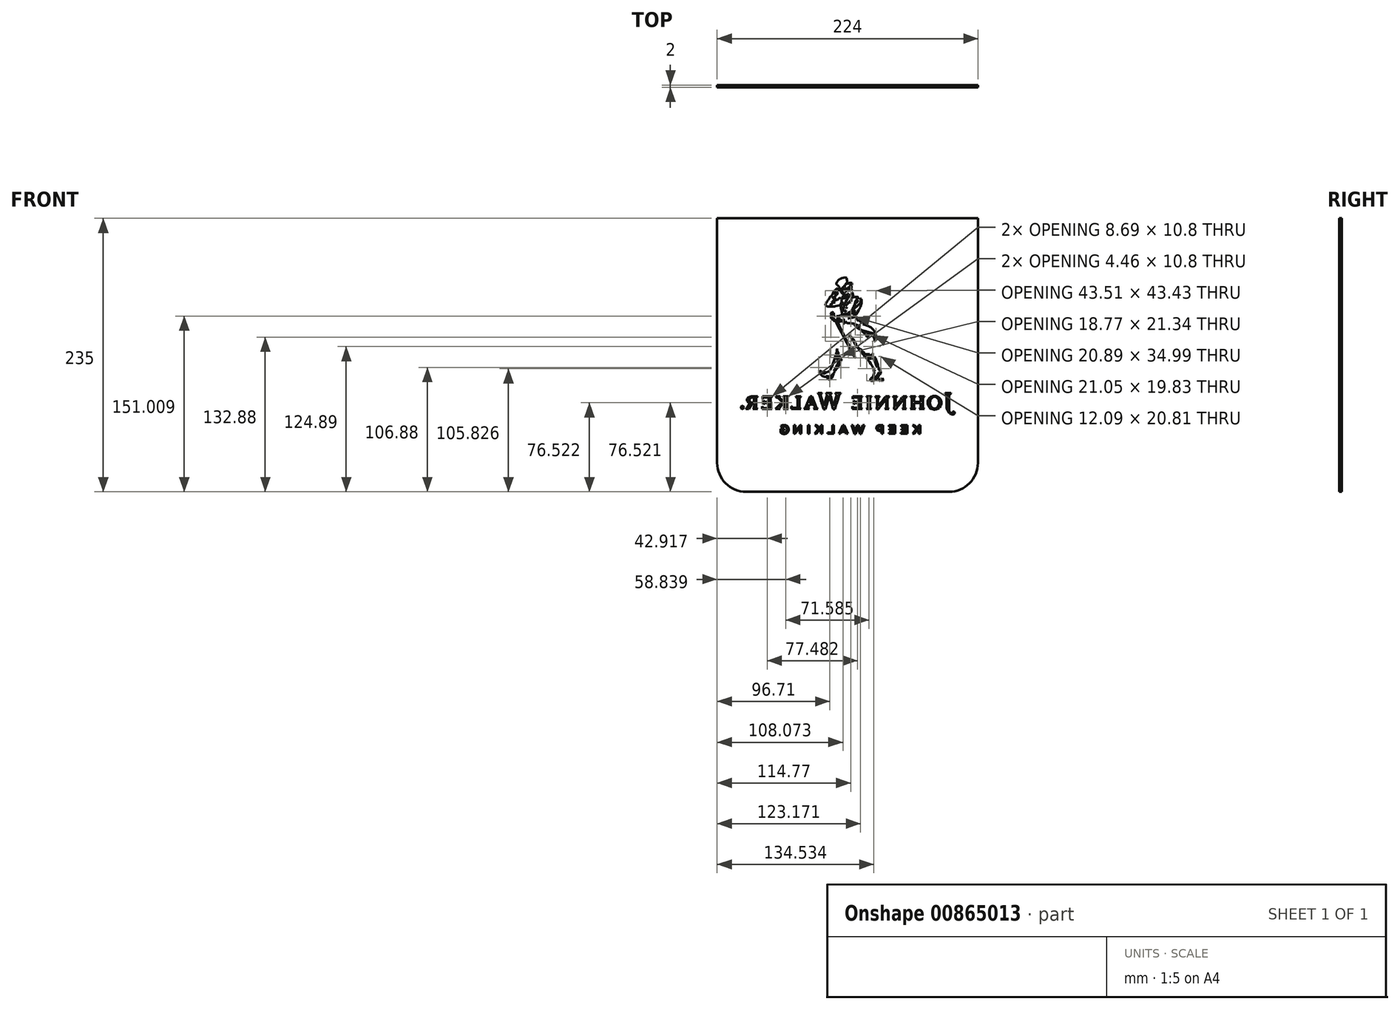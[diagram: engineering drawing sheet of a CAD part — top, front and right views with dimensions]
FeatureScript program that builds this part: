
annotation { "Feature Type Name" : "Feature", "Feature Type Description" : "" }
export const myFeature = defineFeature(function(context is Context, id is Id, definition is map)
    precondition{}
    {
        {
            var Q0;
            Q0=qCreatedBy(makeId("Front.planeOp"),FACE);
            var sketch = newSketch(context, id + "F0", { "sketchPlane" : qUnion([Q0])});
            skLineSegment(sketch, "E0", {"start": v(0.13, 0) * mm, "end": v(-86.87, 0) * mm});
            skLineSegment(sketch, "E1", {"start": v(0.13, 0) * mm, "end": v(87.13, 0) * mm});
            skLineSegment(sketch, "E2", {"start": v(0.13, 235) * mm, "end": v(-111.87, 235) * mm});
            skLineSegment(sketch, "E3", {"start": v(-111.87, 235) * mm, "end": v(-111.87, 25) * mm});
            skLineSegment(sketch, "E4", {"start": v(0.13, 235) * mm, "end": v(112.13, 235) * mm});
            skLineSegment(sketch, "E5", {"start": v(112.13, 235) * mm, "end": v(112.13, 25) * mm});
            skArc(sketch, "E6", {"start": v(-111.87, 25) * mm, "mid": v(-104.54, 7.32) * mm, "end": v(-86.87, 0) * mm});
            skArc(sketch, "E7", {"start": v(87.13, 0) * mm, "mid": v(104.81, 7.32) * mm, "end": v(112.13, 25) * mm});
            skSolve(sketch);
        }
        {
            var Q0;
            Q0=qCreatedBy(makeId("Front.planeOp"),FACE);
            var sketch = newSketch(context, id + "F1", { "sketchPlane" : qUnion([Q0])});
            skLineSegment(sketch, "E8", {"start": v(-58.86, 54.13) * mm, "end": v(-55.76, 57.34) * mm});
            skLineSegment(sketch, "E9", {"start": v(-55.76, 57.34) * mm, "end": v(-57.37, 57.34) * mm});
            skLineSegment(sketch, "E10", {"start": v(-57.37, 57.34) * mm, "end": v(-60.91, 53.59) * mm});
            skLineSegment(sketch, "E11", {"start": v(-60.91, 53.59) * mm, "end": v(-60.91, 57.34) * mm});
            skLineSegment(sketch, "E12", {"start": v(-60.91, 57.34) * mm, "end": v(-62.22, 57.34) * mm});
            skLineSegment(sketch, "E13", {"start": v(-62.22, 57.34) * mm, "end": v(-62.22, 49.88) * mm});
            skLineSegment(sketch, "E14", {"start": v(-62.22, 49.88) * mm, "end": v(-60.91, 49.88) * mm});
            skLineSegment(sketch, "E15", {"start": v(-60.91, 49.88) * mm, "end": v(-60.91, 52.04) * mm});
            skLineSegment(sketch, "E16", {"start": v(-60.91, 52.04) * mm, "end": v(-59.75, 53.24) * mm});
            skLineSegment(sketch, "E17", {"start": v(-59.75, 53.24) * mm, "end": v(-57.2, 49.88) * mm});
            skLineSegment(sketch, "E18", {"start": v(-57.2, 49.88) * mm, "end": v(-55.62, 49.88) * mm});
            skLineSegment(sketch, "E19", {"start": v(-55.62, 49.88) * mm, "end": v(-58.86, 54.13) * mm});
            skLineSegment(sketch, "E20", {"start": v(-45.72, 57.34) * mm, "end": v(-51.25, 57.34) * mm});
            skLineSegment(sketch, "E21", {"start": v(-51.25, 57.34) * mm, "end": v(-51.25, 49.88) * mm});
            skLineSegment(sketch, "E22", {"start": v(-51.25, 49.88) * mm, "end": v(-45.67, 49.88) * mm});
            skLineSegment(sketch, "E23", {"start": v(-45.67, 49.88) * mm, "end": v(-45.67, 51.05) * mm});
            skLineSegment(sketch, "E24", {"start": v(-45.67, 51.05) * mm, "end": v(-49.94, 51.05) * mm});
            skLineSegment(sketch, "E25", {"start": v(-49.94, 51.05) * mm, "end": v(-49.94, 53.06) * mm});
            skLineSegment(sketch, "E26", {"start": v(-49.94, 53.06) * mm, "end": v(-46.2, 53.06) * mm});
            skLineSegment(sketch, "E27", {"start": v(-46.2, 53.06) * mm, "end": v(-46.2, 54.23) * mm});
            skLineSegment(sketch, "E28", {"start": v(-46.2, 54.23) * mm, "end": v(-49.94, 54.23) * mm});
            skLineSegment(sketch, "E29", {"start": v(-49.94, 54.23) * mm, "end": v(-49.94, 56.17) * mm});
            skLineSegment(sketch, "E30", {"start": v(-49.94, 56.17) * mm, "end": v(-45.72, 56.17) * mm});
            skLineSegment(sketch, "E31", {"start": v(-45.72, 56.17) * mm, "end": v(-45.72, 57.34) * mm});
            skLineSegment(sketch, "E32", {"start": v(-35.3, 57.34) * mm, "end": v(-40.82, 57.34) * mm});
            skLineSegment(sketch, "E33", {"start": v(-40.82, 57.34) * mm, "end": v(-40.82, 49.88) * mm});
            skLineSegment(sketch, "E34", {"start": v(-40.82, 49.88) * mm, "end": v(-35.24, 49.88) * mm});
            skLineSegment(sketch, "E35", {"start": v(-35.24, 49.88) * mm, "end": v(-35.24, 51.05) * mm});
            skLineSegment(sketch, "E36", {"start": v(-35.24, 51.05) * mm, "end": v(-39.52, 51.05) * mm});
            skLineSegment(sketch, "E37", {"start": v(-39.52, 51.05) * mm, "end": v(-39.52, 53.06) * mm});
            skLineSegment(sketch, "E38", {"start": v(-39.52, 53.06) * mm, "end": v(-35.77, 53.06) * mm});
            skLineSegment(sketch, "E39", {"start": v(-35.77, 53.06) * mm, "end": v(-35.77, 54.23) * mm});
            skLineSegment(sketch, "E40", {"start": v(-35.77, 54.23) * mm, "end": v(-39.52, 54.23) * mm});
            skLineSegment(sketch, "E41", {"start": v(-39.52, 54.23) * mm, "end": v(-39.52, 56.17) * mm});
            skLineSegment(sketch, "E42", {"start": v(-39.52, 56.17) * mm, "end": v(-35.3, 56.17) * mm});
            skLineSegment(sketch, "E43", {"start": v(-35.3, 56.17) * mm, "end": v(-35.3, 57.34) * mm});
            skLineSegment(sketch, "E44", {"start": v(-24.63, 54.83) * mm, "end": v(-24.63, 55.1) * mm});
            skLineSegment(sketch, "E45", {"start": v(-24.63, 55.1) * mm, "end": v(-24.83, 55.87) * mm});
            skLineSegment(sketch, "E46", {"start": v(-24.83, 55.87) * mm, "end": v(-25.4, 56.66) * mm});
            skLineSegment(sketch, "E47", {"start": v(-25.4, 56.66) * mm, "end": v(-26.28, 57.16) * mm});
            skLineSegment(sketch, "E48", {"start": v(-26.28, 57.16) * mm, "end": v(-27.17, 57.34) * mm});
            skLineSegment(sketch, "E49", {"start": v(-27.17, 57.34) * mm, "end": v(-27.46, 57.34) * mm});
            skLineSegment(sketch, "E50", {"start": v(-27.46, 57.34) * mm, "end": v(-30.4, 57.34) * mm});
            skLineSegment(sketch, "E51", {"start": v(-30.4, 57.34) * mm, "end": v(-30.4, 49.88) * mm});
            skLineSegment(sketch, "E52", {"start": v(-30.4, 49.88) * mm, "end": v(-29.09, 49.88) * mm});
            skLineSegment(sketch, "E53", {"start": v(-29.09, 49.88) * mm, "end": v(-29.09, 52.28) * mm});
            skLineSegment(sketch, "E54", {"start": v(-29.09, 52.28) * mm, "end": v(-27.6, 52.28) * mm});
            skLineSegment(sketch, "E55", {"start": v(-27.6, 52.28) * mm, "end": v(-27.32, 52.28) * mm});
            skLineSegment(sketch, "E56", {"start": v(-27.32, 52.28) * mm, "end": v(-26.45, 52.44) * mm});
            skLineSegment(sketch, "E57", {"start": v(-26.45, 52.44) * mm, "end": v(-25.5, 52.93) * mm});
            skLineSegment(sketch, "E58", {"start": v(-25.5, 52.93) * mm, "end": v(-24.86, 53.73) * mm});
            skLineSegment(sketch, "E59", {"start": v(-24.86, 53.73) * mm, "end": v(-24.63, 54.56) * mm});
            skLineSegment(sketch, "E60", {"start": v(-24.63, 54.56) * mm, "end": v(-24.63, 54.83) * mm});
            skLineSegment(sketch, "E61", {"start": v(-25.96, 54.8) * mm, "end": v(-25.96, 54.67) * mm});
            skLineSegment(sketch, "E62", {"start": v(-25.96, 54.67) * mm, "end": v(-26.07, 54.26) * mm});
            skLineSegment(sketch, "E63", {"start": v(-26.07, 54.26) * mm, "end": v(-26.39, 53.83) * mm});
            skLineSegment(sketch, "E64", {"start": v(-26.39, 53.83) * mm, "end": v(-26.9, 53.56) * mm});
            skLineSegment(sketch, "E65", {"start": v(-26.9, 53.56) * mm, "end": v(-27.4, 53.46) * mm});
            skLineSegment(sketch, "E66", {"start": v(-27.4, 53.46) * mm, "end": v(-27.57, 53.46) * mm});
            skLineSegment(sketch, "E67", {"start": v(-27.57, 53.46) * mm, "end": v(-29.09, 53.46) * mm});
            skLineSegment(sketch, "E68", {"start": v(-29.09, 53.46) * mm, "end": v(-29.09, 56.14) * mm});
            skLineSegment(sketch, "E69", {"start": v(-29.09, 56.14) * mm, "end": v(-27.57, 56.14) * mm});
            skLineSegment(sketch, "E70", {"start": v(-27.57, 56.14) * mm, "end": v(-27.4, 56.14) * mm});
            skLineSegment(sketch, "E71", {"start": v(-27.4, 56.14) * mm, "end": v(-26.9, 56.06) * mm});
            skLineSegment(sketch, "E72", {"start": v(-26.9, 56.06) * mm, "end": v(-26.4, 55.8) * mm});
            skLineSegment(sketch, "E73", {"start": v(-26.4, 55.8) * mm, "end": v(-26.07, 55.39) * mm});
            skLineSegment(sketch, "E74", {"start": v(-26.07, 55.39) * mm, "end": v(-25.96, 54.95) * mm});
            skLineSegment(sketch, "E75", {"start": v(-25.96, 54.95) * mm, "end": v(-25.96, 54.8) * mm});
            skLineSegment(sketch, "E76", {"start": v(-11.08, 51.8) * mm, "end": v(-12.86, 57.34) * mm});
            skLineSegment(sketch, "E77", {"start": v(-12.86, 57.34) * mm, "end": v(-14.27, 57.34) * mm});
            skLineSegment(sketch, "E78", {"start": v(-14.27, 57.34) * mm, "end": v(-11.68, 49.83) * mm});
            skLineSegment(sketch, "E79", {"start": v(-11.68, 49.83) * mm, "end": v(-10.55, 49.83) * mm});
            skLineSegment(sketch, "E80", {"start": v(-10.55, 49.83) * mm, "end": v(-8.71, 55.18) * mm});
            skLineSegment(sketch, "E81", {"start": v(-8.71, 55.18) * mm, "end": v(-6.88, 49.83) * mm});
            skLineSegment(sketch, "E82", {"start": v(-6.88, 49.83) * mm, "end": v(-5.75, 49.83) * mm});
            skLineSegment(sketch, "E83", {"start": v(-5.75, 49.83) * mm, "end": v(-3.15, 57.34) * mm});
            skLineSegment(sketch, "E84", {"start": v(-3.15, 57.34) * mm, "end": v(-4.53, 57.34) * mm});
            skLineSegment(sketch, "E85", {"start": v(-4.53, 57.34) * mm, "end": v(-6.3, 51.8) * mm});
            skLineSegment(sketch, "E86", {"start": v(-6.3, 51.8) * mm, "end": v(-8.14, 57.36) * mm});
            skLineSegment(sketch, "E87", {"start": v(-8.14, 57.36) * mm, "end": v(-9.25, 57.36) * mm});
            skLineSegment(sketch, "E88", {"start": v(-9.25, 57.36) * mm, "end": v(-11.08, 51.8) * mm});
            skLineSegment(sketch, "E89", {"start": v(4.31, 57.39) * mm, "end": v(3.1, 57.39) * mm});
            skLineSegment(sketch, "E90", {"start": v(3.1, 57.39) * mm, "end": v(-0.18, 49.88) * mm});
            skLineSegment(sketch, "E91", {"start": v(-0.18, 49.88) * mm, "end": v(1.16, 49.88) * mm});
            skLineSegment(sketch, "E92", {"start": v(1.16, 49.88) * mm, "end": v(1.93, 51.68) * mm});
            skLineSegment(sketch, "E93", {"start": v(1.93, 51.68) * mm, "end": v(5.46, 51.68) * mm});
            skLineSegment(sketch, "E94", {"start": v(5.46, 51.68) * mm, "end": v(6.2, 49.88) * mm});
            skLineSegment(sketch, "E95", {"start": v(6.2, 49.88) * mm, "end": v(7.6, 49.88) * mm});
            skLineSegment(sketch, "E96", {"start": v(7.6, 49.88) * mm, "end": v(4.31, 57.39) * mm});
            skLineSegment(sketch, "E97", {"start": v(4.97, 52.84) * mm, "end": v(2.4, 52.84) * mm});
            skLineSegment(sketch, "E98", {"start": v(2.4, 52.84) * mm, "end": v(3.69, 55.82) * mm});
            skLineSegment(sketch, "E99", {"start": v(3.69, 55.82) * mm, "end": v(4.97, 52.84) * mm});
            skLineSegment(sketch, "E100", {"start": v(12.05, 49.88) * mm, "end": v(17.28, 49.88) * mm});
            skLineSegment(sketch, "E101", {"start": v(17.28, 49.88) * mm, "end": v(17.28, 51.07) * mm});
            skLineSegment(sketch, "E102", {"start": v(17.28, 51.07) * mm, "end": v(13.36, 51.07) * mm});
            skLineSegment(sketch, "E103", {"start": v(13.36, 51.07) * mm, "end": v(13.36, 57.34) * mm});
            skLineSegment(sketch, "E104", {"start": v(13.36, 57.34) * mm, "end": v(12.05, 57.34) * mm});
            skLineSegment(sketch, "E105", {"start": v(12.05, 57.34) * mm, "end": v(12.05, 49.88) * mm});
            skLineSegment(sketch, "E106", {"start": v(25.13, 54.13) * mm, "end": v(28.23, 57.34) * mm});
            skLineSegment(sketch, "E107", {"start": v(28.23, 57.34) * mm, "end": v(26.63, 57.34) * mm});
            skLineSegment(sketch, "E108", {"start": v(26.63, 57.34) * mm, "end": v(23.08, 53.59) * mm});
            skLineSegment(sketch, "E109", {"start": v(23.08, 53.59) * mm, "end": v(23.08, 57.34) * mm});
            skLineSegment(sketch, "E110", {"start": v(23.08, 57.34) * mm, "end": v(21.77, 57.34) * mm});
            skLineSegment(sketch, "E111", {"start": v(21.77, 57.34) * mm, "end": v(21.77, 49.88) * mm});
            skLineSegment(sketch, "E112", {"start": v(21.77, 49.88) * mm, "end": v(23.08, 49.88) * mm});
            skLineSegment(sketch, "E113", {"start": v(23.08, 49.88) * mm, "end": v(23.08, 52.04) * mm});
            skLineSegment(sketch, "E114", {"start": v(23.08, 52.04) * mm, "end": v(24.24, 53.24) * mm});
            skLineSegment(sketch, "E115", {"start": v(24.24, 53.24) * mm, "end": v(26.79, 49.88) * mm});
            skLineSegment(sketch, "E116", {"start": v(26.79, 49.88) * mm, "end": v(28.37, 49.88) * mm});
            skLineSegment(sketch, "E117", {"start": v(28.37, 49.88) * mm, "end": v(25.13, 54.13) * mm});
            skLineSegment(sketch, "E118", {"start": v(33, 49.88) * mm, "end": v(34.31, 49.88) * mm});
            skLineSegment(sketch, "E119", {"start": v(34.31, 49.88) * mm, "end": v(34.31, 57.34) * mm});
            skLineSegment(sketch, "E120", {"start": v(34.31, 57.34) * mm, "end": v(33, 57.34) * mm});
            skLineSegment(sketch, "E121", {"start": v(33, 57.34) * mm, "end": v(33, 49.88) * mm});
            skLineSegment(sketch, "E122", {"start": v(44.97, 52.18) * mm, "end": v(40.98, 57.34) * mm});
            skLineSegment(sketch, "E123", {"start": v(40.98, 57.34) * mm, "end": v(39.76, 57.34) * mm});
            skLineSegment(sketch, "E124", {"start": v(39.76, 57.34) * mm, "end": v(39.76, 49.88) * mm});
            skLineSegment(sketch, "E125", {"start": v(39.76, 49.88) * mm, "end": v(41.05, 49.88) * mm});
            skLineSegment(sketch, "E126", {"start": v(41.05, 49.88) * mm, "end": v(41.05, 55.18) * mm});
            skLineSegment(sketch, "E127", {"start": v(41.05, 55.18) * mm, "end": v(45.16, 49.88) * mm});
            skLineSegment(sketch, "E128", {"start": v(45.16, 49.88) * mm, "end": v(46.26, 49.88) * mm});
            skLineSegment(sketch, "E129", {"start": v(46.26, 49.88) * mm, "end": v(46.26, 57.34) * mm});
            skLineSegment(sketch, "E130", {"start": v(46.26, 57.34) * mm, "end": v(44.97, 57.34) * mm});
            skLineSegment(sketch, "E131", {"start": v(44.97, 57.34) * mm, "end": v(44.97, 52.18) * mm});
            skLineSegment(sketch, "E132", {"start": v(57.65, 50.91) * mm, "end": v(57.65, 54.05) * mm});
            skLineSegment(sketch, "E133", {"start": v(57.65, 54.05) * mm, "end": v(54.48, 54.05) * mm});
            skLineSegment(sketch, "E134", {"start": v(54.48, 54.05) * mm, "end": v(54.48, 52.9) * mm});
            skLineSegment(sketch, "E135", {"start": v(54.48, 52.9) * mm, "end": v(56.39, 52.9) * mm});
            skLineSegment(sketch, "E136", {"start": v(56.39, 52.9) * mm, "end": v(56.39, 51.51) * mm});
            skLineSegment(sketch, "E137", {"start": v(56.39, 51.51) * mm, "end": v(56.27, 51.43) * mm});
            skLineSegment(sketch, "E138", {"start": v(56.27, 51.43) * mm, "end": v(55.58, 51.1) * mm});
            skLineSegment(sketch, "E139", {"start": v(55.58, 51.1) * mm, "end": v(54.83, 50.95) * mm});
            skLineSegment(sketch, "E140", {"start": v(54.83, 50.95) * mm, "end": v(54.59, 50.95) * mm});
            skLineSegment(sketch, "E141", {"start": v(54.59, 50.95) * mm, "end": v(54.33, 50.95) * mm});
            skLineSegment(sketch, "E142", {"start": v(54.33, 50.95) * mm, "end": v(53.55, 51.15) * mm});
            skLineSegment(sketch, "E143", {"start": v(53.55, 51.15) * mm, "end": v(52.75, 51.7) * mm});
            skLineSegment(sketch, "E144", {"start": v(52.75, 51.7) * mm, "end": v(52.23, 52.55) * mm});
            skLineSegment(sketch, "E145", {"start": v(52.23, 52.55) * mm, "end": v(52.05, 53.35) * mm});
            skLineSegment(sketch, "E146", {"start": v(52.05, 53.35) * mm, "end": v(52.05, 53.62) * mm});
            skLineSegment(sketch, "E147", {"start": v(52.05, 53.62) * mm, "end": v(52.05, 53.88) * mm});
            skLineSegment(sketch, "E148", {"start": v(52.05, 53.88) * mm, "end": v(52.23, 54.64) * mm});
            skLineSegment(sketch, "E149", {"start": v(52.23, 54.64) * mm, "end": v(52.74, 55.49) * mm});
            skLineSegment(sketch, "E150", {"start": v(52.74, 55.49) * mm, "end": v(53.5, 56.05) * mm});
            skLineSegment(sketch, "E151", {"start": v(53.5, 56.05) * mm, "end": v(54.23, 56.26) * mm});
            skLineSegment(sketch, "E152", {"start": v(54.23, 56.26) * mm, "end": v(54.47, 56.26) * mm});
            skLineSegment(sketch, "E153", {"start": v(54.47, 56.26) * mm, "end": v(54.76, 56.26) * mm});
            skLineSegment(sketch, "E154", {"start": v(54.76, 56.26) * mm, "end": v(55.65, 56.05) * mm});
            skLineSegment(sketch, "E155", {"start": v(55.65, 56.05) * mm, "end": v(56.41, 55.59) * mm});
            skLineSegment(sketch, "E156", {"start": v(56.41, 55.59) * mm, "end": v(56.56, 55.46) * mm});
            skLineSegment(sketch, "E157", {"start": v(56.56, 55.46) * mm, "end": v(57.38, 56.46) * mm});
            skLineSegment(sketch, "E158", {"start": v(57.38, 56.46) * mm, "end": v(57.2, 56.62) * mm});
            skLineSegment(sketch, "E159", {"start": v(57.2, 56.62) * mm, "end": v(56.15, 57.2) * mm});
            skLineSegment(sketch, "E160", {"start": v(56.15, 57.2) * mm, "end": v(54.93, 57.47) * mm});
            skLineSegment(sketch, "E161", {"start": v(54.93, 57.47) * mm, "end": v(54.52, 57.47) * mm});
            skLineSegment(sketch, "E162", {"start": v(54.52, 57.47) * mm, "end": v(54.13, 57.47) * mm});
            skLineSegment(sketch, "E163", {"start": v(54.13, 57.47) * mm, "end": v(52.97, 57.16) * mm});
            skLineSegment(sketch, "E164", {"start": v(52.97, 57.16) * mm, "end": v(51.76, 56.32) * mm});
            skLineSegment(sketch, "E165", {"start": v(51.76, 56.32) * mm, "end": v(50.96, 55.09) * mm});
            skLineSegment(sketch, "E166", {"start": v(50.96, 55.09) * mm, "end": v(50.68, 53.97) * mm});
            skLineSegment(sketch, "E167", {"start": v(50.68, 53.97) * mm, "end": v(50.68, 53.6) * mm});
            skLineSegment(sketch, "E168", {"start": v(50.68, 53.6) * mm, "end": v(50.68, 53.22) * mm});
            skLineSegment(sketch, "E169", {"start": v(50.68, 53.22) * mm, "end": v(50.95, 52.08) * mm});
            skLineSegment(sketch, "E170", {"start": v(50.95, 52.08) * mm, "end": v(51.73, 50.86) * mm});
            skLineSegment(sketch, "E171", {"start": v(51.73, 50.86) * mm, "end": v(52.95, 50.05) * mm});
            skLineSegment(sketch, "E172", {"start": v(52.95, 50.05) * mm, "end": v(54.14, 49.76) * mm});
            skLineSegment(sketch, "E173", {"start": v(54.14, 49.76) * mm, "end": v(54.54, 49.76) * mm});
            skLineSegment(sketch, "E174", {"start": v(54.54, 49.76) * mm, "end": v(54.99, 49.76) * mm});
            skLineSegment(sketch, "E175", {"start": v(54.99, 49.76) * mm, "end": v(56.32, 50.1) * mm});
            skLineSegment(sketch, "E176", {"start": v(56.32, 50.1) * mm, "end": v(57.47, 50.76) * mm});
            skLineSegment(sketch, "E177", {"start": v(57.47, 50.76) * mm, "end": v(57.65, 50.91) * mm});
            skLineSegment(sketch, "E178", {"start": v(-27.51, 81.88) * mm, "end": v(-26.05, 80.76) * mm});
            skLineSegment(sketch, "E179", {"start": v(-26.05, 80.76) * mm, "end": v(-26.05, 80.5) * mm});
            skLineSegment(sketch, "E180", {"start": v(-26.05, 80.5) * mm, "end": v(-26, 77.76) * mm});
            skLineSegment(sketch, "E181", {"start": v(-26, 77.76) * mm, "end": v(-26, 77.46) * mm});
            skLineSegment(sketch, "E182", {"start": v(-26, 77.46) * mm, "end": v(-26, 77.16) * mm});
            skLineSegment(sketch, "E183", {"start": v(-26, 77.16) * mm, "end": v(-25.98, 74.54) * mm});
            skLineSegment(sketch, "E184", {"start": v(-25.98, 74.54) * mm, "end": v(-25.98, 73.67) * mm});
            skLineSegment(sketch, "E185", {"start": v(-25.98, 73.67) * mm, "end": v(-26.2, 73.96) * mm});
            skLineSegment(sketch, "E186", {"start": v(-26.2, 73.96) * mm, "end": v(-27.25, 75.3) * mm});
            skLineSegment(sketch, "E187", {"start": v(-27.25, 75.3) * mm, "end": v(-28.21, 76.5) * mm});
            skLineSegment(sketch, "E188", {"start": v(-28.21, 76.5) * mm, "end": v(-28.4, 76.74) * mm});
            skLineSegment(sketch, "E189", {"start": v(-28.4, 76.74) * mm, "end": v(-28.57, 76.96) * mm});
            skLineSegment(sketch, "E190", {"start": v(-28.57, 76.96) * mm, "end": v(-30.17, 78.96) * mm});
            skLineSegment(sketch, "E191", {"start": v(-30.17, 78.96) * mm, "end": v(-30.3, 79.12) * mm});
            skLineSegment(sketch, "E192", {"start": v(-30.3, 79.12) * mm, "end": v(-30.45, 79.3) * mm});
            skLineSegment(sketch, "E193", {"start": v(-30.45, 79.3) * mm, "end": v(-31.63, 80.77) * mm});
            skLineSegment(sketch, "E194", {"start": v(-31.63, 80.77) * mm, "end": v(-31.72, 80.9) * mm});
            skLineSegment(sketch, "E195", {"start": v(-31.72, 80.9) * mm, "end": v(-31.82, 81) * mm});
            skLineSegment(sketch, "E196", {"start": v(-31.82, 81) * mm, "end": v(-32.2, 81.51) * mm});
            skLineSegment(sketch, "E197", {"start": v(-32.2, 81.51) * mm, "end": v(-32.48, 81.93) * mm});
            skLineSegment(sketch, "E198", {"start": v(-32.48, 81.93) * mm, "end": v(-32.52, 82) * mm});
            skLineSegment(sketch, "E199", {"start": v(-32.52, 82) * mm, "end": v(-35.74, 82) * mm});
            skLineSegment(sketch, "E200", {"start": v(-35.74, 82) * mm, "end": v(-35.74, 81.88) * mm});
            skLineSegment(sketch, "E201", {"start": v(-35.74, 81.88) * mm, "end": v(-34.22, 80.8) * mm});
            skLineSegment(sketch, "E202", {"start": v(-34.22, 80.8) * mm, "end": v(-34.2, 79.93) * mm});
            skLineSegment(sketch, "E203", {"start": v(-34.2, 79.93) * mm, "end": v(-34.14, 76.09) * mm});
            skLineSegment(sketch, "E204", {"start": v(-34.14, 76.09) * mm, "end": v(-34.2, 72.88) * mm});
            skLineSegment(sketch, "E205", {"start": v(-34.2, 72.88) * mm, "end": v(-34.22, 72.34) * mm});
            skLineSegment(sketch, "E206", {"start": v(-34.22, 72.34) * mm, "end": v(-35.49, 71.3) * mm});
            skLineSegment(sketch, "E207", {"start": v(-35.49, 71.3) * mm, "end": v(-35.49, 71.15) * mm});
            skLineSegment(sketch, "E208", {"start": v(-35.49, 71.15) * mm, "end": v(-31.79, 71.15) * mm});
            skLineSegment(sketch, "E209", {"start": v(-31.79, 71.15) * mm, "end": v(-31.79, 71.3) * mm});
            skLineSegment(sketch, "E210", {"start": v(-31.79, 71.3) * mm, "end": v(-33.18, 72.34) * mm});
            skLineSegment(sketch, "E211", {"start": v(-33.18, 72.34) * mm, "end": v(-33.18, 72.34) * mm});
            skLineSegment(sketch, "E212", {"start": v(-33.18, 72.34) * mm, "end": v(-33.2, 72.97) * mm});
            skLineSegment(sketch, "E213", {"start": v(-33.2, 72.97) * mm, "end": v(-33.3, 78.1) * mm});
            skLineSegment(sketch, "E214", {"start": v(-33.3, 78.1) * mm, "end": v(-33.3, 79.8) * mm});
            skLineSegment(sketch, "E215", {"start": v(-33.3, 79.8) * mm, "end": v(-26.91, 71.77) * mm});
            skLineSegment(sketch, "E216", {"start": v(-26.91, 71.77) * mm, "end": v(-26.9, 71.74) * mm});
            skLineSegment(sketch, "E217", {"start": v(-26.9, 71.74) * mm, "end": v(-26.65, 71.44) * mm});
            skLineSegment(sketch, "E218", {"start": v(-26.65, 71.44) * mm, "end": v(-26.62, 71.4) * mm});
            skLineSegment(sketch, "E219", {"start": v(-26.62, 71.4) * mm, "end": v(-26.6, 71.38) * mm});
            skLineSegment(sketch, "E220", {"start": v(-26.6, 71.38) * mm, "end": v(-26.47, 71.16) * mm});
            skLineSegment(sketch, "E221", {"start": v(-26.47, 71.16) * mm, "end": v(-26.47, 71.1) * mm});
            skLineSegment(sketch, "E222", {"start": v(-26.47, 71.1) * mm, "end": v(-25, 71.1) * mm});
            skLineSegment(sketch, "E223", {"start": v(-25, 71.1) * mm, "end": v(-25.01, 71.44) * mm});
            skLineSegment(sketch, "E224", {"start": v(-25.01, 71.44) * mm, "end": v(-25.13, 74.54) * mm});
            skLineSegment(sketch, "E225", {"start": v(-25.13, 74.54) * mm, "end": v(-25.13, 75.58) * mm});
            skLineSegment(sketch, "E226", {"start": v(-25.13, 75.58) * mm, "end": v(-25.14, 75.97) * mm});
            skLineSegment(sketch, "E227", {"start": v(-25.14, 75.97) * mm, "end": v(-25.09, 80.3) * mm});
            skLineSegment(sketch, "E228", {"start": v(-25.09, 80.3) * mm, "end": v(-25.07, 80.76) * mm});
            skLineSegment(sketch, "E229", {"start": v(-25.07, 80.76) * mm, "end": v(-23.8, 81.88) * mm});
            skLineSegment(sketch, "E230", {"start": v(-23.8, 81.88) * mm, "end": v(-23.8, 82) * mm});
            skLineSegment(sketch, "E231", {"start": v(-23.8, 82) * mm, "end": v(-27.51, 82) * mm});
            skLineSegment(sketch, "E232", {"start": v(-27.51, 82) * mm, "end": v(-27.51, 81.88) * mm});
            skLineSegment(sketch, "E233", {"start": v(-17.36, 81) * mm, "end": v(-16.11, 81.88) * mm});
            skLineSegment(sketch, "E234", {"start": v(-16.11, 81.88) * mm, "end": v(-16.11, 81.99) * mm});
            skLineSegment(sketch, "E235", {"start": v(-16.11, 81.99) * mm, "end": v(-20.47, 81.99) * mm});
            skLineSegment(sketch, "E236", {"start": v(-20.47, 81.99) * mm, "end": v(-20.47, 81.88) * mm});
            skLineSegment(sketch, "E237", {"start": v(-20.47, 81.88) * mm, "end": v(-19.22, 81) * mm});
            skLineSegment(sketch, "E238", {"start": v(-19.22, 81) * mm, "end": v(-19.22, 80.28) * mm});
            skLineSegment(sketch, "E239", {"start": v(-19.22, 80.28) * mm, "end": v(-19.22, 72.97) * mm});
            skLineSegment(sketch, "E240", {"start": v(-19.22, 72.97) * mm, "end": v(-19.22, 72.23) * mm});
            skLineSegment(sketch, "E241", {"start": v(-19.22, 72.23) * mm, "end": v(-20.51, 71.32) * mm});
            skLineSegment(sketch, "E242", {"start": v(-20.51, 71.32) * mm, "end": v(-20.51, 71.19) * mm});
            skLineSegment(sketch, "E243", {"start": v(-20.51, 71.19) * mm, "end": v(-16.06, 71.19) * mm});
            skLineSegment(sketch, "E244", {"start": v(-16.06, 71.19) * mm, "end": v(-16.06, 71.32) * mm});
            skLineSegment(sketch, "E245", {"start": v(-16.06, 71.32) * mm, "end": v(-17.36, 72.23) * mm});
            skLineSegment(sketch, "E246", {"start": v(-17.36, 72.23) * mm, "end": v(-17.37, 72.93) * mm});
            skLineSegment(sketch, "E247", {"start": v(-17.37, 72.93) * mm, "end": v(-17.37, 80.24) * mm});
            skLineSegment(sketch, "E248", {"start": v(-17.37, 80.24) * mm, "end": v(-17.36, 81) * mm});
            skLineSegment(sketch, "E249", {"start": v(-5.1, 72.11) * mm, "end": v(-5.49, 72.1) * mm});
            skLineSegment(sketch, "E250", {"start": v(-5.49, 72.1) * mm, "end": v(-9.16, 72.1) * mm});
            skLineSegment(sketch, "E251", {"start": v(-9.16, 72.1) * mm, "end": v(-9.51, 72.11) * mm});
            skLineSegment(sketch, "E252", {"start": v(-9.51, 72.11) * mm, "end": v(-9.52, 72.47) * mm});
            skLineSegment(sketch, "E253", {"start": v(-9.52, 72.47) * mm, "end": v(-9.52, 76.02) * mm});
            skLineSegment(sketch, "E254", {"start": v(-9.52, 76.02) * mm, "end": v(-9.51, 76.37) * mm});
            skLineSegment(sketch, "E255", {"start": v(-9.51, 76.37) * mm, "end": v(-9.3, 76.38) * mm});
            skLineSegment(sketch, "E256", {"start": v(-9.3, 76.38) * mm, "end": v(-8.05, 76.4) * mm});
            skLineSegment(sketch, "E257", {"start": v(-8.05, 76.4) * mm, "end": v(-6.6, 76.4) * mm});
            skLineSegment(sketch, "E258", {"start": v(-6.6, 76.4) * mm, "end": v(-6.12, 76.4) * mm});
            skLineSegment(sketch, "E259", {"start": v(-6.12, 76.4) * mm, "end": v(-5.28, 75.17) * mm});
            skLineSegment(sketch, "E260", {"start": v(-5.28, 75.17) * mm, "end": v(-5.16, 75.17) * mm});
            skLineSegment(sketch, "E261", {"start": v(-5.16, 75.17) * mm, "end": v(-5.16, 78.51) * mm});
            skLineSegment(sketch, "E262", {"start": v(-5.16, 78.51) * mm, "end": v(-5.28, 78.51) * mm});
            skLineSegment(sketch, "E263", {"start": v(-5.28, 78.51) * mm, "end": v(-6.12, 77.25) * mm});
            skLineSegment(sketch, "E264", {"start": v(-6.12, 77.25) * mm, "end": v(-6.7, 77.25) * mm});
            skLineSegment(sketch, "E265", {"start": v(-6.7, 77.25) * mm, "end": v(-8.41, 77.27) * mm});
            skLineSegment(sketch, "E266", {"start": v(-8.41, 77.27) * mm, "end": v(-9.45, 77.3) * mm});
            skLineSegment(sketch, "E267", {"start": v(-9.45, 77.3) * mm, "end": v(-9.54, 77.3) * mm});
            skLineSegment(sketch, "E268", {"start": v(-9.54, 77.3) * mm, "end": v(-9.54, 77.45) * mm});
            skLineSegment(sketch, "E269", {"start": v(-9.54, 77.45) * mm, "end": v(-9.58, 78.72) * mm});
            skLineSegment(sketch, "E270", {"start": v(-9.58, 78.72) * mm, "end": v(-9.58, 79.14) * mm});
            skLineSegment(sketch, "E271", {"start": v(-9.58, 79.14) * mm, "end": v(-9.58, 79.62) * mm});
            skLineSegment(sketch, "E272", {"start": v(-9.58, 79.62) * mm, "end": v(-9.56, 80.88) * mm});
            skLineSegment(sketch, "E273", {"start": v(-9.56, 80.88) * mm, "end": v(-9.55, 81.04) * mm});
            skLineSegment(sketch, "E274", {"start": v(-9.55, 81.04) * mm, "end": v(-9.39, 81.06) * mm});
            skLineSegment(sketch, "E275", {"start": v(-9.39, 81.06) * mm, "end": v(-7.92, 81.1) * mm});
            skLineSegment(sketch, "E276", {"start": v(-7.92, 81.1) * mm, "end": v(-7.43, 81.1) * mm});
            skLineSegment(sketch, "E277", {"start": v(-7.43, 81.1) * mm, "end": v(-6.87, 81.1) * mm});
            skLineSegment(sketch, "E278", {"start": v(-6.87, 81.1) * mm, "end": v(-5.6, 81.1) * mm});
            skLineSegment(sketch, "E279", {"start": v(-5.6, 81.1) * mm, "end": v(-5.16, 81.1) * mm});
            skLineSegment(sketch, "E280", {"start": v(-5.16, 81.1) * mm, "end": v(-4.26, 79.85) * mm});
            skLineSegment(sketch, "E281", {"start": v(-4.26, 79.85) * mm, "end": v(-4.14, 79.85) * mm});
            skLineSegment(sketch, "E282", {"start": v(-4.14, 79.85) * mm, "end": v(-4.14, 82) * mm});
            skLineSegment(sketch, "E283", {"start": v(-4.14, 82) * mm, "end": v(-12.6, 82) * mm});
            skLineSegment(sketch, "E284", {"start": v(-12.6, 82) * mm, "end": v(-12.6, 81.88) * mm});
            skLineSegment(sketch, "E285", {"start": v(-12.6, 81.88) * mm, "end": v(-11.37, 81) * mm});
            skLineSegment(sketch, "E286", {"start": v(-11.37, 81) * mm, "end": v(-11.37, 80.37) * mm});
            skLineSegment(sketch, "E287", {"start": v(-11.37, 80.37) * mm, "end": v(-11.35, 76.92) * mm});
            skLineSegment(sketch, "E288", {"start": v(-11.35, 76.92) * mm, "end": v(-11.37, 73.06) * mm});
            skLineSegment(sketch, "E289", {"start": v(-11.37, 73.06) * mm, "end": v(-11.37, 72.23) * mm});
            skLineSegment(sketch, "E290", {"start": v(-11.37, 72.23) * mm, "end": v(-12.6, 71.33) * mm});
            skLineSegment(sketch, "E291", {"start": v(-12.6, 71.33) * mm, "end": v(-12.6, 71.19) * mm});
            skLineSegment(sketch, "E292", {"start": v(-12.6, 71.19) * mm, "end": v(-3.92, 71.19) * mm});
            skLineSegment(sketch, "E293", {"start": v(-3.92, 71.19) * mm, "end": v(-3.92, 73.58) * mm});
            skLineSegment(sketch, "E294", {"start": v(-3.92, 73.58) * mm, "end": v(-4.04, 73.58) * mm});
            skLineSegment(sketch, "E295", {"start": v(-4.04, 73.58) * mm, "end": v(-5.1, 72.11) * mm});
            skLineSegment(sketch, "E296", {"start": v(-42.45, 81.88) * mm, "end": v(-41.02, 80.76) * mm});
            skLineSegment(sketch, "E297", {"start": v(-41.02, 80.76) * mm, "end": v(-41.01, 80.5) * mm});
            skLineSegment(sketch, "E298", {"start": v(-41.01, 80.5) * mm, "end": v(-40.98, 77.76) * mm});
            skLineSegment(sketch, "E299", {"start": v(-40.98, 77.76) * mm, "end": v(-40.97, 77.46) * mm});
            skLineSegment(sketch, "E300", {"start": v(-40.97, 77.46) * mm, "end": v(-40.97, 77.16) * mm});
            skLineSegment(sketch, "E301", {"start": v(-40.97, 77.16) * mm, "end": v(-40.95, 74.54) * mm});
            skLineSegment(sketch, "E302", {"start": v(-40.95, 74.54) * mm, "end": v(-40.95, 73.67) * mm});
            skLineSegment(sketch, "E303", {"start": v(-40.95, 73.67) * mm, "end": v(-41.17, 73.96) * mm});
            skLineSegment(sketch, "E304", {"start": v(-41.17, 73.96) * mm, "end": v(-43.15, 76.5) * mm});
            skLineSegment(sketch, "E305", {"start": v(-43.15, 76.5) * mm, "end": v(-43.33, 76.74) * mm});
            skLineSegment(sketch, "E306", {"start": v(-43.33, 76.74) * mm, "end": v(-43.52, 76.96) * mm});
            skLineSegment(sketch, "E307", {"start": v(-43.52, 76.96) * mm, "end": v(-45.14, 78.96) * mm});
            skLineSegment(sketch, "E308", {"start": v(-45.14, 78.96) * mm, "end": v(-45.28, 79.12) * mm});
            skLineSegment(sketch, "E309", {"start": v(-45.28, 79.12) * mm, "end": v(-45.42, 79.3) * mm});
            skLineSegment(sketch, "E310", {"start": v(-45.42, 79.3) * mm, "end": v(-46.58, 80.77) * mm});
            skLineSegment(sketch, "E311", {"start": v(-46.58, 80.77) * mm, "end": v(-46.67, 80.9) * mm});
            skLineSegment(sketch, "E312", {"start": v(-46.67, 80.9) * mm, "end": v(-46.77, 81) * mm});
            skLineSegment(sketch, "E313", {"start": v(-46.77, 81) * mm, "end": v(-47.15, 81.51) * mm});
            skLineSegment(sketch, "E314", {"start": v(-47.15, 81.51) * mm, "end": v(-47.43, 81.93) * mm});
            skLineSegment(sketch, "E315", {"start": v(-47.43, 81.93) * mm, "end": v(-47.47, 82) * mm});
            skLineSegment(sketch, "E316", {"start": v(-47.47, 82) * mm, "end": v(-50.68, 82) * mm});
            skLineSegment(sketch, "E317", {"start": v(-50.68, 82) * mm, "end": v(-50.68, 81.88) * mm});
            skLineSegment(sketch, "E318", {"start": v(-50.68, 81.88) * mm, "end": v(-49.18, 80.8) * mm});
            skLineSegment(sketch, "E319", {"start": v(-49.18, 80.8) * mm, "end": v(-49.15, 79.93) * mm});
            skLineSegment(sketch, "E320", {"start": v(-49.15, 79.93) * mm, "end": v(-49.1, 76.09) * mm});
            skLineSegment(sketch, "E321", {"start": v(-49.1, 76.09) * mm, "end": v(-49.15, 72.88) * mm});
            skLineSegment(sketch, "E322", {"start": v(-49.15, 72.88) * mm, "end": v(-49.18, 72.34) * mm});
            skLineSegment(sketch, "E323", {"start": v(-49.18, 72.34) * mm, "end": v(-50.43, 71.3) * mm});
            skLineSegment(sketch, "E324", {"start": v(-50.43, 71.3) * mm, "end": v(-50.43, 71.15) * mm});
            skLineSegment(sketch, "E325", {"start": v(-50.43, 71.15) * mm, "end": v(-46.74, 71.15) * mm});
            skLineSegment(sketch, "E326", {"start": v(-46.74, 71.15) * mm, "end": v(-46.74, 71.3) * mm});
            skLineSegment(sketch, "E327", {"start": v(-46.74, 71.3) * mm, "end": v(-48.13, 72.34) * mm});
            skLineSegment(sketch, "E328", {"start": v(-48.13, 72.34) * mm, "end": v(-48.12, 72.34) * mm});
            skLineSegment(sketch, "E329", {"start": v(-48.12, 72.34) * mm, "end": v(-48.15, 72.97) * mm});
            skLineSegment(sketch, "E330", {"start": v(-48.15, 72.97) * mm, "end": v(-48.26, 78.1) * mm});
            skLineSegment(sketch, "E331", {"start": v(-48.26, 78.1) * mm, "end": v(-48.26, 79.8) * mm});
            skLineSegment(sketch, "E332", {"start": v(-48.26, 79.8) * mm, "end": v(-41.86, 71.77) * mm});
            skLineSegment(sketch, "E333", {"start": v(-41.86, 71.77) * mm, "end": v(-41.83, 71.74) * mm});
            skLineSegment(sketch, "E334", {"start": v(-41.83, 71.74) * mm, "end": v(-41.6, 71.44) * mm});
            skLineSegment(sketch, "E335", {"start": v(-41.6, 71.44) * mm, "end": v(-41.57, 71.4) * mm});
            skLineSegment(sketch, "E336", {"start": v(-41.57, 71.4) * mm, "end": v(-41.55, 71.38) * mm});
            skLineSegment(sketch, "E337", {"start": v(-41.55, 71.38) * mm, "end": v(-41.42, 71.16) * mm});
            skLineSegment(sketch, "E338", {"start": v(-41.42, 71.16) * mm, "end": v(-41.42, 71.1) * mm});
            skLineSegment(sketch, "E339", {"start": v(-41.42, 71.1) * mm, "end": v(-39.95, 71.1) * mm});
            skLineSegment(sketch, "E340", {"start": v(-39.95, 71.1) * mm, "end": v(-39.97, 71.44) * mm});
            skLineSegment(sketch, "E341", {"start": v(-39.97, 71.44) * mm, "end": v(-40.1, 74.54) * mm});
            skLineSegment(sketch, "E342", {"start": v(-40.1, 74.54) * mm, "end": v(-40.1, 75.58) * mm});
            skLineSegment(sketch, "E343", {"start": v(-40.1, 75.58) * mm, "end": v(-40.1, 75.97) * mm});
            skLineSegment(sketch, "E344", {"start": v(-40.1, 75.97) * mm, "end": v(-40.04, 80.3) * mm});
            skLineSegment(sketch, "E345", {"start": v(-40.04, 80.3) * mm, "end": v(-40.02, 80.76) * mm});
            skLineSegment(sketch, "E346", {"start": v(-40.02, 80.76) * mm, "end": v(-38.76, 81.88) * mm});
            skLineSegment(sketch, "E347", {"start": v(-38.76, 81.88) * mm, "end": v(-38.76, 82) * mm});
            skLineSegment(sketch, "E348", {"start": v(-38.76, 82) * mm, "end": v(-42.45, 82) * mm});
            skLineSegment(sketch, "E349", {"start": v(-42.45, 82) * mm, "end": v(-42.45, 81.88) * mm});
            skLineSegment(sketch, "E350", {"start": v(22.12, 84.65) * mm, "end": v(22.17, 84.62) * mm});
            skLineSegment(sketch, "E351", {"start": v(22.17, 84.62) * mm, "end": v(22.7, 84.26) * mm});
            skLineSegment(sketch, "E352", {"start": v(22.7, 84.26) * mm, "end": v(22.75, 84.23) * mm});
            skLineSegment(sketch, "E353", {"start": v(22.75, 84.23) * mm, "end": v(22.8, 84.2) * mm});
            skLineSegment(sketch, "E354", {"start": v(22.8, 84.2) * mm, "end": v(23.3, 83.82) * mm});
            skLineSegment(sketch, "E355", {"start": v(23.3, 83.82) * mm, "end": v(23.35, 83.78) * mm});
            skLineSegment(sketch, "E356", {"start": v(23.35, 83.78) * mm, "end": v(23.25, 83.42) * mm});
            skLineSegment(sketch, "E357", {"start": v(23.25, 83.42) * mm, "end": v(22.34, 80.21) * mm});
            skLineSegment(sketch, "E358", {"start": v(22.34, 80.21) * mm, "end": v(22.26, 79.92) * mm});
            skLineSegment(sketch, "E359", {"start": v(22.26, 79.92) * mm, "end": v(22.18, 79.63) * mm});
            skLineSegment(sketch, "E360", {"start": v(22.18, 79.63) * mm, "end": v(21.46, 77.16) * mm});
            skLineSegment(sketch, "E361", {"start": v(21.46, 77.16) * mm, "end": v(21.4, 76.94) * mm});
            skLineSegment(sketch, "E362", {"start": v(21.4, 76.94) * mm, "end": v(21.33, 76.74) * mm});
            skLineSegment(sketch, "E363", {"start": v(21.33, 76.74) * mm, "end": v(20.84, 75.02) * mm});
            skLineSegment(sketch, "E364", {"start": v(20.84, 75.02) * mm, "end": v(20.8, 74.88) * mm});
            skLineSegment(sketch, "E365", {"start": v(20.8, 74.88) * mm, "end": v(20.77, 74.75) * mm});
            skLineSegment(sketch, "E366", {"start": v(20.77, 74.75) * mm, "end": v(20.63, 74.2) * mm});
            skLineSegment(sketch, "E367", {"start": v(20.63, 74.2) * mm, "end": v(20.54, 73.83) * mm});
            skLineSegment(sketch, "E368", {"start": v(20.54, 73.83) * mm, "end": v(20.53, 73.78) * mm});
            skLineSegment(sketch, "E369", {"start": v(20.53, 73.78) * mm, "end": v(17.53, 83.66) * mm});
            skLineSegment(sketch, "E370", {"start": v(17.53, 83.66) * mm, "end": v(17.58, 83.71) * mm});
            skLineSegment(sketch, "E371", {"start": v(17.58, 83.71) * mm, "end": v(18.07, 84.19) * mm});
            skLineSegment(sketch, "E372", {"start": v(18.07, 84.19) * mm, "end": v(18.12, 84.23) * mm});
            skLineSegment(sketch, "E373", {"start": v(18.12, 84.23) * mm, "end": v(18.17, 84.27) * mm});
            skLineSegment(sketch, "E374", {"start": v(18.17, 84.27) * mm, "end": v(18.64, 84.62) * mm});
            skLineSegment(sketch, "E375", {"start": v(18.64, 84.62) * mm, "end": v(18.68, 84.65) * mm});
            skLineSegment(sketch, "E376", {"start": v(18.68, 84.65) * mm, "end": v(18.68, 84.77) * mm});
            skLineSegment(sketch, "E377", {"start": v(18.68, 84.77) * mm, "end": v(13.9, 84.77) * mm});
            skLineSegment(sketch, "E378", {"start": v(13.9, 84.77) * mm, "end": v(13.9, 84.63) * mm});
            skLineSegment(sketch, "E379", {"start": v(13.9, 84.63) * mm, "end": v(15.1, 83.7) * mm});
            skLineSegment(sketch, "E380", {"start": v(15.1, 83.7) * mm, "end": v(15.02, 83.45) * mm});
            skLineSegment(sketch, "E381", {"start": v(15.02, 83.45) * mm, "end": v(14.26, 80.97) * mm});
            skLineSegment(sketch, "E382", {"start": v(14.26, 80.97) * mm, "end": v(14.2, 80.73) * mm});
            skLineSegment(sketch, "E383", {"start": v(14.2, 80.73) * mm, "end": v(14.12, 80.5) * mm});
            skLineSegment(sketch, "E384", {"start": v(14.12, 80.5) * mm, "end": v(13.48, 78.33) * mm});
            skLineSegment(sketch, "E385", {"start": v(13.48, 78.33) * mm, "end": v(13.42, 78.13) * mm});
            skLineSegment(sketch, "E386", {"start": v(13.42, 78.13) * mm, "end": v(13.36, 77.93) * mm});
            skLineSegment(sketch, "E387", {"start": v(13.36, 77.93) * mm, "end": v(12.8, 76.03) * mm});
            skLineSegment(sketch, "E388", {"start": v(12.8, 76.03) * mm, "end": v(12.76, 75.85) * mm});
            skLineSegment(sketch, "E389", {"start": v(12.76, 75.85) * mm, "end": v(12.7, 75.68) * mm});
            skLineSegment(sketch, "E390", {"start": v(12.7, 75.68) * mm, "end": v(12.23, 74) * mm});
            skLineSegment(sketch, "E391", {"start": v(12.23, 74) * mm, "end": v(12.19, 73.83) * mm});
            skLineSegment(sketch, "E392", {"start": v(12.19, 73.83) * mm, "end": v(9.36, 83.69) * mm});
            skLineSegment(sketch, "E393", {"start": v(9.36, 83.69) * mm, "end": v(10.52, 84.65) * mm});
            skLineSegment(sketch, "E394", {"start": v(10.52, 84.65) * mm, "end": v(10.52, 84.77) * mm});
            skLineSegment(sketch, "E395", {"start": v(10.52, 84.77) * mm, "end": v(5.92, 84.77) * mm});
            skLineSegment(sketch, "E396", {"start": v(5.92, 84.77) * mm, "end": v(5.92, 84.65) * mm});
            skLineSegment(sketch, "E397", {"start": v(5.92, 84.65) * mm, "end": v(5.97, 84.61) * mm});
            skLineSegment(sketch, "E398", {"start": v(5.97, 84.61) * mm, "end": v(6.39, 84.27) * mm});
            skLineSegment(sketch, "E399", {"start": v(6.39, 84.27) * mm, "end": v(6.42, 84.24) * mm});
            skLineSegment(sketch, "E400", {"start": v(6.42, 84.24) * mm, "end": v(6.45, 84.22) * mm});
            skLineSegment(sketch, "E401", {"start": v(6.45, 84.22) * mm, "end": v(6.73, 84) * mm});
            skLineSegment(sketch, "E402", {"start": v(6.73, 84) * mm, "end": v(6.75, 83.97) * mm});
            skLineSegment(sketch, "E403", {"start": v(6.75, 83.97) * mm, "end": v(6.77, 83.95) * mm});
            skLineSegment(sketch, "E404", {"start": v(6.77, 83.95) * mm, "end": v(6.94, 83.77) * mm});
            skLineSegment(sketch, "E405", {"start": v(6.94, 83.77) * mm, "end": v(6.95, 83.76) * mm});
            skLineSegment(sketch, "E406", {"start": v(6.95, 83.76) * mm, "end": v(6.96, 83.74) * mm});
            skLineSegment(sketch, "E407", {"start": v(6.96, 83.74) * mm, "end": v(7.06, 83.55) * mm});
            skLineSegment(sketch, "E408", {"start": v(7.06, 83.55) * mm, "end": v(7.06, 83.53) * mm});
            skLineSegment(sketch, "E409", {"start": v(7.06, 83.53) * mm, "end": v(7.1, 83.41) * mm});
            skLineSegment(sketch, "E410", {"start": v(7.1, 83.41) * mm, "end": v(7.33, 82.68) * mm});
            skLineSegment(sketch, "E411", {"start": v(7.33, 82.68) * mm, "end": v(7.63, 81.76) * mm});
            skLineSegment(sketch, "E412", {"start": v(7.63, 81.76) * mm, "end": v(7.7, 81.55) * mm});
            skLineSegment(sketch, "E413", {"start": v(7.7, 81.55) * mm, "end": v(7.77, 81.33) * mm});
            skLineSegment(sketch, "E414", {"start": v(7.77, 81.33) * mm, "end": v(8.57, 78.85) * mm});
            skLineSegment(sketch, "E415", {"start": v(8.57, 78.85) * mm, "end": v(8.66, 78.57) * mm});
            skLineSegment(sketch, "E416", {"start": v(8.66, 78.57) * mm, "end": v(8.75, 78.3) * mm});
            skLineSegment(sketch, "E417", {"start": v(8.75, 78.3) * mm, "end": v(9.73, 75.3) * mm});
            skLineSegment(sketch, "E418", {"start": v(9.73, 75.3) * mm, "end": v(9.84, 74.97) * mm});
            skLineSegment(sketch, "E419", {"start": v(9.84, 74.97) * mm, "end": v(9.94, 74.65) * mm});
            skLineSegment(sketch, "E420", {"start": v(9.94, 74.65) * mm, "end": v(10.97, 71.27) * mm});
            skLineSegment(sketch, "E421", {"start": v(10.97, 71.27) * mm, "end": v(11.08, 70.91) * mm});
            skLineSegment(sketch, "E422", {"start": v(11.08, 70.91) * mm, "end": v(12.6, 70.91) * mm});
            skLineSegment(sketch, "E423", {"start": v(12.6, 70.91) * mm, "end": v(12.59, 70.93) * mm});
            skLineSegment(sketch, "E424", {"start": v(12.59, 70.93) * mm, "end": v(12.57, 71.03) * mm});
            skLineSegment(sketch, "E425", {"start": v(12.57, 71.03) * mm, "end": v(12.57, 71.06) * mm});
            skLineSegment(sketch, "E426", {"start": v(12.57, 71.06) * mm, "end": v(12.57, 71.13) * mm});
            skLineSegment(sketch, "E427", {"start": v(12.57, 71.13) * mm, "end": v(12.6, 71.31) * mm});
            skLineSegment(sketch, "E428", {"start": v(12.6, 71.31) * mm, "end": v(12.6, 71.33) * mm});
            skLineSegment(sketch, "E429", {"start": v(12.6, 71.33) * mm, "end": v(12.6, 71.35) * mm});
            skLineSegment(sketch, "E430", {"start": v(12.6, 71.35) * mm, "end": v(12.66, 71.59) * mm});
            skLineSegment(sketch, "E431", {"start": v(12.66, 71.59) * mm, "end": v(12.67, 71.6) * mm});
            skLineSegment(sketch, "E432", {"start": v(12.67, 71.6) * mm, "end": v(12.68, 71.63) * mm});
            skLineSegment(sketch, "E433", {"start": v(12.68, 71.63) * mm, "end": v(12.75, 71.84) * mm});
            skLineSegment(sketch, "E434", {"start": v(12.75, 71.84) * mm, "end": v(12.76, 71.86) * mm});
            skLineSegment(sketch, "E435", {"start": v(12.76, 71.86) * mm, "end": v(12.79, 71.98) * mm});
            skLineSegment(sketch, "E436", {"start": v(12.79, 71.98) * mm, "end": v(13.13, 73.27) * mm});
            skLineSegment(sketch, "E437", {"start": v(13.13, 73.27) * mm, "end": v(13.17, 73.4) * mm});
            skLineSegment(sketch, "E438", {"start": v(13.17, 73.4) * mm, "end": v(13.2, 73.55) * mm});
            skLineSegment(sketch, "E439", {"start": v(13.2, 73.55) * mm, "end": v(13.6, 75.01) * mm});
            skLineSegment(sketch, "E440", {"start": v(13.6, 75.01) * mm, "end": v(13.65, 75.16) * mm});
            skLineSegment(sketch, "E441", {"start": v(13.65, 75.16) * mm, "end": v(13.69, 75.31) * mm});
            skLineSegment(sketch, "E442", {"start": v(13.69, 75.31) * mm, "end": v(14.13, 76.88) * mm});
            skLineSegment(sketch, "E443", {"start": v(14.13, 76.88) * mm, "end": v(14.17, 77.04) * mm});
            skLineSegment(sketch, "E444", {"start": v(14.17, 77.04) * mm, "end": v(14.22, 77.2) * mm});
            skLineSegment(sketch, "E445", {"start": v(14.22, 77.2) * mm, "end": v(14.67, 78.78) * mm});
            skLineSegment(sketch, "E446", {"start": v(14.67, 78.78) * mm, "end": v(14.72, 78.94) * mm});
            skLineSegment(sketch, "E447", {"start": v(14.72, 78.94) * mm, "end": v(14.76, 79.1) * mm});
            skLineSegment(sketch, "E448", {"start": v(14.76, 79.1) * mm, "end": v(15.2, 80.59) * mm});
            skLineSegment(sketch, "E449", {"start": v(15.2, 80.59) * mm, "end": v(15.24, 80.73) * mm});
            skLineSegment(sketch, "E450", {"start": v(15.24, 80.73) * mm, "end": v(15.28, 80.89) * mm});
            skLineSegment(sketch, "E451", {"start": v(15.28, 80.89) * mm, "end": v(15.69, 82.25) * mm});
            skLineSegment(sketch, "E452", {"start": v(15.69, 82.25) * mm, "end": v(15.72, 82.37) * mm});
            skLineSegment(sketch, "E453", {"start": v(15.72, 82.37) * mm, "end": v(19.31, 70.91) * mm});
            skLineSegment(sketch, "E454", {"start": v(19.31, 70.91) * mm, "end": v(20.76, 70.91) * mm});
            skLineSegment(sketch, "E455", {"start": v(20.76, 70.91) * mm, "end": v(20.78, 70.97) * mm});
            skLineSegment(sketch, "E456", {"start": v(20.78, 70.97) * mm, "end": v(20.9, 71.44) * mm});
            skLineSegment(sketch, "E457", {"start": v(20.9, 71.44) * mm, "end": v(21.08, 72.13) * mm});
            skLineSegment(sketch, "E458", {"start": v(21.08, 72.13) * mm, "end": v(21.13, 72.3) * mm});
            skLineSegment(sketch, "E459", {"start": v(21.13, 72.3) * mm, "end": v(21.17, 72.47) * mm});
            skLineSegment(sketch, "E460", {"start": v(21.17, 72.47) * mm, "end": v(21.46, 73.45) * mm});
            skLineSegment(sketch, "E461", {"start": v(21.46, 73.45) * mm, "end": v(21.81, 74.64) * mm});
            skLineSegment(sketch, "E462", {"start": v(21.81, 74.64) * mm, "end": v(21.9, 74.9) * mm});
            skLineSegment(sketch, "E463", {"start": v(21.9, 74.9) * mm, "end": v(21.98, 75.17) * mm});
            skLineSegment(sketch, "E464", {"start": v(21.98, 75.17) * mm, "end": v(22.42, 76.65) * mm});
            skLineSegment(sketch, "E465", {"start": v(22.42, 76.65) * mm, "end": v(22.93, 78.32) * mm});
            skLineSegment(sketch, "E466", {"start": v(22.93, 78.32) * mm, "end": v(23.04, 78.68) * mm});
            skLineSegment(sketch, "E467", {"start": v(23.04, 78.68) * mm, "end": v(23.15, 79.04) * mm});
            skLineSegment(sketch, "E468", {"start": v(23.15, 79.04) * mm, "end": v(23.73, 81.02) * mm});
            skLineSegment(sketch, "E469", {"start": v(23.73, 81.02) * mm, "end": v(24.36, 83.17) * mm});
            skLineSegment(sketch, "E470", {"start": v(24.36, 83.17) * mm, "end": v(24.5, 83.62) * mm});
            skLineSegment(sketch, "E471", {"start": v(24.5, 83.62) * mm, "end": v(24.57, 83.7) * mm});
            skLineSegment(sketch, "E472", {"start": v(24.57, 83.7) * mm, "end": v(25.2, 84.28) * mm});
            skLineSegment(sketch, "E473", {"start": v(25.2, 84.28) * mm, "end": v(25.25, 84.32) * mm});
            skLineSegment(sketch, "E474", {"start": v(25.25, 84.32) * mm, "end": v(25.3, 84.36) * mm});
            skLineSegment(sketch, "E475", {"start": v(25.3, 84.36) * mm, "end": v(25.62, 84.66) * mm});
            skLineSegment(sketch, "E476", {"start": v(25.62, 84.66) * mm, "end": v(25.64, 84.67) * mm});
            skLineSegment(sketch, "E477", {"start": v(25.64, 84.67) * mm, "end": v(25.64, 84.77) * mm});
            skLineSegment(sketch, "E478", {"start": v(25.64, 84.77) * mm, "end": v(22.12, 84.77) * mm});
            skLineSegment(sketch, "E479", {"start": v(22.12, 84.77) * mm, "end": v(22.12, 84.65) * mm});
            skLineSegment(sketch, "E480", {"start": v(-88.79, 84.72) * mm, "end": v(-87.13, 83.69) * mm});
            skLineSegment(sketch, "E481", {"start": v(-87.13, 83.69) * mm, "end": v(-87.02, 72.08) * mm});
            skLineSegment(sketch, "E482", {"start": v(-87.02, 72.08) * mm, "end": v(-87.02, 71.77) * mm});
            skLineSegment(sketch, "E483", {"start": v(-87.02, 71.77) * mm, "end": v(-87.04, 70.93) * mm});
            skLineSegment(sketch, "E484", {"start": v(-87.04, 70.93) * mm, "end": v(-87.04, 70.84) * mm});
            skLineSegment(sketch, "E485", {"start": v(-87.04, 70.84) * mm, "end": v(-87.05, 70.76) * mm});
            skLineSegment(sketch, "E486", {"start": v(-87.05, 70.76) * mm, "end": v(-87.13, 69.94) * mm});
            skLineSegment(sketch, "E487", {"start": v(-87.13, 69.94) * mm, "end": v(-87.14, 69.87) * mm});
            skLineSegment(sketch, "E488", {"start": v(-87.14, 69.87) * mm, "end": v(-87.16, 69.8) * mm});
            skLineSegment(sketch, "E489", {"start": v(-87.16, 69.8) * mm, "end": v(-87.38, 69.1) * mm});
            skLineSegment(sketch, "E490", {"start": v(-87.38, 69.1) * mm, "end": v(-87.4, 69.04) * mm});
            skLineSegment(sketch, "E491", {"start": v(-87.4, 69.04) * mm, "end": v(-87.44, 68.98) * mm});
            skLineSegment(sketch, "E492", {"start": v(-87.44, 68.98) * mm, "end": v(-87.85, 68.36) * mm});
            skLineSegment(sketch, "E493", {"start": v(-87.85, 68.36) * mm, "end": v(-87.9, 68.3) * mm});
            skLineSegment(sketch, "E494", {"start": v(-87.9, 68.3) * mm, "end": v(-87.96, 68.23) * mm});
            skLineSegment(sketch, "E495", {"start": v(-87.96, 68.23) * mm, "end": v(-88.74, 67.61) * mm});
            skLineSegment(sketch, "E496", {"start": v(-88.74, 67.61) * mm, "end": v(-88.83, 67.57) * mm});
            skLineSegment(sketch, "E497", {"start": v(-88.83, 67.57) * mm, "end": v(-88.92, 67.52) * mm});
            skLineSegment(sketch, "E498", {"start": v(-88.92, 67.52) * mm, "end": v(-89.9, 67.32) * mm});
            skLineSegment(sketch, "E499", {"start": v(-89.9, 67.32) * mm, "end": v(-90, 67.32) * mm});
            skLineSegment(sketch, "E500", {"start": v(-90, 67.32) * mm, "end": v(-90, 67.33) * mm});
            skLineSegment(sketch, "E501", {"start": v(-90, 67.33) * mm, "end": v(-89.9, 67.48) * mm});
            skLineSegment(sketch, "E502", {"start": v(-89.9, 67.48) * mm, "end": v(-89.89, 67.5) * mm});
            skLineSegment(sketch, "E503", {"start": v(-89.89, 67.5) * mm, "end": v(-89.88, 67.5) * mm});
            skLineSegment(sketch, "E504", {"start": v(-89.88, 67.5) * mm, "end": v(-89.8, 67.68) * mm});
            skLineSegment(sketch, "E505", {"start": v(-89.8, 67.68) * mm, "end": v(-89.8, 67.7) * mm});
            skLineSegment(sketch, "E506", {"start": v(-89.8, 67.7) * mm, "end": v(-89.8, 67.72) * mm});
            skLineSegment(sketch, "E507", {"start": v(-89.8, 67.72) * mm, "end": v(-89.77, 67.93) * mm});
            skLineSegment(sketch, "E508", {"start": v(-89.77, 67.93) * mm, "end": v(-89.77, 68) * mm});
            skLineSegment(sketch, "E509", {"start": v(-89.77, 68) * mm, "end": v(-89.77, 68.08) * mm});
            skLineSegment(sketch, "E510", {"start": v(-89.77, 68.08) * mm, "end": v(-89.83, 68.3) * mm});
            skLineSegment(sketch, "E511", {"start": v(-89.83, 68.3) * mm, "end": v(-89.85, 68.32) * mm});
            skLineSegment(sketch, "E512", {"start": v(-89.85, 68.32) * mm, "end": v(-89.86, 68.35) * mm});
            skLineSegment(sketch, "E513", {"start": v(-89.86, 68.35) * mm, "end": v(-90.04, 68.63) * mm});
            skLineSegment(sketch, "E514", {"start": v(-90.04, 68.63) * mm, "end": v(-90.06, 68.66) * mm});
            skLineSegment(sketch, "E515", {"start": v(-90.06, 68.66) * mm, "end": v(-90.1, 68.68) * mm});
            skLineSegment(sketch, "E516", {"start": v(-90.1, 68.68) * mm, "end": v(-90.37, 68.86) * mm});
            skLineSegment(sketch, "E517", {"start": v(-90.37, 68.86) * mm, "end": v(-90.4, 68.87) * mm});
            skLineSegment(sketch, "E518", {"start": v(-90.4, 68.87) * mm, "end": v(-90.43, 68.89) * mm});
            skLineSegment(sketch, "E519", {"start": v(-90.43, 68.89) * mm, "end": v(-90.7, 68.97) * mm});
            skLineSegment(sketch, "E520", {"start": v(-90.7, 68.97) * mm, "end": v(-90.8, 68.97) * mm});
            skLineSegment(sketch, "E521", {"start": v(-90.8, 68.97) * mm, "end": v(-90.9, 68.97) * mm});
            skLineSegment(sketch, "E522", {"start": v(-90.9, 68.97) * mm, "end": v(-91.17, 68.9) * mm});
            skLineSegment(sketch, "E523", {"start": v(-91.17, 68.9) * mm, "end": v(-91.2, 68.88) * mm});
            skLineSegment(sketch, "E524", {"start": v(-91.2, 68.88) * mm, "end": v(-91.24, 68.87) * mm});
            skLineSegment(sketch, "E525", {"start": v(-91.24, 68.87) * mm, "end": v(-91.52, 68.68) * mm});
            skLineSegment(sketch, "E526", {"start": v(-91.52, 68.68) * mm, "end": v(-91.55, 68.66) * mm});
            skLineSegment(sketch, "E527", {"start": v(-91.55, 68.66) * mm, "end": v(-91.57, 68.64) * mm});
            skLineSegment(sketch, "E528", {"start": v(-91.57, 68.64) * mm, "end": v(-91.77, 68.34) * mm});
            skLineSegment(sketch, "E529", {"start": v(-91.77, 68.34) * mm, "end": v(-91.79, 68.3) * mm});
            skLineSegment(sketch, "E530", {"start": v(-91.79, 68.3) * mm, "end": v(-91.8, 68.28) * mm});
            skLineSegment(sketch, "E531", {"start": v(-91.8, 68.28) * mm, "end": v(-91.9, 67.98) * mm});
            skLineSegment(sketch, "E532", {"start": v(-91.9, 67.98) * mm, "end": v(-91.9, 67.87) * mm});
            skLineSegment(sketch, "E533", {"start": v(-91.9, 67.87) * mm, "end": v(-91.9, 67.72) * mm});
            skLineSegment(sketch, "E534", {"start": v(-91.9, 67.72) * mm, "end": v(-91.74, 67.3) * mm});
            skLineSegment(sketch, "E535", {"start": v(-91.74, 67.3) * mm, "end": v(-91.71, 67.26) * mm});
            skLineSegment(sketch, "E536", {"start": v(-91.71, 67.26) * mm, "end": v(-91.69, 67.2) * mm});
            skLineSegment(sketch, "E537", {"start": v(-91.69, 67.2) * mm, "end": v(-91.32, 66.86) * mm});
            skLineSegment(sketch, "E538", {"start": v(-91.32, 66.86) * mm, "end": v(-91.28, 66.83) * mm});
            skLineSegment(sketch, "E539", {"start": v(-91.28, 66.83) * mm, "end": v(-91.23, 66.8) * mm});
            skLineSegment(sketch, "E540", {"start": v(-91.23, 66.8) * mm, "end": v(-90.75, 66.6) * mm});
            skLineSegment(sketch, "E541", {"start": v(-90.75, 66.6) * mm, "end": v(-90.7, 66.59) * mm});
            skLineSegment(sketch, "E542", {"start": v(-90.7, 66.59) * mm, "end": v(-90.64, 66.57) * mm});
            skLineSegment(sketch, "E543", {"start": v(-90.64, 66.57) * mm, "end": v(-90.22, 66.5) * mm});
            skLineSegment(sketch, "E544", {"start": v(-90.22, 66.5) * mm, "end": v(-90.08, 66.5) * mm});
            skLineSegment(sketch, "E545", {"start": v(-90.08, 66.5) * mm, "end": v(-89.78, 66.5) * mm});
            skLineSegment(sketch, "E546", {"start": v(-89.78, 66.5) * mm, "end": v(-88.96, 66.67) * mm});
            skLineSegment(sketch, "E547", {"start": v(-88.96, 66.67) * mm, "end": v(-88.87, 66.7) * mm});
            skLineSegment(sketch, "E548", {"start": v(-88.87, 66.7) * mm, "end": v(-88.77, 66.74) * mm});
            skLineSegment(sketch, "E549", {"start": v(-88.77, 66.74) * mm, "end": v(-87.88, 67.2) * mm});
            skLineSegment(sketch, "E550", {"start": v(-87.88, 67.2) * mm, "end": v(-87.8, 67.26) * mm});
            skLineSegment(sketch, "E551", {"start": v(-87.8, 67.26) * mm, "end": v(-87.7, 67.32) * mm});
            skLineSegment(sketch, "E552", {"start": v(-87.7, 67.32) * mm, "end": v(-86.93, 68.03) * mm});
            skLineSegment(sketch, "E553", {"start": v(-86.93, 68.03) * mm, "end": v(-86.86, 68.11) * mm});
            skLineSegment(sketch, "E554", {"start": v(-86.86, 68.11) * mm, "end": v(-86.79, 68.2) * mm});
            skLineSegment(sketch, "E555", {"start": v(-86.79, 68.2) * mm, "end": v(-86.18, 69.13) * mm});
            skLineSegment(sketch, "E556", {"start": v(-86.18, 69.13) * mm, "end": v(-86.13, 69.23) * mm});
            skLineSegment(sketch, "E557", {"start": v(-86.13, 69.23) * mm, "end": v(-86.08, 69.32) * mm});
            skLineSegment(sketch, "E558", {"start": v(-86.08, 69.32) * mm, "end": v(-85.66, 70.15) * mm});
            skLineSegment(sketch, "E559", {"start": v(-85.66, 70.15) * mm, "end": v(-85.62, 70.23) * mm});
            skLineSegment(sketch, "E560", {"start": v(-85.62, 70.23) * mm, "end": v(-85.58, 70.31) * mm});
            skLineSegment(sketch, "E561", {"start": v(-85.58, 70.31) * mm, "end": v(-85.25, 71.18) * mm});
            skLineSegment(sketch, "E562", {"start": v(-85.25, 71.18) * mm, "end": v(-85.23, 71.28) * mm});
            skLineSegment(sketch, "E563", {"start": v(-85.23, 71.28) * mm, "end": v(-85.2, 71.38) * mm});
            skLineSegment(sketch, "E564", {"start": v(-85.2, 71.38) * mm, "end": v(-85, 72.38) * mm});
            skLineSegment(sketch, "E565", {"start": v(-85, 72.38) * mm, "end": v(-84.98, 72.48) * mm});
            skLineSegment(sketch, "E566", {"start": v(-84.98, 72.48) * mm, "end": v(-84.96, 72.6) * mm});
            skLineSegment(sketch, "E567", {"start": v(-84.96, 72.6) * mm, "end": v(-84.9, 73.85) * mm});
            skLineSegment(sketch, "E568", {"start": v(-84.9, 73.85) * mm, "end": v(-84.91, 73.99) * mm});
            skLineSegment(sketch, "E569", {"start": v(-84.91, 73.99) * mm, "end": v(-84.91, 74.14) * mm});
            skLineSegment(sketch, "E570", {"start": v(-84.91, 74.14) * mm, "end": v(-84.94, 75.64) * mm});
            skLineSegment(sketch, "E571", {"start": v(-84.94, 75.64) * mm, "end": v(-84.95, 75.8) * mm});
            skLineSegment(sketch, "E572", {"start": v(-84.95, 75.8) * mm, "end": v(-84.95, 75.96) * mm});
            skLineSegment(sketch, "E573", {"start": v(-84.95, 75.96) * mm, "end": v(-84.97, 77.71) * mm});
            skLineSegment(sketch, "E574", {"start": v(-84.97, 77.71) * mm, "end": v(-84.98, 77.9) * mm});
            skLineSegment(sketch, "E575", {"start": v(-84.98, 77.9) * mm, "end": v(-84.98, 78.1) * mm});
            skLineSegment(sketch, "E576", {"start": v(-84.98, 78.1) * mm, "end": v(-85.01, 80.26) * mm});
            skLineSegment(sketch, "E577", {"start": v(-85.01, 80.26) * mm, "end": v(-85.01, 80.5) * mm});
            skLineSegment(sketch, "E578", {"start": v(-85.01, 80.5) * mm, "end": v(-85.02, 80.74) * mm});
            skLineSegment(sketch, "E579", {"start": v(-85.02, 80.74) * mm, "end": v(-85.03, 83.05) * mm});
            skLineSegment(sketch, "E580", {"start": v(-85.03, 83.05) * mm, "end": v(-85.03, 83.82) * mm});
            skLineSegment(sketch, "E581", {"start": v(-85.03, 83.82) * mm, "end": v(-83.65, 84.72) * mm});
            skLineSegment(sketch, "E582", {"start": v(-83.65, 84.72) * mm, "end": v(-83.65, 84.84) * mm});
            skLineSegment(sketch, "E583", {"start": v(-83.65, 84.84) * mm, "end": v(-88.79, 84.84) * mm});
            skLineSegment(sketch, "E584", {"start": v(-88.79, 84.84) * mm, "end": v(-88.79, 84.72) * mm});
            skLineSegment(sketch, "E585", {"start": v(-69.46, 79.59) * mm, "end": v(-69.53, 79.7) * mm});
            skLineSegment(sketch, "E586", {"start": v(-69.53, 79.7) * mm, "end": v(-70.34, 80.67) * mm});
            skLineSegment(sketch, "E587", {"start": v(-70.34, 80.67) * mm, "end": v(-70.43, 80.75) * mm});
            skLineSegment(sketch, "E588", {"start": v(-70.43, 80.75) * mm, "end": v(-70.52, 80.85) * mm});
            skLineSegment(sketch, "E589", {"start": v(-70.52, 80.85) * mm, "end": v(-71.51, 81.62) * mm});
            skLineSegment(sketch, "E590", {"start": v(-71.51, 81.62) * mm, "end": v(-71.62, 81.68) * mm});
            skLineSegment(sketch, "E591", {"start": v(-71.62, 81.68) * mm, "end": v(-71.73, 81.75) * mm});
            skLineSegment(sketch, "E592", {"start": v(-71.73, 81.75) * mm, "end": v(-72.85, 82.22) * mm});
            skLineSegment(sketch, "E593", {"start": v(-72.85, 82.22) * mm, "end": v(-72.97, 82.25) * mm});
            skLineSegment(sketch, "E594", {"start": v(-72.97, 82.25) * mm, "end": v(-73.09, 82.29) * mm});
            skLineSegment(sketch, "E595", {"start": v(-73.09, 82.29) * mm, "end": v(-74.08, 82.45) * mm});
            skLineSegment(sketch, "E596", {"start": v(-74.08, 82.45) * mm, "end": v(-74.4, 82.45) * mm});
            skLineSegment(sketch, "E597", {"start": v(-74.4, 82.45) * mm, "end": v(-74.72, 82.45) * mm});
            skLineSegment(sketch, "E598", {"start": v(-74.72, 82.45) * mm, "end": v(-75.66, 82.34) * mm});
            skLineSegment(sketch, "E599", {"start": v(-75.66, 82.34) * mm, "end": v(-76.63, 82.07) * mm});
            skLineSegment(sketch, "E600", {"start": v(-76.63, 82.07) * mm, "end": v(-76.8, 82) * mm});
            skLineSegment(sketch, "E601", {"start": v(-76.8, 82) * mm, "end": v(-77, 81.92) * mm});
            skLineSegment(sketch, "E602", {"start": v(-77, 81.92) * mm, "end": v(-78.58, 80.87) * mm});
            skLineSegment(sketch, "E603", {"start": v(-78.58, 80.87) * mm, "end": v(-78.71, 80.73) * mm});
            skLineSegment(sketch, "E604", {"start": v(-78.71, 80.73) * mm, "end": v(-78.85, 80.6) * mm});
            skLineSegment(sketch, "E605", {"start": v(-78.85, 80.6) * mm, "end": v(-79.45, 79.87) * mm});
            skLineSegment(sketch, "E606", {"start": v(-79.45, 79.87) * mm, "end": v(-79.92, 79.05) * mm});
            skLineSegment(sketch, "E607", {"start": v(-79.92, 79.05) * mm, "end": v(-80, 78.87) * mm});
            skLineSegment(sketch, "E608", {"start": v(-80, 78.87) * mm, "end": v(-80.07, 78.7) * mm});
            skLineSegment(sketch, "E609", {"start": v(-80.07, 78.7) * mm, "end": v(-80.45, 77.1) * mm});
            skLineSegment(sketch, "E610", {"start": v(-80.45, 77.1) * mm, "end": v(-80.45, 76.58) * mm});
            skLineSegment(sketch, "E611", {"start": v(-80.45, 76.58) * mm, "end": v(-80.45, 76.02) * mm});
            skLineSegment(sketch, "E612", {"start": v(-80.45, 76.02) * mm, "end": v(-80.06, 74.5) * mm});
            skLineSegment(sketch, "E613", {"start": v(-80.06, 74.5) * mm, "end": v(-79.98, 74.33) * mm});
            skLineSegment(sketch, "E614", {"start": v(-79.98, 74.33) * mm, "end": v(-79.9, 74.15) * mm});
            skLineSegment(sketch, "E615", {"start": v(-79.9, 74.15) * mm, "end": v(-78.83, 72.62) * mm});
            skLineSegment(sketch, "E616", {"start": v(-78.83, 72.62) * mm, "end": v(-78.7, 72.48) * mm});
            skLineSegment(sketch, "E617", {"start": v(-78.7, 72.48) * mm, "end": v(-78.56, 72.35) * mm});
            skLineSegment(sketch, "E618", {"start": v(-78.56, 72.35) * mm, "end": v(-76.98, 71.28) * mm});
            skLineSegment(sketch, "E619", {"start": v(-76.98, 71.28) * mm, "end": v(-76.8, 71.2) * mm});
            skLineSegment(sketch, "E620", {"start": v(-76.8, 71.2) * mm, "end": v(-76.62, 71.11) * mm});
            skLineSegment(sketch, "E621", {"start": v(-76.62, 71.11) * mm, "end": v(-75.68, 70.85) * mm});
            skLineSegment(sketch, "E622", {"start": v(-75.68, 70.85) * mm, "end": v(-74.77, 70.76) * mm});
            skLineSegment(sketch, "E623", {"start": v(-74.77, 70.76) * mm, "end": v(-74.47, 70.76) * mm});
            skLineSegment(sketch, "E624", {"start": v(-74.47, 70.76) * mm, "end": v(-74.17, 70.76) * mm});
            skLineSegment(sketch, "E625", {"start": v(-74.17, 70.76) * mm, "end": v(-73.27, 70.85) * mm});
            skLineSegment(sketch, "E626", {"start": v(-73.27, 70.85) * mm, "end": v(-72.33, 71.12) * mm});
            skLineSegment(sketch, "E627", {"start": v(-72.33, 71.12) * mm, "end": v(-72.15, 71.22) * mm});
            skLineSegment(sketch, "E628", {"start": v(-72.15, 71.22) * mm, "end": v(-71.97, 71.3) * mm});
            skLineSegment(sketch, "E629", {"start": v(-71.97, 71.3) * mm, "end": v(-70.43, 72.36) * mm});
            skLineSegment(sketch, "E630", {"start": v(-70.43, 72.36) * mm, "end": v(-70.3, 72.5) * mm});
            skLineSegment(sketch, "E631", {"start": v(-70.3, 72.5) * mm, "end": v(-70.17, 72.64) * mm});
            skLineSegment(sketch, "E632", {"start": v(-70.17, 72.64) * mm, "end": v(-69.13, 74.18) * mm});
            skLineSegment(sketch, "E633", {"start": v(-69.13, 74.18) * mm, "end": v(-69.05, 74.35) * mm});
            skLineSegment(sketch, "E634", {"start": v(-69.05, 74.35) * mm, "end": v(-68.98, 74.53) * mm});
            skLineSegment(sketch, "E635", {"start": v(-68.98, 74.53) * mm, "end": v(-68.61, 76.07) * mm});
            skLineSegment(sketch, "E636", {"start": v(-68.61, 76.07) * mm, "end": v(-68.61, 76.58) * mm});
            skLineSegment(sketch, "E637", {"start": v(-68.61, 76.58) * mm, "end": v(-68.61, 76.98) * mm});
            skLineSegment(sketch, "E638", {"start": v(-68.61, 76.98) * mm, "end": v(-68.8, 78.06) * mm});
            skLineSegment(sketch, "E639", {"start": v(-68.8, 78.06) * mm, "end": v(-68.83, 78.19) * mm});
            skLineSegment(sketch, "E640", {"start": v(-68.83, 78.19) * mm, "end": v(-68.87, 78.31) * mm});
            skLineSegment(sketch, "E641", {"start": v(-68.87, 78.31) * mm, "end": v(-69.4, 79.49) * mm});
            skLineSegment(sketch, "E642", {"start": v(-69.4, 79.49) * mm, "end": v(-69.46, 79.59) * mm});
            skLineSegment(sketch, "E643", {"start": v(-71.06, 74.4) * mm, "end": v(-71.12, 74.24) * mm});
            skLineSegment(sketch, "E644", {"start": v(-71.12, 74.24) * mm, "end": v(-71.82, 72.94) * mm});
            skLineSegment(sketch, "E645", {"start": v(-71.82, 72.94) * mm, "end": v(-71.9, 72.83) * mm});
            skLineSegment(sketch, "E646", {"start": v(-71.9, 72.83) * mm, "end": v(-72, 72.73) * mm});
            skLineSegment(sketch, "E647", {"start": v(-72, 72.73) * mm, "end": v(-73, 71.9) * mm});
            skLineSegment(sketch, "E648", {"start": v(-73, 71.9) * mm, "end": v(-73.11, 71.83) * mm});
            skLineSegment(sketch, "E649", {"start": v(-73.11, 71.83) * mm, "end": v(-73.22, 71.78) * mm});
            skLineSegment(sketch, "E650", {"start": v(-73.22, 71.78) * mm, "end": v(-74.2, 71.52) * mm});
            skLineSegment(sketch, "E651", {"start": v(-74.2, 71.52) * mm, "end": v(-74.51, 71.52) * mm});
            skLineSegment(sketch, "E652", {"start": v(-74.51, 71.52) * mm, "end": v(-74.89, 71.52) * mm});
            skLineSegment(sketch, "E653", {"start": v(-74.89, 71.52) * mm, "end": v(-75.9, 71.8) * mm});
            skLineSegment(sketch, "E654", {"start": v(-75.9, 71.8) * mm, "end": v(-76.01, 71.86) * mm});
            skLineSegment(sketch, "E655", {"start": v(-76.01, 71.86) * mm, "end": v(-76.13, 71.92) * mm});
            skLineSegment(sketch, "E656", {"start": v(-76.13, 71.92) * mm, "end": v(-77.17, 72.76) * mm});
            skLineSegment(sketch, "E657", {"start": v(-77.17, 72.76) * mm, "end": v(-77.26, 72.87) * mm});
            skLineSegment(sketch, "E658", {"start": v(-77.26, 72.87) * mm, "end": v(-77.35, 72.97) * mm});
            skLineSegment(sketch, "E659", {"start": v(-77.35, 72.97) * mm, "end": v(-78.07, 74.3) * mm});
            skLineSegment(sketch, "E660", {"start": v(-78.07, 74.3) * mm, "end": v(-78.12, 74.46) * mm});
            skLineSegment(sketch, "E661", {"start": v(-78.12, 74.46) * mm, "end": v(-78.17, 74.62) * mm});
            skLineSegment(sketch, "E662", {"start": v(-78.17, 74.62) * mm, "end": v(-78.43, 76.09) * mm});
            skLineSegment(sketch, "E663", {"start": v(-78.43, 76.09) * mm, "end": v(-78.43, 76.58) * mm});
            skLineSegment(sketch, "E664", {"start": v(-78.43, 76.58) * mm, "end": v(-78.43, 77.08) * mm});
            skLineSegment(sketch, "E665", {"start": v(-78.43, 77.08) * mm, "end": v(-78.22, 78.43) * mm});
            skLineSegment(sketch, "E666", {"start": v(-78.22, 78.43) * mm, "end": v(-78.17, 78.59) * mm});
            skLineSegment(sketch, "E667", {"start": v(-78.17, 78.59) * mm, "end": v(-78.13, 78.74) * mm});
            skLineSegment(sketch, "E668", {"start": v(-78.13, 78.74) * mm, "end": v(-77.5, 80.05) * mm});
            skLineSegment(sketch, "E669", {"start": v(-77.5, 80.05) * mm, "end": v(-77.42, 80.16) * mm});
            skLineSegment(sketch, "E670", {"start": v(-77.42, 80.16) * mm, "end": v(-77.34, 80.27) * mm});
            skLineSegment(sketch, "E671", {"start": v(-77.34, 80.27) * mm, "end": v(-76.33, 81.17) * mm});
            skLineSegment(sketch, "E672", {"start": v(-76.33, 81.17) * mm, "end": v(-76.22, 81.23) * mm});
            skLineSegment(sketch, "E673", {"start": v(-76.22, 81.23) * mm, "end": v(-76.1, 81.3) * mm});
            skLineSegment(sketch, "E674", {"start": v(-76.1, 81.3) * mm, "end": v(-74.98, 81.62) * mm});
            skLineSegment(sketch, "E675", {"start": v(-74.98, 81.62) * mm, "end": v(-74.6, 81.62) * mm});
            skLineSegment(sketch, "E676", {"start": v(-74.6, 81.62) * mm, "end": v(-74.2, 81.62) * mm});
            skLineSegment(sketch, "E677", {"start": v(-74.2, 81.62) * mm, "end": v(-73.1, 81.3) * mm});
            skLineSegment(sketch, "E678", {"start": v(-73.1, 81.3) * mm, "end": v(-72.98, 81.23) * mm});
            skLineSegment(sketch, "E679", {"start": v(-72.98, 81.23) * mm, "end": v(-72.86, 81.17) * mm});
            skLineSegment(sketch, "E680", {"start": v(-72.86, 81.17) * mm, "end": v(-71.85, 80.28) * mm});
            skLineSegment(sketch, "E681", {"start": v(-71.85, 80.28) * mm, "end": v(-71.76, 80.17) * mm});
            skLineSegment(sketch, "E682", {"start": v(-71.76, 80.17) * mm, "end": v(-71.68, 80.06) * mm});
            skLineSegment(sketch, "E683", {"start": v(-71.68, 80.06) * mm, "end": v(-71.05, 78.74) * mm});
            skLineSegment(sketch, "E684", {"start": v(-71.05, 78.74) * mm, "end": v(-71, 78.59) * mm});
            skLineSegment(sketch, "E685", {"start": v(-71, 78.59) * mm, "end": v(-70.96, 78.44) * mm});
            skLineSegment(sketch, "E686", {"start": v(-70.96, 78.44) * mm, "end": v(-70.74, 77.04) * mm});
            skLineSegment(sketch, "E687", {"start": v(-70.74, 77.04) * mm, "end": v(-70.74, 76.58) * mm});
            skLineSegment(sketch, "E688", {"start": v(-70.74, 76.58) * mm, "end": v(-70.74, 76.03) * mm});
            skLineSegment(sketch, "E689", {"start": v(-70.74, 76.03) * mm, "end": v(-71, 74.56) * mm});
            skLineSegment(sketch, "E690", {"start": v(-71, 74.56) * mm, "end": v(-71.06, 74.4) * mm});
            skLineSegment(sketch, "E691", {"start": v(-58.23, 81.88) * mm, "end": v(-56.98, 81) * mm});
            skLineSegment(sketch, "E692", {"start": v(-56.98, 81) * mm, "end": v(-56.98, 77.31) * mm});
            skLineSegment(sketch, "E693", {"start": v(-56.98, 77.31) * mm, "end": v(-57.47, 77.3) * mm});
            skLineSegment(sketch, "E694", {"start": v(-57.47, 77.3) * mm, "end": v(-62.24, 77.3) * mm});
            skLineSegment(sketch, "E695", {"start": v(-62.24, 77.3) * mm, "end": v(-62.72, 77.31) * mm});
            skLineSegment(sketch, "E696", {"start": v(-62.72, 77.31) * mm, "end": v(-62.72, 81) * mm});
            skLineSegment(sketch, "E697", {"start": v(-62.72, 81) * mm, "end": v(-61.47, 81.88) * mm});
            skLineSegment(sketch, "E698", {"start": v(-61.47, 81.88) * mm, "end": v(-61.47, 82) * mm});
            skLineSegment(sketch, "E699", {"start": v(-61.47, 82) * mm, "end": v(-65.79, 82) * mm});
            skLineSegment(sketch, "E700", {"start": v(-65.79, 82) * mm, "end": v(-65.79, 81.88) * mm});
            skLineSegment(sketch, "E701", {"start": v(-65.79, 81.88) * mm, "end": v(-64.58, 81) * mm});
            skLineSegment(sketch, "E702", {"start": v(-64.58, 81) * mm, "end": v(-64.58, 72.23) * mm});
            skLineSegment(sketch, "E703", {"start": v(-64.58, 72.23) * mm, "end": v(-65.79, 71.32) * mm});
            skLineSegment(sketch, "E704", {"start": v(-65.79, 71.32) * mm, "end": v(-65.79, 71.19) * mm});
            skLineSegment(sketch, "E705", {"start": v(-65.79, 71.19) * mm, "end": v(-61.47, 71.19) * mm});
            skLineSegment(sketch, "E706", {"start": v(-61.47, 71.19) * mm, "end": v(-61.47, 71.32) * mm});
            skLineSegment(sketch, "E707", {"start": v(-61.47, 71.32) * mm, "end": v(-62.72, 72.23) * mm});
            skLineSegment(sketch, "E708", {"start": v(-62.72, 72.23) * mm, "end": v(-62.72, 76.43) * mm});
            skLineSegment(sketch, "E709", {"start": v(-62.72, 76.43) * mm, "end": v(-62.24, 76.44) * mm});
            skLineSegment(sketch, "E710", {"start": v(-62.24, 76.44) * mm, "end": v(-57.47, 76.44) * mm});
            skLineSegment(sketch, "E711", {"start": v(-57.47, 76.44) * mm, "end": v(-56.98, 76.43) * mm});
            skLineSegment(sketch, "E712", {"start": v(-56.98, 76.43) * mm, "end": v(-56.98, 72.23) * mm});
            skLineSegment(sketch, "E713", {"start": v(-56.98, 72.23) * mm, "end": v(-58.23, 71.32) * mm});
            skLineSegment(sketch, "E714", {"start": v(-58.23, 71.32) * mm, "end": v(-58.23, 71.19) * mm});
            skLineSegment(sketch, "E715", {"start": v(-58.23, 71.19) * mm, "end": v(-53.91, 71.19) * mm});
            skLineSegment(sketch, "E716", {"start": v(-53.91, 71.19) * mm, "end": v(-53.91, 71.32) * mm});
            skLineSegment(sketch, "E717", {"start": v(-53.91, 71.32) * mm, "end": v(-55.13, 72.23) * mm});
            skLineSegment(sketch, "E718", {"start": v(-55.13, 72.23) * mm, "end": v(-55.14, 72.91) * mm});
            skLineSegment(sketch, "E719", {"start": v(-55.14, 72.91) * mm, "end": v(-55.14, 80.22) * mm});
            skLineSegment(sketch, "E720", {"start": v(-55.14, 80.22) * mm, "end": v(-55.13, 81) * mm});
            skLineSegment(sketch, "E721", {"start": v(-55.13, 81) * mm, "end": v(-53.91, 81.88) * mm});
            skLineSegment(sketch, "E722", {"start": v(-53.91, 81.88) * mm, "end": v(-53.91, 82) * mm});
            skLineSegment(sketch, "E723", {"start": v(-53.91, 82) * mm, "end": v(-58.23, 82) * mm});
            skLineSegment(sketch, "E724", {"start": v(-58.23, 82) * mm, "end": v(-58.23, 81.88) * mm});
            skLineSegment(sketch, "E725", {"start": v(32.2, 82.16) * mm, "end": v(30.65, 82.16) * mm});
            skLineSegment(sketch, "E726", {"start": v(30.65, 82.16) * mm, "end": v(26.9, 72.3) * mm});
            skLineSegment(sketch, "E727", {"start": v(26.9, 72.3) * mm, "end": v(25.64, 71.26) * mm});
            skLineSegment(sketch, "E728", {"start": v(25.64, 71.26) * mm, "end": v(25.64, 71.12) * mm});
            skLineSegment(sketch, "E729", {"start": v(25.64, 71.12) * mm, "end": v(29.3, 71.12) * mm});
            skLineSegment(sketch, "E730", {"start": v(29.3, 71.12) * mm, "end": v(29.3, 71.26) * mm});
            skLineSegment(sketch, "E731", {"start": v(29.3, 71.26) * mm, "end": v(27.92, 72.3) * mm});
            skLineSegment(sketch, "E732", {"start": v(27.92, 72.3) * mm, "end": v(28.96, 75.15) * mm});
            skLineSegment(sketch, "E733", {"start": v(28.96, 75.15) * mm, "end": v(29.32, 75.16) * mm});
            skLineSegment(sketch, "E734", {"start": v(29.32, 75.16) * mm, "end": v(32.7, 75.16) * mm});
            skLineSegment(sketch, "E735", {"start": v(32.7, 75.16) * mm, "end": v(33.02, 75.15) * mm});
            skLineSegment(sketch, "E736", {"start": v(33.02, 75.15) * mm, "end": v(34.14, 72.3) * mm});
            skLineSegment(sketch, "E737", {"start": v(34.14, 72.3) * mm, "end": v(32.75, 71.26) * mm});
            skLineSegment(sketch, "E738", {"start": v(32.75, 71.26) * mm, "end": v(32.75, 71.12) * mm});
            skLineSegment(sketch, "E739", {"start": v(32.75, 71.12) * mm, "end": v(37.5, 71.12) * mm});
            skLineSegment(sketch, "E740", {"start": v(37.5, 71.12) * mm, "end": v(37.5, 71.26) * mm});
            skLineSegment(sketch, "E741", {"start": v(37.5, 71.26) * mm, "end": v(36.25, 72.34) * mm});
            skLineSegment(sketch, "E742", {"start": v(36.25, 72.34) * mm, "end": v(32.2, 82.16) * mm});
            skLineSegment(sketch, "E743", {"start": v(29.28, 75.96) * mm, "end": v(30.94, 80.54) * mm});
            skLineSegment(sketch, "E744", {"start": v(30.94, 80.54) * mm, "end": v(32.71, 75.96) * mm});
            skLineSegment(sketch, "E745", {"start": v(32.71, 75.96) * mm, "end": v(29.28, 75.96) * mm});
            skLineSegment(sketch, "E746", {"start": v(72.4, 72.05) * mm, "end": v(72, 72.03) * mm});
            skLineSegment(sketch, "E747", {"start": v(72, 72.03) * mm, "end": v(68.31, 72.03) * mm});
            skLineSegment(sketch, "E748", {"start": v(68.31, 72.03) * mm, "end": v(67.97, 72.05) * mm});
            skLineSegment(sketch, "E749", {"start": v(67.97, 72.05) * mm, "end": v(67.96, 72.4) * mm});
            skLineSegment(sketch, "E750", {"start": v(67.96, 72.4) * mm, "end": v(67.96, 75.95) * mm});
            skLineSegment(sketch, "E751", {"start": v(67.96, 75.95) * mm, "end": v(67.97, 76.3) * mm});
            skLineSegment(sketch, "E752", {"start": v(67.97, 76.3) * mm, "end": v(68.17, 76.3) * mm});
            skLineSegment(sketch, "E753", {"start": v(68.17, 76.3) * mm, "end": v(69.41, 76.33) * mm});
            skLineSegment(sketch, "E754", {"start": v(69.41, 76.33) * mm, "end": v(70.89, 76.34) * mm});
            skLineSegment(sketch, "E755", {"start": v(70.89, 76.34) * mm, "end": v(71.38, 76.34) * mm});
            skLineSegment(sketch, "E756", {"start": v(71.38, 76.34) * mm, "end": v(72.22, 75.1) * mm});
            skLineSegment(sketch, "E757", {"start": v(72.22, 75.1) * mm, "end": v(72.34, 75.1) * mm});
            skLineSegment(sketch, "E758", {"start": v(72.34, 75.1) * mm, "end": v(72.34, 78.44) * mm});
            skLineSegment(sketch, "E759", {"start": v(72.34, 78.44) * mm, "end": v(72.22, 78.44) * mm});
            skLineSegment(sketch, "E760", {"start": v(72.22, 78.44) * mm, "end": v(71.38, 77.19) * mm});
            skLineSegment(sketch, "E761", {"start": v(71.38, 77.19) * mm, "end": v(70.8, 77.19) * mm});
            skLineSegment(sketch, "E762", {"start": v(70.8, 77.19) * mm, "end": v(69.07, 77.2) * mm});
            skLineSegment(sketch, "E763", {"start": v(69.07, 77.2) * mm, "end": v(68.03, 77.22) * mm});
            skLineSegment(sketch, "E764", {"start": v(68.03, 77.22) * mm, "end": v(67.94, 77.23) * mm});
            skLineSegment(sketch, "E765", {"start": v(67.94, 77.23) * mm, "end": v(67.94, 77.38) * mm});
            skLineSegment(sketch, "E766", {"start": v(67.94, 77.38) * mm, "end": v(67.91, 78.65) * mm});
            skLineSegment(sketch, "E767", {"start": v(67.91, 78.65) * mm, "end": v(67.91, 79.07) * mm});
            skLineSegment(sketch, "E768", {"start": v(67.91, 79.07) * mm, "end": v(67.9, 79.23) * mm});
            skLineSegment(sketch, "E769", {"start": v(67.9, 79.23) * mm, "end": v(67.92, 80.81) * mm});
            skLineSegment(sketch, "E770", {"start": v(67.92, 80.81) * mm, "end": v(67.93, 80.98) * mm});
            skLineSegment(sketch, "E771", {"start": v(67.93, 80.98) * mm, "end": v(68.1, 81) * mm});
            skLineSegment(sketch, "E772", {"start": v(68.1, 81) * mm, "end": v(69.54, 81.04) * mm});
            skLineSegment(sketch, "E773", {"start": v(69.54, 81.04) * mm, "end": v(70.03, 81.04) * mm});
            skLineSegment(sketch, "E774", {"start": v(70.03, 81.04) * mm, "end": v(70.6, 81.04) * mm});
            skLineSegment(sketch, "E775", {"start": v(70.6, 81.04) * mm, "end": v(71.9, 81.03) * mm});
            skLineSegment(sketch, "E776", {"start": v(71.9, 81.03) * mm, "end": v(72.34, 81.03) * mm});
            skLineSegment(sketch, "E777", {"start": v(72.34, 81.03) * mm, "end": v(73.23, 79.78) * mm});
            skLineSegment(sketch, "E778", {"start": v(73.23, 79.78) * mm, "end": v(73.34, 79.78) * mm});
            skLineSegment(sketch, "E779", {"start": v(73.34, 79.78) * mm, "end": v(73.34, 81.92) * mm});
            skLineSegment(sketch, "E780", {"start": v(73.34, 81.92) * mm, "end": v(64.87, 81.92) * mm});
            skLineSegment(sketch, "E781", {"start": v(64.87, 81.92) * mm, "end": v(64.87, 81.81) * mm});
            skLineSegment(sketch, "E782", {"start": v(64.87, 81.81) * mm, "end": v(66.1, 80.93) * mm});
            skLineSegment(sketch, "E783", {"start": v(66.1, 80.93) * mm, "end": v(66.1, 80.3) * mm});
            skLineSegment(sketch, "E784", {"start": v(66.1, 80.3) * mm, "end": v(66.13, 76.86) * mm});
            skLineSegment(sketch, "E785", {"start": v(66.13, 76.86) * mm, "end": v(66.1, 73) * mm});
            skLineSegment(sketch, "E786", {"start": v(66.1, 73) * mm, "end": v(66.1, 72.16) * mm});
            skLineSegment(sketch, "E787", {"start": v(66.1, 72.16) * mm, "end": v(64.87, 71.26) * mm});
            skLineSegment(sketch, "E788", {"start": v(64.87, 71.26) * mm, "end": v(64.87, 71.12) * mm});
            skLineSegment(sketch, "E789", {"start": v(64.87, 71.12) * mm, "end": v(73.57, 71.12) * mm});
            skLineSegment(sketch, "E790", {"start": v(73.57, 71.12) * mm, "end": v(73.57, 73.52) * mm});
            skLineSegment(sketch, "E791", {"start": v(73.57, 73.52) * mm, "end": v(73.44, 73.52) * mm});
            skLineSegment(sketch, "E792", {"start": v(73.44, 73.52) * mm, "end": v(72.4, 72.05) * mm});
            skLineSegment(sketch, "E793", {"start": v(87.18, 71.44) * mm, "end": v(87.16, 71.46) * mm});
            skLineSegment(sketch, "E794", {"start": v(87.16, 71.46) * mm, "end": v(86.89, 71.73) * mm});
            skLineSegment(sketch, "E795", {"start": v(86.89, 71.73) * mm, "end": v(86.86, 71.75) * mm});
            skLineSegment(sketch, "E796", {"start": v(86.86, 71.75) * mm, "end": v(86.83, 71.79) * mm});
            skLineSegment(sketch, "E797", {"start": v(86.83, 71.79) * mm, "end": v(86.56, 72.15) * mm});
            skLineSegment(sketch, "E798", {"start": v(86.56, 72.15) * mm, "end": v(86.54, 72.18) * mm});
            skLineSegment(sketch, "E799", {"start": v(86.54, 72.18) * mm, "end": v(86.5, 72.2) * mm});
            skLineSegment(sketch, "E800", {"start": v(86.5, 72.2) * mm, "end": v(86.29, 72.48) * mm});
            skLineSegment(sketch, "E801", {"start": v(86.29, 72.48) * mm, "end": v(86.27, 72.5) * mm});
            skLineSegment(sketch, "E802", {"start": v(86.27, 72.5) * mm, "end": v(84.57, 75.15) * mm});
            skLineSegment(sketch, "E803", {"start": v(84.57, 75.15) * mm, "end": v(84.52, 75.23) * mm});
            skLineSegment(sketch, "E804", {"start": v(84.52, 75.23) * mm, "end": v(84, 75.83) * mm});
            skLineSegment(sketch, "E805", {"start": v(84, 75.83) * mm, "end": v(83.94, 75.88) * mm});
            skLineSegment(sketch, "E806", {"start": v(83.94, 75.88) * mm, "end": v(83.88, 75.92) * mm});
            skLineSegment(sketch, "E807", {"start": v(83.88, 75.92) * mm, "end": v(83.12, 76.17) * mm});
            skLineSegment(sketch, "E808", {"start": v(83.12, 76.17) * mm, "end": v(83.03, 76.18) * mm});
            skLineSegment(sketch, "E809", {"start": v(83.03, 76.18) * mm, "end": v(83.15, 76.18) * mm});
            skLineSegment(sketch, "E810", {"start": v(83.15, 76.18) * mm, "end": v(84.33, 76.4) * mm});
            skLineSegment(sketch, "E811", {"start": v(84.33, 76.4) * mm, "end": v(84.44, 76.43) * mm});
            skLineSegment(sketch, "E812", {"start": v(84.44, 76.43) * mm, "end": v(84.55, 76.47) * mm});
            skLineSegment(sketch, "E813", {"start": v(84.55, 76.47) * mm, "end": v(85.48, 76.96) * mm});
            skLineSegment(sketch, "E814", {"start": v(85.48, 76.96) * mm, "end": v(85.56, 77.02) * mm});
            skLineSegment(sketch, "E815", {"start": v(85.56, 77.02) * mm, "end": v(85.64, 77.08) * mm});
            skLineSegment(sketch, "E816", {"start": v(85.64, 77.08) * mm, "end": v(86.25, 77.8) * mm});
            skLineSegment(sketch, "E817", {"start": v(86.25, 77.8) * mm, "end": v(86.3, 77.88) * mm});
            skLineSegment(sketch, "E818", {"start": v(86.3, 77.88) * mm, "end": v(86.34, 77.97) * mm});
            skLineSegment(sketch, "E819", {"start": v(86.34, 77.97) * mm, "end": v(86.57, 78.74) * mm});
            skLineSegment(sketch, "E820", {"start": v(86.57, 78.74) * mm, "end": v(86.57, 79) * mm});
            skLineSegment(sketch, "E821", {"start": v(86.57, 79) * mm, "end": v(86.57, 79.29) * mm});
            skLineSegment(sketch, "E822", {"start": v(86.57, 79.29) * mm, "end": v(86.3, 80.07) * mm});
            skLineSegment(sketch, "E823", {"start": v(86.3, 80.07) * mm, "end": v(86.26, 80.16) * mm});
            skLineSegment(sketch, "E824", {"start": v(86.26, 80.16) * mm, "end": v(86.2, 80.25) * mm});
            skLineSegment(sketch, "E825", {"start": v(86.2, 80.25) * mm, "end": v(85.48, 81.04) * mm});
            skLineSegment(sketch, "E826", {"start": v(85.48, 81.04) * mm, "end": v(85.4, 81.1) * mm});
            skLineSegment(sketch, "E827", {"start": v(85.4, 81.1) * mm, "end": v(85.3, 81.18) * mm});
            skLineSegment(sketch, "E828", {"start": v(85.3, 81.18) * mm, "end": v(84.17, 81.68) * mm});
            skLineSegment(sketch, "E829", {"start": v(84.17, 81.68) * mm, "end": v(84.04, 81.71) * mm});
            skLineSegment(sketch, "E830", {"start": v(84.04, 81.71) * mm, "end": v(83.9, 81.75) * mm});
            skLineSegment(sketch, "E831", {"start": v(83.9, 81.75) * mm, "end": v(82.7, 81.92) * mm});
            skLineSegment(sketch, "E832", {"start": v(82.7, 81.92) * mm, "end": v(82.29, 81.92) * mm});
            skLineSegment(sketch, "E833", {"start": v(82.29, 81.92) * mm, "end": v(77.26, 81.92) * mm});
            skLineSegment(sketch, "E834", {"start": v(77.26, 81.92) * mm, "end": v(77.26, 81.81) * mm});
            skLineSegment(sketch, "E835", {"start": v(77.26, 81.81) * mm, "end": v(78.48, 80.9) * mm});
            skLineSegment(sketch, "E836", {"start": v(78.48, 80.9) * mm, "end": v(78.48, 72.16) * mm});
            skLineSegment(sketch, "E837", {"start": v(78.48, 72.16) * mm, "end": v(77.19, 71.26) * mm});
            skLineSegment(sketch, "E838", {"start": v(77.19, 71.26) * mm, "end": v(77.19, 71.12) * mm});
            skLineSegment(sketch, "E839", {"start": v(77.19, 71.12) * mm, "end": v(81.6, 71.12) * mm});
            skLineSegment(sketch, "E840", {"start": v(81.6, 71.12) * mm, "end": v(81.6, 71.26) * mm});
            skLineSegment(sketch, "E841", {"start": v(81.6, 71.26) * mm, "end": v(80.4, 72.1) * mm});
            skLineSegment(sketch, "E842", {"start": v(80.4, 72.1) * mm, "end": v(80.35, 75.81) * mm});
            skLineSegment(sketch, "E843", {"start": v(80.35, 75.81) * mm, "end": v(80.41, 75.82) * mm});
            skLineSegment(sketch, "E844", {"start": v(80.41, 75.82) * mm, "end": v(80.9, 75.85) * mm});
            skLineSegment(sketch, "E845", {"start": v(80.9, 75.85) * mm, "end": v(81.06, 75.85) * mm});
            skLineSegment(sketch, "E846", {"start": v(81.06, 75.85) * mm, "end": v(81.52, 75.85) * mm});
            skLineSegment(sketch, "E847", {"start": v(81.52, 75.85) * mm, "end": v(81.66, 75.85) * mm});
            skLineSegment(sketch, "E848", {"start": v(81.66, 75.85) * mm, "end": v(82.03, 75.77) * mm});
            skLineSegment(sketch, "E849", {"start": v(82.03, 75.77) * mm, "end": v(82.06, 75.75) * mm});
            skLineSegment(sketch, "E850", {"start": v(82.06, 75.75) * mm, "end": v(82.09, 75.74) * mm});
            skLineSegment(sketch, "E851", {"start": v(82.09, 75.74) * mm, "end": v(82.4, 75.43) * mm});
            skLineSegment(sketch, "E852", {"start": v(82.4, 75.43) * mm, "end": v(82.43, 75.38) * mm});
            skLineSegment(sketch, "E853", {"start": v(82.43, 75.38) * mm, "end": v(84.96, 71.12) * mm});
            skLineSegment(sketch, "E854", {"start": v(84.96, 71.12) * mm, "end": v(87.42, 71.12) * mm});
            skLineSegment(sketch, "E855", {"start": v(87.42, 71.12) * mm, "end": v(87.42, 71.26) * mm});
            skLineSegment(sketch, "E856", {"start": v(87.42, 71.26) * mm, "end": v(87.4, 71.27) * mm});
            skLineSegment(sketch, "E857", {"start": v(87.4, 71.27) * mm, "end": v(87.2, 71.41) * mm});
            skLineSegment(sketch, "E858", {"start": v(87.2, 71.41) * mm, "end": v(87.18, 71.44) * mm});
            skLineSegment(sketch, "E859", {"start": v(81.58, 76.6) * mm, "end": v(81, 76.6) * mm});
            skLineSegment(sketch, "E860", {"start": v(81, 76.6) * mm, "end": v(80.97, 76.6) * mm});
            skLineSegment(sketch, "E861", {"start": v(80.97, 76.6) * mm, "end": v(80.73, 76.6) * mm});
            skLineSegment(sketch, "E862", {"start": v(80.73, 76.6) * mm, "end": v(80.66, 76.6) * mm});
            skLineSegment(sketch, "E863", {"start": v(80.66, 76.6) * mm, "end": v(80.58, 76.6) * mm});
            skLineSegment(sketch, "E864", {"start": v(80.58, 76.6) * mm, "end": v(80.38, 76.62) * mm});
            skLineSegment(sketch, "E865", {"start": v(80.38, 76.62) * mm, "end": v(80.36, 76.62) * mm});
            skLineSegment(sketch, "E866", {"start": v(80.36, 76.62) * mm, "end": v(80.38, 81.07) * mm});
            skLineSegment(sketch, "E867", {"start": v(80.38, 81.07) * mm, "end": v(80.5, 81.07) * mm});
            skLineSegment(sketch, "E868", {"start": v(80.5, 81.07) * mm, "end": v(80.82, 81.1) * mm});
            skLineSegment(sketch, "E869", {"start": v(80.82, 81.1) * mm, "end": v(80.86, 81.1) * mm});
            skLineSegment(sketch, "E870", {"start": v(80.86, 81.1) * mm, "end": v(80.9, 81.1) * mm});
            skLineSegment(sketch, "E871", {"start": v(80.9, 81.1) * mm, "end": v(81.32, 81.1) * mm});
            skLineSegment(sketch, "E872", {"start": v(81.32, 81.1) * mm, "end": v(81.37, 81.1) * mm});
            skLineSegment(sketch, "E873", {"start": v(81.37, 81.1) * mm, "end": v(81.4, 81.11) * mm});
            skLineSegment(sketch, "E874", {"start": v(81.4, 81.11) * mm, "end": v(81.69, 81.13) * mm});
            skLineSegment(sketch, "E875", {"start": v(81.69, 81.13) * mm, "end": v(81.78, 81.13) * mm});
            skLineSegment(sketch, "E876", {"start": v(81.78, 81.13) * mm, "end": v(82.06, 81.13) * mm});
            skLineSegment(sketch, "E877", {"start": v(82.06, 81.13) * mm, "end": v(82.15, 81.13) * mm});
            skLineSegment(sketch, "E878", {"start": v(82.15, 81.13) * mm, "end": v(82.97, 80.98) * mm});
            skLineSegment(sketch, "E879", {"start": v(82.97, 80.98) * mm, "end": v(83.04, 80.96) * mm});
            skLineSegment(sketch, "E880", {"start": v(83.04, 80.96) * mm, "end": v(83.12, 80.93) * mm});
            skLineSegment(sketch, "E881", {"start": v(83.12, 80.93) * mm, "end": v(83.75, 80.51) * mm});
            skLineSegment(sketch, "E882", {"start": v(83.75, 80.51) * mm, "end": v(83.8, 80.46) * mm});
            skLineSegment(sketch, "E883", {"start": v(83.8, 80.46) * mm, "end": v(83.85, 80.41) * mm});
            skLineSegment(sketch, "E884", {"start": v(83.85, 80.41) * mm, "end": v(84.24, 79.84) * mm});
            skLineSegment(sketch, "E885", {"start": v(84.24, 79.84) * mm, "end": v(84.27, 79.78) * mm});
            skLineSegment(sketch, "E886", {"start": v(84.27, 79.78) * mm, "end": v(84.3, 79.71) * mm});
            skLineSegment(sketch, "E887", {"start": v(84.3, 79.71) * mm, "end": v(84.43, 79.14) * mm});
            skLineSegment(sketch, "E888", {"start": v(84.43, 79.14) * mm, "end": v(84.43, 78.94) * mm});
            skLineSegment(sketch, "E889", {"start": v(84.43, 78.94) * mm, "end": v(84.43, 78.7) * mm});
            skLineSegment(sketch, "E890", {"start": v(84.43, 78.7) * mm, "end": v(84.25, 77.94) * mm});
            skLineSegment(sketch, "E891", {"start": v(84.25, 77.94) * mm, "end": v(83.82, 77.3) * mm});
            skLineSegment(sketch, "E892", {"start": v(83.82, 77.3) * mm, "end": v(83.7, 77.2) * mm});
            skLineSegment(sketch, "E893", {"start": v(83.7, 77.2) * mm, "end": v(83.57, 77.1) * mm});
            skLineSegment(sketch, "E894", {"start": v(83.57, 77.1) * mm, "end": v(82.8, 76.75) * mm});
            skLineSegment(sketch, "E895", {"start": v(82.8, 76.75) * mm, "end": v(81.88, 76.6) * mm});
            skLineSegment(sketch, "E896", {"start": v(81.88, 76.6) * mm, "end": v(81.58, 76.6) * mm});
            skLineSegment(sketch, "E897", {"start": v(56.22, 77.38) * mm, "end": v(56.46, 77.6) * mm});
            skLineSegment(sketch, "E898", {"start": v(56.46, 77.6) * mm, "end": v(57.53, 78.61) * mm});
            skLineSegment(sketch, "E899", {"start": v(57.53, 78.61) * mm, "end": v(58.46, 79.48) * mm});
            skLineSegment(sketch, "E900", {"start": v(58.46, 79.48) * mm, "end": v(58.63, 79.63) * mm});
            skLineSegment(sketch, "E901", {"start": v(58.63, 79.63) * mm, "end": v(58.8, 79.78) * mm});
            skLineSegment(sketch, "E902", {"start": v(58.8, 79.78) * mm, "end": v(59.5, 80.4) * mm});
            skLineSegment(sketch, "E903", {"start": v(59.5, 80.4) * mm, "end": v(60.03, 80.88) * mm});
            skLineSegment(sketch, "E904", {"start": v(60.03, 80.88) * mm, "end": v(60.12, 80.96) * mm});
            skLineSegment(sketch, "E905", {"start": v(60.12, 80.96) * mm, "end": v(61.75, 81.81) * mm});
            skLineSegment(sketch, "E906", {"start": v(61.75, 81.81) * mm, "end": v(61.75, 81.92) * mm});
            skLineSegment(sketch, "E907", {"start": v(61.75, 81.92) * mm, "end": v(58.12, 81.92) * mm});
            skLineSegment(sketch, "E908", {"start": v(58.12, 81.92) * mm, "end": v(58.12, 81.81) * mm});
            skLineSegment(sketch, "E909", {"start": v(58.12, 81.81) * mm, "end": v(58.67, 80.97) * mm});
            skLineSegment(sketch, "E910", {"start": v(58.67, 80.97) * mm, "end": v(58.58, 80.87) * mm});
            skLineSegment(sketch, "E911", {"start": v(58.58, 80.87) * mm, "end": v(57.61, 79.9) * mm});
            skLineSegment(sketch, "E912", {"start": v(57.61, 79.9) * mm, "end": v(57.52, 79.8) * mm});
            skLineSegment(sketch, "E913", {"start": v(57.52, 79.8) * mm, "end": v(57.42, 79.71) * mm});
            skLineSegment(sketch, "E914", {"start": v(57.42, 79.71) * mm, "end": v(56.45, 78.8) * mm});
            skLineSegment(sketch, "E915", {"start": v(56.45, 78.8) * mm, "end": v(56.35, 78.72) * mm});
            skLineSegment(sketch, "E916", {"start": v(56.35, 78.72) * mm, "end": v(56.26, 78.63) * mm});
            skLineSegment(sketch, "E917", {"start": v(56.26, 78.63) * mm, "end": v(55.35, 77.79) * mm});
            skLineSegment(sketch, "E918", {"start": v(55.35, 77.79) * mm, "end": v(55.26, 77.7) * mm});
            skLineSegment(sketch, "E919", {"start": v(55.26, 77.7) * mm, "end": v(55.17, 77.63) * mm});
            skLineSegment(sketch, "E920", {"start": v(55.17, 77.63) * mm, "end": v(54.33, 76.9) * mm});
            skLineSegment(sketch, "E921", {"start": v(54.33, 76.9) * mm, "end": v(54.24, 76.84) * mm});
            skLineSegment(sketch, "E922", {"start": v(54.24, 76.84) * mm, "end": v(54.56, 76.52) * mm});
            skLineSegment(sketch, "E923", {"start": v(54.56, 76.52) * mm, "end": v(56.26, 74.72) * mm});
            skLineSegment(sketch, "E924", {"start": v(56.26, 74.72) * mm, "end": v(58.17, 72.59) * mm});
            skLineSegment(sketch, "E925", {"start": v(58.17, 72.59) * mm, "end": v(58.59, 72.1) * mm});
            skLineSegment(sketch, "E926", {"start": v(58.59, 72.1) * mm, "end": v(58.12, 71.26) * mm});
            skLineSegment(sketch, "E927", {"start": v(58.12, 71.26) * mm, "end": v(58.12, 71.12) * mm});
            skLineSegment(sketch, "E928", {"start": v(58.12, 71.12) * mm, "end": v(62.05, 71.12) * mm});
            skLineSegment(sketch, "E929", {"start": v(62.05, 71.12) * mm, "end": v(62.05, 71.26) * mm});
            skLineSegment(sketch, "E930", {"start": v(62.05, 71.26) * mm, "end": v(61.2, 72.1) * mm});
            skLineSegment(sketch, "E931", {"start": v(61.2, 72.1) * mm, "end": v(60.8, 72.53) * mm});
            skLineSegment(sketch, "E932", {"start": v(60.8, 72.53) * mm, "end": v(59.59, 73.79) * mm});
            skLineSegment(sketch, "E933", {"start": v(59.59, 73.79) * mm, "end": v(58.22, 75.22) * mm});
            skLineSegment(sketch, "E934", {"start": v(58.22, 75.22) * mm, "end": v(57.1, 76.42) * mm});
            skLineSegment(sketch, "E935", {"start": v(57.1, 76.42) * mm, "end": v(56.44, 77.14) * mm});
            skLineSegment(sketch, "E936", {"start": v(56.44, 77.14) * mm, "end": v(56.22, 77.38) * mm});
            skLineSegment(sketch, "E937", {"start": v(54.24, 80.93) * mm, "end": v(55.5, 81.81) * mm});
            skLineSegment(sketch, "E938", {"start": v(55.5, 81.81) * mm, "end": v(55.5, 81.92) * mm});
            skLineSegment(sketch, "E939", {"start": v(55.5, 81.92) * mm, "end": v(51.12, 81.92) * mm});
            skLineSegment(sketch, "E940", {"start": v(51.12, 81.92) * mm, "end": v(51.12, 81.81) * mm});
            skLineSegment(sketch, "E941", {"start": v(51.12, 81.81) * mm, "end": v(52.36, 80.93) * mm});
            skLineSegment(sketch, "E942", {"start": v(52.36, 80.93) * mm, "end": v(52.36, 80.2) * mm});
            skLineSegment(sketch, "E943", {"start": v(52.36, 80.2) * mm, "end": v(52.36, 72.9) * mm});
            skLineSegment(sketch, "E944", {"start": v(52.36, 72.9) * mm, "end": v(52.36, 72.16) * mm});
            skLineSegment(sketch, "E945", {"start": v(52.36, 72.16) * mm, "end": v(51.07, 71.26) * mm});
            skLineSegment(sketch, "E946", {"start": v(51.07, 71.26) * mm, "end": v(51.07, 71.12) * mm});
            skLineSegment(sketch, "E947", {"start": v(51.07, 71.12) * mm, "end": v(55.53, 71.12) * mm});
            skLineSegment(sketch, "E948", {"start": v(55.53, 71.12) * mm, "end": v(55.53, 71.26) * mm});
            skLineSegment(sketch, "E949", {"start": v(55.53, 71.26) * mm, "end": v(54.24, 72.16) * mm});
            skLineSegment(sketch, "E950", {"start": v(54.24, 72.16) * mm, "end": v(54.24, 72.9) * mm});
            skLineSegment(sketch, "E951", {"start": v(54.24, 72.9) * mm, "end": v(54.24, 80.21) * mm});
            skLineSegment(sketch, "E952", {"start": v(54.24, 80.21) * mm, "end": v(54.24, 80.93) * mm});
            skLineSegment(sketch, "E953", {"start": v(47.18, 72.1) * mm, "end": v(45.04, 72.1) * mm});
            skLineSegment(sketch, "E954", {"start": v(45.04, 72.1) * mm, "end": v(44.57, 72.1) * mm});
            skLineSegment(sketch, "E955", {"start": v(44.57, 72.1) * mm, "end": v(43.54, 72.1) * mm});
            skLineSegment(sketch, "E956", {"start": v(43.54, 72.1) * mm, "end": v(43.2, 72.1) * mm});
            skLineSegment(sketch, "E957", {"start": v(43.2, 72.1) * mm, "end": v(43.18, 72.85) * mm});
            skLineSegment(sketch, "E958", {"start": v(43.18, 72.85) * mm, "end": v(43.18, 80.2) * mm});
            skLineSegment(sketch, "E959", {"start": v(43.18, 80.2) * mm, "end": v(43.2, 80.93) * mm});
            skLineSegment(sketch, "E960", {"start": v(43.2, 80.93) * mm, "end": v(44.56, 81.8) * mm});
            skLineSegment(sketch, "E961", {"start": v(44.56, 81.8) * mm, "end": v(44.56, 81.91) * mm});
            skLineSegment(sketch, "E962", {"start": v(44.56, 81.91) * mm, "end": v(40.06, 81.91) * mm});
            skLineSegment(sketch, "E963", {"start": v(40.06, 81.91) * mm, "end": v(40.06, 81.8) * mm});
            skLineSegment(sketch, "E964", {"start": v(40.06, 81.8) * mm, "end": v(41.3, 80.93) * mm});
            skLineSegment(sketch, "E965", {"start": v(41.3, 80.93) * mm, "end": v(41.3, 80.2) * mm});
            skLineSegment(sketch, "E966", {"start": v(41.3, 80.2) * mm, "end": v(41.3, 72.9) * mm});
            skLineSegment(sketch, "E967", {"start": v(41.3, 72.9) * mm, "end": v(41.3, 72.16) * mm});
            skLineSegment(sketch, "E968", {"start": v(41.3, 72.16) * mm, "end": v(40.06, 71.26) * mm});
            skLineSegment(sketch, "E969", {"start": v(40.06, 71.26) * mm, "end": v(40.06, 71.12) * mm});
            skLineSegment(sketch, "E970", {"start": v(40.06, 71.12) * mm, "end": v(48.34, 71.12) * mm});
            skLineSegment(sketch, "E971", {"start": v(48.34, 71.12) * mm, "end": v(48.34, 73.53) * mm});
            skLineSegment(sketch, "E972", {"start": v(48.34, 73.53) * mm, "end": v(48.19, 73.53) * mm});
            skLineSegment(sketch, "E973", {"start": v(48.19, 73.53) * mm, "end": v(47.18, 72.1) * mm});
            skLineSegment(sketch, "E974", {"start": v(91.9, 72.54) * mm, "end": v(91.9, 72.68) * mm});
            skLineSegment(sketch, "E975", {"start": v(91.9, 72.68) * mm, "end": v(91.78, 73.1) * mm});
            skLineSegment(sketch, "E976", {"start": v(91.78, 73.1) * mm, "end": v(91.48, 73.54) * mm});
            skLineSegment(sketch, "E977", {"start": v(91.48, 73.54) * mm, "end": v(91.03, 73.85) * mm});
            skLineSegment(sketch, "E978", {"start": v(91.03, 73.85) * mm, "end": v(90.6, 73.96) * mm});
            skLineSegment(sketch, "E979", {"start": v(90.6, 73.96) * mm, "end": v(90.47, 73.96) * mm});
            skLineSegment(sketch, "E980", {"start": v(90.47, 73.96) * mm, "end": v(90.33, 73.96) * mm});
            skLineSegment(sketch, "E981", {"start": v(90.33, 73.96) * mm, "end": v(89.9, 73.85) * mm});
            skLineSegment(sketch, "E982", {"start": v(89.9, 73.85) * mm, "end": v(89.46, 73.54) * mm});
            skLineSegment(sketch, "E983", {"start": v(89.46, 73.54) * mm, "end": v(89.15, 73.09) * mm});
            skLineSegment(sketch, "E984", {"start": v(89.15, 73.09) * mm, "end": v(89.04, 72.67) * mm});
            skLineSegment(sketch, "E985", {"start": v(89.04, 72.67) * mm, "end": v(89.04, 72.53) * mm});
            skLineSegment(sketch, "E986", {"start": v(89.04, 72.53) * mm, "end": v(89.04, 72.4) * mm});
            skLineSegment(sketch, "E987", {"start": v(89.04, 72.4) * mm, "end": v(89.15, 71.98) * mm});
            skLineSegment(sketch, "E988", {"start": v(89.15, 71.98) * mm, "end": v(89.45, 71.53) * mm});
            skLineSegment(sketch, "E989", {"start": v(89.45, 71.53) * mm, "end": v(89.9, 71.22) * mm});
            skLineSegment(sketch, "E990", {"start": v(89.9, 71.22) * mm, "end": v(90.32, 71.11) * mm});
            skLineSegment(sketch, "E991", {"start": v(90.32, 71.11) * mm, "end": v(90.46, 71.11) * mm});
            skLineSegment(sketch, "E992", {"start": v(90.46, 71.11) * mm, "end": v(90.6, 71.11) * mm});
            skLineSegment(sketch, "E993", {"start": v(90.6, 71.11) * mm, "end": v(91.02, 71.23) * mm});
            skLineSegment(sketch, "E994", {"start": v(91.02, 71.23) * mm, "end": v(91.48, 71.54) * mm});
            skLineSegment(sketch, "E995", {"start": v(91.48, 71.54) * mm, "end": v(91.78, 71.99) * mm});
            skLineSegment(sketch, "E996", {"start": v(91.78, 71.99) * mm, "end": v(91.9, 72.4) * mm});
            skLineSegment(sketch, "E997", {"start": v(91.9, 72.4) * mm, "end": v(91.9, 72.54) * mm});
            skLineSegment(sketch, "E998", {"start": v(91.73, 72.54) * mm, "end": v(91.73, 72.42) * mm});
            skLineSegment(sketch, "E999", {"start": v(91.73, 72.42) * mm, "end": v(91.63, 72.05) * mm});
            skLineSegment(sketch, "E1000", {"start": v(91.63, 72.05) * mm, "end": v(91.36, 71.64) * mm});
            skLineSegment(sketch, "E1001", {"start": v(91.36, 71.64) * mm, "end": v(90.96, 71.37) * mm});
            skLineSegment(sketch, "E1002", {"start": v(90.96, 71.37) * mm, "end": v(90.59, 71.27) * mm});
            skLineSegment(sketch, "E1003", {"start": v(90.59, 71.27) * mm, "end": v(90.46, 71.27) * mm});
            skLineSegment(sketch, "E1004", {"start": v(90.46, 71.27) * mm, "end": v(90.34, 71.27) * mm});
            skLineSegment(sketch, "E1005", {"start": v(90.34, 71.27) * mm, "end": v(89.96, 71.37) * mm});
            skLineSegment(sketch, "E1006", {"start": v(89.96, 71.37) * mm, "end": v(89.57, 71.64) * mm});
            skLineSegment(sketch, "E1007", {"start": v(89.57, 71.64) * mm, "end": v(89.3, 72.04) * mm});
            skLineSegment(sketch, "E1008", {"start": v(89.3, 72.04) * mm, "end": v(89.2, 72.41) * mm});
            skLineSegment(sketch, "E1009", {"start": v(89.2, 72.41) * mm, "end": v(89.2, 72.53) * mm});
            skLineSegment(sketch, "E1010", {"start": v(89.2, 72.53) * mm, "end": v(89.2, 72.66) * mm});
            skLineSegment(sketch, "E1011", {"start": v(89.2, 72.66) * mm, "end": v(89.3, 73.03) * mm});
            skLineSegment(sketch, "E1012", {"start": v(89.3, 73.03) * mm, "end": v(89.57, 73.43) * mm});
            skLineSegment(sketch, "E1013", {"start": v(89.57, 73.43) * mm, "end": v(89.97, 73.7) * mm});
            skLineSegment(sketch, "E1014", {"start": v(89.97, 73.7) * mm, "end": v(90.34, 73.8) * mm});
            skLineSegment(sketch, "E1015", {"start": v(90.34, 73.8) * mm, "end": v(90.47, 73.8) * mm});
            skLineSegment(sketch, "E1016", {"start": v(90.47, 73.8) * mm, "end": v(90.6, 73.8) * mm});
            skLineSegment(sketch, "E1017", {"start": v(90.6, 73.8) * mm, "end": v(90.97, 73.7) * mm});
            skLineSegment(sketch, "E1018", {"start": v(90.97, 73.7) * mm, "end": v(91.37, 73.44) * mm});
            skLineSegment(sketch, "E1019", {"start": v(91.37, 73.44) * mm, "end": v(91.63, 73.04) * mm});
            skLineSegment(sketch, "E1020", {"start": v(91.63, 73.04) * mm, "end": v(91.73, 72.67) * mm});
            skLineSegment(sketch, "E1021", {"start": v(91.73, 72.67) * mm, "end": v(91.73, 72.54) * mm});
            skLineSegment(sketch, "E1022", {"start": v(91.15, 72.84) * mm, "end": v(91.15, 72.93) * mm});
            skLineSegment(sketch, "E1023", {"start": v(91.15, 72.93) * mm, "end": v(90.99, 73.2) * mm});
            skLineSegment(sketch, "E1024", {"start": v(90.99, 73.2) * mm, "end": v(90.66, 73.34) * mm});
            skLineSegment(sketch, "E1025", {"start": v(90.66, 73.34) * mm, "end": v(90.55, 73.34) * mm});
            skLineSegment(sketch, "E1026", {"start": v(90.55, 73.34) * mm, "end": v(89.88, 73.34) * mm});
            skLineSegment(sketch, "E1027", {"start": v(89.88, 73.34) * mm, "end": v(89.88, 71.82) * mm});
            skLineSegment(sketch, "E1028", {"start": v(89.88, 71.82) * mm, "end": v(90.21, 71.82) * mm});
            skLineSegment(sketch, "E1029", {"start": v(90.21, 71.82) * mm, "end": v(90.21, 72.3) * mm});
            skLineSegment(sketch, "E1030", {"start": v(90.21, 72.3) * mm, "end": v(90.48, 72.3) * mm});
            skLineSegment(sketch, "E1031", {"start": v(90.48, 72.3) * mm, "end": v(90.8, 71.82) * mm});
            skLineSegment(sketch, "E1032", {"start": v(90.8, 71.82) * mm, "end": v(91.2, 71.82) * mm});
            skLineSegment(sketch, "E1033", {"start": v(91.2, 71.82) * mm, "end": v(90.82, 72.36) * mm});
            skLineSegment(sketch, "E1034", {"start": v(90.82, 72.36) * mm, "end": v(90.87, 72.38) * mm});
            skLineSegment(sketch, "E1035", {"start": v(90.87, 72.38) * mm, "end": v(91.15, 72.72) * mm});
            skLineSegment(sketch, "E1036", {"start": v(91.15, 72.72) * mm, "end": v(91.15, 72.84) * mm});
            skLineSegment(sketch, "E1037", {"start": v(90.8, 72.82) * mm, "end": v(90.8, 72.76) * mm});
            skLineSegment(sketch, "E1038", {"start": v(90.8, 72.76) * mm, "end": v(90.61, 72.6) * mm});
            skLineSegment(sketch, "E1039", {"start": v(90.61, 72.6) * mm, "end": v(90.55, 72.6) * mm});
            skLineSegment(sketch, "E1040", {"start": v(90.55, 72.6) * mm, "end": v(90.21, 72.6) * mm});
            skLineSegment(sketch, "E1041", {"start": v(90.21, 72.6) * mm, "end": v(90.21, 73.04) * mm});
            skLineSegment(sketch, "E1042", {"start": v(90.21, 73.04) * mm, "end": v(90.54, 73.04) * mm});
            skLineSegment(sketch, "E1043", {"start": v(90.54, 73.04) * mm, "end": v(90.6, 73.04) * mm});
            skLineSegment(sketch, "E1044", {"start": v(90.6, 73.04) * mm, "end": v(90.8, 72.87) * mm});
            skLineSegment(sketch, "E1045", {"start": v(90.8, 72.87) * mm, "end": v(90.8, 72.82) * mm});
            skLineSegment(sketch, "E1046", {"start": v(62.65, 51.28) * mm, "end": v(62.65, 51.41) * mm});
            skLineSegment(sketch, "E1047", {"start": v(62.65, 51.41) * mm, "end": v(62.54, 51.83) * mm});
            skLineSegment(sketch, "E1048", {"start": v(62.54, 51.83) * mm, "end": v(62.24, 52.28) * mm});
            skLineSegment(sketch, "E1049", {"start": v(62.24, 52.28) * mm, "end": v(61.78, 52.58) * mm});
            skLineSegment(sketch, "E1050", {"start": v(61.78, 52.58) * mm, "end": v(61.36, 52.7) * mm});
            skLineSegment(sketch, "E1051", {"start": v(61.36, 52.7) * mm, "end": v(61.23, 52.7) * mm});
            skLineSegment(sketch, "E1052", {"start": v(61.23, 52.7) * mm, "end": v(61.08, 52.7) * mm});
            skLineSegment(sketch, "E1053", {"start": v(61.08, 52.7) * mm, "end": v(60.66, 52.58) * mm});
            skLineSegment(sketch, "E1054", {"start": v(60.66, 52.58) * mm, "end": v(60.21, 52.27) * mm});
            skLineSegment(sketch, "E1055", {"start": v(60.21, 52.27) * mm, "end": v(59.9, 51.82) * mm});
            skLineSegment(sketch, "E1056", {"start": v(59.9, 51.82) * mm, "end": v(59.8, 51.4) * mm});
            skLineSegment(sketch, "E1057", {"start": v(59.8, 51.4) * mm, "end": v(59.8, 51.27) * mm});
            skLineSegment(sketch, "E1058", {"start": v(59.8, 51.27) * mm, "end": v(59.8, 51.13) * mm});
            skLineSegment(sketch, "E1059", {"start": v(59.8, 51.13) * mm, "end": v(59.9, 50.72) * mm});
            skLineSegment(sketch, "E1060", {"start": v(59.9, 50.72) * mm, "end": v(60.2, 50.27) * mm});
            skLineSegment(sketch, "E1061", {"start": v(60.2, 50.27) * mm, "end": v(60.66, 49.96) * mm});
            skLineSegment(sketch, "E1062", {"start": v(60.66, 49.96) * mm, "end": v(61.08, 49.85) * mm});
            skLineSegment(sketch, "E1063", {"start": v(61.08, 49.85) * mm, "end": v(61.22, 49.85) * mm});
            skLineSegment(sketch, "E1064", {"start": v(61.22, 49.85) * mm, "end": v(61.36, 49.85) * mm});
            skLineSegment(sketch, "E1065", {"start": v(61.36, 49.85) * mm, "end": v(61.78, 49.96) * mm});
            skLineSegment(sketch, "E1066", {"start": v(61.78, 49.96) * mm, "end": v(62.23, 50.27) * mm});
            skLineSegment(sketch, "E1067", {"start": v(62.23, 50.27) * mm, "end": v(62.54, 50.72) * mm});
            skLineSegment(sketch, "E1068", {"start": v(62.54, 50.72) * mm, "end": v(62.65, 51.14) * mm});
            skLineSegment(sketch, "E1069", {"start": v(62.65, 51.14) * mm, "end": v(62.65, 51.28) * mm});
            skLineSegment(sketch, "E1070", {"start": v(62.48, 51.28) * mm, "end": v(62.48, 51.15) * mm});
            skLineSegment(sketch, "E1071", {"start": v(62.48, 51.15) * mm, "end": v(62.38, 50.78) * mm});
            skLineSegment(sketch, "E1072", {"start": v(62.38, 50.78) * mm, "end": v(62.12, 50.38) * mm});
            skLineSegment(sketch, "E1073", {"start": v(62.12, 50.38) * mm, "end": v(61.72, 50.1) * mm});
            skLineSegment(sketch, "E1074", {"start": v(61.72, 50.1) * mm, "end": v(61.34, 50) * mm});
            skLineSegment(sketch, "E1075", {"start": v(61.34, 50) * mm, "end": v(61.22, 50) * mm});
            skLineSegment(sketch, "E1076", {"start": v(61.22, 50) * mm, "end": v(61.1, 50) * mm});
            skLineSegment(sketch, "E1077", {"start": v(61.1, 50) * mm, "end": v(60.72, 50.1) * mm});
            skLineSegment(sketch, "E1078", {"start": v(60.72, 50.1) * mm, "end": v(60.32, 50.37) * mm});
            skLineSegment(sketch, "E1079", {"start": v(60.32, 50.37) * mm, "end": v(60.06, 50.78) * mm});
            skLineSegment(sketch, "E1080", {"start": v(60.06, 50.78) * mm, "end": v(59.96, 51.15) * mm});
            skLineSegment(sketch, "E1081", {"start": v(59.96, 51.15) * mm, "end": v(59.96, 51.27) * mm});
            skLineSegment(sketch, "E1082", {"start": v(59.96, 51.27) * mm, "end": v(59.96, 51.4) * mm});
            skLineSegment(sketch, "E1083", {"start": v(59.96, 51.4) * mm, "end": v(60.06, 51.76) * mm});
            skLineSegment(sketch, "E1084", {"start": v(60.06, 51.76) * mm, "end": v(60.32, 52.17) * mm});
            skLineSegment(sketch, "E1085", {"start": v(60.32, 52.17) * mm, "end": v(60.72, 52.44) * mm});
            skLineSegment(sketch, "E1086", {"start": v(60.72, 52.44) * mm, "end": v(61.1, 52.54) * mm});
            skLineSegment(sketch, "E1087", {"start": v(61.1, 52.54) * mm, "end": v(61.23, 52.54) * mm});
            skLineSegment(sketch, "E1088", {"start": v(61.23, 52.54) * mm, "end": v(61.35, 52.54) * mm});
            skLineSegment(sketch, "E1089", {"start": v(61.35, 52.54) * mm, "end": v(61.72, 52.44) * mm});
            skLineSegment(sketch, "E1090", {"start": v(61.72, 52.44) * mm, "end": v(62.12, 52.17) * mm});
            skLineSegment(sketch, "E1091", {"start": v(62.12, 52.17) * mm, "end": v(62.38, 51.77) * mm});
            skLineSegment(sketch, "E1092", {"start": v(62.38, 51.77) * mm, "end": v(62.48, 51.4) * mm});
            skLineSegment(sketch, "E1093", {"start": v(62.48, 51.4) * mm, "end": v(62.48, 51.28) * mm});
            skLineSegment(sketch, "E1094", {"start": v(61.9, 51.57) * mm, "end": v(61.9, 51.66) * mm});
            skLineSegment(sketch, "E1095", {"start": v(61.9, 51.66) * mm, "end": v(61.74, 51.94) * mm});
            skLineSegment(sketch, "E1096", {"start": v(61.74, 51.94) * mm, "end": v(61.42, 52.07) * mm});
            skLineSegment(sketch, "E1097", {"start": v(61.42, 52.07) * mm, "end": v(61.3, 52.07) * mm});
            skLineSegment(sketch, "E1098", {"start": v(61.3, 52.07) * mm, "end": v(60.64, 52.07) * mm});
            skLineSegment(sketch, "E1099", {"start": v(60.64, 52.07) * mm, "end": v(60.64, 50.56) * mm});
            skLineSegment(sketch, "E1100", {"start": v(60.64, 50.56) * mm, "end": v(60.97, 50.56) * mm});
            skLineSegment(sketch, "E1101", {"start": v(60.97, 50.56) * mm, "end": v(60.97, 51.04) * mm});
            skLineSegment(sketch, "E1102", {"start": v(60.97, 51.04) * mm, "end": v(61.23, 51.04) * mm});
            skLineSegment(sketch, "E1103", {"start": v(61.23, 51.04) * mm, "end": v(61.56, 50.56) * mm});
            skLineSegment(sketch, "E1104", {"start": v(61.56, 50.56) * mm, "end": v(61.95, 50.56) * mm});
            skLineSegment(sketch, "E1105", {"start": v(61.95, 50.56) * mm, "end": v(61.58, 51.1) * mm});
            skLineSegment(sketch, "E1106", {"start": v(61.58, 51.1) * mm, "end": v(61.62, 51.12) * mm});
            skLineSegment(sketch, "E1107", {"start": v(61.62, 51.12) * mm, "end": v(61.9, 51.46) * mm});
            skLineSegment(sketch, "E1108", {"start": v(61.9, 51.46) * mm, "end": v(61.9, 51.57) * mm});
            skLineSegment(sketch, "E1109", {"start": v(61.56, 51.55) * mm, "end": v(61.56, 51.5) * mm});
            skLineSegment(sketch, "E1110", {"start": v(61.56, 51.5) * mm, "end": v(61.37, 51.33) * mm});
            skLineSegment(sketch, "E1111", {"start": v(61.37, 51.33) * mm, "end": v(61.3, 51.33) * mm});
            skLineSegment(sketch, "E1112", {"start": v(61.3, 51.33) * mm, "end": v(60.97, 51.33) * mm});
            skLineSegment(sketch, "E1113", {"start": v(60.97, 51.33) * mm, "end": v(60.97, 51.78) * mm});
            skLineSegment(sketch, "E1114", {"start": v(60.97, 51.78) * mm, "end": v(61.3, 51.78) * mm});
            skLineSegment(sketch, "E1115", {"start": v(61.3, 51.78) * mm, "end": v(61.36, 51.78) * mm});
            skLineSegment(sketch, "E1116", {"start": v(61.36, 51.78) * mm, "end": v(61.56, 51.6) * mm});
            skLineSegment(sketch, "E1117", {"start": v(61.56, 51.6) * mm, "end": v(61.56, 51.55) * mm});
            skLineSegment(sketch, "E1118", {"start": v(-29.92, 96.85) * mm, "end": v(-29.92, 95.42) * mm});
            skLineSegment(sketch, "E1119", {"start": v(-29.92, 95.42) * mm, "end": v(-30.18, 95.42) * mm});
            skLineSegment(sketch, "E1120", {"start": v(-30.18, 95.42) * mm, "end": v(-30.18, 96.85) * mm});
            skLineSegment(sketch, "E1121", {"start": v(-30.18, 96.85) * mm, "end": v(-30.8, 96.85) * mm});
            skLineSegment(sketch, "E1122", {"start": v(-30.8, 96.85) * mm, "end": v(-30.8, 97.06) * mm});
            skLineSegment(sketch, "E1123", {"start": v(-30.8, 97.06) * mm, "end": v(-29.31, 97.06) * mm});
            skLineSegment(sketch, "E1124", {"start": v(-29.31, 97.06) * mm, "end": v(-29.31, 96.85) * mm});
            skLineSegment(sketch, "E1125", {"start": v(-29.31, 96.85) * mm, "end": v(-29.92, 96.85) * mm});
            skLineSegment(sketch, "E1126", {"start": v(-27.42, 95.42) * mm, "end": v(-27.42, 96.58) * mm});
            skLineSegment(sketch, "E1127", {"start": v(-27.42, 96.58) * mm, "end": v(-28.07, 95.6) * mm});
            skLineSegment(sketch, "E1128", {"start": v(-28.07, 95.6) * mm, "end": v(-28.72, 96.58) * mm});
            skLineSegment(sketch, "E1129", {"start": v(-28.72, 96.58) * mm, "end": v(-28.72, 95.42) * mm});
            skLineSegment(sketch, "E1130", {"start": v(-28.72, 95.42) * mm, "end": v(-29, 95.42) * mm});
            skLineSegment(sketch, "E1131", {"start": v(-29, 95.42) * mm, "end": v(-29, 97.06) * mm});
            skLineSegment(sketch, "E1132", {"start": v(-29, 97.06) * mm, "end": v(-28.72, 97.06) * mm});
            skLineSegment(sketch, "E1133", {"start": v(-28.72, 97.06) * mm, "end": v(-28.07, 96.05) * mm});
            skLineSegment(sketch, "E1134", {"start": v(-28.07, 96.05) * mm, "end": v(-27.42, 97.06) * mm});
            skLineSegment(sketch, "E1135", {"start": v(-27.42, 97.06) * mm, "end": v(-27.16, 97.06) * mm});
            skLineSegment(sketch, "E1136", {"start": v(-27.16, 97.06) * mm, "end": v(-27.16, 95.42) * mm});
            skLineSegment(sketch, "E1137", {"start": v(-27.16, 95.42) * mm, "end": v(-27.42, 95.42) * mm});
            skLineSegment(sketch, "E1138", {"start": v(8.48, 149.61) * mm, "end": v(8.42, 149.6) * mm});
            skLineSegment(sketch, "E1139", {"start": v(8.42, 149.6) * mm, "end": v(8.17, 149.45) * mm});
            skLineSegment(sketch, "E1140", {"start": v(8.17, 149.45) * mm, "end": v(8.09, 149.28) * mm});
            skLineSegment(sketch, "E1141", {"start": v(8.09, 149.28) * mm, "end": v(8.1, 149.24) * mm});
            skLineSegment(sketch, "E1142", {"start": v(8.1, 149.24) * mm, "end": v(8.13, 149.21) * mm});
            skLineSegment(sketch, "E1143", {"start": v(8.13, 149.21) * mm, "end": v(8.37, 149.16) * mm});
            skLineSegment(sketch, "E1144", {"start": v(8.37, 149.16) * mm, "end": v(8.8, 149.28) * mm});
            skLineSegment(sketch, "E1145", {"start": v(8.8, 149.28) * mm, "end": v(8.91, 149.33) * mm});
            skLineSegment(sketch, "E1146", {"start": v(8.91, 149.33) * mm, "end": v(9.03, 149.39) * mm});
            skLineSegment(sketch, "E1147", {"start": v(9.03, 149.39) * mm, "end": v(9.4, 149.63) * mm});
            skLineSegment(sketch, "E1148", {"start": v(9.4, 149.63) * mm, "end": v(9.38, 149.76) * mm});
            skLineSegment(sketch, "E1149", {"start": v(9.38, 149.76) * mm, "end": v(9.37, 149.76) * mm});
            skLineSegment(sketch, "E1150", {"start": v(9.37, 149.76) * mm, "end": v(9.02, 149.72) * mm});
            skLineSegment(sketch, "E1151", {"start": v(9.02, 149.72) * mm, "end": v(8.54, 149.64) * mm});
            skLineSegment(sketch, "E1152", {"start": v(8.54, 149.64) * mm, "end": v(8.48, 149.61) * mm});
            skLineSegment(sketch, "E1153", {"start": v(-14.67, 137.43) * mm, "end": v(-15, 137.37) * mm});
            skLineSegment(sketch, "E1154", {"start": v(-15, 137.37) * mm, "end": v(-16.1, 137.19) * mm});
            skLineSegment(sketch, "E1155", {"start": v(-16.1, 137.19) * mm, "end": v(-16.62, 137.05) * mm});
            skLineSegment(sketch, "E1156", {"start": v(-16.62, 137.05) * mm, "end": v(-16.65, 137.02) * mm});
            skLineSegment(sketch, "E1157", {"start": v(-16.65, 137.02) * mm, "end": v(-16.84, 136.86) * mm});
            skLineSegment(sketch, "E1158", {"start": v(-16.84, 136.86) * mm, "end": v(-17.31, 136.3) * mm});
            skLineSegment(sketch, "E1159", {"start": v(-17.31, 136.3) * mm, "end": v(-17.71, 135.62) * mm});
            skLineSegment(sketch, "E1160", {"start": v(-17.71, 135.62) * mm, "end": v(-17.88, 134.98) * mm});
            skLineSegment(sketch, "E1161", {"start": v(-17.88, 134.98) * mm, "end": v(-17.88, 134.39) * mm});
            skLineSegment(sketch, "E1162", {"start": v(-17.88, 134.39) * mm, "end": v(-17.74, 133.87) * mm});
            skLineSegment(sketch, "E1163", {"start": v(-17.74, 133.87) * mm, "end": v(-17.52, 133.43) * mm});
            skLineSegment(sketch, "E1164", {"start": v(-17.52, 133.43) * mm, "end": v(-17.24, 133.08) * mm});
            skLineSegment(sketch, "E1165", {"start": v(-17.24, 133.08) * mm, "end": v(-17.04, 132.9) * mm});
            skLineSegment(sketch, "E1166", {"start": v(-17.04, 132.9) * mm, "end": v(-16.97, 132.85) * mm});
            skLineSegment(sketch, "E1167", {"start": v(-16.97, 132.85) * mm, "end": v(-16.94, 132.83) * mm});
            skLineSegment(sketch, "E1168", {"start": v(-16.94, 132.83) * mm, "end": v(-16.83, 132.78) * mm});
            skLineSegment(sketch, "E1169", {"start": v(-16.83, 132.78) * mm, "end": v(-16.74, 132.8) * mm});
            skLineSegment(sketch, "E1170", {"start": v(-16.74, 132.8) * mm, "end": v(-16.66, 132.93) * mm});
            skLineSegment(sketch, "E1171", {"start": v(-16.66, 132.93) * mm, "end": v(-16.55, 133.17) * mm});
            skLineSegment(sketch, "E1172", {"start": v(-16.55, 133.17) * mm, "end": v(-16.36, 133.54) * mm});
            skLineSegment(sketch, "E1173", {"start": v(-16.36, 133.54) * mm, "end": v(-16.05, 134.07) * mm});
            skLineSegment(sketch, "E1174", {"start": v(-16.05, 134.07) * mm, "end": v(-15.58, 134.77) * mm});
            skLineSegment(sketch, "E1175", {"start": v(-15.58, 134.77) * mm, "end": v(-15.08, 135.44) * mm});
            skLineSegment(sketch, "E1176", {"start": v(-15.08, 135.44) * mm, "end": v(-14.9, 135.66) * mm});
            skLineSegment(sketch, "E1177", {"start": v(-14.9, 135.66) * mm, "end": v(-14.76, 135.84) * mm});
            skLineSegment(sketch, "E1178", {"start": v(-14.76, 135.84) * mm, "end": v(-14.24, 136.34) * mm});
            skLineSegment(sketch, "E1179", {"start": v(-14.24, 136.34) * mm, "end": v(-13.47, 136.98) * mm});
            skLineSegment(sketch, "E1180", {"start": v(-13.47, 136.98) * mm, "end": v(-12.77, 137.49) * mm});
            skLineSegment(sketch, "E1181", {"start": v(-12.77, 137.49) * mm, "end": v(-12.43, 137.73) * mm});
            skLineSegment(sketch, "E1182", {"start": v(-12.43, 137.73) * mm, "end": v(-12.36, 137.8) * mm});
            skLineSegment(sketch, "E1183", {"start": v(-12.36, 137.8) * mm, "end": v(-12.49, 137.83) * mm});
            skLineSegment(sketch, "E1184", {"start": v(-12.49, 137.83) * mm, "end": v(-13.03, 137.74) * mm});
            skLineSegment(sketch, "E1185", {"start": v(-13.03, 137.74) * mm, "end": v(-13.82, 137.59) * mm});
            skLineSegment(sketch, "E1186", {"start": v(-13.82, 137.59) * mm, "end": v(-14.46, 137.46) * mm});
            skLineSegment(sketch, "E1187", {"start": v(-14.46, 137.46) * mm, "end": v(-14.67, 137.43) * mm});
            skLineSegment(sketch, "E1188", {"start": v(4.13, 162.5) * mm, "end": v(4.16, 162.42) * mm});
            skLineSegment(sketch, "E1189", {"start": v(4.16, 162.42) * mm, "end": v(4.26, 162.14) * mm});
            skLineSegment(sketch, "E1190", {"start": v(4.26, 162.14) * mm, "end": v(4.3, 162.04) * mm});
            skLineSegment(sketch, "E1191", {"start": v(4.3, 162.04) * mm, "end": v(4.37, 162.02) * mm});
            skLineSegment(sketch, "E1192", {"start": v(4.37, 162.02) * mm, "end": v(4.53, 162.03) * mm});
            skLineSegment(sketch, "E1193", {"start": v(4.53, 162.03) * mm, "end": v(4.7, 162.13) * mm});
            skLineSegment(sketch, "E1194", {"start": v(4.7, 162.13) * mm, "end": v(4.8, 162.33) * mm});
            skLineSegment(sketch, "E1195", {"start": v(4.8, 162.33) * mm, "end": v(4.82, 162.4) * mm});
            skLineSegment(sketch, "E1196", {"start": v(4.82, 162.4) * mm, "end": v(4.83, 162.46) * mm});
            skLineSegment(sketch, "E1197", {"start": v(4.83, 162.46) * mm, "end": v(4.73, 162.68) * mm});
            skLineSegment(sketch, "E1198", {"start": v(4.73, 162.68) * mm, "end": v(4.46, 162.77) * mm});
            skLineSegment(sketch, "E1199", {"start": v(4.46, 162.77) * mm, "end": v(4.2, 162.7) * mm});
            skLineSegment(sketch, "E1200", {"start": v(4.2, 162.7) * mm, "end": v(4.12, 162.54) * mm});
            skLineSegment(sketch, "E1201", {"start": v(4.12, 162.54) * mm, "end": v(4.13, 162.5) * mm});
            skLineSegment(sketch, "E1202", {"start": v(5.21, 160.85) * mm, "end": v(5.22, 160.9) * mm});
            skLineSegment(sketch, "E1203", {"start": v(5.22, 160.9) * mm, "end": v(5.11, 161.1) * mm});
            skLineSegment(sketch, "E1204", {"start": v(5.11, 161.1) * mm, "end": v(4.88, 161.14) * mm});
            skLineSegment(sketch, "E1205", {"start": v(4.88, 161.14) * mm, "end": v(4.66, 161.05) * mm});
            skLineSegment(sketch, "E1206", {"start": v(4.66, 161.05) * mm, "end": v(4.6, 160.89) * mm});
            skLineSegment(sketch, "E1207", {"start": v(4.6, 160.89) * mm, "end": v(4.63, 160.85) * mm});
            skLineSegment(sketch, "E1208", {"start": v(4.63, 160.85) * mm, "end": v(4.66, 160.78) * mm});
            skLineSegment(sketch, "E1209", {"start": v(4.66, 160.78) * mm, "end": v(4.71, 160.46) * mm});
            skLineSegment(sketch, "E1210", {"start": v(4.71, 160.46) * mm, "end": v(4.7, 160.28) * mm});
            skLineSegment(sketch, "E1211", {"start": v(4.7, 160.28) * mm, "end": v(4.95, 160.38) * mm});
            skLineSegment(sketch, "E1212", {"start": v(4.95, 160.38) * mm, "end": v(5.2, 160.73) * mm});
            skLineSegment(sketch, "E1213", {"start": v(5.2, 160.73) * mm, "end": v(5.21, 160.85) * mm});
            skLineSegment(sketch, "E1214", {"start": v(11.64, 146.86) * mm, "end": v(11.73, 146.92) * mm});
            skLineSegment(sketch, "E1215", {"start": v(11.73, 146.92) * mm, "end": v(12.08, 147.1) * mm});
            skLineSegment(sketch, "E1216", {"start": v(12.08, 147.1) * mm, "end": v(12.34, 147.25) * mm});
            skLineSegment(sketch, "E1217", {"start": v(12.34, 147.25) * mm, "end": v(12.4, 147.3) * mm});
            skLineSegment(sketch, "E1218", {"start": v(12.4, 147.3) * mm, "end": v(12.44, 147.31) * mm});
            skLineSegment(sketch, "E1219", {"start": v(12.44, 147.31) * mm, "end": v(12.63, 147.52) * mm});
            skLineSegment(sketch, "E1220", {"start": v(12.63, 147.52) * mm, "end": v(12.72, 147.75) * mm});
            skLineSegment(sketch, "E1221", {"start": v(12.72, 147.75) * mm, "end": v(12.72, 147.8) * mm});
            skLineSegment(sketch, "E1222", {"start": v(12.72, 147.8) * mm, "end": v(12.71, 147.84) * mm});
            skLineSegment(sketch, "E1223", {"start": v(12.71, 147.84) * mm, "end": v(12.78, 147.97) * mm});
            skLineSegment(sketch, "E1224", {"start": v(12.78, 147.97) * mm, "end": v(12.98, 148.07) * mm});
            skLineSegment(sketch, "E1225", {"start": v(12.98, 148.07) * mm, "end": v(13.04, 148.1) * mm});
            skLineSegment(sketch, "E1226", {"start": v(13.04, 148.1) * mm, "end": v(13.1, 148.12) * mm});
            skLineSegment(sketch, "E1227", {"start": v(13.1, 148.12) * mm, "end": v(13.28, 148.26) * mm});
            skLineSegment(sketch, "E1228", {"start": v(13.28, 148.26) * mm, "end": v(13.38, 148.43) * mm});
            skLineSegment(sketch, "E1229", {"start": v(13.38, 148.43) * mm, "end": v(13.4, 148.48) * mm});
            skLineSegment(sketch, "E1230", {"start": v(13.4, 148.48) * mm, "end": v(13.41, 148.52) * mm});
            skLineSegment(sketch, "E1231", {"start": v(13.41, 148.52) * mm, "end": v(13.52, 148.8) * mm});
            skLineSegment(sketch, "E1232", {"start": v(13.52, 148.8) * mm, "end": v(13.59, 148.88) * mm});
            skLineSegment(sketch, "E1233", {"start": v(13.59, 148.88) * mm, "end": v(13.8, 148.98) * mm});
            skLineSegment(sketch, "E1234", {"start": v(13.8, 148.98) * mm, "end": v(13.87, 149) * mm});
            skLineSegment(sketch, "E1235", {"start": v(13.87, 149) * mm, "end": v(13.94, 149) * mm});
            skLineSegment(sketch, "E1236", {"start": v(13.94, 149) * mm, "end": v(14.3, 149.12) * mm});
            skLineSegment(sketch, "E1237", {"start": v(14.3, 149.12) * mm, "end": v(14.5, 149.4) * mm});
            skLineSegment(sketch, "E1238", {"start": v(14.5, 149.4) * mm, "end": v(14.5, 149.5) * mm});
            skLineSegment(sketch, "E1239", {"start": v(14.5, 149.5) * mm, "end": v(14.5, 149.58) * mm});
            skLineSegment(sketch, "E1240", {"start": v(14.5, 149.58) * mm, "end": v(14.44, 149.85) * mm});
            skLineSegment(sketch, "E1241", {"start": v(14.44, 149.85) * mm, "end": v(14.38, 150.06) * mm});
            skLineSegment(sketch, "E1242", {"start": v(14.38, 150.06) * mm, "end": v(14.37, 150.08) * mm});
            skLineSegment(sketch, "E1243", {"start": v(14.37, 150.08) * mm, "end": v(14.35, 150.08) * mm});
            skLineSegment(sketch, "E1244", {"start": v(14.35, 150.08) * mm, "end": v(14.33, 150.06) * mm});
            skLineSegment(sketch, "E1245", {"start": v(14.33, 150.06) * mm, "end": v(14.15, 149.93) * mm});
            skLineSegment(sketch, "E1246", {"start": v(14.15, 149.93) * mm, "end": v(13.84, 149.9) * mm});
            skLineSegment(sketch, "E1247", {"start": v(13.84, 149.9) * mm, "end": v(13.76, 149.93) * mm});
            skLineSegment(sketch, "E1248", {"start": v(13.76, 149.93) * mm, "end": v(13.64, 149.97) * mm});
            skLineSegment(sketch, "E1249", {"start": v(13.64, 149.97) * mm, "end": v(13.2, 150.17) * mm});
            skLineSegment(sketch, "E1250", {"start": v(13.2, 150.17) * mm, "end": v(12.9, 150.31) * mm});
            skLineSegment(sketch, "E1251", {"start": v(12.9, 150.31) * mm, "end": v(12.85, 150.33) * mm});
            skLineSegment(sketch, "E1252", {"start": v(12.85, 150.33) * mm, "end": v(12.78, 150.35) * mm});
            skLineSegment(sketch, "E1253", {"start": v(12.78, 150.35) * mm, "end": v(12.51, 150.38) * mm});
            skLineSegment(sketch, "E1254", {"start": v(12.51, 150.38) * mm, "end": v(12.43, 150.2) * mm});
            skLineSegment(sketch, "E1255", {"start": v(12.43, 150.2) * mm, "end": v(12.45, 150.17) * mm});
            skLineSegment(sketch, "E1256", {"start": v(12.45, 150.17) * mm, "end": v(12.48, 150.1) * mm});
            skLineSegment(sketch, "E1257", {"start": v(12.48, 150.1) * mm, "end": v(12.55, 149.88) * mm});
            skLineSegment(sketch, "E1258", {"start": v(12.55, 149.88) * mm, "end": v(12.5, 149.69) * mm});
            skLineSegment(sketch, "E1259", {"start": v(12.5, 149.69) * mm, "end": v(12.46, 149.65) * mm});
            skLineSegment(sketch, "E1260", {"start": v(12.46, 149.65) * mm, "end": v(12.43, 149.64) * mm});
            skLineSegment(sketch, "E1261", {"start": v(12.43, 149.64) * mm, "end": v(12.22, 149.5) * mm});
            skLineSegment(sketch, "E1262", {"start": v(12.22, 149.5) * mm, "end": v(12.2, 149.5) * mm});
            skLineSegment(sketch, "E1263", {"start": v(12.2, 149.5) * mm, "end": v(12.13, 149.46) * mm});
            skLineSegment(sketch, "E1264", {"start": v(12.13, 149.46) * mm, "end": v(11.9, 149.26) * mm});
            skLineSegment(sketch, "E1265", {"start": v(11.9, 149.26) * mm, "end": v(11.86, 149.07) * mm});
            skLineSegment(sketch, "E1266", {"start": v(11.86, 149.07) * mm, "end": v(11.86, 149.04) * mm});
            skLineSegment(sketch, "E1267", {"start": v(11.86, 149.04) * mm, "end": v(11.87, 149.02) * mm});
            skLineSegment(sketch, "E1268", {"start": v(11.87, 149.02) * mm, "end": v(11.87, 148.83) * mm});
            skLineSegment(sketch, "E1269", {"start": v(11.87, 148.83) * mm, "end": v(11.8, 148.65) * mm});
            skLineSegment(sketch, "E1270", {"start": v(11.8, 148.65) * mm, "end": v(11.75, 148.62) * mm});
            skLineSegment(sketch, "E1271", {"start": v(11.75, 148.62) * mm, "end": v(11.7, 148.58) * mm});
            skLineSegment(sketch, "E1272", {"start": v(11.7, 148.58) * mm, "end": v(11.42, 148.19) * mm});
            skLineSegment(sketch, "E1273", {"start": v(11.42, 148.19) * mm, "end": v(11.42, 148.14) * mm});
            skLineSegment(sketch, "E1274", {"start": v(11.42, 148.14) * mm, "end": v(11.43, 148.1) * mm});
            skLineSegment(sketch, "E1275", {"start": v(11.43, 148.1) * mm, "end": v(11.22, 147.76) * mm});
            skLineSegment(sketch, "E1276", {"start": v(11.22, 147.76) * mm, "end": v(11.18, 147.73) * mm});
            skLineSegment(sketch, "E1277", {"start": v(11.18, 147.73) * mm, "end": v(11.13, 147.7) * mm});
            skLineSegment(sketch, "E1278", {"start": v(11.13, 147.7) * mm, "end": v(10.8, 147.58) * mm});
            skLineSegment(sketch, "E1279", {"start": v(10.8, 147.58) * mm, "end": v(10.2, 147.52) * mm});
            skLineSegment(sketch, "E1280", {"start": v(10.2, 147.52) * mm, "end": v(10.03, 147.5) * mm});
            skLineSegment(sketch, "E1281", {"start": v(10.03, 147.5) * mm, "end": v(9.85, 147.48) * mm});
            skLineSegment(sketch, "E1282", {"start": v(9.85, 147.48) * mm, "end": v(9.27, 147.52) * mm});
            skLineSegment(sketch, "E1283", {"start": v(9.27, 147.52) * mm, "end": v(8.9, 147.64) * mm});
            skLineSegment(sketch, "E1284", {"start": v(8.9, 147.64) * mm, "end": v(8.84, 147.66) * mm});
            skLineSegment(sketch, "E1285", {"start": v(8.84, 147.66) * mm, "end": v(8.77, 147.68) * mm});
            skLineSegment(sketch, "E1286", {"start": v(8.77, 147.68) * mm, "end": v(8.5, 147.64) * mm});
            skLineSegment(sketch, "E1287", {"start": v(8.5, 147.64) * mm, "end": v(8.37, 147.47) * mm});
            skLineSegment(sketch, "E1288", {"start": v(8.37, 147.47) * mm, "end": v(8.37, 147.41) * mm});
            skLineSegment(sketch, "E1289", {"start": v(8.37, 147.41) * mm, "end": v(8.36, 147.37) * mm});
            skLineSegment(sketch, "E1290", {"start": v(8.36, 147.37) * mm, "end": v(8.38, 147.21) * mm});
            skLineSegment(sketch, "E1291", {"start": v(8.38, 147.21) * mm, "end": v(8.52, 147.14) * mm});
            skLineSegment(sketch, "E1292", {"start": v(8.52, 147.14) * mm, "end": v(8.57, 147.13) * mm});
            skLineSegment(sketch, "E1293", {"start": v(8.57, 147.13) * mm, "end": v(8.61, 147.13) * mm});
            skLineSegment(sketch, "E1294", {"start": v(8.61, 147.13) * mm, "end": v(8.73, 147.03) * mm});
            skLineSegment(sketch, "E1295", {"start": v(8.73, 147.03) * mm, "end": v(8.59, 146.91) * mm});
            skLineSegment(sketch, "E1296", {"start": v(8.59, 146.91) * mm, "end": v(8.54, 146.9) * mm});
            skLineSegment(sketch, "E1297", {"start": v(8.54, 146.9) * mm, "end": v(8.52, 146.9) * mm});
            skLineSegment(sketch, "E1298", {"start": v(8.52, 146.9) * mm, "end": v(8.47, 146.82) * mm});
            skLineSegment(sketch, "E1299", {"start": v(8.47, 146.82) * mm, "end": v(8.6, 146.7) * mm});
            skLineSegment(sketch, "E1300", {"start": v(8.6, 146.7) * mm, "end": v(8.82, 146.58) * mm});
            skLineSegment(sketch, "E1301", {"start": v(8.82, 146.58) * mm, "end": v(8.98, 146.51) * mm});
            skLineSegment(sketch, "E1302", {"start": v(8.98, 146.51) * mm, "end": v(9.04, 146.5) * mm});
            skLineSegment(sketch, "E1303", {"start": v(9.04, 146.5) * mm, "end": v(9.05, 146.5) * mm});
            skLineSegment(sketch, "E1304", {"start": v(9.05, 146.5) * mm, "end": v(9.12, 146.47) * mm});
            skLineSegment(sketch, "E1305", {"start": v(9.12, 146.47) * mm, "end": v(9.15, 146.47) * mm});
            skLineSegment(sketch, "E1306", {"start": v(9.15, 146.47) * mm, "end": v(9.06, 146.28) * mm});
            skLineSegment(sketch, "E1307", {"start": v(9.06, 146.28) * mm, "end": v(8.78, 145.72) * mm});
            skLineSegment(sketch, "E1308", {"start": v(8.78, 145.72) * mm, "end": v(8.15, 144.44) * mm});
            skLineSegment(sketch, "E1309", {"start": v(8.15, 144.44) * mm, "end": v(7.29, 142.72) * mm});
            skLineSegment(sketch, "E1310", {"start": v(7.29, 142.72) * mm, "end": v(6.24, 140.64) * mm});
            skLineSegment(sketch, "E1311", {"start": v(6.24, 140.64) * mm, "end": v(5.05, 138.26) * mm});
            skLineSegment(sketch, "E1312", {"start": v(5.05, 138.26) * mm, "end": v(3.75, 135.68) * mm});
            skLineSegment(sketch, "E1313", {"start": v(3.75, 135.68) * mm, "end": v(2.38, 132.97) * mm});
            skLineSegment(sketch, "E1314", {"start": v(2.38, 132.97) * mm, "end": v(0.99, 130.2) * mm});
            skLineSegment(sketch, "E1315", {"start": v(0.99, 130.2) * mm, "end": v(-0.4, 127.46) * mm});
            skLineSegment(sketch, "E1316", {"start": v(-0.4, 127.46) * mm, "end": v(-1.72, 124.83) * mm});
            skLineSegment(sketch, "E1317", {"start": v(-1.72, 124.83) * mm, "end": v(-2.96, 122.37) * mm});
            skLineSegment(sketch, "E1318", {"start": v(-2.96, 122.37) * mm, "end": v(-4.06, 120.18) * mm});
            skLineSegment(sketch, "E1319", {"start": v(-4.06, 120.18) * mm, "end": v(-5, 118.33) * mm});
            skLineSegment(sketch, "E1320", {"start": v(-5, 118.33) * mm, "end": v(-5.72, 116.89) * mm});
            skLineSegment(sketch, "E1321", {"start": v(-5.72, 116.89) * mm, "end": v(-6.2, 115.95) * mm});
            skLineSegment(sketch, "E1322", {"start": v(-6.2, 115.95) * mm, "end": v(-6.34, 115.65) * mm});
            skLineSegment(sketch, "E1323", {"start": v(-6.34, 115.65) * mm, "end": v(-6.37, 115.58) * mm});
            skLineSegment(sketch, "E1324", {"start": v(-6.37, 115.58) * mm, "end": v(-6.38, 115.56) * mm});
            skLineSegment(sketch, "E1325", {"start": v(-6.38, 115.56) * mm, "end": v(-6.31, 115.4) * mm});
            skLineSegment(sketch, "E1326", {"start": v(-6.31, 115.4) * mm, "end": v(-6.3, 115.4) * mm});
            skLineSegment(sketch, "E1327", {"start": v(-6.3, 115.4) * mm, "end": v(-6.28, 115.38) * mm});
            skLineSegment(sketch, "E1328", {"start": v(-6.28, 115.38) * mm, "end": v(-6.08, 115.4) * mm});
            skLineSegment(sketch, "E1329", {"start": v(-6.08, 115.4) * mm, "end": v(-6.07, 115.42) * mm});
            skLineSegment(sketch, "E1330", {"start": v(-6.07, 115.42) * mm, "end": v(-6.04, 115.47) * mm});
            skLineSegment(sketch, "E1331", {"start": v(-6.04, 115.47) * mm, "end": v(-5.86, 115.8) * mm});
            skLineSegment(sketch, "E1332", {"start": v(-5.86, 115.8) * mm, "end": v(-5.32, 116.81) * mm});
            skLineSegment(sketch, "E1333", {"start": v(-5.32, 116.81) * mm, "end": v(-4.49, 118.37) * mm});
            skLineSegment(sketch, "E1334", {"start": v(-4.49, 118.37) * mm, "end": v(-3.42, 120.37) * mm});
            skLineSegment(sketch, "E1335", {"start": v(-3.42, 120.37) * mm, "end": v(-2.16, 122.74) * mm});
            skLineSegment(sketch, "E1336", {"start": v(-2.16, 122.74) * mm, "end": v(-0.75, 125.37) * mm});
            skLineSegment(sketch, "E1337", {"start": v(-0.75, 125.37) * mm, "end": v(0.75, 128.18) * mm});
            skLineSegment(sketch, "E1338", {"start": v(0.75, 128.18) * mm, "end": v(2.3, 131.08) * mm});
            skLineSegment(sketch, "E1339", {"start": v(2.3, 131.08) * mm, "end": v(3.83, 133.98) * mm});
            skLineSegment(sketch, "E1340", {"start": v(3.83, 133.98) * mm, "end": v(5.33, 136.79) * mm});
            skLineSegment(sketch, "E1341", {"start": v(5.33, 136.79) * mm, "end": v(6.72, 139.41) * mm});
            skLineSegment(sketch, "E1342", {"start": v(6.72, 139.41) * mm, "end": v(7.97, 141.76) * mm});
            skLineSegment(sketch, "E1343", {"start": v(7.97, 141.76) * mm, "end": v(9.03, 143.75) * mm});
            skLineSegment(sketch, "E1344", {"start": v(9.03, 143.75) * mm, "end": v(9.84, 145.28) * mm});
            skLineSegment(sketch, "E1345", {"start": v(9.84, 145.28) * mm, "end": v(10.37, 146.26) * mm});
            skLineSegment(sketch, "E1346", {"start": v(10.37, 146.26) * mm, "end": v(10.55, 146.6) * mm});
            skLineSegment(sketch, "E1347", {"start": v(10.55, 146.6) * mm, "end": v(10.65, 146.62) * mm});
            skLineSegment(sketch, "E1348", {"start": v(10.65, 146.62) * mm, "end": v(11.17, 146.7) * mm});
            skLineSegment(sketch, "E1349", {"start": v(11.17, 146.7) * mm, "end": v(11.59, 146.83) * mm});
            skLineSegment(sketch, "E1350", {"start": v(11.59, 146.83) * mm, "end": v(11.64, 146.86) * mm});
            skLineSegment(sketch, "E1351", {"start": v(12.5, 151.39) * mm, "end": v(12.58, 151.39) * mm});
            skLineSegment(sketch, "E1352", {"start": v(12.58, 151.39) * mm, "end": v(12.82, 151.32) * mm});
            skLineSegment(sketch, "E1353", {"start": v(12.82, 151.32) * mm, "end": v(13, 151.25) * mm});
            skLineSegment(sketch, "E1354", {"start": v(13, 151.25) * mm, "end": v(13.24, 151.7) * mm});
            skLineSegment(sketch, "E1355", {"start": v(13.24, 151.7) * mm, "end": v(13.37, 151.71) * mm});
            skLineSegment(sketch, "E1356", {"start": v(13.37, 151.71) * mm, "end": v(13.73, 151.83) * mm});
            skLineSegment(sketch, "E1357", {"start": v(13.73, 151.83) * mm, "end": v(14.12, 152.11) * mm});
            skLineSegment(sketch, "E1358", {"start": v(14.12, 152.11) * mm, "end": v(14.37, 152.52) * mm});
            skLineSegment(sketch, "E1359", {"start": v(14.37, 152.52) * mm, "end": v(14.47, 152.88) * mm});
            skLineSegment(sketch, "E1360", {"start": v(14.47, 152.88) * mm, "end": v(14.47, 153) * mm});
            skLineSegment(sketch, "E1361", {"start": v(14.47, 153) * mm, "end": v(14.47, 153.13) * mm});
            skLineSegment(sketch, "E1362", {"start": v(14.47, 153.13) * mm, "end": v(14.36, 153.52) * mm});
            skLineSegment(sketch, "E1363", {"start": v(14.36, 153.52) * mm, "end": v(14.08, 153.94) * mm});
            skLineSegment(sketch, "E1364", {"start": v(14.08, 153.94) * mm, "end": v(13.66, 154.22) * mm});
            skLineSegment(sketch, "E1365", {"start": v(13.66, 154.22) * mm, "end": v(13.28, 154.32) * mm});
            skLineSegment(sketch, "E1366", {"start": v(13.28, 154.32) * mm, "end": v(13.15, 154.32) * mm});
            skLineSegment(sketch, "E1367", {"start": v(13.15, 154.32) * mm, "end": v(12.95, 154.32) * mm});
            skLineSegment(sketch, "E1368", {"start": v(12.95, 154.32) * mm, "end": v(12.42, 154.1) * mm});
            skLineSegment(sketch, "E1369", {"start": v(12.42, 154.1) * mm, "end": v(12.36, 154.05) * mm});
            skLineSegment(sketch, "E1370", {"start": v(12.36, 154.05) * mm, "end": v(12.4, 154.05) * mm});
            skLineSegment(sketch, "E1371", {"start": v(12.4, 154.05) * mm, "end": v(12.42, 154.05) * mm});
            skLineSegment(sketch, "E1372", {"start": v(12.42, 154.05) * mm, "end": v(12.46, 154.06) * mm});
            skLineSegment(sketch, "E1373", {"start": v(12.46, 154.06) * mm, "end": v(12.77, 154.1) * mm});
            skLineSegment(sketch, "E1374", {"start": v(12.77, 154.1) * mm, "end": v(12.8, 154.08) * mm});
            skLineSegment(sketch, "E1375", {"start": v(12.8, 154.08) * mm, "end": v(12.81, 154.05) * mm});
            skLineSegment(sketch, "E1376", {"start": v(12.81, 154.05) * mm, "end": v(12.83, 154.03) * mm});
            skLineSegment(sketch, "E1377", {"start": v(12.83, 154.03) * mm, "end": v(12.78, 153.89) * mm});
            skLineSegment(sketch, "E1378", {"start": v(12.78, 153.89) * mm, "end": v(12.66, 153.66) * mm});
            skLineSegment(sketch, "E1379", {"start": v(12.66, 153.66) * mm, "end": v(12.66, 153.6) * mm});
            skLineSegment(sketch, "E1380", {"start": v(12.66, 153.6) * mm, "end": v(12.65, 153.57) * mm});
            skLineSegment(sketch, "E1381", {"start": v(12.65, 153.57) * mm, "end": v(12.54, 153.37) * mm});
            skLineSegment(sketch, "E1382", {"start": v(12.54, 153.37) * mm, "end": v(12.52, 153.36) * mm});
            skLineSegment(sketch, "E1383", {"start": v(12.52, 153.36) * mm, "end": v(12.49, 153.35) * mm});
            skLineSegment(sketch, "E1384", {"start": v(12.49, 153.35) * mm, "end": v(12.22, 153.4) * mm});
            skLineSegment(sketch, "E1385", {"start": v(12.22, 153.4) * mm, "end": v(12.2, 153.42) * mm});
            skLineSegment(sketch, "E1386", {"start": v(12.2, 153.42) * mm, "end": v(12.19, 153.44) * mm});
            skLineSegment(sketch, "E1387", {"start": v(12.19, 153.44) * mm, "end": v(12.09, 153.62) * mm});
            skLineSegment(sketch, "E1388", {"start": v(12.09, 153.62) * mm, "end": v(12.09, 153.68) * mm});
            skLineSegment(sketch, "E1389", {"start": v(12.09, 153.68) * mm, "end": v(12.09, 153.69) * mm});
            skLineSegment(sketch, "E1390", {"start": v(12.09, 153.69) * mm, "end": v(12.03, 153.69) * mm});
            skLineSegment(sketch, "E1391", {"start": v(12.03, 153.69) * mm, "end": v(12.03, 153.68) * mm});
            skLineSegment(sketch, "E1392", {"start": v(12.03, 153.68) * mm, "end": v(12, 153.64) * mm});
            skLineSegment(sketch, "E1393", {"start": v(12, 153.64) * mm, "end": v(11.84, 153.16) * mm});
            skLineSegment(sketch, "E1394", {"start": v(11.84, 153.16) * mm, "end": v(11.84, 153) * mm});
            skLineSegment(sketch, "E1395", {"start": v(11.84, 153) * mm, "end": v(11.84, 152.84) * mm});
            skLineSegment(sketch, "E1396", {"start": v(11.84, 152.84) * mm, "end": v(12.01, 152.38) * mm});
            skLineSegment(sketch, "E1397", {"start": v(12.01, 152.38) * mm, "end": v(12.05, 152.33) * mm});
            skLineSegment(sketch, "E1398", {"start": v(12.05, 152.33) * mm, "end": v(12, 152.22) * mm});
            skLineSegment(sketch, "E1399", {"start": v(12, 152.22) * mm, "end": v(11.74, 151.63) * mm});
            skLineSegment(sketch, "E1400", {"start": v(11.74, 151.63) * mm, "end": v(11.55, 151.18) * mm});
            skLineSegment(sketch, "E1401", {"start": v(11.55, 151.18) * mm, "end": v(11.55, 151.15) * mm});
            skLineSegment(sketch, "E1402", {"start": v(11.55, 151.15) * mm, "end": v(11.54, 151.14) * mm});
            skLineSegment(sketch, "E1403", {"start": v(11.54, 151.14) * mm, "end": v(11.6, 151.1) * mm});
            skLineSegment(sketch, "E1404", {"start": v(11.6, 151.1) * mm, "end": v(11.82, 151.2) * mm});
            skLineSegment(sketch, "E1405", {"start": v(11.82, 151.2) * mm, "end": v(12.14, 151.32) * mm});
            skLineSegment(sketch, "E1406", {"start": v(12.14, 151.32) * mm, "end": v(12.4, 151.39) * mm});
            skLineSegment(sketch, "E1407", {"start": v(12.4, 151.39) * mm, "end": v(12.5, 151.39) * mm});
            skLineSegment(sketch, "E1408", {"start": v(24.4, 103.83) * mm, "end": v(24.33, 103.83) * mm});
            skLineSegment(sketch, "E1409", {"start": v(24.33, 103.83) * mm, "end": v(24.11, 103.7) * mm});
            skLineSegment(sketch, "E1410", {"start": v(24.11, 103.7) * mm, "end": v(24.02, 103.77) * mm});
            skLineSegment(sketch, "E1411", {"start": v(24.02, 103.77) * mm, "end": v(23.75, 103.88) * mm});
            skLineSegment(sketch, "E1412", {"start": v(23.75, 103.88) * mm, "end": v(23.36, 103.92) * mm});
            skLineSegment(sketch, "E1413", {"start": v(23.36, 103.92) * mm, "end": v(22.98, 103.83) * mm});
            skLineSegment(sketch, "E1414", {"start": v(22.98, 103.83) * mm, "end": v(22.87, 103.77) * mm});
            skLineSegment(sketch, "E1415", {"start": v(22.87, 103.77) * mm, "end": v(22.84, 103.74) * mm});
            skLineSegment(sketch, "E1416", {"start": v(22.84, 103.74) * mm, "end": v(22.67, 103.51) * mm});
            skLineSegment(sketch, "E1417", {"start": v(22.67, 103.51) * mm, "end": v(22.53, 103.17) * mm});
            skLineSegment(sketch, "E1418", {"start": v(22.53, 103.17) * mm, "end": v(22.51, 103.08) * mm});
            skLineSegment(sketch, "E1419", {"start": v(22.51, 103.08) * mm, "end": v(22.5, 102.98) * mm});
            skLineSegment(sketch, "E1420", {"start": v(22.5, 102.98) * mm, "end": v(22.42, 102.5) * mm});
            skLineSegment(sketch, "E1421", {"start": v(22.42, 102.5) * mm, "end": v(22.33, 102.17) * mm});
            skLineSegment(sketch, "E1422", {"start": v(22.33, 102.17) * mm, "end": v(22.3, 102.15) * mm});
            skLineSegment(sketch, "E1423", {"start": v(22.3, 102.15) * mm, "end": v(22.29, 102.14) * mm});
            skLineSegment(sketch, "E1424", {"start": v(22.29, 102.14) * mm, "end": v(22.09, 102.13) * mm});
            skLineSegment(sketch, "E1425", {"start": v(22.09, 102.13) * mm, "end": v(22.06, 102.14) * mm});
            skLineSegment(sketch, "E1426", {"start": v(22.06, 102.14) * mm, "end": v(21.97, 102.17) * mm});
            skLineSegment(sketch, "E1427", {"start": v(21.97, 102.17) * mm, "end": v(21.7, 102.27) * mm});
            skLineSegment(sketch, "E1428", {"start": v(21.7, 102.27) * mm, "end": v(21.46, 102.12) * mm});
            skLineSegment(sketch, "E1429", {"start": v(21.46, 102.12) * mm, "end": v(21.39, 102.06) * mm});
            skLineSegment(sketch, "E1430", {"start": v(21.39, 102.06) * mm, "end": v(21.3, 102) * mm});
            skLineSegment(sketch, "E1431", {"start": v(21.3, 102) * mm, "end": v(21, 101.87) * mm});
            skLineSegment(sketch, "E1432", {"start": v(21, 101.87) * mm, "end": v(20.42, 101.72) * mm});
            skLineSegment(sketch, "E1433", {"start": v(20.42, 101.72) * mm, "end": v(19.82, 101.72) * mm});
            skLineSegment(sketch, "E1434", {"start": v(19.82, 101.72) * mm, "end": v(19.43, 101.84) * mm});
            skLineSegment(sketch, "E1435", {"start": v(19.43, 101.84) * mm, "end": v(19.34, 101.93) * mm});
            skLineSegment(sketch, "E1436", {"start": v(19.34, 101.93) * mm, "end": v(19.34, 101.96) * mm});
            skLineSegment(sketch, "E1437", {"start": v(19.34, 101.96) * mm, "end": v(19.38, 101.96) * mm});
            skLineSegment(sketch, "E1438", {"start": v(19.38, 101.96) * mm, "end": v(19.59, 101.94) * mm});
            skLineSegment(sketch, "E1439", {"start": v(19.59, 101.94) * mm, "end": v(20.03, 101.96) * mm});
            skLineSegment(sketch, "E1440", {"start": v(20.03, 101.96) * mm, "end": v(20.59, 102.14) * mm});
            skLineSegment(sketch, "E1441", {"start": v(20.59, 102.14) * mm, "end": v(21.04, 102.42) * mm});
            skLineSegment(sketch, "E1442", {"start": v(21.04, 102.42) * mm, "end": v(21.17, 102.54) * mm});
            skLineSegment(sketch, "E1443", {"start": v(21.17, 102.54) * mm, "end": v(21.2, 102.56) * mm});
            skLineSegment(sketch, "E1444", {"start": v(21.2, 102.56) * mm, "end": v(21.43, 102.76) * mm});
            skLineSegment(sketch, "E1445", {"start": v(21.43, 102.76) * mm, "end": v(21.45, 102.78) * mm});
            skLineSegment(sketch, "E1446", {"start": v(21.45, 102.78) * mm, "end": v(21.46, 102.78) * mm});
            skLineSegment(sketch, "E1447", {"start": v(21.46, 102.78) * mm, "end": v(21.44, 102.81) * mm});
            skLineSegment(sketch, "E1448", {"start": v(21.44, 102.81) * mm, "end": v(21.43, 102.81) * mm});
            skLineSegment(sketch, "E1449", {"start": v(21.43, 102.81) * mm, "end": v(21.4, 102.8) * mm});
            skLineSegment(sketch, "E1450", {"start": v(21.4, 102.8) * mm, "end": v(21.1, 102.7) * mm});
            skLineSegment(sketch, "E1451", {"start": v(21.1, 102.7) * mm, "end": v(21.07, 102.68) * mm});
            skLineSegment(sketch, "E1452", {"start": v(21.07, 102.68) * mm, "end": v(20.81, 102.6) * mm});
            skLineSegment(sketch, "E1453", {"start": v(20.81, 102.6) * mm, "end": v(19.36, 102.56) * mm});
            skLineSegment(sketch, "E1454", {"start": v(19.36, 102.56) * mm, "end": v(17.66, 102.86) * mm});
            skLineSegment(sketch, "E1455", {"start": v(17.66, 102.86) * mm, "end": v(17.28, 102.95) * mm});
            skLineSegment(sketch, "E1456", {"start": v(17.28, 102.95) * mm, "end": v(17.2, 102.97) * mm});
            skLineSegment(sketch, "E1457", {"start": v(17.2, 102.97) * mm, "end": v(16.47, 103.28) * mm});
            skLineSegment(sketch, "E1458", {"start": v(16.47, 103.28) * mm, "end": v(16.4, 103.32) * mm});
            skLineSegment(sketch, "E1459", {"start": v(16.4, 103.32) * mm, "end": v(16.4, 103.36) * mm});
            skLineSegment(sketch, "E1460", {"start": v(16.4, 103.36) * mm, "end": v(16.28, 103.7) * mm});
            skLineSegment(sketch, "E1461", {"start": v(16.28, 103.7) * mm, "end": v(16.23, 103.74) * mm});
            skLineSegment(sketch, "E1462", {"start": v(16.23, 103.74) * mm, "end": v(16.2, 103.76) * mm});
            skLineSegment(sketch, "E1463", {"start": v(16.2, 103.76) * mm, "end": v(15.73, 103.89) * mm});
            skLineSegment(sketch, "E1464", {"start": v(15.73, 103.89) * mm, "end": v(15.68, 103.9) * mm});
            skLineSegment(sketch, "E1465", {"start": v(15.68, 103.9) * mm, "end": v(15.64, 103.92) * mm});
            skLineSegment(sketch, "E1466", {"start": v(15.64, 103.92) * mm, "end": v(15.3, 104.36) * mm});
            skLineSegment(sketch, "E1467", {"start": v(15.3, 104.36) * mm, "end": v(15.26, 104.4) * mm});
            skLineSegment(sketch, "E1468", {"start": v(15.26, 104.4) * mm, "end": v(15.14, 104.64) * mm});
            skLineSegment(sketch, "E1469", {"start": v(15.14, 104.64) * mm, "end": v(14.2, 106.6) * mm});
            skLineSegment(sketch, "E1470", {"start": v(14.2, 106.6) * mm, "end": v(13, 109.45) * mm});
            skLineSegment(sketch, "E1471", {"start": v(13, 109.45) * mm, "end": v(12.74, 110.12) * mm});
            skLineSegment(sketch, "E1472", {"start": v(12.74, 110.12) * mm, "end": v(12.55, 110.63) * mm});
            skLineSegment(sketch, "E1473", {"start": v(12.55, 110.63) * mm, "end": v(12.02, 112.18) * mm});
            skLineSegment(sketch, "E1474", {"start": v(12.02, 112.18) * mm, "end": v(11.44, 114.01) * mm});
            skLineSegment(sketch, "E1475", {"start": v(11.44, 114.01) * mm, "end": v(11, 115.5) * mm});
            skLineSegment(sketch, "E1476", {"start": v(11, 115.5) * mm, "end": v(10.8, 116.27) * mm});
            skLineSegment(sketch, "E1477", {"start": v(10.8, 116.27) * mm, "end": v(10.74, 116.52) * mm});
            skLineSegment(sketch, "E1478", {"start": v(10.74, 116.52) * mm, "end": v(10.67, 116.8) * mm});
            skLineSegment(sketch, "E1479", {"start": v(10.67, 116.8) * mm, "end": v(10.65, 116.84) * mm});
            skLineSegment(sketch, "E1480", {"start": v(10.65, 116.84) * mm, "end": v(10.65, 116.86) * mm});
            skLineSegment(sketch, "E1481", {"start": v(10.65, 116.86) * mm, "end": v(10.62, 116.95) * mm});
            skLineSegment(sketch, "E1482", {"start": v(10.62, 116.95) * mm, "end": v(10.62, 116.94) * mm});
            skLineSegment(sketch, "E1483", {"start": v(10.62, 116.94) * mm, "end": v(10.61, 117) * mm});
            skLineSegment(sketch, "E1484", {"start": v(10.61, 117) * mm, "end": v(10.49, 117.44) * mm});
            skLineSegment(sketch, "E1485", {"start": v(10.49, 117.44) * mm, "end": v(10.47, 117.48) * mm});
            skLineSegment(sketch, "E1486", {"start": v(10.47, 117.48) * mm, "end": v(10.47, 117.49) * mm});
            skLineSegment(sketch, "E1487", {"start": v(10.47, 117.49) * mm, "end": v(10.46, 117.54) * mm});
            skLineSegment(sketch, "E1488", {"start": v(10.46, 117.54) * mm, "end": v(10.45, 117.55) * mm});
            skLineSegment(sketch, "E1489", {"start": v(10.45, 117.55) * mm, "end": v(10.37, 117.52) * mm});
            skLineSegment(sketch, "E1490", {"start": v(10.37, 117.52) * mm, "end": v(10.3, 117.24) * mm});
            skLineSegment(sketch, "E1491", {"start": v(10.3, 117.24) * mm, "end": v(10.27, 116.82) * mm});
            skLineSegment(sketch, "E1492", {"start": v(10.27, 116.82) * mm, "end": v(10.27, 116.47) * mm});
            skLineSegment(sketch, "E1493", {"start": v(10.27, 116.47) * mm, "end": v(10.29, 116.36) * mm});
            skLineSegment(sketch, "E1494", {"start": v(10.29, 116.36) * mm, "end": v(10.24, 116.3) * mm});
            skLineSegment(sketch, "E1495", {"start": v(10.24, 116.3) * mm, "end": v(9.84, 115.5) * mm});
            skLineSegment(sketch, "E1496", {"start": v(9.84, 115.5) * mm, "end": v(9.8, 115.4) * mm});
            skLineSegment(sketch, "E1497", {"start": v(9.8, 115.4) * mm, "end": v(9.7, 115.16) * mm});
            skLineSegment(sketch, "E1498", {"start": v(9.7, 115.16) * mm, "end": v(9.26, 114.05) * mm});
            skLineSegment(sketch, "E1499", {"start": v(9.26, 114.05) * mm, "end": v(8.68, 113.13) * mm});
            skLineSegment(sketch, "E1500", {"start": v(8.68, 113.13) * mm, "end": v(8.5, 113) * mm});
            skLineSegment(sketch, "E1501", {"start": v(8.5, 113) * mm, "end": v(8.36, 112.9) * mm});
            skLineSegment(sketch, "E1502", {"start": v(8.36, 112.9) * mm, "end": v(7.83, 112.55) * mm});
            skLineSegment(sketch, "E1503", {"start": v(7.83, 112.55) * mm, "end": v(7.53, 112.37) * mm});
            skLineSegment(sketch, "E1504", {"start": v(7.53, 112.37) * mm, "end": v(7.51, 112.35) * mm});
            skLineSegment(sketch, "E1505", {"start": v(7.51, 112.35) * mm, "end": v(7.5, 112.34) * mm});
            skLineSegment(sketch, "E1506", {"start": v(7.5, 112.34) * mm, "end": v(7.51, 112.25) * mm});
            skLineSegment(sketch, "E1507", {"start": v(7.51, 112.25) * mm, "end": v(7.63, 112.2) * mm});
            skLineSegment(sketch, "E1508", {"start": v(7.63, 112.2) * mm, "end": v(7.66, 112.18) * mm});
            skLineSegment(sketch, "E1509", {"start": v(7.66, 112.18) * mm, "end": v(7.68, 112.18) * mm});
            skLineSegment(sketch, "E1510", {"start": v(7.68, 112.18) * mm, "end": v(7.84, 112.06) * mm});
            skLineSegment(sketch, "E1511", {"start": v(7.84, 112.06) * mm, "end": v(7.85, 112.04) * mm});
            skLineSegment(sketch, "E1512", {"start": v(7.85, 112.04) * mm, "end": v(7.87, 112) * mm});
            skLineSegment(sketch, "E1513", {"start": v(7.87, 112) * mm, "end": v(8.06, 111.61) * mm});
            skLineSegment(sketch, "E1514", {"start": v(8.06, 111.61) * mm, "end": v(8.07, 111.58) * mm});
            skLineSegment(sketch, "E1515", {"start": v(8.07, 111.58) * mm, "end": v(8.08, 111.56) * mm});
            skLineSegment(sketch, "E1516", {"start": v(8.08, 111.56) * mm, "end": v(8.12, 111.44) * mm});
            skLineSegment(sketch, "E1517", {"start": v(8.12, 111.44) * mm, "end": v(8.12, 111.42) * mm});
            skLineSegment(sketch, "E1518", {"start": v(8.12, 111.42) * mm, "end": v(8.21, 111.18) * mm});
            skLineSegment(sketch, "E1519", {"start": v(8.21, 111.18) * mm, "end": v(8.48, 110.46) * mm});
            skLineSegment(sketch, "E1520", {"start": v(8.48, 110.46) * mm, "end": v(8.97, 109.22) * mm});
            skLineSegment(sketch, "E1521", {"start": v(8.97, 109.22) * mm, "end": v(9.65, 107.8) * mm});
            skLineSegment(sketch, "E1522", {"start": v(9.65, 107.8) * mm, "end": v(10.3, 106.62) * mm});
            skLineSegment(sketch, "E1523", {"start": v(10.3, 106.62) * mm, "end": v(10.55, 106.25) * mm});
            skLineSegment(sketch, "E1524", {"start": v(10.55, 106.25) * mm, "end": v(10.7, 106) * mm});
            skLineSegment(sketch, "E1525", {"start": v(10.7, 106) * mm, "end": v(11.18, 105.3) * mm});
            skLineSegment(sketch, "E1526", {"start": v(11.18, 105.3) * mm, "end": v(11.72, 104.46) * mm});
            skLineSegment(sketch, "E1527", {"start": v(11.72, 104.46) * mm, "end": v(12.03, 103.95) * mm});
            skLineSegment(sketch, "E1528", {"start": v(12.03, 103.95) * mm, "end": v(11.95, 103.95) * mm});
            skLineSegment(sketch, "E1529", {"start": v(11.95, 103.95) * mm, "end": v(11.94, 103.97) * mm});
            skLineSegment(sketch, "E1530", {"start": v(11.94, 103.97) * mm, "end": v(11.74, 104.15) * mm});
            skLineSegment(sketch, "E1531", {"start": v(11.74, 104.15) * mm, "end": v(11.17, 104.74) * mm});
            skLineSegment(sketch, "E1532", {"start": v(11.17, 104.74) * mm, "end": v(10.37, 105.64) * mm});
            skLineSegment(sketch, "E1533", {"start": v(10.37, 105.64) * mm, "end": v(9.62, 106.56) * mm});
            skLineSegment(sketch, "E1534", {"start": v(9.62, 106.56) * mm, "end": v(9.16, 107.18) * mm});
            skLineSegment(sketch, "E1535", {"start": v(9.16, 107.18) * mm, "end": v(9.02, 107.39) * mm});
            skLineSegment(sketch, "E1536", {"start": v(9.02, 107.39) * mm, "end": v(8.93, 107.53) * mm});
            skLineSegment(sketch, "E1537", {"start": v(8.93, 107.53) * mm, "end": v(8.46, 108.4) * mm});
            skLineSegment(sketch, "E1538", {"start": v(8.46, 108.4) * mm, "end": v(8, 109.42) * mm});
            skLineSegment(sketch, "E1539", {"start": v(8, 109.42) * mm, "end": v(7.93, 109.62) * mm});
            skLineSegment(sketch, "E1540", {"start": v(7.93, 109.62) * mm, "end": v(7.85, 109.78) * mm});
            skLineSegment(sketch, "E1541", {"start": v(7.85, 109.78) * mm, "end": v(7.55, 110.59) * mm});
            skLineSegment(sketch, "E1542", {"start": v(7.55, 110.59) * mm, "end": v(7.36, 111.24) * mm});
            skLineSegment(sketch, "E1543", {"start": v(7.36, 111.24) * mm, "end": v(7.34, 111.32) * mm});
            skLineSegment(sketch, "E1544", {"start": v(7.34, 111.32) * mm, "end": v(7.34, 111.34) * mm});
            skLineSegment(sketch, "E1545", {"start": v(7.34, 111.34) * mm, "end": v(7.33, 111.4) * mm});
            skLineSegment(sketch, "E1546", {"start": v(7.33, 111.4) * mm, "end": v(7.32, 111.43) * mm});
            skLineSegment(sketch, "E1547", {"start": v(7.32, 111.43) * mm, "end": v(7.2, 111.68) * mm});
            skLineSegment(sketch, "E1548", {"start": v(7.2, 111.68) * mm, "end": v(7.2, 111.7) * mm});
            skLineSegment(sketch, "E1549", {"start": v(7.2, 111.7) * mm, "end": v(7.15, 111.77) * mm});
            skLineSegment(sketch, "E1550", {"start": v(7.15, 111.77) * mm, "end": v(6.92, 111.97) * mm});
            skLineSegment(sketch, "E1551", {"start": v(6.92, 111.97) * mm, "end": v(6.68, 112) * mm});
            skLineSegment(sketch, "E1552", {"start": v(6.68, 112) * mm, "end": v(6.64, 111.98) * mm});
            skLineSegment(sketch, "E1553", {"start": v(6.64, 111.98) * mm, "end": v(6.6, 111.96) * mm});
            skLineSegment(sketch, "E1554", {"start": v(6.6, 111.96) * mm, "end": v(6.29, 111.78) * mm});
            skLineSegment(sketch, "E1555", {"start": v(6.29, 111.78) * mm, "end": v(6.04, 111.66) * mm});
            skLineSegment(sketch, "E1556", {"start": v(6.04, 111.66) * mm, "end": v(6.13, 111.38) * mm});
            skLineSegment(sketch, "E1557", {"start": v(6.13, 111.38) * mm, "end": v(6.43, 110.6) * mm});
            skLineSegment(sketch, "E1558", {"start": v(6.43, 110.6) * mm, "end": v(7, 109.4) * mm});
            skLineSegment(sketch, "E1559", {"start": v(7, 109.4) * mm, "end": v(7.64, 108.26) * mm});
            skLineSegment(sketch, "E1560", {"start": v(7.64, 108.26) * mm, "end": v(7.88, 107.89) * mm});
            skLineSegment(sketch, "E1561", {"start": v(7.88, 107.89) * mm, "end": v(8.11, 107.53) * mm});
            skLineSegment(sketch, "E1562", {"start": v(8.11, 107.53) * mm, "end": v(8.83, 106.48) * mm});
            skLineSegment(sketch, "E1563", {"start": v(8.83, 106.48) * mm, "end": v(9.6, 105.46) * mm});
            skLineSegment(sketch, "E1564", {"start": v(9.6, 105.46) * mm, "end": v(10.27, 104.65) * mm});
            skLineSegment(sketch, "E1565", {"start": v(10.27, 104.65) * mm, "end": v(10.76, 104.08) * mm});
            skLineSegment(sketch, "E1566", {"start": v(10.76, 104.08) * mm, "end": v(10.92, 103.88) * mm});
            skLineSegment(sketch, "E1567", {"start": v(10.92, 103.88) * mm, "end": v(10.94, 103.85) * mm});
            skLineSegment(sketch, "E1568", {"start": v(10.94, 103.85) * mm, "end": v(11.17, 103.56) * mm});
            skLineSegment(sketch, "E1569", {"start": v(11.17, 103.56) * mm, "end": v(11.19, 103.53) * mm});
            skLineSegment(sketch, "E1570", {"start": v(11.19, 103.53) * mm, "end": v(11.23, 103.48) * mm});
            skLineSegment(sketch, "E1571", {"start": v(11.23, 103.48) * mm, "end": v(11.54, 103) * mm});
            skLineSegment(sketch, "E1572", {"start": v(11.54, 103) * mm, "end": v(11.58, 102.95) * mm});
            skLineSegment(sketch, "E1573", {"start": v(11.58, 102.95) * mm, "end": v(11.57, 102.9) * mm});
            skLineSegment(sketch, "E1574", {"start": v(11.57, 102.9) * mm, "end": v(11.59, 102.6) * mm});
            skLineSegment(sketch, "E1575", {"start": v(11.59, 102.6) * mm, "end": v(11.7, 102.28) * mm});
            skLineSegment(sketch, "E1576", {"start": v(11.7, 102.28) * mm, "end": v(11.73, 102.23) * mm});
            skLineSegment(sketch, "E1577", {"start": v(11.73, 102.23) * mm, "end": v(11.75, 102.21) * mm});
            skLineSegment(sketch, "E1578", {"start": v(11.75, 102.21) * mm, "end": v(11.91, 102.11) * mm});
            skLineSegment(sketch, "E1579", {"start": v(11.91, 102.11) * mm, "end": v(11.94, 102.1) * mm});
            skLineSegment(sketch, "E1580", {"start": v(11.94, 102.1) * mm, "end": v(11.96, 102.1) * mm});
            skLineSegment(sketch, "E1581", {"start": v(11.96, 102.1) * mm, "end": v(12.05, 102.08) * mm});
            skLineSegment(sketch, "E1582", {"start": v(12.05, 102.08) * mm, "end": v(12.18, 102.01) * mm});
            skLineSegment(sketch, "E1583", {"start": v(12.18, 102.01) * mm, "end": v(12.27, 101.86) * mm});
            skLineSegment(sketch, "E1584", {"start": v(12.27, 101.86) * mm, "end": v(12.25, 101.64) * mm});
            skLineSegment(sketch, "E1585", {"start": v(12.25, 101.64) * mm, "end": v(12.23, 101.58) * mm});
            skLineSegment(sketch, "E1586", {"start": v(12.23, 101.58) * mm, "end": v(12.21, 101.56) * mm});
            skLineSegment(sketch, "E1587", {"start": v(12.21, 101.56) * mm, "end": v(12.11, 101.38) * mm});
            skLineSegment(sketch, "E1588", {"start": v(12.11, 101.38) * mm, "end": v(12.1, 101.36) * mm});
            skLineSegment(sketch, "E1589", {"start": v(12.1, 101.36) * mm, "end": v(12.09, 101.32) * mm});
            skLineSegment(sketch, "E1590", {"start": v(12.09, 101.32) * mm, "end": v(12.1, 100.98) * mm});
            skLineSegment(sketch, "E1591", {"start": v(12.1, 100.98) * mm, "end": v(12.12, 100.95) * mm});
            skLineSegment(sketch, "E1592", {"start": v(12.12, 100.95) * mm, "end": v(12.15, 100.88) * mm});
            skLineSegment(sketch, "E1593", {"start": v(12.15, 100.88) * mm, "end": v(12.35, 100.63) * mm});
            skLineSegment(sketch, "E1594", {"start": v(12.35, 100.63) * mm, "end": v(12.53, 100.43) * mm});
            skLineSegment(sketch, "E1595", {"start": v(12.53, 100.43) * mm, "end": v(12.54, 100.4) * mm});
            skLineSegment(sketch, "E1596", {"start": v(12.54, 100.4) * mm, "end": v(12.56, 100.35) * mm});
            skLineSegment(sketch, "E1597", {"start": v(12.56, 100.35) * mm, "end": v(12.63, 100.05) * mm});
            skLineSegment(sketch, "E1598", {"start": v(12.63, 100.05) * mm, "end": v(12.75, 99.58) * mm});
            skLineSegment(sketch, "E1599", {"start": v(12.75, 99.58) * mm, "end": v(12.8, 99.45) * mm});
            skLineSegment(sketch, "E1600", {"start": v(12.8, 99.45) * mm, "end": v(12.8, 99.41) * mm});
            skLineSegment(sketch, "E1601", {"start": v(12.8, 99.41) * mm, "end": v(12.91, 99.14) * mm});
            skLineSegment(sketch, "E1602", {"start": v(12.91, 99.14) * mm, "end": v(12.92, 99.11) * mm});
            skLineSegment(sketch, "E1603", {"start": v(12.92, 99.11) * mm, "end": v(12.94, 99.07) * mm});
            skLineSegment(sketch, "E1604", {"start": v(12.94, 99.07) * mm, "end": v(13.12, 98.64) * mm});
            skLineSegment(sketch, "E1605", {"start": v(13.12, 98.64) * mm, "end": v(13.14, 98.6) * mm});
            skLineSegment(sketch, "E1606", {"start": v(13.14, 98.6) * mm, "end": v(13.23, 98.44) * mm});
            skLineSegment(sketch, "E1607", {"start": v(13.23, 98.44) * mm, "end": v(13.54, 98) * mm});
            skLineSegment(sketch, "E1608", {"start": v(13.54, 98) * mm, "end": v(13.97, 97.5) * mm});
            skLineSegment(sketch, "E1609", {"start": v(13.97, 97.5) * mm, "end": v(14.31, 97.14) * mm});
            skLineSegment(sketch, "E1610", {"start": v(14.31, 97.14) * mm, "end": v(14.46, 97.02) * mm});
            skLineSegment(sketch, "E1611", {"start": v(14.46, 97.02) * mm, "end": v(15.23, 96.21) * mm});
            skLineSegment(sketch, "E1612", {"start": v(15.23, 96.21) * mm, "end": v(15.58, 96.31) * mm});
            skLineSegment(sketch, "E1613", {"start": v(15.58, 96.31) * mm, "end": v(16.34, 96.63) * mm});
            skLineSegment(sketch, "E1614", {"start": v(16.34, 96.63) * mm, "end": v(16.55, 96.73) * mm});
            skLineSegment(sketch, "E1615", {"start": v(16.55, 96.73) * mm, "end": v(16.76, 96.83) * mm});
            skLineSegment(sketch, "E1616", {"start": v(16.76, 96.83) * mm, "end": v(17.46, 97.26) * mm});
            skLineSegment(sketch, "E1617", {"start": v(17.46, 97.26) * mm, "end": v(17.74, 97.47) * mm});
            skLineSegment(sketch, "E1618", {"start": v(17.74, 97.47) * mm, "end": v(17.57, 98.36) * mm});
            skLineSegment(sketch, "E1619", {"start": v(17.57, 98.36) * mm, "end": v(18.1, 98.57) * mm});
            skLineSegment(sketch, "E1620", {"start": v(18.1, 98.57) * mm, "end": v(18.23, 98.62) * mm});
            skLineSegment(sketch, "E1621", {"start": v(18.23, 98.62) * mm, "end": v(18.76, 98.76) * mm});
            skLineSegment(sketch, "E1622", {"start": v(18.76, 98.76) * mm, "end": v(19.77, 99) * mm});
            skLineSegment(sketch, "E1623", {"start": v(19.77, 99) * mm, "end": v(20.91, 99.34) * mm});
            skLineSegment(sketch, "E1624", {"start": v(20.91, 99.34) * mm, "end": v(21.7, 99.64) * mm});
            skLineSegment(sketch, "E1625", {"start": v(21.7, 99.64) * mm, "end": v(21.94, 99.78) * mm});
            skLineSegment(sketch, "E1626", {"start": v(21.94, 99.78) * mm, "end": v(22.2, 99.91) * mm});
            skLineSegment(sketch, "E1627", {"start": v(22.2, 99.91) * mm, "end": v(22.87, 100.48) * mm});
            skLineSegment(sketch, "E1628", {"start": v(22.87, 100.48) * mm, "end": v(23.74, 101.47) * mm});
            skLineSegment(sketch, "E1629", {"start": v(23.74, 101.47) * mm, "end": v(24.44, 102.52) * mm});
            skLineSegment(sketch, "E1630", {"start": v(24.44, 102.52) * mm, "end": v(24.75, 103.18) * mm});
            skLineSegment(sketch, "E1631", {"start": v(24.75, 103.18) * mm, "end": v(24.8, 103.4) * mm});
            skLineSegment(sketch, "E1632", {"start": v(24.8, 103.4) * mm, "end": v(24.81, 103.46) * mm});
            skLineSegment(sketch, "E1633", {"start": v(24.81, 103.46) * mm, "end": v(24.65, 103.7) * mm});
            skLineSegment(sketch, "E1634", {"start": v(24.65, 103.7) * mm, "end": v(24.42, 103.82) * mm});
            skLineSegment(sketch, "E1635", {"start": v(24.42, 103.82) * mm, "end": v(24.4, 103.83) * mm});
            skLineSegment(sketch, "E1636", {"start": v(13.89, 99.19) * mm, "end": v(13.85, 99.16) * mm});
            skLineSegment(sketch, "E1637", {"start": v(13.85, 99.16) * mm, "end": v(13.55, 99.19) * mm});
            skLineSegment(sketch, "E1638", {"start": v(13.55, 99.19) * mm, "end": v(13.2, 99.5) * mm});
            skLineSegment(sketch, "E1639", {"start": v(13.2, 99.5) * mm, "end": v(13.14, 99.61) * mm});
            skLineSegment(sketch, "E1640", {"start": v(13.14, 99.61) * mm, "end": v(13.12, 99.67) * mm});
            skLineSegment(sketch, "E1641", {"start": v(13.12, 99.67) * mm, "end": v(12.97, 100.35) * mm});
            skLineSegment(sketch, "E1642", {"start": v(12.97, 100.35) * mm, "end": v(12.96, 100.41) * mm});
            skLineSegment(sketch, "E1643", {"start": v(12.96, 100.41) * mm, "end": v(12.95, 100.47) * mm});
            skLineSegment(sketch, "E1644", {"start": v(12.95, 100.47) * mm, "end": v(13.17, 100.7) * mm});
            skLineSegment(sketch, "E1645", {"start": v(13.17, 100.7) * mm, "end": v(13.54, 100.74) * mm});
            skLineSegment(sketch, "E1646", {"start": v(13.54, 100.74) * mm, "end": v(13.6, 100.7) * mm});
            skLineSegment(sketch, "E1647", {"start": v(13.6, 100.7) * mm, "end": v(13.67, 100.67) * mm});
            skLineSegment(sketch, "E1648", {"start": v(13.67, 100.67) * mm, "end": v(13.8, 100.35) * mm});
            skLineSegment(sketch, "E1649", {"start": v(13.8, 100.35) * mm, "end": v(13.78, 100.1) * mm});
            skLineSegment(sketch, "E1650", {"start": v(13.78, 100.1) * mm, "end": v(13.78, 100) * mm});
            skLineSegment(sketch, "E1651", {"start": v(13.78, 100) * mm, "end": v(13.8, 99.65) * mm});
            skLineSegment(sketch, "E1652", {"start": v(13.8, 99.65) * mm, "end": v(13.87, 99.4) * mm});
            skLineSegment(sketch, "E1653", {"start": v(13.87, 99.4) * mm, "end": v(13.92, 99.26) * mm});
            skLineSegment(sketch, "E1654", {"start": v(13.92, 99.26) * mm, "end": v(13.9, 99.2) * mm});
            skLineSegment(sketch, "E1655", {"start": v(13.9, 99.2) * mm, "end": v(13.89, 99.19) * mm});
            skLineSegment(sketch, "E1656", {"start": v(18, 99.3) * mm, "end": v(17.92, 99.28) * mm});
            skLineSegment(sketch, "E1657", {"start": v(17.92, 99.28) * mm, "end": v(17.41, 99.12) * mm});
            skLineSegment(sketch, "E1658", {"start": v(17.41, 99.12) * mm, "end": v(16.88, 98.98) * mm});
            skLineSegment(sketch, "E1659", {"start": v(16.88, 98.98) * mm, "end": v(16.8, 98.96) * mm});
            skLineSegment(sketch, "E1660", {"start": v(16.8, 98.96) * mm, "end": v(16.7, 98.94) * mm});
            skLineSegment(sketch, "E1661", {"start": v(16.7, 98.94) * mm, "end": v(16.4, 98.86) * mm});
            skLineSegment(sketch, "E1662", {"start": v(16.4, 98.86) * mm, "end": v(16.16, 98.76) * mm});
            skLineSegment(sketch, "E1663", {"start": v(16.16, 98.76) * mm, "end": v(15.92, 98.6) * mm});
            skLineSegment(sketch, "E1664", {"start": v(15.92, 98.6) * mm, "end": v(15.66, 98.43) * mm});
            skLineSegment(sketch, "E1665", {"start": v(15.66, 98.43) * mm, "end": v(15.57, 98.37) * mm});
            skLineSegment(sketch, "E1666", {"start": v(15.57, 98.37) * mm, "end": v(15.5, 98.33) * mm});
            skLineSegment(sketch, "E1667", {"start": v(15.5, 98.33) * mm, "end": v(15.26, 98.3) * mm});
            skLineSegment(sketch, "E1668", {"start": v(15.26, 98.3) * mm, "end": v(15.2, 98.48) * mm});
            skLineSegment(sketch, "E1669", {"start": v(15.2, 98.48) * mm, "end": v(15.29, 98.78) * mm});
            skLineSegment(sketch, "E1670", {"start": v(15.29, 98.78) * mm, "end": v(15.42, 98.98) * mm});
            skLineSegment(sketch, "E1671", {"start": v(15.42, 98.98) * mm, "end": v(15.47, 99.03) * mm});
            skLineSegment(sketch, "E1672", {"start": v(15.47, 99.03) * mm, "end": v(15.54, 99.1) * mm});
            skLineSegment(sketch, "E1673", {"start": v(15.54, 99.1) * mm, "end": v(16.2, 99.28) * mm});
            skLineSegment(sketch, "E1674", {"start": v(16.2, 99.28) * mm, "end": v(16.91, 99.33) * mm});
            skLineSegment(sketch, "E1675", {"start": v(16.91, 99.33) * mm, "end": v(17.15, 99.33) * mm});
            skLineSegment(sketch, "E1676", {"start": v(17.15, 99.33) * mm, "end": v(17.32, 99.33) * mm});
            skLineSegment(sketch, "E1677", {"start": v(17.32, 99.33) * mm, "end": v(17.82, 99.46) * mm});
            skLineSegment(sketch, "E1678", {"start": v(17.82, 99.46) * mm, "end": v(18.18, 99.6) * mm});
            skLineSegment(sketch, "E1679", {"start": v(18.18, 99.6) * mm, "end": v(18.22, 99.6) * mm});
            skLineSegment(sketch, "E1680", {"start": v(18.22, 99.6) * mm, "end": v(18.22, 99.6) * mm});
            skLineSegment(sketch, "E1681", {"start": v(18.22, 99.6) * mm, "end": v(18.24, 99.51) * mm});
            skLineSegment(sketch, "E1682", {"start": v(18.24, 99.51) * mm, "end": v(18.07, 99.34) * mm});
            skLineSegment(sketch, "E1683", {"start": v(18.07, 99.34) * mm, "end": v(18, 99.3) * mm});
            skLineSegment(sketch, "E1684", {"start": v(14.18, 150.58) * mm, "end": v(14.2, 150.56) * mm});
            skLineSegment(sketch, "E1685", {"start": v(14.2, 150.56) * mm, "end": v(14.38, 150.38) * mm});
            skLineSegment(sketch, "E1686", {"start": v(14.38, 150.38) * mm, "end": v(14.39, 150.36) * mm});
            skLineSegment(sketch, "E1687", {"start": v(14.39, 150.36) * mm, "end": v(14.44, 150.38) * mm});
            skLineSegment(sketch, "E1688", {"start": v(14.44, 150.38) * mm, "end": v(14.77, 150.7) * mm});
            skLineSegment(sketch, "E1689", {"start": v(14.77, 150.7) * mm, "end": v(14.78, 150.76) * mm});
            skLineSegment(sketch, "E1690", {"start": v(14.78, 150.76) * mm, "end": v(14.8, 150.81) * mm});
            skLineSegment(sketch, "E1691", {"start": v(14.8, 150.81) * mm, "end": v(14.67, 151.02) * mm});
            skLineSegment(sketch, "E1692", {"start": v(14.67, 151.02) * mm, "end": v(14.33, 151.15) * mm});
            skLineSegment(sketch, "E1693", {"start": v(14.33, 151.15) * mm, "end": v(14.24, 151.16) * mm});
            skLineSegment(sketch, "E1694", {"start": v(14.24, 151.16) * mm, "end": v(14.13, 151.17) * mm});
            skLineSegment(sketch, "E1695", {"start": v(14.13, 151.17) * mm, "end": v(13.68, 151.26) * mm});
            skLineSegment(sketch, "E1696", {"start": v(13.68, 151.26) * mm, "end": v(13.43, 151.32) * mm});
            skLineSegment(sketch, "E1697", {"start": v(13.43, 151.32) * mm, "end": v(13.33, 151.32) * mm});
            skLineSegment(sketch, "E1698", {"start": v(13.33, 151.32) * mm, "end": v(13.06, 151.24) * mm});
            skLineSegment(sketch, "E1699", {"start": v(13.06, 151.24) * mm, "end": v(13.04, 151.22) * mm});
            skLineSegment(sketch, "E1700", {"start": v(13.04, 151.22) * mm, "end": v(13.11, 151.18) * mm});
            skLineSegment(sketch, "E1701", {"start": v(13.11, 151.18) * mm, "end": v(13.14, 151.18) * mm});
            skLineSegment(sketch, "E1702", {"start": v(13.14, 151.18) * mm, "end": v(13.17, 151.17) * mm});
            skLineSegment(sketch, "E1703", {"start": v(13.17, 151.17) * mm, "end": v(13.64, 150.92) * mm});
            skLineSegment(sketch, "E1704", {"start": v(13.64, 150.92) * mm, "end": v(14.14, 150.62) * mm});
            skLineSegment(sketch, "E1705", {"start": v(14.14, 150.62) * mm, "end": v(14.18, 150.58) * mm});
            skLineSegment(sketch, "E1706", {"start": v(3.02, 167.78) * mm, "end": v(3, 167.8) * mm});
            skLineSegment(sketch, "E1707", {"start": v(3, 167.8) * mm, "end": v(2.8, 167.91) * mm});
            skLineSegment(sketch, "E1708", {"start": v(2.8, 167.91) * mm, "end": v(2.78, 167.92) * mm});
            skLineSegment(sketch, "E1709", {"start": v(2.78, 167.92) * mm, "end": v(2.77, 167.93) * mm});
            skLineSegment(sketch, "E1710", {"start": v(2.77, 167.93) * mm, "end": v(2.74, 167.94) * mm});
            skLineSegment(sketch, "E1711", {"start": v(2.74, 167.94) * mm, "end": v(2.68, 167.96) * mm});
            skLineSegment(sketch, "E1712", {"start": v(2.68, 167.96) * mm, "end": v(2.39, 167.9) * mm});
            skLineSegment(sketch, "E1713", {"start": v(2.39, 167.9) * mm, "end": v(2.06, 167.95) * mm});
            skLineSegment(sketch, "E1714", {"start": v(2.06, 167.95) * mm, "end": v(2, 168.02) * mm});
            skLineSegment(sketch, "E1715", {"start": v(2, 168.02) * mm, "end": v(1.89, 168.13) * mm});
            skLineSegment(sketch, "E1716", {"start": v(1.89, 168.13) * mm, "end": v(1.54, 168.45) * mm});
            skLineSegment(sketch, "E1717", {"start": v(1.54, 168.45) * mm, "end": v(1.1, 168.75) * mm});
            skLineSegment(sketch, "E1718", {"start": v(1.1, 168.75) * mm, "end": v(0.77, 168.86) * mm});
            skLineSegment(sketch, "E1719", {"start": v(0.77, 168.86) * mm, "end": v(0.62, 168.77) * mm});
            skLineSegment(sketch, "E1720", {"start": v(0.62, 168.77) * mm, "end": v(0.62, 168.73) * mm});
            skLineSegment(sketch, "E1721", {"start": v(0.62, 168.73) * mm, "end": v(0.6, 168.64) * mm});
            skLineSegment(sketch, "E1722", {"start": v(0.6, 168.64) * mm, "end": v(0.57, 167.67) * mm});
            skLineSegment(sketch, "E1723", {"start": v(0.57, 167.67) * mm, "end": v(0.6, 167.57) * mm});
            skLineSegment(sketch, "E1724", {"start": v(0.6, 167.57) * mm, "end": v(0.63, 167.4) * mm});
            skLineSegment(sketch, "E1725", {"start": v(0.63, 167.4) * mm, "end": v(0.8, 166.8) * mm});
            skLineSegment(sketch, "E1726", {"start": v(0.8, 166.8) * mm, "end": v(0.9, 166.55) * mm});
            skLineSegment(sketch, "E1727", {"start": v(0.9, 166.55) * mm, "end": v(0.98, 166.43) * mm});
            skLineSegment(sketch, "E1728", {"start": v(0.98, 166.43) * mm, "end": v(1.25, 166.4) * mm});
            skLineSegment(sketch, "E1729", {"start": v(1.25, 166.4) * mm, "end": v(1.32, 166.44) * mm});
            skLineSegment(sketch, "E1730", {"start": v(1.32, 166.44) * mm, "end": v(1.4, 166.47) * mm});
            skLineSegment(sketch, "E1731", {"start": v(1.4, 166.47) * mm, "end": v(1.76, 166.6) * mm});
            skLineSegment(sketch, "E1732", {"start": v(1.76, 166.6) * mm, "end": v(2.01, 166.64) * mm});
            skLineSegment(sketch, "E1733", {"start": v(2.01, 166.64) * mm, "end": v(2.03, 166.65) * mm});
            skLineSegment(sketch, "E1734", {"start": v(2.03, 166.65) * mm, "end": v(2.05, 166.65) * mm});
            skLineSegment(sketch, "E1735", {"start": v(2.05, 166.65) * mm, "end": v(2.28, 166.44) * mm});
            skLineSegment(sketch, "E1736", {"start": v(2.28, 166.44) * mm, "end": v(2.32, 166.41) * mm});
            skLineSegment(sketch, "E1737", {"start": v(2.32, 166.41) * mm, "end": v(2.37, 166.37) * mm});
            skLineSegment(sketch, "E1738", {"start": v(2.37, 166.37) * mm, "end": v(2.65, 166.27) * mm});
            skLineSegment(sketch, "E1739", {"start": v(2.65, 166.27) * mm, "end": v(2.88, 166.28) * mm});
            skLineSegment(sketch, "E1740", {"start": v(2.88, 166.28) * mm, "end": v(2.92, 166.3) * mm});
            skLineSegment(sketch, "E1741", {"start": v(2.92, 166.3) * mm, "end": v(2.95, 166.3) * mm});
            skLineSegment(sketch, "E1742", {"start": v(2.95, 166.3) * mm, "end": v(3.1, 166.43) * mm});
            skLineSegment(sketch, "E1743", {"start": v(3.1, 166.43) * mm, "end": v(3.21, 166.5) * mm});
            skLineSegment(sketch, "E1744", {"start": v(3.21, 166.5) * mm, "end": v(3.22, 166.5) * mm});
            skLineSegment(sketch, "E1745", {"start": v(3.22, 166.5) * mm, "end": v(3.3, 166.46) * mm});
            skLineSegment(sketch, "E1746", {"start": v(3.3, 166.46) * mm, "end": v(3.53, 166.32) * mm});
            skLineSegment(sketch, "E1747", {"start": v(3.53, 166.32) * mm, "end": v(3.87, 166.13) * mm});
            skLineSegment(sketch, "E1748", {"start": v(3.87, 166.13) * mm, "end": v(4.1, 166.1) * mm});
            skLineSegment(sketch, "E1749", {"start": v(4.1, 166.1) * mm, "end": v(4.12, 166.3) * mm});
            skLineSegment(sketch, "E1750", {"start": v(4.12, 166.3) * mm, "end": v(4.1, 166.36) * mm});
            skLineSegment(sketch, "E1751", {"start": v(4.1, 166.36) * mm, "end": v(4.09, 166.39) * mm});
            skLineSegment(sketch, "E1752", {"start": v(4.09, 166.39) * mm, "end": v(4.02, 166.57) * mm});
            skLineSegment(sketch, "E1753", {"start": v(4.02, 166.57) * mm, "end": v(3.94, 166.96) * mm});
            skLineSegment(sketch, "E1754", {"start": v(3.94, 166.96) * mm, "end": v(3.95, 167.46) * mm});
            skLineSegment(sketch, "E1755", {"start": v(3.95, 167.46) * mm, "end": v(4.07, 167.87) * mm});
            skLineSegment(sketch, "E1756", {"start": v(4.07, 167.87) * mm, "end": v(4.15, 167.98) * mm});
            skLineSegment(sketch, "E1757", {"start": v(4.15, 167.98) * mm, "end": v(4.18, 168.03) * mm});
            skLineSegment(sketch, "E1758", {"start": v(4.18, 168.03) * mm, "end": v(4.28, 168.25) * mm});
            skLineSegment(sketch, "E1759", {"start": v(4.28, 168.25) * mm, "end": v(4.25, 168.4) * mm});
            skLineSegment(sketch, "E1760", {"start": v(4.25, 168.4) * mm, "end": v(4.23, 168.4) * mm});
            skLineSegment(sketch, "E1761", {"start": v(4.23, 168.4) * mm, "end": v(4.21, 168.41) * mm});
            skLineSegment(sketch, "E1762", {"start": v(4.21, 168.41) * mm, "end": v(3.98, 168.37) * mm});
            skLineSegment(sketch, "E1763", {"start": v(3.98, 168.37) * mm, "end": v(3.67, 168.27) * mm});
            skLineSegment(sketch, "E1764", {"start": v(3.67, 168.27) * mm, "end": v(3.62, 168.25) * mm});
            skLineSegment(sketch, "E1765", {"start": v(3.62, 168.25) * mm, "end": v(3.57, 168.24) * mm});
            skLineSegment(sketch, "E1766", {"start": v(3.57, 168.24) * mm, "end": v(3.35, 168.1) * mm});
            skLineSegment(sketch, "E1767", {"start": v(3.35, 168.1) * mm, "end": v(3.18, 167.98) * mm});
            skLineSegment(sketch, "E1768", {"start": v(3.18, 167.98) * mm, "end": v(3.17, 167.96) * mm});
            skLineSegment(sketch, "E1769", {"start": v(3.17, 167.96) * mm, "end": v(3.17, 167.94) * mm});
            skLineSegment(sketch, "E1770", {"start": v(3.17, 167.94) * mm, "end": v(3.15, 167.94) * mm});
            skLineSegment(sketch, "E1771", {"start": v(3.15, 167.94) * mm, "end": v(3.14, 167.93) * mm});
            skLineSegment(sketch, "E1772", {"start": v(3.14, 167.93) * mm, "end": v(3.15, 167.77) * mm});
            skLineSegment(sketch, "E1773", {"start": v(3.15, 167.77) * mm, "end": v(3.17, 167.75) * mm});
            skLineSegment(sketch, "E1774", {"start": v(3.17, 167.75) * mm, "end": v(3.17, 167.74) * mm});
            skLineSegment(sketch, "E1775", {"start": v(3.17, 167.74) * mm, "end": v(3.12, 167.7) * mm});
            skLineSegment(sketch, "E1776", {"start": v(3.12, 167.7) * mm, "end": v(3.03, 167.76) * mm});
            skLineSegment(sketch, "E1777", {"start": v(3.03, 167.76) * mm, "end": v(3.02, 167.78) * mm});
            skLineSegment(sketch, "E1778", {"start": v(1.73, 171.75) * mm, "end": v(1.78, 171.78) * mm});
            skLineSegment(sketch, "E1779", {"start": v(1.78, 171.78) * mm, "end": v(2, 171.87) * mm});
            skLineSegment(sketch, "E1780", {"start": v(2, 171.87) * mm, "end": v(2.05, 171.94) * mm});
            skLineSegment(sketch, "E1781", {"start": v(2.05, 171.94) * mm, "end": v(1.87, 171.97) * mm});
            skLineSegment(sketch, "E1782", {"start": v(1.87, 171.97) * mm, "end": v(1.6, 171.93) * mm});
            skLineSegment(sketch, "E1783", {"start": v(1.6, 171.93) * mm, "end": v(1.57, 171.9) * mm});
            skLineSegment(sketch, "E1784", {"start": v(1.57, 171.9) * mm, "end": v(1.52, 171.88) * mm});
            skLineSegment(sketch, "E1785", {"start": v(1.52, 171.88) * mm, "end": v(1.43, 171.67) * mm});
            skLineSegment(sketch, "E1786", {"start": v(1.43, 171.67) * mm, "end": v(1.47, 171.51) * mm});
            skLineSegment(sketch, "E1787", {"start": v(1.47, 171.51) * mm, "end": v(1.48, 171.51) * mm});
            skLineSegment(sketch, "E1788", {"start": v(1.48, 171.51) * mm, "end": v(1.5, 171.5) * mm});
            skLineSegment(sketch, "E1789", {"start": v(1.5, 171.5) * mm, "end": v(1.56, 171.57) * mm});
            skLineSegment(sketch, "E1790", {"start": v(1.56, 171.57) * mm, "end": v(1.69, 171.72) * mm});
            skLineSegment(sketch, "E1791", {"start": v(1.69, 171.72) * mm, "end": v(1.73, 171.75) * mm});
            skLineSegment(sketch, "E1792", {"start": v(-0.06, 170.37) * mm, "end": v(-0.08, 170.38) * mm});
            skLineSegment(sketch, "E1793", {"start": v(-0.08, 170.38) * mm, "end": v(-0.26, 170.3) * mm});
            skLineSegment(sketch, "E1794", {"start": v(-0.26, 170.3) * mm, "end": v(-0.56, 170.1) * mm});
            skLineSegment(sketch, "E1795", {"start": v(-0.56, 170.1) * mm, "end": v(-0.75, 169.92) * mm});
            skLineSegment(sketch, "E1796", {"start": v(-0.75, 169.92) * mm, "end": v(-0.62, 169.84) * mm});
            skLineSegment(sketch, "E1797", {"start": v(-0.62, 169.84) * mm, "end": v(-0.58, 169.84) * mm});
            skLineSegment(sketch, "E1798", {"start": v(-0.58, 169.84) * mm, "end": v(-0.55, 169.84) * mm});
            skLineSegment(sketch, "E1799", {"start": v(-0.55, 169.84) * mm, "end": v(-0.5, 169.84) * mm});
            skLineSegment(sketch, "E1800", {"start": v(-0.5, 169.84) * mm, "end": v(0.11, 169.94) * mm});
            skLineSegment(sketch, "E1801", {"start": v(0.11, 169.94) * mm, "end": v(0.17, 169.95) * mm});
            skLineSegment(sketch, "E1802", {"start": v(0.17, 169.95) * mm, "end": v(0.18, 169.95) * mm});
            skLineSegment(sketch, "E1803", {"start": v(0.18, 169.95) * mm, "end": v(0.28, 170.07) * mm});
            skLineSegment(sketch, "E1804", {"start": v(0.28, 170.07) * mm, "end": v(0.28, 170.07) * mm});
            skLineSegment(sketch, "E1805", {"start": v(0.28, 170.07) * mm, "end": v(0.13, 170.22) * mm});
            skLineSegment(sketch, "E1806", {"start": v(0.13, 170.22) * mm, "end": v(-0.01, 170.37) * mm});
            skLineSegment(sketch, "E1807", {"start": v(-0.01, 170.37) * mm, "end": v(-0.06, 170.37) * mm});
            skLineSegment(sketch, "E1808", {"start": v(8.76, 116.52) * mm, "end": v(8.84, 116.73) * mm});
            skLineSegment(sketch, "E1809", {"start": v(8.84, 116.73) * mm, "end": v(9.1, 117.35) * mm});
            skLineSegment(sketch, "E1810", {"start": v(9.1, 117.35) * mm, "end": v(9.45, 117.97) * mm});
            skLineSegment(sketch, "E1811", {"start": v(9.45, 117.97) * mm, "end": v(9.73, 118.38) * mm});
            skLineSegment(sketch, "E1812", {"start": v(9.73, 118.38) * mm, "end": v(9.87, 118.57) * mm});
            skLineSegment(sketch, "E1813", {"start": v(9.87, 118.57) * mm, "end": v(9.9, 118.61) * mm});
            skLineSegment(sketch, "E1814", {"start": v(9.9, 118.61) * mm, "end": v(9.93, 118.64) * mm});
            skLineSegment(sketch, "E1815", {"start": v(9.93, 118.64) * mm, "end": v(9.87, 119.04) * mm});
            skLineSegment(sketch, "E1816", {"start": v(9.87, 119.04) * mm, "end": v(9.7, 119.51) * mm});
            skLineSegment(sketch, "E1817", {"start": v(9.7, 119.51) * mm, "end": v(9.67, 119.58) * mm});
            skLineSegment(sketch, "E1818", {"start": v(9.67, 119.58) * mm, "end": v(9.66, 119.6) * mm});
            skLineSegment(sketch, "E1819", {"start": v(9.66, 119.6) * mm, "end": v(9.62, 119.68) * mm});
            skLineSegment(sketch, "E1820", {"start": v(9.62, 119.68) * mm, "end": v(9.61, 119.68) * mm});
            skLineSegment(sketch, "E1821", {"start": v(9.61, 119.68) * mm, "end": v(9.45, 119.7) * mm});
            skLineSegment(sketch, "E1822", {"start": v(9.45, 119.7) * mm, "end": v(9.43, 119.7) * mm});
            skLineSegment(sketch, "E1823", {"start": v(9.43, 119.7) * mm, "end": v(9.25, 119.75) * mm});
            skLineSegment(sketch, "E1824", {"start": v(9.25, 119.75) * mm, "end": v(9.24, 119.77) * mm});
            skLineSegment(sketch, "E1825", {"start": v(9.24, 119.77) * mm, "end": v(9.27, 119.86) * mm});
            skLineSegment(sketch, "E1826", {"start": v(9.27, 119.86) * mm, "end": v(9.42, 120.67) * mm});
            skLineSegment(sketch, "E1827", {"start": v(9.42, 120.67) * mm, "end": v(9.43, 120.74) * mm});
            skLineSegment(sketch, "E1828", {"start": v(9.43, 120.74) * mm, "end": v(9.44, 120.82) * mm});
            skLineSegment(sketch, "E1829", {"start": v(9.44, 120.82) * mm, "end": v(9.43, 121.44) * mm});
            skLineSegment(sketch, "E1830", {"start": v(9.43, 121.44) * mm, "end": v(9.3, 122.2) * mm});
            skLineSegment(sketch, "E1831", {"start": v(9.3, 122.2) * mm, "end": v(9.26, 122.36) * mm});
            skLineSegment(sketch, "E1832", {"start": v(9.26, 122.36) * mm, "end": v(9.23, 122.47) * mm});
            skLineSegment(sketch, "E1833", {"start": v(9.23, 122.47) * mm, "end": v(9.1, 122.81) * mm});
            skLineSegment(sketch, "E1834", {"start": v(9.1, 122.81) * mm, "end": v(8.97, 122.97) * mm});
            skLineSegment(sketch, "E1835", {"start": v(8.97, 122.97) * mm, "end": v(8.94, 122.99) * mm});
            skLineSegment(sketch, "E1836", {"start": v(8.94, 122.99) * mm, "end": v(8.91, 122.85) * mm});
            skLineSegment(sketch, "E1837", {"start": v(8.91, 122.85) * mm, "end": v(8.97, 122.46) * mm});
            skLineSegment(sketch, "E1838", {"start": v(8.97, 122.46) * mm, "end": v(8.97, 122.33) * mm});
            skLineSegment(sketch, "E1839", {"start": v(8.97, 122.33) * mm, "end": v(8.98, 122.22) * mm});
            skLineSegment(sketch, "E1840", {"start": v(8.98, 122.22) * mm, "end": v(8.94, 121.56) * mm});
            skLineSegment(sketch, "E1841", {"start": v(8.94, 121.56) * mm, "end": v(8.74, 120.85) * mm});
            skLineSegment(sketch, "E1842", {"start": v(8.74, 120.85) * mm, "end": v(8.68, 120.72) * mm});
            skLineSegment(sketch, "E1843", {"start": v(8.68, 120.72) * mm, "end": v(8.6, 120.58) * mm});
            skLineSegment(sketch, "E1844", {"start": v(8.6, 120.58) * mm, "end": v(8.24, 119.95) * mm});
            skLineSegment(sketch, "E1845", {"start": v(8.24, 119.95) * mm, "end": v(7.97, 119.44) * mm});
            skLineSegment(sketch, "E1846", {"start": v(7.97, 119.44) * mm, "end": v(7.94, 119.36) * mm});
            skLineSegment(sketch, "E1847", {"start": v(7.94, 119.36) * mm, "end": v(7.91, 119.28) * mm});
            skLineSegment(sketch, "E1848", {"start": v(7.91, 119.28) * mm, "end": v(7.9, 118.95) * mm});
            skLineSegment(sketch, "E1849", {"start": v(7.9, 118.95) * mm, "end": v(8.07, 118.74) * mm});
            skLineSegment(sketch, "E1850", {"start": v(8.07, 118.74) * mm, "end": v(8.13, 118.72) * mm});
            skLineSegment(sketch, "E1851", {"start": v(8.13, 118.72) * mm, "end": v(8.14, 118.72) * mm});
            skLineSegment(sketch, "E1852", {"start": v(8.14, 118.72) * mm, "end": v(8.2, 118.72) * mm});
            skLineSegment(sketch, "E1853", {"start": v(8.2, 118.72) * mm, "end": v(8.33, 118.58) * mm});
            skLineSegment(sketch, "E1854", {"start": v(8.33, 118.58) * mm, "end": v(8.34, 118.53) * mm});
            skLineSegment(sketch, "E1855", {"start": v(8.34, 118.53) * mm, "end": v(8.35, 118.47) * mm});
            skLineSegment(sketch, "E1856", {"start": v(8.35, 118.47) * mm, "end": v(8.34, 118.25) * mm});
            skLineSegment(sketch, "E1857", {"start": v(8.34, 118.25) * mm, "end": v(8.22, 117.84) * mm});
            skLineSegment(sketch, "E1858", {"start": v(8.22, 117.84) * mm, "end": v(7.9, 117.24) * mm});
            skLineSegment(sketch, "E1859", {"start": v(7.9, 117.24) * mm, "end": v(7.46, 116.63) * mm});
            skLineSegment(sketch, "E1860", {"start": v(7.46, 116.63) * mm, "end": v(7.3, 116.44) * mm});
            skLineSegment(sketch, "E1861", {"start": v(7.3, 116.44) * mm, "end": v(7.23, 116.36) * mm});
            skLineSegment(sketch, "E1862", {"start": v(7.23, 116.36) * mm, "end": v(6.71, 115.87) * mm});
            skLineSegment(sketch, "E1863", {"start": v(6.71, 115.87) * mm, "end": v(6.05, 115.34) * mm});
            skLineSegment(sketch, "E1864", {"start": v(6.05, 115.34) * mm, "end": v(5.91, 115.24) * mm});
            skLineSegment(sketch, "E1865", {"start": v(5.91, 115.24) * mm, "end": v(5.92, 115.2) * mm});
            skLineSegment(sketch, "E1866", {"start": v(5.92, 115.2) * mm, "end": v(5.94, 114.74) * mm});
            skLineSegment(sketch, "E1867", {"start": v(5.94, 114.74) * mm, "end": v(5.93, 114.68) * mm});
            skLineSegment(sketch, "E1868", {"start": v(5.93, 114.68) * mm, "end": v(5.93, 114.62) * mm});
            skLineSegment(sketch, "E1869", {"start": v(5.93, 114.62) * mm, "end": v(5.83, 114.25) * mm});
            skLineSegment(sketch, "E1870", {"start": v(5.83, 114.25) * mm, "end": v(5.7, 114) * mm});
            skLineSegment(sketch, "E1871", {"start": v(5.7, 114) * mm, "end": v(5.7, 113.98) * mm});
            skLineSegment(sketch, "E1872", {"start": v(5.7, 113.98) * mm, "end": v(5.68, 113.97) * mm});
            skLineSegment(sketch, "E1873", {"start": v(5.68, 113.97) * mm, "end": v(5.54, 113.88) * mm});
            skLineSegment(sketch, "E1874", {"start": v(5.54, 113.88) * mm, "end": v(5.52, 113.88) * mm});
            skLineSegment(sketch, "E1875", {"start": v(5.52, 113.88) * mm, "end": v(5.45, 113.83) * mm});
            skLineSegment(sketch, "E1876", {"start": v(5.45, 113.83) * mm, "end": v(5.31, 113.58) * mm});
            skLineSegment(sketch, "E1877", {"start": v(5.31, 113.58) * mm, "end": v(5.33, 113.24) * mm});
            skLineSegment(sketch, "E1878", {"start": v(5.33, 113.24) * mm, "end": v(5.45, 112.96) * mm});
            skLineSegment(sketch, "E1879", {"start": v(5.45, 112.96) * mm, "end": v(5.52, 112.84) * mm});
            skLineSegment(sketch, "E1880", {"start": v(5.52, 112.84) * mm, "end": v(5.6, 112.9) * mm});
            skLineSegment(sketch, "E1881", {"start": v(5.6, 112.9) * mm, "end": v(5.88, 113.06) * mm});
            skLineSegment(sketch, "E1882", {"start": v(5.88, 113.06) * mm, "end": v(6.41, 113.4) * mm});
            skLineSegment(sketch, "E1883", {"start": v(6.41, 113.4) * mm, "end": v(7.03, 113.79) * mm});
            skLineSegment(sketch, "E1884", {"start": v(7.03, 113.79) * mm, "end": v(7.24, 113.92) * mm});
            skLineSegment(sketch, "E1885", {"start": v(7.24, 113.92) * mm, "end": v(7.4, 114.03) * mm});
            skLineSegment(sketch, "E1886", {"start": v(7.4, 114.03) * mm, "end": v(7.84, 114.47) * mm});
            skLineSegment(sketch, "E1887", {"start": v(7.84, 114.47) * mm, "end": v(8.26, 115.14) * mm});
            skLineSegment(sketch, "E1888", {"start": v(8.26, 115.14) * mm, "end": v(8.54, 115.85) * mm});
            skLineSegment(sketch, "E1889", {"start": v(8.54, 115.85) * mm, "end": v(8.7, 116.35) * mm});
            skLineSegment(sketch, "E1890", {"start": v(8.7, 116.35) * mm, "end": v(8.76, 116.52) * mm});
            skLineSegment(sketch, "E1891", {"start": v(-2.16, 133.25) * mm, "end": v(-2.03, 133.4) * mm});
            skLineSegment(sketch, "E1892", {"start": v(-2.03, 133.4) * mm, "end": v(-1.33, 134.07) * mm});
            skLineSegment(sketch, "E1893", {"start": v(-1.33, 134.07) * mm, "end": v(-0.73, 134.58) * mm});
            skLineSegment(sketch, "E1894", {"start": v(-0.73, 134.58) * mm, "end": v(-0.65, 134.63) * mm});
            skLineSegment(sketch, "E1895", {"start": v(-0.65, 134.63) * mm, "end": v(-0.6, 134.66) * mm});
            skLineSegment(sketch, "E1896", {"start": v(-0.6, 134.66) * mm, "end": v(-0.5, 134.8) * mm});
            skLineSegment(sketch, "E1897", {"start": v(-0.5, 134.8) * mm, "end": v(-0.75, 134.78) * mm});
            skLineSegment(sketch, "E1898", {"start": v(-0.75, 134.78) * mm, "end": v(-1.34, 134.5) * mm});
            skLineSegment(sketch, "E1899", {"start": v(-1.34, 134.5) * mm, "end": v(-2.06, 134.07) * mm});
            skLineSegment(sketch, "E1900", {"start": v(-2.06, 134.07) * mm, "end": v(-2.3, 133.91) * mm});
            skLineSegment(sketch, "E1901", {"start": v(-2.3, 133.91) * mm, "end": v(-2.41, 133.83) * mm});
            skLineSegment(sketch, "E1902", {"start": v(-2.41, 133.83) * mm, "end": v(-3.1, 133.26) * mm});
            skLineSegment(sketch, "E1903", {"start": v(-3.1, 133.26) * mm, "end": v(-3.9, 132.38) * mm});
            skLineSegment(sketch, "E1904", {"start": v(-3.9, 132.38) * mm, "end": v(-4.06, 132.13) * mm});
            skLineSegment(sketch, "E1905", {"start": v(-4.06, 132.13) * mm, "end": v(-4.32, 131.77) * mm});
            skLineSegment(sketch, "E1906", {"start": v(-4.32, 131.77) * mm, "end": v(-5.04, 130.65) * mm});
            skLineSegment(sketch, "E1907", {"start": v(-5.04, 130.65) * mm, "end": v(-5.92, 129.09) * mm});
            skLineSegment(sketch, "E1908", {"start": v(-5.92, 129.09) * mm, "end": v(-6.65, 127.67) * mm});
            skLineSegment(sketch, "E1909", {"start": v(-6.65, 127.67) * mm, "end": v(-7.03, 126.89) * mm});
            skLineSegment(sketch, "E1910", {"start": v(-7.03, 126.89) * mm, "end": v(-7.16, 126.63) * mm});
            skLineSegment(sketch, "E1911", {"start": v(-7.16, 126.63) * mm, "end": v(-7.26, 126.42) * mm});
            skLineSegment(sketch, "E1912", {"start": v(-7.26, 126.42) * mm, "end": v(-7.96, 125.25) * mm});
            skLineSegment(sketch, "E1913", {"start": v(-7.96, 125.25) * mm, "end": v(-8.85, 124.14) * mm});
            skLineSegment(sketch, "E1914", {"start": v(-8.85, 124.14) * mm, "end": v(-9.05, 123.96) * mm});
            skLineSegment(sketch, "E1915", {"start": v(-9.05, 123.96) * mm, "end": v(-9.28, 123.76) * mm});
            skLineSegment(sketch, "E1916", {"start": v(-9.28, 123.76) * mm, "end": v(-10.38, 123.07) * mm});
            skLineSegment(sketch, "E1917", {"start": v(-10.38, 123.07) * mm, "end": v(-11.29, 122.54) * mm});
            skLineSegment(sketch, "E1918", {"start": v(-11.29, 122.54) * mm, "end": v(-11.42, 122.43) * mm});
            skLineSegment(sketch, "E1919", {"start": v(-11.42, 122.43) * mm, "end": v(-11.43, 122.41) * mm});
            skLineSegment(sketch, "E1920", {"start": v(-11.43, 122.41) * mm, "end": v(-11.58, 122.27) * mm});
            skLineSegment(sketch, "E1921", {"start": v(-11.58, 122.27) * mm, "end": v(-11.6, 122.26) * mm});
            skLineSegment(sketch, "E1922", {"start": v(-11.6, 122.26) * mm, "end": v(-11.6, 122.25) * mm});
            skLineSegment(sketch, "E1923", {"start": v(-11.6, 122.25) * mm, "end": v(-11.74, 122.08) * mm});
            skLineSegment(sketch, "E1924", {"start": v(-11.74, 122.08) * mm, "end": v(-11.76, 122.06) * mm});
            skLineSegment(sketch, "E1925", {"start": v(-11.76, 122.06) * mm, "end": v(-11.77, 122.04) * mm});
            skLineSegment(sketch, "E1926", {"start": v(-11.77, 122.04) * mm, "end": v(-11.83, 121.86) * mm});
            skLineSegment(sketch, "E1927", {"start": v(-11.83, 121.86) * mm, "end": v(-11.85, 121.66) * mm});
            skLineSegment(sketch, "E1928", {"start": v(-11.85, 121.66) * mm, "end": v(-11.84, 121.62) * mm});
            skLineSegment(sketch, "E1929", {"start": v(-11.84, 121.62) * mm, "end": v(-11.84, 121.56) * mm});
            skLineSegment(sketch, "E1930", {"start": v(-11.84, 121.56) * mm, "end": v(-11.85, 121.23) * mm});
            skLineSegment(sketch, "E1931", {"start": v(-11.85, 121.23) * mm, "end": v(-11.98, 120.9) * mm});
            skLineSegment(sketch, "E1932", {"start": v(-11.98, 120.9) * mm, "end": v(-12.03, 120.84) * mm});
            skLineSegment(sketch, "E1933", {"start": v(-12.03, 120.84) * mm, "end": v(-12.05, 120.8) * mm});
            skLineSegment(sketch, "E1934", {"start": v(-12.05, 120.8) * mm, "end": v(-12.34, 120.6) * mm});
            skLineSegment(sketch, "E1935", {"start": v(-12.34, 120.6) * mm, "end": v(-12.9, 120.33) * mm});
            skLineSegment(sketch, "E1936", {"start": v(-12.9, 120.33) * mm, "end": v(-13.05, 120.27) * mm});
            skLineSegment(sketch, "E1937", {"start": v(-13.05, 120.27) * mm, "end": v(-13.09, 120.27) * mm});
            skLineSegment(sketch, "E1938", {"start": v(-13.09, 120.27) * mm, "end": v(-13.18, 120.25) * mm});
            skLineSegment(sketch, "E1939", {"start": v(-13.18, 120.25) * mm, "end": v(-13.2, 120.24) * mm});
            skLineSegment(sketch, "E1940", {"start": v(-13.2, 120.24) * mm, "end": v(-13.22, 120.23) * mm});
            skLineSegment(sketch, "E1941", {"start": v(-13.22, 120.23) * mm, "end": v(-13.46, 120.17) * mm});
            skLineSegment(sketch, "E1942", {"start": v(-13.46, 120.17) * mm, "end": v(-13.67, 120.1) * mm});
            skLineSegment(sketch, "E1943", {"start": v(-13.67, 120.1) * mm, "end": v(-13.68, 120.1) * mm});
            skLineSegment(sketch, "E1944", {"start": v(-13.68, 120.1) * mm, "end": v(-13.78, 120.09) * mm});
            skLineSegment(sketch, "E1945", {"start": v(-13.78, 120.09) * mm, "end": v(-14.12, 119.94) * mm});
            skLineSegment(sketch, "E1946", {"start": v(-14.12, 119.94) * mm, "end": v(-14.04, 119.7) * mm});
            skLineSegment(sketch, "E1947", {"start": v(-14.04, 119.7) * mm, "end": v(-14, 119.68) * mm});
            skLineSegment(sketch, "E1948", {"start": v(-14, 119.68) * mm, "end": v(-13.96, 119.66) * mm});
            skLineSegment(sketch, "E1949", {"start": v(-13.96, 119.66) * mm, "end": v(-13.64, 119.53) * mm});
            skLineSegment(sketch, "E1950", {"start": v(-13.64, 119.53) * mm, "end": v(-13.59, 119.52) * mm});
            skLineSegment(sketch, "E1951", {"start": v(-13.59, 119.52) * mm, "end": v(-13.5, 119.5) * mm});
            skLineSegment(sketch, "E1952", {"start": v(-13.5, 119.5) * mm, "end": v(-13.26, 119.39) * mm});
            skLineSegment(sketch, "E1953", {"start": v(-13.26, 119.39) * mm, "end": v(-13.18, 119.27) * mm});
            skLineSegment(sketch, "E1954", {"start": v(-13.18, 119.27) * mm, "end": v(-13.18, 119.23) * mm});
            skLineSegment(sketch, "E1955", {"start": v(-13.18, 119.23) * mm, "end": v(-13.18, 119.14) * mm});
            skLineSegment(sketch, "E1956", {"start": v(-13.18, 119.14) * mm, "end": v(-13.4, 118.88) * mm});
            skLineSegment(sketch, "E1957", {"start": v(-13.4, 118.88) * mm, "end": v(-14, 118.53) * mm});
            skLineSegment(sketch, "E1958", {"start": v(-14, 118.53) * mm, "end": v(-14.2, 118.46) * mm});
            skLineSegment(sketch, "E1959", {"start": v(-14.2, 118.46) * mm, "end": v(-14.46, 118.38) * mm});
            skLineSegment(sketch, "E1960", {"start": v(-14.46, 118.38) * mm, "end": v(-15.25, 118.24) * mm});
            skLineSegment(sketch, "E1961", {"start": v(-15.25, 118.24) * mm, "end": v(-16.27, 118.14) * mm});
            skLineSegment(sketch, "E1962", {"start": v(-16.27, 118.14) * mm, "end": v(-17.05, 118.12) * mm});
            skLineSegment(sketch, "E1963", {"start": v(-17.05, 118.12) * mm, "end": v(-17.36, 118.12) * mm});
            skLineSegment(sketch, "E1964", {"start": v(-17.36, 118.12) * mm, "end": v(-17.59, 118.13) * mm});
            skLineSegment(sketch, "E1965", {"start": v(-17.59, 118.13) * mm, "end": v(-18.4, 118.17) * mm});
            skLineSegment(sketch, "E1966", {"start": v(-18.4, 118.17) * mm, "end": v(-18.83, 118.15) * mm});
            skLineSegment(sketch, "E1967", {"start": v(-18.83, 118.15) * mm, "end": v(-18.87, 118.13) * mm});
            skLineSegment(sketch, "E1968", {"start": v(-18.87, 118.13) * mm, "end": v(-18.89, 118.12) * mm});
            skLineSegment(sketch, "E1969", {"start": v(-18.89, 118.12) * mm, "end": v(-18.88, 117.97) * mm});
            skLineSegment(sketch, "E1970", {"start": v(-18.88, 117.97) * mm, "end": v(-18.52, 117.77) * mm});
            skLineSegment(sketch, "E1971", {"start": v(-18.52, 117.77) * mm, "end": v(-18.39, 117.73) * mm});
            skLineSegment(sketch, "E1972", {"start": v(-18.39, 117.73) * mm, "end": v(-18.3, 117.7) * mm});
            skLineSegment(sketch, "E1973", {"start": v(-18.3, 117.7) * mm, "end": v(-17.68, 117.56) * mm});
            skLineSegment(sketch, "E1974", {"start": v(-17.68, 117.56) * mm, "end": v(-17.03, 117.4) * mm});
            skLineSegment(sketch, "E1975", {"start": v(-17.03, 117.4) * mm, "end": v(-16.93, 117.37) * mm});
            skLineSegment(sketch, "E1976", {"start": v(-16.93, 117.37) * mm, "end": v(-16.9, 117.35) * mm});
            skLineSegment(sketch, "E1977", {"start": v(-16.9, 117.35) * mm, "end": v(-16.82, 117.2) * mm});
            skLineSegment(sketch, "E1978", {"start": v(-16.82, 117.2) * mm, "end": v(-17, 117.09) * mm});
            skLineSegment(sketch, "E1979", {"start": v(-17, 117.09) * mm, "end": v(-17.06, 117.08) * mm});
            skLineSegment(sketch, "E1980", {"start": v(-17.06, 117.08) * mm, "end": v(-17.17, 117.06) * mm});
            skLineSegment(sketch, "E1981", {"start": v(-17.17, 117.06) * mm, "end": v(-17.52, 117.04) * mm});
            skLineSegment(sketch, "E1982", {"start": v(-17.52, 117.04) * mm, "end": v(-18.17, 117.05) * mm});
            skLineSegment(sketch, "E1983", {"start": v(-18.17, 117.05) * mm, "end": v(-18.87, 117.12) * mm});
            skLineSegment(sketch, "E1984", {"start": v(-18.87, 117.12) * mm, "end": v(-19.35, 117.21) * mm});
            skLineSegment(sketch, "E1985", {"start": v(-19.35, 117.21) * mm, "end": v(-19.5, 117.26) * mm});
            skLineSegment(sketch, "E1986", {"start": v(-19.5, 117.26) * mm, "end": v(-19.66, 117.31) * mm});
            skLineSegment(sketch, "E1987", {"start": v(-19.66, 117.31) * mm, "end": v(-19.88, 117.4) * mm});
            skLineSegment(sketch, "E1988", {"start": v(-19.88, 117.4) * mm, "end": v(-19.91, 117.41) * mm});
            skLineSegment(sketch, "E1989", {"start": v(-19.91, 117.41) * mm, "end": v(-20.01, 117.47) * mm});
            skLineSegment(sketch, "E1990", {"start": v(-20.01, 117.47) * mm, "end": v(-20.43, 117.78) * mm});
            skLineSegment(sketch, "E1991", {"start": v(-20.43, 117.78) * mm, "end": v(-20.71, 118.1) * mm});
            skLineSegment(sketch, "E1992", {"start": v(-20.71, 118.1) * mm, "end": v(-20.75, 118.15) * mm});
            skLineSegment(sketch, "E1993", {"start": v(-20.75, 118.15) * mm, "end": v(-20.77, 118.18) * mm});
            skLineSegment(sketch, "E1994", {"start": v(-20.77, 118.18) * mm, "end": v(-20.84, 118.41) * mm});
            skLineSegment(sketch, "E1995", {"start": v(-20.84, 118.41) * mm, "end": v(-20.93, 118.6) * mm});
            skLineSegment(sketch, "E1996", {"start": v(-20.93, 118.6) * mm, "end": v(-20.95, 118.61) * mm});
            skLineSegment(sketch, "E1997", {"start": v(-20.95, 118.61) * mm, "end": v(-21.56, 117.78) * mm});
            skLineSegment(sketch, "E1998", {"start": v(-21.56, 117.78) * mm, "end": v(-21.55, 117.59) * mm});
            skLineSegment(sketch, "E1999", {"start": v(-21.55, 117.59) * mm, "end": v(-21.32, 117.11) * mm});
            skLineSegment(sketch, "E2000", {"start": v(-21.32, 117.11) * mm, "end": v(-21.21, 116.97) * mm});
            skLineSegment(sketch, "E2001", {"start": v(-21.21, 116.97) * mm, "end": v(-21.2, 116.99) * mm});
            skLineSegment(sketch, "E2002", {"start": v(-21.2, 116.99) * mm, "end": v(-21.1, 117.25) * mm});
            skLineSegment(sketch, "E2003", {"start": v(-21.1, 117.25) * mm, "end": v(-21.07, 117.27) * mm});
            skLineSegment(sketch, "E2004", {"start": v(-21.07, 117.27) * mm, "end": v(-21.06, 117.31) * mm});
            skLineSegment(sketch, "E2005", {"start": v(-21.06, 117.31) * mm, "end": v(-20.91, 117.44) * mm});
            skLineSegment(sketch, "E2006", {"start": v(-20.91, 117.44) * mm, "end": v(-20.74, 117.39) * mm});
            skLineSegment(sketch, "E2007", {"start": v(-20.74, 117.39) * mm, "end": v(-20.71, 117.35) * mm});
            skLineSegment(sketch, "E2008", {"start": v(-20.71, 117.35) * mm, "end": v(-20.69, 117.31) * mm});
            skLineSegment(sketch, "E2009", {"start": v(-20.69, 117.31) * mm, "end": v(-20.66, 116.86) * mm});
            skLineSegment(sketch, "E2010", {"start": v(-20.66, 116.86) * mm, "end": v(-20.68, 116.82) * mm});
            skLineSegment(sketch, "E2011", {"start": v(-20.68, 116.82) * mm, "end": v(-20.7, 116.8) * mm});
            skLineSegment(sketch, "E2012", {"start": v(-20.7, 116.8) * mm, "end": v(-20.76, 116.62) * mm});
            skLineSegment(sketch, "E2013", {"start": v(-20.76, 116.62) * mm, "end": v(-20.76, 116.57) * mm});
            skLineSegment(sketch, "E2014", {"start": v(-20.76, 116.57) * mm, "end": v(-20.75, 116.52) * mm});
            skLineSegment(sketch, "E2015", {"start": v(-20.75, 116.52) * mm, "end": v(-20.67, 116.46) * mm});
            skLineSegment(sketch, "E2016", {"start": v(-20.67, 116.46) * mm, "end": v(-20.17, 116.17) * mm});
            skLineSegment(sketch, "E2017", {"start": v(-20.17, 116.17) * mm, "end": v(-19.48, 115.93) * mm});
            skLineSegment(sketch, "E2018", {"start": v(-19.48, 115.93) * mm, "end": v(-19.31, 115.9) * mm});
            skLineSegment(sketch, "E2019", {"start": v(-19.31, 115.9) * mm, "end": v(-19.01, 115.84) * mm});
            skLineSegment(sketch, "E2020", {"start": v(-19.01, 115.84) * mm, "end": v(-18.1, 115.76) * mm});
            skLineSegment(sketch, "E2021", {"start": v(-18.1, 115.76) * mm, "end": v(-17.17, 115.78) * mm});
            skLineSegment(sketch, "E2022", {"start": v(-17.17, 115.78) * mm, "end": v(-16.5, 115.88) * mm});
            skLineSegment(sketch, "E2023", {"start": v(-16.5, 115.88) * mm, "end": v(-16.2, 115.94) * mm});
            skLineSegment(sketch, "E2024", {"start": v(-16.2, 115.94) * mm, "end": v(-16.12, 115.95) * mm});
            skLineSegment(sketch, "E2025", {"start": v(-16.12, 115.95) * mm, "end": v(-16.1, 115.97) * mm});
            skLineSegment(sketch, "E2026", {"start": v(-16.1, 115.97) * mm, "end": v(-15.82, 116.01) * mm});
            skLineSegment(sketch, "E2027", {"start": v(-15.82, 116.01) * mm, "end": v(-15.58, 116.01) * mm});
            skLineSegment(sketch, "E2028", {"start": v(-15.58, 116.01) * mm, "end": v(-15.57, 116) * mm});
            skLineSegment(sketch, "E2029", {"start": v(-15.57, 116) * mm, "end": v(-15.57, 115.97) * mm});
            skLineSegment(sketch, "E2030", {"start": v(-15.57, 115.97) * mm, "end": v(-15.68, 115.57) * mm});
            skLineSegment(sketch, "E2031", {"start": v(-15.68, 115.57) * mm, "end": v(-15.7, 115.53) * mm});
            skLineSegment(sketch, "E2032", {"start": v(-15.7, 115.53) * mm, "end": v(-15.71, 115.48) * mm});
            skLineSegment(sketch, "E2033", {"start": v(-15.71, 115.48) * mm, "end": v(-15.87, 115.15) * mm});
            skLineSegment(sketch, "E2034", {"start": v(-15.87, 115.15) * mm, "end": v(-15.88, 115.12) * mm});
            skLineSegment(sketch, "E2035", {"start": v(-15.88, 115.12) * mm, "end": v(-15.89, 115.09) * mm});
            skLineSegment(sketch, "E2036", {"start": v(-15.89, 115.09) * mm, "end": v(-15.88, 115) * mm});
            skLineSegment(sketch, "E2037", {"start": v(-15.88, 115) * mm, "end": v(-15.84, 114.98) * mm});
            skLineSegment(sketch, "E2038", {"start": v(-15.84, 114.98) * mm, "end": v(-15.8, 115) * mm});
            skLineSegment(sketch, "E2039", {"start": v(-15.8, 115) * mm, "end": v(-15.42, 115.31) * mm});
            skLineSegment(sketch, "E2040", {"start": v(-15.42, 115.31) * mm, "end": v(-15.38, 115.35) * mm});
            skLineSegment(sketch, "E2041", {"start": v(-15.38, 115.35) * mm, "end": v(-15.34, 115.4) * mm});
            skLineSegment(sketch, "E2042", {"start": v(-15.34, 115.4) * mm, "end": v(-14.98, 115.72) * mm});
            skLineSegment(sketch, "E2043", {"start": v(-14.98, 115.72) * mm, "end": v(-14.63, 116.04) * mm});
            skLineSegment(sketch, "E2044", {"start": v(-14.63, 116.04) * mm, "end": v(-14.6, 116.07) * mm});
            skLineSegment(sketch, "E2045", {"start": v(-14.6, 116.07) * mm, "end": v(-14.5, 116.17) * mm});
            skLineSegment(sketch, "E2046", {"start": v(-14.5, 116.17) * mm, "end": v(-14.12, 116.55) * mm});
            skLineSegment(sketch, "E2047", {"start": v(-14.12, 116.55) * mm, "end": v(-13.98, 116.82) * mm});
            skLineSegment(sketch, "E2048", {"start": v(-13.98, 116.82) * mm, "end": v(-14, 116.86) * mm});
            skLineSegment(sketch, "E2049", {"start": v(-14, 116.86) * mm, "end": v(-14, 116.87) * mm});
            skLineSegment(sketch, "E2050", {"start": v(-14, 116.87) * mm, "end": v(-14.05, 117.11) * mm});
            skLineSegment(sketch, "E2051", {"start": v(-14.05, 117.11) * mm, "end": v(-14.05, 117.2) * mm});
            skLineSegment(sketch, "E2052", {"start": v(-14.05, 117.2) * mm, "end": v(-14.06, 117.26) * mm});
            skLineSegment(sketch, "E2053", {"start": v(-14.06, 117.26) * mm, "end": v(-13.94, 117.61) * mm});
            skLineSegment(sketch, "E2054", {"start": v(-13.94, 117.61) * mm, "end": v(-13.59, 117.98) * mm});
            skLineSegment(sketch, "E2055", {"start": v(-13.59, 117.98) * mm, "end": v(-13.48, 118.07) * mm});
            skLineSegment(sketch, "E2056", {"start": v(-13.48, 118.07) * mm, "end": v(-13.37, 118.15) * mm});
            skLineSegment(sketch, "E2057", {"start": v(-13.37, 118.15) * mm, "end": v(-12.8, 118.46) * mm});
            skLineSegment(sketch, "E2058", {"start": v(-12.8, 118.46) * mm, "end": v(-12.25, 118.83) * mm});
            skLineSegment(sketch, "E2059", {"start": v(-12.25, 118.83) * mm, "end": v(-12.15, 118.94) * mm});
            skLineSegment(sketch, "E2060", {"start": v(-12.15, 118.94) * mm, "end": v(-12.04, 119.04) * mm});
            skLineSegment(sketch, "E2061", {"start": v(-12.04, 119.04) * mm, "end": v(-11.88, 119.61) * mm});
            skLineSegment(sketch, "E2062", {"start": v(-11.88, 119.61) * mm, "end": v(-11.75, 120.17) * mm});
            skLineSegment(sketch, "E2063", {"start": v(-11.75, 120.17) * mm, "end": v(-11.66, 120.27) * mm});
            skLineSegment(sketch, "E2064", {"start": v(-11.66, 120.27) * mm, "end": v(-11.56, 120.38) * mm});
            skLineSegment(sketch, "E2065", {"start": v(-11.56, 120.38) * mm, "end": v(-11, 120.78) * mm});
            skLineSegment(sketch, "E2066", {"start": v(-11, 120.78) * mm, "end": v(-10.5, 121.11) * mm});
            skLineSegment(sketch, "E2067", {"start": v(-10.5, 121.11) * mm, "end": v(-10.45, 121.19) * mm});
            skLineSegment(sketch, "E2068", {"start": v(-10.45, 121.19) * mm, "end": v(-10.37, 121.3) * mm});
            skLineSegment(sketch, "E2069", {"start": v(-10.37, 121.3) * mm, "end": v(-10.12, 121.72) * mm});
            skLineSegment(sketch, "E2070", {"start": v(-10.12, 121.72) * mm, "end": v(-9.87, 122.18) * mm});
            skLineSegment(sketch, "E2071", {"start": v(-9.87, 122.18) * mm, "end": v(-9.8, 122.3) * mm});
            skLineSegment(sketch, "E2072", {"start": v(-9.8, 122.3) * mm, "end": v(-9.73, 122.4) * mm});
            skLineSegment(sketch, "E2073", {"start": v(-9.73, 122.4) * mm, "end": v(-9.48, 122.72) * mm});
            skLineSegment(sketch, "E2074", {"start": v(-9.48, 122.72) * mm, "end": v(-8.96, 123.3) * mm});
            skLineSegment(sketch, "E2075", {"start": v(-8.96, 123.3) * mm, "end": v(-8.37, 123.92) * mm});
            skLineSegment(sketch, "E2076", {"start": v(-8.37, 123.92) * mm, "end": v(-7.96, 124.34) * mm});
            skLineSegment(sketch, "E2077", {"start": v(-7.96, 124.34) * mm, "end": v(-7.82, 124.48) * mm});
            skLineSegment(sketch, "E2078", {"start": v(-7.82, 124.48) * mm, "end": v(-7.62, 124.71) * mm});
            skLineSegment(sketch, "E2079", {"start": v(-7.62, 124.71) * mm, "end": v(-7.06, 125.46) * mm});
            skLineSegment(sketch, "E2080", {"start": v(-7.06, 125.46) * mm, "end": v(-6.46, 126.46) * mm});
            skLineSegment(sketch, "E2081", {"start": v(-6.46, 126.46) * mm, "end": v(-5.88, 127.55) * mm});
            skLineSegment(sketch, "E2082", {"start": v(-5.88, 127.55) * mm, "end": v(-5.37, 128.5) * mm});
            skLineSegment(sketch, "E2083", {"start": v(-5.37, 128.5) * mm, "end": v(-5.2, 128.8) * mm});
            skLineSegment(sketch, "E2084", {"start": v(-5.2, 128.8) * mm, "end": v(-4.9, 129.3) * mm});
            skLineSegment(sketch, "E2085", {"start": v(-4.9, 129.3) * mm, "end": v(-3.57, 131.42) * mm});
            skLineSegment(sketch, "E2086", {"start": v(-3.57, 131.42) * mm, "end": v(-2.38, 133.02) * mm});
            skLineSegment(sketch, "E2087", {"start": v(-2.38, 133.02) * mm, "end": v(-2.16, 133.25) * mm});
            skLineSegment(sketch, "E2088", {"start": v(-16.65, 114.53) * mm, "end": v(-16.96, 114.5) * mm});
            skLineSegment(sketch, "E2089", {"start": v(-16.96, 114.5) * mm, "end": v(-17.73, 114.46) * mm});
            skLineSegment(sketch, "E2090", {"start": v(-17.73, 114.46) * mm, "end": v(-18.69, 114.45) * mm});
            skLineSegment(sketch, "E2091", {"start": v(-18.69, 114.45) * mm, "end": v(-19.37, 114.48) * mm});
            skLineSegment(sketch, "E2092", {"start": v(-19.37, 114.48) * mm, "end": v(-19.59, 114.51) * mm});
            skLineSegment(sketch, "E2093", {"start": v(-19.59, 114.51) * mm, "end": v(-19.78, 114.55) * mm});
            skLineSegment(sketch, "E2094", {"start": v(-19.78, 114.55) * mm, "end": v(-20.63, 114.75) * mm});
            skLineSegment(sketch, "E2095", {"start": v(-20.63, 114.75) * mm, "end": v(-21.18, 114.94) * mm});
            skLineSegment(sketch, "E2096", {"start": v(-21.18, 114.94) * mm, "end": v(-21.22, 114.96) * mm});
            skLineSegment(sketch, "E2097", {"start": v(-21.22, 114.96) * mm, "end": v(-21.28, 114.98) * mm});
            skLineSegment(sketch, "E2098", {"start": v(-21.28, 114.98) * mm, "end": v(-21.48, 115.03) * mm});
            skLineSegment(sketch, "E2099", {"start": v(-21.48, 115.03) * mm, "end": v(-21.68, 114.86) * mm});
            skLineSegment(sketch, "E2100", {"start": v(-21.68, 114.86) * mm, "end": v(-21.7, 114.79) * mm});
            skLineSegment(sketch, "E2101", {"start": v(-21.7, 114.79) * mm, "end": v(-21.76, 114.7) * mm});
            skLineSegment(sketch, "E2102", {"start": v(-21.76, 114.7) * mm, "end": v(-22.03, 114.21) * mm});
            skLineSegment(sketch, "E2103", {"start": v(-22.03, 114.21) * mm, "end": v(-22.57, 113.24) * mm});
            skLineSegment(sketch, "E2104", {"start": v(-22.57, 113.24) * mm, "end": v(-23.15, 112.16) * mm});
            skLineSegment(sketch, "E2105", {"start": v(-23.15, 112.16) * mm, "end": v(-23.5, 111.48) * mm});
            skLineSegment(sketch, "E2106", {"start": v(-23.5, 111.48) * mm, "end": v(-23.6, 111.24) * mm});
            skLineSegment(sketch, "E2107", {"start": v(-23.6, 111.24) * mm, "end": v(-23.68, 111.02) * mm});
            skLineSegment(sketch, "E2108", {"start": v(-23.68, 111.02) * mm, "end": v(-23.95, 110.36) * mm});
            skLineSegment(sketch, "E2109", {"start": v(-23.95, 110.36) * mm, "end": v(-24.35, 109.34) * mm});
            skLineSegment(sketch, "E2110", {"start": v(-24.35, 109.34) * mm, "end": v(-24.7, 108.4) * mm});
            skLineSegment(sketch, "E2111", {"start": v(-24.7, 108.4) * mm, "end": v(-24.87, 107.88) * mm});
            skLineSegment(sketch, "E2112", {"start": v(-24.87, 107.88) * mm, "end": v(-24.91, 107.72) * mm});
            skLineSegment(sketch, "E2113", {"start": v(-24.91, 107.72) * mm, "end": v(-24.95, 107.6) * mm});
            skLineSegment(sketch, "E2114", {"start": v(-24.95, 107.6) * mm, "end": v(-25.06, 107.21) * mm});
            skLineSegment(sketch, "E2115", {"start": v(-25.06, 107.21) * mm, "end": v(-25.2, 106.87) * mm});
            skLineSegment(sketch, "E2116", {"start": v(-25.2, 106.87) * mm, "end": v(-25.29, 106.98) * mm});
            skLineSegment(sketch, "E2117", {"start": v(-25.29, 106.98) * mm, "end": v(-25.26, 107.63) * mm});
            skLineSegment(sketch, "E2118", {"start": v(-25.26, 107.63) * mm, "end": v(-25.23, 107.84) * mm});
            skLineSegment(sketch, "E2119", {"start": v(-25.23, 107.84) * mm, "end": v(-25.2, 108.22) * mm});
            skLineSegment(sketch, "E2120", {"start": v(-25.2, 108.22) * mm, "end": v(-24.92, 109.33) * mm});
            skLineSegment(sketch, "E2121", {"start": v(-24.92, 109.33) * mm, "end": v(-24.4, 110.94) * mm});
            skLineSegment(sketch, "E2122", {"start": v(-24.4, 110.94) * mm, "end": v(-23.85, 112.34) * mm});
            skLineSegment(sketch, "E2123", {"start": v(-23.85, 112.34) * mm, "end": v(-23.56, 113.05) * mm});
            skLineSegment(sketch, "E2124", {"start": v(-23.56, 113.05) * mm, "end": v(-23.48, 113.2) * mm});
            skLineSegment(sketch, "E2125", {"start": v(-23.48, 113.2) * mm, "end": v(-23.39, 113.41) * mm});
            skLineSegment(sketch, "E2126", {"start": v(-23.39, 113.41) * mm, "end": v(-23.07, 114.01) * mm});
            skLineSegment(sketch, "E2127", {"start": v(-23.07, 114.01) * mm, "end": v(-22.72, 114.57) * mm});
            skLineSegment(sketch, "E2128", {"start": v(-22.72, 114.57) * mm, "end": v(-22.43, 114.98) * mm});
            skLineSegment(sketch, "E2129", {"start": v(-22.43, 114.98) * mm, "end": v(-22.26, 115.24) * mm});
            skLineSegment(sketch, "E2130", {"start": v(-22.26, 115.24) * mm, "end": v(-22.21, 115.32) * mm});
            skLineSegment(sketch, "E2131", {"start": v(-22.21, 115.32) * mm, "end": v(-22.2, 115.35) * mm});
            skLineSegment(sketch, "E2132", {"start": v(-22.2, 115.35) * mm, "end": v(-22.34, 115.56) * mm});
            skLineSegment(sketch, "E2133", {"start": v(-22.34, 115.56) * mm, "end": v(-22.55, 115.72) * mm});
            skLineSegment(sketch, "E2134", {"start": v(-22.55, 115.72) * mm, "end": v(-22.57, 115.74) * mm});
            skLineSegment(sketch, "E2135", {"start": v(-22.57, 115.74) * mm, "end": v(-22.58, 115.75) * mm});
            skLineSegment(sketch, "E2136", {"start": v(-22.58, 115.75) * mm, "end": v(-22.79, 115.96) * mm});
            skLineSegment(sketch, "E2137", {"start": v(-22.79, 115.96) * mm, "end": v(-22.8, 116) * mm});
            skLineSegment(sketch, "E2138", {"start": v(-22.8, 116) * mm, "end": v(-22.83, 116.03) * mm});
            skLineSegment(sketch, "E2139", {"start": v(-22.83, 116.03) * mm, "end": v(-22.89, 116.23) * mm});
            skLineSegment(sketch, "E2140", {"start": v(-22.89, 116.23) * mm, "end": v(-22.99, 116.22) * mm});
            skLineSegment(sketch, "E2141", {"start": v(-22.99, 116.22) * mm, "end": v(-23, 116.2) * mm});
            skLineSegment(sketch, "E2142", {"start": v(-23, 116.2) * mm, "end": v(-23.1, 116.07) * mm});
            skLineSegment(sketch, "E2143", {"start": v(-23.1, 116.07) * mm, "end": v(-23.4, 115.63) * mm});
            skLineSegment(sketch, "E2144", {"start": v(-23.4, 115.63) * mm, "end": v(-23.86, 114.84) * mm});
            skLineSegment(sketch, "E2145", {"start": v(-23.86, 114.84) * mm, "end": v(-24.33, 113.92) * mm});
            skLineSegment(sketch, "E2146", {"start": v(-24.33, 113.92) * mm, "end": v(-24.65, 113.2) * mm});
            skLineSegment(sketch, "E2147", {"start": v(-24.65, 113.2) * mm, "end": v(-24.74, 112.95) * mm});
            skLineSegment(sketch, "E2148", {"start": v(-24.74, 112.95) * mm, "end": v(-24.82, 112.73) * mm});
            skLineSegment(sketch, "E2149", {"start": v(-24.82, 112.73) * mm, "end": v(-25.04, 112.03) * mm});
            skLineSegment(sketch, "E2150", {"start": v(-25.04, 112.03) * mm, "end": v(-25.4, 110.86) * mm});
            skLineSegment(sketch, "E2151", {"start": v(-25.4, 110.86) * mm, "end": v(-25.73, 109.64) * mm});
            skLineSegment(sketch, "E2152", {"start": v(-25.73, 109.64) * mm, "end": v(-25.93, 108.88) * mm});
            skLineSegment(sketch, "E2153", {"start": v(-25.93, 108.88) * mm, "end": v(-25.99, 108.63) * mm});
            skLineSegment(sketch, "E2154", {"start": v(-25.99, 108.63) * mm, "end": v(-26.03, 108.43) * mm});
            skLineSegment(sketch, "E2155", {"start": v(-26.03, 108.43) * mm, "end": v(-26.23, 107.62) * mm});
            skLineSegment(sketch, "E2156", {"start": v(-26.23, 107.62) * mm, "end": v(-26.42, 107.02) * mm});
            skLineSegment(sketch, "E2157", {"start": v(-26.42, 107.02) * mm, "end": v(-26.45, 106.92) * mm});
            skLineSegment(sketch, "E2158", {"start": v(-26.45, 106.92) * mm, "end": v(-26.48, 106.86) * mm});
            skLineSegment(sketch, "E2159", {"start": v(-26.48, 106.86) * mm, "end": v(-26.78, 106.29) * mm});
            skLineSegment(sketch, "E2160", {"start": v(-26.78, 106.29) * mm, "end": v(-26.8, 106.25) * mm});
            skLineSegment(sketch, "E2161", {"start": v(-26.8, 106.25) * mm, "end": v(-26.82, 106.24) * mm});
            skLineSegment(sketch, "E2162", {"start": v(-26.82, 106.24) * mm, "end": v(-27.1, 105.99) * mm});
            skLineSegment(sketch, "E2163", {"start": v(-27.1, 105.99) * mm, "end": v(-27.12, 105.96) * mm});
            skLineSegment(sketch, "E2164", {"start": v(-27.12, 105.96) * mm, "end": v(-27.13, 105.96) * mm});
            skLineSegment(sketch, "E2165", {"start": v(-27.13, 105.96) * mm, "end": v(-27.17, 105.94) * mm});
            skLineSegment(sketch, "E2166", {"start": v(-27.17, 105.94) * mm, "end": v(-27.09, 105.95) * mm});
            skLineSegment(sketch, "E2167", {"start": v(-27.09, 105.95) * mm, "end": v(-26.73, 105.94) * mm});
            skLineSegment(sketch, "E2168", {"start": v(-26.73, 105.94) * mm, "end": v(-26.5, 105.86) * mm});
            skLineSegment(sketch, "E2169", {"start": v(-26.5, 105.86) * mm, "end": v(-26.48, 105.84) * mm});
            skLineSegment(sketch, "E2170", {"start": v(-26.48, 105.84) * mm, "end": v(-26.45, 105.8) * mm});
            skLineSegment(sketch, "E2171", {"start": v(-26.45, 105.8) * mm, "end": v(-26.37, 105.63) * mm});
            skLineSegment(sketch, "E2172", {"start": v(-26.37, 105.63) * mm, "end": v(-26.57, 105.39) * mm});
            skLineSegment(sketch, "E2173", {"start": v(-26.57, 105.39) * mm, "end": v(-26.65, 105.34) * mm});
            skLineSegment(sketch, "E2174", {"start": v(-26.65, 105.34) * mm, "end": v(-26.7, 105.3) * mm});
            skLineSegment(sketch, "E2175", {"start": v(-26.7, 105.3) * mm, "end": v(-27.24, 104.73) * mm});
            skLineSegment(sketch, "E2176", {"start": v(-27.24, 104.73) * mm, "end": v(-27.3, 104.66) * mm});
            skLineSegment(sketch, "E2177", {"start": v(-27.3, 104.66) * mm, "end": v(-27.35, 104.6) * mm});
            skLineSegment(sketch, "E2178", {"start": v(-27.35, 104.6) * mm, "end": v(-27.66, 104.6) * mm});
            skLineSegment(sketch, "E2179", {"start": v(-27.66, 104.6) * mm, "end": v(-27.9, 104.85) * mm});
            skLineSegment(sketch, "E2180", {"start": v(-27.9, 104.85) * mm, "end": v(-27.92, 104.93) * mm});
            skLineSegment(sketch, "E2181", {"start": v(-27.92, 104.93) * mm, "end": v(-27.92, 104.94) * mm});
            skLineSegment(sketch, "E2182", {"start": v(-27.92, 104.94) * mm, "end": v(-27.95, 104.95) * mm});
            skLineSegment(sketch, "E2183", {"start": v(-27.95, 104.95) * mm, "end": v(-28, 104.82) * mm});
            skLineSegment(sketch, "E2184", {"start": v(-28, 104.82) * mm, "end": v(-28.13, 104.4) * mm});
            skLineSegment(sketch, "E2185", {"start": v(-28.13, 104.4) * mm, "end": v(-28.2, 103.98) * mm});
            skLineSegment(sketch, "E2186", {"start": v(-28.2, 103.98) * mm, "end": v(-28.2, 103.72) * mm});
            skLineSegment(sketch, "E2187", {"start": v(-28.2, 103.72) * mm, "end": v(-28.2, 103.63) * mm});
            skLineSegment(sketch, "E2188", {"start": v(-28.2, 103.63) * mm, "end": v(-28.25, 103.46) * mm});
            skLineSegment(sketch, "E2189", {"start": v(-28.25, 103.46) * mm, "end": v(-28.31, 103.32) * mm});
            skLineSegment(sketch, "E2190", {"start": v(-28.31, 103.32) * mm, "end": v(-28.41, 102.92) * mm});
            skLineSegment(sketch, "E2191", {"start": v(-28.41, 102.92) * mm, "end": v(-28.44, 102.35) * mm});
            skLineSegment(sketch, "E2192", {"start": v(-28.44, 102.35) * mm, "end": v(-28.35, 101.82) * mm});
            skLineSegment(sketch, "E2193", {"start": v(-28.35, 101.82) * mm, "end": v(-28.29, 101.66) * mm});
            skLineSegment(sketch, "E2194", {"start": v(-28.29, 101.66) * mm, "end": v(-28.23, 101.5) * mm});
            skLineSegment(sketch, "E2195", {"start": v(-28.23, 101.5) * mm, "end": v(-27.9, 100.83) * mm});
            skLineSegment(sketch, "E2196", {"start": v(-27.9, 100.83) * mm, "end": v(-27.7, 100.47) * mm});
            skLineSegment(sketch, "E2197", {"start": v(-27.7, 100.47) * mm, "end": v(-26.9, 100.48) * mm});
            skLineSegment(sketch, "E2198", {"start": v(-26.9, 100.48) * mm, "end": v(-26.82, 100.28) * mm});
            skLineSegment(sketch, "E2199", {"start": v(-26.82, 100.28) * mm, "end": v(-26.6, 99.73) * mm});
            skLineSegment(sketch, "E2200", {"start": v(-26.6, 99.73) * mm, "end": v(-26.3, 98.96) * mm});
            skLineSegment(sketch, "E2201", {"start": v(-26.3, 98.96) * mm, "end": v(-26, 98.3) * mm});
            skLineSegment(sketch, "E2202", {"start": v(-26, 98.3) * mm, "end": v(-25.91, 98.09) * mm});
            skLineSegment(sketch, "E2203", {"start": v(-25.91, 98.09) * mm, "end": v(-25.83, 97.9) * mm});
            skLineSegment(sketch, "E2204", {"start": v(-25.83, 97.9) * mm, "end": v(-25.52, 97.34) * mm});
            skLineSegment(sketch, "E2205", {"start": v(-25.52, 97.34) * mm, "end": v(-25.08, 96.8) * mm});
            skLineSegment(sketch, "E2206", {"start": v(-25.08, 96.8) * mm, "end": v(-24.5, 96.4) * mm});
            skLineSegment(sketch, "E2207", {"start": v(-24.5, 96.4) * mm, "end": v(-23.89, 96.11) * mm});
            skLineSegment(sketch, "E2208", {"start": v(-23.89, 96.11) * mm, "end": v(-23.68, 96.03) * mm});
            skLineSegment(sketch, "E2209", {"start": v(-23.68, 96.03) * mm, "end": v(-23.44, 95.93) * mm});
            skLineSegment(sketch, "E2210", {"start": v(-23.44, 95.93) * mm, "end": v(-22.7, 95.7) * mm});
            skLineSegment(sketch, "E2211", {"start": v(-22.7, 95.7) * mm, "end": v(-21.8, 95.52) * mm});
            skLineSegment(sketch, "E2212", {"start": v(-21.8, 95.52) * mm, "end": v(-21.01, 95.43) * mm});
            skLineSegment(sketch, "E2213", {"start": v(-21.01, 95.43) * mm, "end": v(-20.56, 95.42) * mm});
            skLineSegment(sketch, "E2214", {"start": v(-20.56, 95.42) * mm, "end": v(-20.41, 95.43) * mm});
            skLineSegment(sketch, "E2215", {"start": v(-20.41, 95.43) * mm, "end": v(-20.24, 95.43) * mm});
            skLineSegment(sketch, "E2216", {"start": v(-20.24, 95.43) * mm, "end": v(-19.67, 95.5) * mm});
            skLineSegment(sketch, "E2217", {"start": v(-19.67, 95.5) * mm, "end": v(-19.42, 95.62) * mm});
            skLineSegment(sketch, "E2218", {"start": v(-19.42, 95.62) * mm, "end": v(-19.4, 95.65) * mm});
            skLineSegment(sketch, "E2219", {"start": v(-19.4, 95.65) * mm, "end": v(-19.35, 95.75) * mm});
            skLineSegment(sketch, "E2220", {"start": v(-19.35, 95.75) * mm, "end": v(-19.36, 96.1) * mm});
            skLineSegment(sketch, "E2221", {"start": v(-19.36, 96.1) * mm, "end": v(-19.48, 96.21) * mm});
            skLineSegment(sketch, "E2222", {"start": v(-19.48, 96.21) * mm, "end": v(-19.43, 96.3) * mm});
            skLineSegment(sketch, "E2223", {"start": v(-19.43, 96.3) * mm, "end": v(-19.37, 96.55) * mm});
            skLineSegment(sketch, "E2224", {"start": v(-19.37, 96.55) * mm, "end": v(-19.4, 96.91) * mm});
            skLineSegment(sketch, "E2225", {"start": v(-19.4, 96.91) * mm, "end": v(-19.54, 97.24) * mm});
            skLineSegment(sketch, "E2226", {"start": v(-19.54, 97.24) * mm, "end": v(-19.61, 97.33) * mm});
            skLineSegment(sketch, "E2227", {"start": v(-19.61, 97.33) * mm, "end": v(-19.7, 97.43) * mm});
            skLineSegment(sketch, "E2228", {"start": v(-19.7, 97.43) * mm, "end": v(-20, 97.68) * mm});
            skLineSegment(sketch, "E2229", {"start": v(-20, 97.68) * mm, "end": v(-20.53, 98.05) * mm});
            skLineSegment(sketch, "E2230", {"start": v(-20.53, 98.05) * mm, "end": v(-21, 98.35) * mm});
            skLineSegment(sketch, "E2231", {"start": v(-21, 98.35) * mm, "end": v(-21.2, 98.47) * mm});
            skLineSegment(sketch, "E2232", {"start": v(-21.2, 98.47) * mm, "end": v(-21.32, 98.64) * mm});
            skLineSegment(sketch, "E2233", {"start": v(-21.32, 98.64) * mm, "end": v(-21.61, 99.1) * mm});
            skLineSegment(sketch, "E2234", {"start": v(-21.61, 99.1) * mm, "end": v(-21.96, 99.75) * mm});
            skLineSegment(sketch, "E2235", {"start": v(-21.96, 99.75) * mm, "end": v(-22.2, 100.33) * mm});
            skLineSegment(sketch, "E2236", {"start": v(-22.2, 100.33) * mm, "end": v(-22.25, 100.53) * mm});
            skLineSegment(sketch, "E2237", {"start": v(-22.25, 100.53) * mm, "end": v(-22.34, 100.85) * mm});
            skLineSegment(sketch, "E2238", {"start": v(-22.34, 100.85) * mm, "end": v(-22.6, 102.08) * mm});
            skLineSegment(sketch, "E2239", {"start": v(-22.6, 102.08) * mm, "end": v(-22.67, 103.1) * mm});
            skLineSegment(sketch, "E2240", {"start": v(-22.67, 103.1) * mm, "end": v(-22.66, 103.3) * mm});
            skLineSegment(sketch, "E2241", {"start": v(-22.66, 103.3) * mm, "end": v(-22.62, 103.33) * mm});
            skLineSegment(sketch, "E2242", {"start": v(-22.62, 103.33) * mm, "end": v(-22.55, 103.36) * mm});
            skLineSegment(sketch, "E2243", {"start": v(-22.55, 103.36) * mm, "end": v(-22.3, 103.58) * mm});
            skLineSegment(sketch, "E2244", {"start": v(-22.3, 103.58) * mm, "end": v(-22.24, 103.9) * mm});
            skLineSegment(sketch, "E2245", {"start": v(-22.24, 103.9) * mm, "end": v(-22.25, 103.95) * mm});
            skLineSegment(sketch, "E2246", {"start": v(-22.25, 103.95) * mm, "end": v(-22.26, 103.97) * mm});
            skLineSegment(sketch, "E2247", {"start": v(-22.26, 103.97) * mm, "end": v(-22.38, 104.2) * mm});
            skLineSegment(sketch, "E2248", {"start": v(-22.38, 104.2) * mm, "end": v(-22.4, 104.23) * mm});
            skLineSegment(sketch, "E2249", {"start": v(-22.4, 104.23) * mm, "end": v(-22.4, 104.23) * mm});
            skLineSegment(sketch, "E2250", {"start": v(-22.4, 104.23) * mm, "end": v(-22.42, 104.23) * mm});
            skLineSegment(sketch, "E2251", {"start": v(-22.42, 104.23) * mm, "end": v(-22.42, 104.17) * mm});
            skLineSegment(sketch, "E2252", {"start": v(-22.42, 104.17) * mm, "end": v(-22.55, 104) * mm});
            skLineSegment(sketch, "E2253", {"start": v(-22.55, 104) * mm, "end": v(-22.58, 103.99) * mm});
            skLineSegment(sketch, "E2254", {"start": v(-22.58, 103.99) * mm, "end": v(-22.63, 103.96) * mm});
            skLineSegment(sketch, "E2255", {"start": v(-22.63, 103.96) * mm, "end": v(-22.85, 104.04) * mm});
            skLineSegment(sketch, "E2256", {"start": v(-22.85, 104.04) * mm, "end": v(-23.03, 104.22) * mm});
            skLineSegment(sketch, "E2257", {"start": v(-23.03, 104.22) * mm, "end": v(-23.1, 104.23) * mm});
            skLineSegment(sketch, "E2258", {"start": v(-23.1, 104.23) * mm, "end": v(-23.18, 104.24) * mm});
            skLineSegment(sketch, "E2259", {"start": v(-23.18, 104.24) * mm, "end": v(-23.42, 104.38) * mm});
            skLineSegment(sketch, "E2260", {"start": v(-23.42, 104.38) * mm, "end": v(-23.35, 104.57) * mm});
            skLineSegment(sketch, "E2261", {"start": v(-23.35, 104.57) * mm, "end": v(-23.3, 104.6) * mm});
            skLineSegment(sketch, "E2262", {"start": v(-23.3, 104.6) * mm, "end": v(-23.29, 104.6) * mm});
            skLineSegment(sketch, "E2263", {"start": v(-23.29, 104.6) * mm, "end": v(-23.12, 104.68) * mm});
            skLineSegment(sketch, "E2264", {"start": v(-23.12, 104.68) * mm, "end": v(-22.83, 104.67) * mm});
            skLineSegment(sketch, "E2265", {"start": v(-22.83, 104.67) * mm, "end": v(-22.76, 104.63) * mm});
            skLineSegment(sketch, "E2266", {"start": v(-22.76, 104.63) * mm, "end": v(-22.74, 104.63) * mm});
            skLineSegment(sketch, "E2267", {"start": v(-22.74, 104.63) * mm, "end": v(-22.57, 104.52) * mm});
            skLineSegment(sketch, "E2268", {"start": v(-22.57, 104.52) * mm, "end": v(-22.55, 104.5) * mm});
            skLineSegment(sketch, "E2269", {"start": v(-22.55, 104.5) * mm, "end": v(-22.53, 104.52) * mm});
            skLineSegment(sketch, "E2270", {"start": v(-22.53, 104.52) * mm, "end": v(-22.53, 104.57) * mm});
            skLineSegment(sketch, "E2271", {"start": v(-22.53, 104.57) * mm, "end": v(-22.52, 104.65) * mm});
            skLineSegment(sketch, "E2272", {"start": v(-22.52, 104.65) * mm, "end": v(-22.48, 104.88) * mm});
            skLineSegment(sketch, "E2273", {"start": v(-22.48, 104.88) * mm, "end": v(-22.39, 105.28) * mm});
            skLineSegment(sketch, "E2274", {"start": v(-22.39, 105.28) * mm, "end": v(-22.22, 105.83) * mm});
            skLineSegment(sketch, "E2275", {"start": v(-22.22, 105.83) * mm, "end": v(-22, 106.4) * mm});
            skLineSegment(sketch, "E2276", {"start": v(-22, 106.4) * mm, "end": v(-21.92, 106.57) * mm});
            skLineSegment(sketch, "E2277", {"start": v(-21.92, 106.57) * mm, "end": v(-21.75, 106.98) * mm});
            skLineSegment(sketch, "E2278", {"start": v(-21.75, 106.98) * mm, "end": v(-21.08, 108.13) * mm});
            skLineSegment(sketch, "E2279", {"start": v(-21.08, 108.13) * mm, "end": v(-19.9, 109.9) * mm});
            skLineSegment(sketch, "E2280", {"start": v(-19.9, 109.9) * mm, "end": v(-18.76, 111.48) * mm});
            skLineSegment(sketch, "E2281", {"start": v(-18.76, 111.48) * mm, "end": v(-18.15, 112.3) * mm});
            skLineSegment(sketch, "E2282", {"start": v(-18.15, 112.3) * mm, "end": v(-18, 112.49) * mm});
            skLineSegment(sketch, "E2283", {"start": v(-18, 112.49) * mm, "end": v(-17.78, 112.75) * mm});
            skLineSegment(sketch, "E2284", {"start": v(-17.78, 112.75) * mm, "end": v(-17, 113.66) * mm});
            skLineSegment(sketch, "E2285", {"start": v(-17, 113.66) * mm, "end": v(-16.54, 114.16) * mm});
            skLineSegment(sketch, "E2286", {"start": v(-16.54, 114.16) * mm, "end": v(-16.5, 114.21) * mm});
            skLineSegment(sketch, "E2287", {"start": v(-16.5, 114.21) * mm, "end": v(-16.46, 114.26) * mm});
            skLineSegment(sketch, "E2288", {"start": v(-16.46, 114.26) * mm, "end": v(-16.35, 114.42) * mm});
            skLineSegment(sketch, "E2289", {"start": v(-16.35, 114.42) * mm, "end": v(-16.58, 114.52) * mm});
            skLineSegment(sketch, "E2290", {"start": v(-16.58, 114.52) * mm, "end": v(-16.65, 114.53) * mm});
            skLineSegment(sketch, "E2291", {"start": v(-25.36, 99.46) * mm, "end": v(-25.39, 99.43) * mm});
            skLineSegment(sketch, "E2292", {"start": v(-25.39, 99.43) * mm, "end": v(-25.57, 99.43) * mm});
            skLineSegment(sketch, "E2293", {"start": v(-25.57, 99.43) * mm, "end": v(-25.77, 99.7) * mm});
            skLineSegment(sketch, "E2294", {"start": v(-25.77, 99.7) * mm, "end": v(-25.95, 100.1) * mm});
            skLineSegment(sketch, "E2295", {"start": v(-25.95, 100.1) * mm, "end": v(-26.06, 100.4) * mm});
            skLineSegment(sketch, "E2296", {"start": v(-26.06, 100.4) * mm, "end": v(-26.1, 100.5) * mm});
            skLineSegment(sketch, "E2297", {"start": v(-26.1, 100.5) * mm, "end": v(-26.14, 100.6) * mm});
            skLineSegment(sketch, "E2298", {"start": v(-26.14, 100.6) * mm, "end": v(-26.54, 101.25) * mm});
            skLineSegment(sketch, "E2299", {"start": v(-26.54, 101.25) * mm, "end": v(-26.87, 101.95) * mm});
            skLineSegment(sketch, "E2300", {"start": v(-26.87, 101.95) * mm, "end": v(-26.87, 102.1) * mm});
            skLineSegment(sketch, "E2301", {"start": v(-26.87, 102.1) * mm, "end": v(-26.87, 102.23) * mm});
            skLineSegment(sketch, "E2302", {"start": v(-26.87, 102.23) * mm, "end": v(-26.8, 102.63) * mm});
            skLineSegment(sketch, "E2303", {"start": v(-26.8, 102.63) * mm, "end": v(-26.75, 102.74) * mm});
            skLineSegment(sketch, "E2304", {"start": v(-26.75, 102.74) * mm, "end": v(-26.72, 102.77) * mm});
            skLineSegment(sketch, "E2305", {"start": v(-26.72, 102.77) * mm, "end": v(-26.59, 102.8) * mm});
            skLineSegment(sketch, "E2306", {"start": v(-26.59, 102.8) * mm, "end": v(-26.5, 102.66) * mm});
            skLineSegment(sketch, "E2307", {"start": v(-26.5, 102.66) * mm, "end": v(-26.47, 102.39) * mm});
            skLineSegment(sketch, "E2308", {"start": v(-26.47, 102.39) * mm, "end": v(-26.45, 102.14) * mm});
            skLineSegment(sketch, "E2309", {"start": v(-26.45, 102.14) * mm, "end": v(-26.44, 102.06) * mm});
            skLineSegment(sketch, "E2310", {"start": v(-26.44, 102.06) * mm, "end": v(-26.44, 101.95) * mm});
            skLineSegment(sketch, "E2311", {"start": v(-26.44, 101.95) * mm, "end": v(-26.16, 101.51) * mm});
            skLineSegment(sketch, "E2312", {"start": v(-26.16, 101.51) * mm, "end": v(-25.7, 101.02) * mm});
            skLineSegment(sketch, "E2313", {"start": v(-25.7, 101.02) * mm, "end": v(-25.6, 100.88) * mm});
            skLineSegment(sketch, "E2314", {"start": v(-25.6, 100.88) * mm, "end": v(-25.5, 100.75) * mm});
            skLineSegment(sketch, "E2315", {"start": v(-25.5, 100.75) * mm, "end": v(-25.2, 100.1) * mm});
            skLineSegment(sketch, "E2316", {"start": v(-25.2, 100.1) * mm, "end": v(-25.28, 99.55) * mm});
            skLineSegment(sketch, "E2317", {"start": v(-25.28, 99.55) * mm, "end": v(-25.36, 99.46) * mm});
            skLineSegment(sketch, "E2318", {"start": v(-22.85, 97.8) * mm, "end": v(-22.83, 97.77) * mm});
            skLineSegment(sketch, "E2319", {"start": v(-22.83, 97.77) * mm, "end": v(-22.45, 97.38) * mm});
            skLineSegment(sketch, "E2320", {"start": v(-22.45, 97.38) * mm, "end": v(-22.4, 97.34) * mm});
            skLineSegment(sketch, "E2321", {"start": v(-22.4, 97.34) * mm, "end": v(-22.36, 97.32) * mm});
            skLineSegment(sketch, "E2322", {"start": v(-22.36, 97.32) * mm, "end": v(-21.98, 97.17) * mm});
            skLineSegment(sketch, "E2323", {"start": v(-21.98, 97.17) * mm, "end": v(-21.95, 97.16) * mm});
            skLineSegment(sketch, "E2324", {"start": v(-21.95, 97.16) * mm, "end": v(-21.94, 97.16) * mm});
            skLineSegment(sketch, "E2325", {"start": v(-21.94, 97.16) * mm, "end": v(-21.91, 97.1) * mm});
            skLineSegment(sketch, "E2326", {"start": v(-21.91, 97.1) * mm, "end": v(-21.92, 97.09) * mm});
            skLineSegment(sketch, "E2327", {"start": v(-21.92, 97.09) * mm, "end": v(-21.93, 97.08) * mm});
            skLineSegment(sketch, "E2328", {"start": v(-21.93, 97.08) * mm, "end": v(-22.06, 97.05) * mm});
            skLineSegment(sketch, "E2329", {"start": v(-22.06, 97.05) * mm, "end": v(-22.2, 97.05) * mm});
            skLineSegment(sketch, "E2330", {"start": v(-22.2, 97.05) * mm, "end": v(-22.57, 97.16) * mm});
            skLineSegment(sketch, "E2331", {"start": v(-22.57, 97.16) * mm, "end": v(-22.62, 97.2) * mm});
            skLineSegment(sketch, "E2332", {"start": v(-22.62, 97.2) * mm, "end": v(-22.7, 97.24) * mm});
            skLineSegment(sketch, "E2333", {"start": v(-22.7, 97.24) * mm, "end": v(-23.17, 97.42) * mm});
            skLineSegment(sketch, "E2334", {"start": v(-23.17, 97.42) * mm, "end": v(-23.65, 97.62) * mm});
            skLineSegment(sketch, "E2335", {"start": v(-23.65, 97.62) * mm, "end": v(-23.73, 97.68) * mm});
            skLineSegment(sketch, "E2336", {"start": v(-23.73, 97.68) * mm, "end": v(-23.77, 97.71) * mm});
            skLineSegment(sketch, "E2337", {"start": v(-23.77, 97.71) * mm, "end": v(-23.85, 97.86) * mm});
            skLineSegment(sketch, "E2338", {"start": v(-23.85, 97.86) * mm, "end": v(-23.77, 98) * mm});
            skLineSegment(sketch, "E2339", {"start": v(-23.77, 98) * mm, "end": v(-23.57, 98.12) * mm});
            skLineSegment(sketch, "E2340", {"start": v(-23.57, 98.12) * mm, "end": v(-23.39, 98.16) * mm});
            skLineSegment(sketch, "E2341", {"start": v(-23.39, 98.16) * mm, "end": v(-23.33, 98.16) * mm});
            skLineSegment(sketch, "E2342", {"start": v(-23.33, 98.16) * mm, "end": v(-23.24, 98.16) * mm});
            skLineSegment(sketch, "E2343", {"start": v(-23.24, 98.16) * mm, "end": v(-22.97, 97.98) * mm});
            skLineSegment(sketch, "E2344", {"start": v(-22.97, 97.98) * mm, "end": v(-22.85, 97.8) * mm});
            skLineSegment(sketch, "E2345", {"start": v(-23.89, 98.43) * mm, "end": v(-23.97, 98.43) * mm});
            skLineSegment(sketch, "E2346", {"start": v(-23.97, 98.43) * mm, "end": v(-24.2, 98.3) * mm});
            skLineSegment(sketch, "E2347", {"start": v(-24.2, 98.3) * mm, "end": v(-24.41, 98.18) * mm});
            skLineSegment(sketch, "E2348", {"start": v(-24.41, 98.18) * mm, "end": v(-24.48, 98.18) * mm});
            skLineSegment(sketch, "E2349", {"start": v(-24.48, 98.18) * mm, "end": v(-24.5, 98.18) * mm});
            skLineSegment(sketch, "E2350", {"start": v(-24.5, 98.18) * mm, "end": v(-24.6, 98.28) * mm});
            skLineSegment(sketch, "E2351", {"start": v(-24.6, 98.28) * mm, "end": v(-24.43, 98.54) * mm});
            skLineSegment(sketch, "E2352", {"start": v(-24.43, 98.54) * mm, "end": v(-24.36, 98.6) * mm});
            skLineSegment(sketch, "E2353", {"start": v(-24.36, 98.6) * mm, "end": v(-24.28, 98.68) * mm});
            skLineSegment(sketch, "E2354", {"start": v(-24.28, 98.68) * mm, "end": v(-23.82, 98.82) * mm});
            skLineSegment(sketch, "E2355", {"start": v(-23.82, 98.82) * mm, "end": v(-23.5, 98.79) * mm});
            skLineSegment(sketch, "E2356", {"start": v(-23.5, 98.79) * mm, "end": v(-23.48, 98.78) * mm});
            skLineSegment(sketch, "E2357", {"start": v(-23.48, 98.78) * mm, "end": v(-23.43, 98.77) * mm});
            skLineSegment(sketch, "E2358", {"start": v(-23.43, 98.77) * mm, "end": v(-23.28, 98.7) * mm});
            skLineSegment(sketch, "E2359", {"start": v(-23.28, 98.7) * mm, "end": v(-23.32, 98.57) * mm});
            skLineSegment(sketch, "E2360", {"start": v(-23.32, 98.57) * mm, "end": v(-23.54, 98.47) * mm});
            skLineSegment(sketch, "E2361", {"start": v(-23.54, 98.47) * mm, "end": v(-23.8, 98.43) * mm});
            skLineSegment(sketch, "E2362", {"start": v(-23.8, 98.43) * mm, "end": v(-23.89, 98.43) * mm});
            skLineSegment(sketch, "E2363", {"start": v(-24.39, 132.21) * mm, "end": v(-24.39, 131.91) * mm});
            skLineSegment(sketch, "E2364", {"start": v(-24.39, 131.91) * mm, "end": v(-24.23, 131.02) * mm});
            skLineSegment(sketch, "E2365", {"start": v(-24.23, 131.02) * mm, "end": v(-23.88, 130.14) * mm});
            skLineSegment(sketch, "E2366", {"start": v(-23.88, 130.14) * mm, "end": v(-23.5, 129.57) * mm});
            skLineSegment(sketch, "E2367", {"start": v(-23.5, 129.57) * mm, "end": v(-23.3, 129.35) * mm});
            skLineSegment(sketch, "E2368", {"start": v(-23.3, 129.35) * mm, "end": v(-23.27, 129.31) * mm});
            skLineSegment(sketch, "E2369", {"start": v(-23.27, 129.31) * mm, "end": v(-23.25, 129.3) * mm});
            skLineSegment(sketch, "E2370", {"start": v(-23.25, 129.3) * mm, "end": v(-23.16, 129.3) * mm});
            skLineSegment(sketch, "E2371", {"start": v(-23.16, 129.3) * mm, "end": v(-23.16, 129.6) * mm});
            skLineSegment(sketch, "E2372", {"start": v(-23.16, 129.6) * mm, "end": v(-23.16, 130.2) * mm});
            skLineSegment(sketch, "E2373", {"start": v(-23.16, 130.2) * mm, "end": v(-23, 131.08) * mm});
            skLineSegment(sketch, "E2374", {"start": v(-23, 131.08) * mm, "end": v(-22.53, 132.2) * mm});
            skLineSegment(sketch, "E2375", {"start": v(-22.53, 132.2) * mm, "end": v(-21.63, 133.53) * mm});
            skLineSegment(sketch, "E2376", {"start": v(-21.63, 133.53) * mm, "end": v(-20.16, 135.06) * mm});
            skLineSegment(sketch, "E2377", {"start": v(-20.16, 135.06) * mm, "end": v(-18.54, 136.35) * mm});
            skLineSegment(sketch, "E2378", {"start": v(-18.54, 136.35) * mm, "end": v(-17.97, 136.74) * mm});
            skLineSegment(sketch, "E2379", {"start": v(-17.97, 136.74) * mm, "end": v(-18.02, 136.75) * mm});
            skLineSegment(sketch, "E2380", {"start": v(-18.02, 136.75) * mm, "end": v(-18.03, 136.75) * mm});
            skLineSegment(sketch, "E2381", {"start": v(-18.03, 136.75) * mm, "end": v(-18.07, 136.75) * mm});
            skLineSegment(sketch, "E2382", {"start": v(-18.07, 136.75) * mm, "end": v(-18.16, 136.74) * mm});
            skLineSegment(sketch, "E2383", {"start": v(-18.16, 136.74) * mm, "end": v(-18.18, 136.74) * mm});
            skLineSegment(sketch, "E2384", {"start": v(-18.18, 136.74) * mm, "end": v(-18.45, 136.68) * mm});
            skLineSegment(sketch, "E2385", {"start": v(-18.45, 136.68) * mm, "end": v(-19.9, 136.29) * mm});
            skLineSegment(sketch, "E2386", {"start": v(-19.9, 136.29) * mm, "end": v(-21.27, 135.77) * mm});
            skLineSegment(sketch, "E2387", {"start": v(-21.27, 135.77) * mm, "end": v(-21.5, 135.64) * mm});
            skLineSegment(sketch, "E2388", {"start": v(-21.5, 135.64) * mm, "end": v(-21.57, 135.61) * mm});
            skLineSegment(sketch, "E2389", {"start": v(-21.57, 135.61) * mm, "end": v(-22.1, 135.3) * mm});
            skLineSegment(sketch, "E2390", {"start": v(-22.1, 135.3) * mm, "end": v(-22.14, 135.26) * mm});
            skLineSegment(sketch, "E2391", {"start": v(-22.14, 135.26) * mm, "end": v(-22.35, 135.13) * mm});
            skLineSegment(sketch, "E2392", {"start": v(-22.35, 135.13) * mm, "end": v(-23, 134.55) * mm});
            skLineSegment(sketch, "E2393", {"start": v(-23, 134.55) * mm, "end": v(-23.28, 134.08) * mm});
            skLineSegment(sketch, "E2394", {"start": v(-23.28, 134.08) * mm, "end": v(-23.32, 134) * mm});
            skLineSegment(sketch, "E2395", {"start": v(-23.32, 134) * mm, "end": v(-23.34, 133.98) * mm});
            skLineSegment(sketch, "E2396", {"start": v(-23.34, 133.98) * mm, "end": v(-23.34, 133.97) * mm});
            skLineSegment(sketch, "E2397", {"start": v(-23.34, 133.97) * mm, "end": v(-23.38, 133.89) * mm});
            skLineSegment(sketch, "E2398", {"start": v(-23.38, 133.89) * mm, "end": v(-23.46, 133.62) * mm});
            skLineSegment(sketch, "E2399", {"start": v(-23.46, 133.62) * mm, "end": v(-23.54, 133.3) * mm});
            skLineSegment(sketch, "E2400", {"start": v(-23.54, 133.3) * mm, "end": v(-23.6, 133.15) * mm});
            skLineSegment(sketch, "E2401", {"start": v(-23.6, 133.15) * mm, "end": v(-23.63, 133.32) * mm});
            skLineSegment(sketch, "E2402", {"start": v(-23.63, 133.32) * mm, "end": v(-23.64, 133.37) * mm});
            skLineSegment(sketch, "E2403", {"start": v(-23.64, 133.37) * mm, "end": v(-23.64, 133.47) * mm});
            skLineSegment(sketch, "E2404", {"start": v(-23.64, 133.47) * mm, "end": v(-23.6, 133.73) * mm});
            skLineSegment(sketch, "E2405", {"start": v(-23.6, 133.73) * mm, "end": v(-23.6, 133.76) * mm});
            skLineSegment(sketch, "E2406", {"start": v(-23.6, 133.76) * mm, "end": v(-23.6, 133.87) * mm});
            skLineSegment(sketch, "E2407", {"start": v(-23.6, 133.87) * mm, "end": v(-23.53, 134.15) * mm});
            skLineSegment(sketch, "E2408", {"start": v(-23.53, 134.15) * mm, "end": v(-23.52, 134.18) * mm});
            skLineSegment(sketch, "E2409", {"start": v(-23.52, 134.18) * mm, "end": v(-23.52, 134.2) * mm});
            skLineSegment(sketch, "E2410", {"start": v(-23.52, 134.2) * mm, "end": v(-23.43, 134.38) * mm});
            skLineSegment(sketch, "E2411", {"start": v(-23.43, 134.38) * mm, "end": v(-23.42, 134.4) * mm});
            skLineSegment(sketch, "E2412", {"start": v(-23.42, 134.4) * mm, "end": v(-23.4, 134.45) * mm});
            skLineSegment(sketch, "E2413", {"start": v(-23.4, 134.45) * mm, "end": v(-23.1, 134.95) * mm});
            skLineSegment(sketch, "E2414", {"start": v(-23.1, 134.95) * mm, "end": v(-23.07, 135) * mm});
            skLineSegment(sketch, "E2415", {"start": v(-23.07, 135) * mm, "end": v(-23, 135.1) * mm});
            skLineSegment(sketch, "E2416", {"start": v(-23, 135.1) * mm, "end": v(-21.9, 136) * mm});
            skLineSegment(sketch, "E2417", {"start": v(-21.9, 136) * mm, "end": v(-21.75, 136.09) * mm});
            skLineSegment(sketch, "E2418", {"start": v(-21.75, 136.09) * mm, "end": v(-21.33, 136.32) * mm});
            skLineSegment(sketch, "E2419", {"start": v(-21.33, 136.32) * mm, "end": v(-19.99, 136.83) * mm});
            skLineSegment(sketch, "E2420", {"start": v(-19.99, 136.83) * mm, "end": v(-18, 137.32) * mm});
            skLineSegment(sketch, "E2421", {"start": v(-18, 137.32) * mm, "end": v(-15.56, 137.86) * mm});
            skLineSegment(sketch, "E2422", {"start": v(-15.56, 137.86) * mm, "end": v(-13.22, 138.47) * mm});
            skLineSegment(sketch, "E2423", {"start": v(-13.22, 138.47) * mm, "end": v(-12.45, 138.71) * mm});
            skLineSegment(sketch, "E2424", {"start": v(-12.45, 138.71) * mm, "end": v(-12.2, 138.82) * mm});
            skLineSegment(sketch, "E2425", {"start": v(-12.2, 138.82) * mm, "end": v(-9.45, 140.11) * mm});
            skLineSegment(sketch, "E2426", {"start": v(-9.45, 140.11) * mm, "end": v(-9.17, 140.27) * mm});
            skLineSegment(sketch, "E2427", {"start": v(-9.17, 140.27) * mm, "end": v(-8.8, 140.49) * mm});
            skLineSegment(sketch, "E2428", {"start": v(-8.8, 140.49) * mm, "end": v(-7.77, 141.24) * mm});
            skLineSegment(sketch, "E2429", {"start": v(-7.77, 141.24) * mm, "end": v(-6.83, 142.15) * mm});
            skLineSegment(sketch, "E2430", {"start": v(-6.83, 142.15) * mm, "end": v(-6.13, 143) * mm});
            skLineSegment(sketch, "E2431", {"start": v(-6.13, 143) * mm, "end": v(-5.62, 143.58) * mm});
            skLineSegment(sketch, "E2432", {"start": v(-5.62, 143.58) * mm, "end": v(-5.43, 143.75) * mm});
            skLineSegment(sketch, "E2433", {"start": v(-5.43, 143.75) * mm, "end": v(-5.7, 143.65) * mm});
            skLineSegment(sketch, "E2434", {"start": v(-5.7, 143.65) * mm, "end": v(-6.5, 143.34) * mm});
            skLineSegment(sketch, "E2435", {"start": v(-6.5, 143.34) * mm, "end": v(-7.26, 143.03) * mm});
            skLineSegment(sketch, "E2436", {"start": v(-7.26, 143.03) * mm, "end": v(-7.84, 142.79) * mm});
            skLineSegment(sketch, "E2437", {"start": v(-7.84, 142.79) * mm, "end": v(-8.25, 142.63) * mm});
            skLineSegment(sketch, "E2438", {"start": v(-8.25, 142.63) * mm, "end": v(-8.39, 142.58) * mm});
            skLineSegment(sketch, "E2439", {"start": v(-8.39, 142.58) * mm, "end": v(-8.54, 142.53) * mm});
            skLineSegment(sketch, "E2440", {"start": v(-8.54, 142.53) * mm, "end": v(-9, 142.4) * mm});
            skLineSegment(sketch, "E2441", {"start": v(-9, 142.4) * mm, "end": v(-9.6, 142.23) * mm});
            skLineSegment(sketch, "E2442", {"start": v(-9.6, 142.23) * mm, "end": v(-10.19, 142.09) * mm});
            skLineSegment(sketch, "E2443", {"start": v(-10.19, 142.09) * mm, "end": v(-10.67, 142) * mm});
            skLineSegment(sketch, "E2444", {"start": v(-10.67, 142) * mm, "end": v(-11.02, 141.95) * mm});
            skLineSegment(sketch, "E2445", {"start": v(-11.02, 141.95) * mm, "end": v(-11.16, 141.97) * mm});
            skLineSegment(sketch, "E2446", {"start": v(-11.16, 141.97) * mm, "end": v(-11.06, 142.06) * mm});
            skLineSegment(sketch, "E2447", {"start": v(-11.06, 142.06) * mm, "end": v(-10.76, 142.19) * mm});
            skLineSegment(sketch, "E2448", {"start": v(-10.76, 142.19) * mm, "end": v(-10.65, 142.22) * mm});
            skLineSegment(sketch, "E2449", {"start": v(-10.65, 142.22) * mm, "end": v(-10.36, 142.33) * mm});
            skLineSegment(sketch, "E2450", {"start": v(-10.36, 142.33) * mm, "end": v(-9.49, 142.7) * mm});
            skLineSegment(sketch, "E2451", {"start": v(-9.49, 142.7) * mm, "end": v(-8.15, 143.3) * mm});
            skLineSegment(sketch, "E2452", {"start": v(-8.15, 143.3) * mm, "end": v(-6.48, 143.97) * mm});
            skLineSegment(sketch, "E2453", {"start": v(-6.48, 143.97) * mm, "end": v(-4.84, 144.5) * mm});
            skLineSegment(sketch, "E2454", {"start": v(-4.84, 144.5) * mm, "end": v(-4.3, 144.65) * mm});
            skLineSegment(sketch, "E2455", {"start": v(-4.3, 144.65) * mm, "end": v(-4.25, 144.67) * mm});
            skLineSegment(sketch, "E2456", {"start": v(-4.25, 144.67) * mm, "end": v(-3.83, 144.76) * mm});
            skLineSegment(sketch, "E2457", {"start": v(-3.83, 144.76) * mm, "end": v(-3.79, 144.77) * mm});
            skLineSegment(sketch, "E2458", {"start": v(-3.79, 144.77) * mm, "end": v(-3.76, 144.78) * mm});
            skLineSegment(sketch, "E2459", {"start": v(-3.76, 144.78) * mm, "end": v(-3.45, 144.84) * mm});
            skLineSegment(sketch, "E2460", {"start": v(-3.45, 144.84) * mm, "end": v(-3.42, 144.85) * mm});
            skLineSegment(sketch, "E2461", {"start": v(-3.42, 144.85) * mm, "end": v(-3.24, 144.88) * mm});
            skLineSegment(sketch, "E2462", {"start": v(-3.24, 144.88) * mm, "end": v(-1.9, 145.04) * mm});
            skLineSegment(sketch, "E2463", {"start": v(-1.9, 145.04) * mm, "end": v(-1.46, 145.04) * mm});
            skLineSegment(sketch, "E2464", {"start": v(-1.46, 145.04) * mm, "end": v(-1.16, 145.05) * mm});
            skLineSegment(sketch, "E2465", {"start": v(-1.16, 145.05) * mm, "end": v(-0.08, 144.97) * mm});
            skLineSegment(sketch, "E2466", {"start": v(-0.08, 144.97) * mm, "end": v(0.41, 144.88) * mm});
            skLineSegment(sketch, "E2467", {"start": v(0.41, 144.88) * mm, "end": v(0.52, 145) * mm});
            skLineSegment(sketch, "E2468", {"start": v(0.52, 145) * mm, "end": v(0.8, 145.28) * mm});
            skLineSegment(sketch, "E2469", {"start": v(0.8, 145.28) * mm, "end": v(1.14, 145.69) * mm});
            skLineSegment(sketch, "E2470", {"start": v(1.14, 145.69) * mm, "end": v(1.4, 146.04) * mm});
            skLineSegment(sketch, "E2471", {"start": v(1.4, 146.04) * mm, "end": v(1.48, 146.16) * mm});
            skLineSegment(sketch, "E2472", {"start": v(1.48, 146.16) * mm, "end": v(1.5, 146.19) * mm});
            skLineSegment(sketch, "E2473", {"start": v(1.5, 146.19) * mm, "end": v(1.62, 146.42) * mm});
            skLineSegment(sketch, "E2474", {"start": v(1.62, 146.42) * mm, "end": v(1.63, 146.44) * mm});
            skLineSegment(sketch, "E2475", {"start": v(1.63, 146.44) * mm, "end": v(1.64, 146.45) * mm});
            skLineSegment(sketch, "E2476", {"start": v(1.64, 146.45) * mm, "end": v(1.72, 146.58) * mm});
            skLineSegment(sketch, "E2477", {"start": v(1.72, 146.58) * mm, "end": v(1.73, 146.59) * mm});
            skLineSegment(sketch, "E2478", {"start": v(1.73, 146.59) * mm, "end": v(1.75, 146.54) * mm});
            skLineSegment(sketch, "E2479", {"start": v(1.75, 146.54) * mm, "end": v(1.75, 146.53) * mm});
            skLineSegment(sketch, "E2480", {"start": v(1.75, 146.53) * mm, "end": v(1.81, 146.4) * mm});
            skLineSegment(sketch, "E2481", {"start": v(1.81, 146.4) * mm, "end": v(2.03, 145.95) * mm});
            skLineSegment(sketch, "E2482", {"start": v(2.03, 145.95) * mm, "end": v(2.43, 145.2) * mm});
            skLineSegment(sketch, "E2483", {"start": v(2.43, 145.2) * mm, "end": v(2.86, 144.64) * mm});
            skLineSegment(sketch, "E2484", {"start": v(2.86, 144.64) * mm, "end": v(3.18, 144.51) * mm});
            skLineSegment(sketch, "E2485", {"start": v(3.18, 144.51) * mm, "end": v(3.22, 144.55) * mm});
            skLineSegment(sketch, "E2486", {"start": v(3.22, 144.55) * mm, "end": v(3.28, 144.6) * mm});
            skLineSegment(sketch, "E2487", {"start": v(3.28, 144.6) * mm, "end": v(3.4, 144.93) * mm});
            skLineSegment(sketch, "E2488", {"start": v(3.4, 144.93) * mm, "end": v(3.55, 145.62) * mm});
            skLineSegment(sketch, "E2489", {"start": v(3.55, 145.62) * mm, "end": v(3.7, 146.42) * mm});
            skLineSegment(sketch, "E2490", {"start": v(3.7, 146.42) * mm, "end": v(3.77, 146.94) * mm});
            skLineSegment(sketch, "E2491", {"start": v(3.77, 146.94) * mm, "end": v(3.8, 147.11) * mm});
            skLineSegment(sketch, "E2492", {"start": v(3.8, 147.11) * mm, "end": v(3.65, 147.18) * mm});
            skLineSegment(sketch, "E2493", {"start": v(3.65, 147.18) * mm, "end": v(2.93, 147.52) * mm});
            skLineSegment(sketch, "E2494", {"start": v(2.93, 147.52) * mm, "end": v(2.47, 147.74) * mm});
            skLineSegment(sketch, "E2495", {"start": v(2.47, 147.74) * mm, "end": v(2.45, 147.75) * mm});
            skLineSegment(sketch, "E2496", {"start": v(2.45, 147.75) * mm, "end": v(2.47, 147.77) * mm});
            skLineSegment(sketch, "E2497", {"start": v(2.47, 147.77) * mm, "end": v(2.56, 147.73) * mm});
            skLineSegment(sketch, "E2498", {"start": v(2.56, 147.73) * mm, "end": v(2.58, 147.73) * mm});
            skLineSegment(sketch, "E2499", {"start": v(2.58, 147.73) * mm, "end": v(2.62, 147.72) * mm});
            skLineSegment(sketch, "E2500", {"start": v(2.62, 147.72) * mm, "end": v(2.93, 147.67) * mm});
            skLineSegment(sketch, "E2501", {"start": v(2.93, 147.67) * mm, "end": v(3.25, 147.76) * mm});
            skLineSegment(sketch, "E2502", {"start": v(3.25, 147.76) * mm, "end": v(3.3, 147.81) * mm});
            skLineSegment(sketch, "E2503", {"start": v(3.3, 147.81) * mm, "end": v(3.32, 147.83) * mm});
            skLineSegment(sketch, "E2504", {"start": v(3.32, 147.83) * mm, "end": v(3.5, 147.98) * mm});
            skLineSegment(sketch, "E2505", {"start": v(3.5, 147.98) * mm, "end": v(3.52, 147.99) * mm});
            skLineSegment(sketch, "E2506", {"start": v(3.52, 147.99) * mm, "end": v(3.54, 148) * mm});
            skLineSegment(sketch, "E2507", {"start": v(3.54, 148) * mm, "end": v(3.8, 147.9) * mm});
            skLineSegment(sketch, "E2508", {"start": v(3.8, 147.9) * mm, "end": v(3.82, 147.86) * mm});
            skLineSegment(sketch, "E2509", {"start": v(3.82, 147.86) * mm, "end": v(3.83, 147.84) * mm});
            skLineSegment(sketch, "E2510", {"start": v(3.83, 147.84) * mm, "end": v(3.94, 147.63) * mm});
            skLineSegment(sketch, "E2511", {"start": v(3.94, 147.63) * mm, "end": v(3.95, 147.6) * mm});
            skLineSegment(sketch, "E2512", {"start": v(3.95, 147.6) * mm, "end": v(3.95, 147.57) * mm});
            skLineSegment(sketch, "E2513", {"start": v(3.95, 147.57) * mm, "end": v(4.08, 147.3) * mm});
            skLineSegment(sketch, "E2514", {"start": v(4.08, 147.3) * mm, "end": v(4.1, 147.28) * mm});
            skLineSegment(sketch, "E2515", {"start": v(4.1, 147.28) * mm, "end": v(4.13, 147.23) * mm});
            skLineSegment(sketch, "E2516", {"start": v(4.13, 147.23) * mm, "end": v(4.27, 147.1) * mm});
            skLineSegment(sketch, "E2517", {"start": v(4.27, 147.1) * mm, "end": v(4.45, 147) * mm});
            skLineSegment(sketch, "E2518", {"start": v(4.45, 147) * mm, "end": v(4.76, 146.9) * mm});
            skLineSegment(sketch, "E2519", {"start": v(4.76, 146.9) * mm, "end": v(5.16, 146.74) * mm});
            skLineSegment(sketch, "E2520", {"start": v(5.16, 146.74) * mm, "end": v(5.3, 146.69) * mm});
            skLineSegment(sketch, "E2521", {"start": v(5.3, 146.69) * mm, "end": v(5.32, 146.69) * mm});
            skLineSegment(sketch, "E2522", {"start": v(5.32, 146.69) * mm, "end": v(5.4, 146.65) * mm});
            skLineSegment(sketch, "E2523", {"start": v(5.4, 146.65) * mm, "end": v(5.4, 146.65) * mm});
            skLineSegment(sketch, "E2524", {"start": v(5.4, 146.65) * mm, "end": v(5.42, 146.64) * mm});
            skLineSegment(sketch, "E2525", {"start": v(5.42, 146.64) * mm, "end": v(5.47, 146.6) * mm});
            skLineSegment(sketch, "E2526", {"start": v(5.47, 146.6) * mm, "end": v(5.43, 146.69) * mm});
            skLineSegment(sketch, "E2527", {"start": v(5.43, 146.69) * mm, "end": v(5.41, 146.7) * mm});
            skLineSegment(sketch, "E2528", {"start": v(5.41, 146.7) * mm, "end": v(5.2, 147) * mm});
            skLineSegment(sketch, "E2529", {"start": v(5.2, 147) * mm, "end": v(5.17, 147.03) * mm});
            skLineSegment(sketch, "E2530", {"start": v(5.17, 147.03) * mm, "end": v(5.13, 147.1) * mm});
            skLineSegment(sketch, "E2531", {"start": v(5.13, 147.1) * mm, "end": v(5.08, 147.34) * mm});
            skLineSegment(sketch, "E2532", {"start": v(5.08, 147.34) * mm, "end": v(5.26, 147.46) * mm});
            skLineSegment(sketch, "E2533", {"start": v(5.26, 147.46) * mm, "end": v(5.56, 147.44) * mm});
            skLineSegment(sketch, "E2534", {"start": v(5.56, 147.44) * mm, "end": v(5.8, 147.35) * mm});
            skLineSegment(sketch, "E2535", {"start": v(5.8, 147.35) * mm, "end": v(5.86, 147.3) * mm});
            skLineSegment(sketch, "E2536", {"start": v(5.86, 147.3) * mm, "end": v(5.96, 147.22) * mm});
            skLineSegment(sketch, "E2537", {"start": v(5.96, 147.22) * mm, "end": v(6.15, 146.84) * mm});
            skLineSegment(sketch, "E2538", {"start": v(6.15, 146.84) * mm, "end": v(6.06, 146.53) * mm});
            skLineSegment(sketch, "E2539", {"start": v(6.06, 146.53) * mm, "end": v(6.04, 146.45) * mm});
            skLineSegment(sketch, "E2540", {"start": v(6.04, 146.45) * mm, "end": v(6.04, 146.44) * mm});
            skLineSegment(sketch, "E2541", {"start": v(6.04, 146.44) * mm, "end": v(6.05, 146.41) * mm});
            skLineSegment(sketch, "E2542", {"start": v(6.05, 146.41) * mm, "end": v(6.06, 146.41) * mm});
            skLineSegment(sketch, "E2543", {"start": v(6.06, 146.41) * mm, "end": v(6.17, 146.38) * mm});
            skLineSegment(sketch, "E2544", {"start": v(6.17, 146.38) * mm, "end": v(6.65, 146.28) * mm});
            skLineSegment(sketch, "E2545", {"start": v(6.65, 146.28) * mm, "end": v(7, 146.23) * mm});
            skLineSegment(sketch, "E2546", {"start": v(7, 146.23) * mm, "end": v(7.06, 146.22) * mm});
            skLineSegment(sketch, "E2547", {"start": v(7.06, 146.22) * mm, "end": v(7.17, 146.2) * mm});
            skLineSegment(sketch, "E2548", {"start": v(7.17, 146.2) * mm, "end": v(7.54, 146.33) * mm});
            skLineSegment(sketch, "E2549", {"start": v(7.54, 146.33) * mm, "end": v(7.7, 146.57) * mm});
            skLineSegment(sketch, "E2550", {"start": v(7.7, 146.57) * mm, "end": v(7.72, 146.6) * mm});
            skLineSegment(sketch, "E2551", {"start": v(7.72, 146.6) * mm, "end": v(7.74, 146.65) * mm});
            skLineSegment(sketch, "E2552", {"start": v(7.74, 146.65) * mm, "end": v(7.69, 146.82) * mm});
            skLineSegment(sketch, "E2553", {"start": v(7.69, 146.82) * mm, "end": v(7.47, 146.96) * mm});
            skLineSegment(sketch, "E2554", {"start": v(7.47, 146.96) * mm, "end": v(7.19, 147.18) * mm});
            skLineSegment(sketch, "E2555", {"start": v(7.19, 147.18) * mm, "end": v(7.01, 147.54) * mm});
            skLineSegment(sketch, "E2556", {"start": v(7.01, 147.54) * mm, "end": v(7, 147.66) * mm});
            skLineSegment(sketch, "E2557", {"start": v(7, 147.66) * mm, "end": v(6.97, 147.82) * mm});
            skLineSegment(sketch, "E2558", {"start": v(6.97, 147.82) * mm, "end": v(7, 148.33) * mm});
            skLineSegment(sketch, "E2559", {"start": v(7, 148.33) * mm, "end": v(7.19, 148.93) * mm});
            skLineSegment(sketch, "E2560", {"start": v(7.19, 148.93) * mm, "end": v(7.5, 149.43) * mm});
            skLineSegment(sketch, "E2561", {"start": v(7.5, 149.43) * mm, "end": v(7.74, 149.72) * mm});
            skLineSegment(sketch, "E2562", {"start": v(7.74, 149.72) * mm, "end": v(7.84, 149.8) * mm});
            skLineSegment(sketch, "E2563", {"start": v(7.84, 149.8) * mm, "end": v(7.88, 149.84) * mm});
            skLineSegment(sketch, "E2564", {"start": v(7.88, 149.84) * mm, "end": v(8.52, 150.24) * mm});
            skLineSegment(sketch, "E2565", {"start": v(8.52, 150.24) * mm, "end": v(8.59, 150.27) * mm});
            skLineSegment(sketch, "E2566", {"start": v(8.59, 150.27) * mm, "end": v(8.63, 150.3) * mm});
            skLineSegment(sketch, "E2567", {"start": v(8.63, 150.3) * mm, "end": v(8.97, 150.47) * mm});
            skLineSegment(sketch, "E2568", {"start": v(8.97, 150.47) * mm, "end": v(9, 150.49) * mm});
            skLineSegment(sketch, "E2569", {"start": v(9, 150.49) * mm, "end": v(9.02, 150.5) * mm});
            skLineSegment(sketch, "E2570", {"start": v(9.02, 150.5) * mm, "end": v(9.33, 150.67) * mm});
            skLineSegment(sketch, "E2571", {"start": v(9.33, 150.67) * mm, "end": v(9.35, 150.68) * mm});
            skLineSegment(sketch, "E2572", {"start": v(9.35, 150.68) * mm, "end": v(9.38, 150.7) * mm});
            skLineSegment(sketch, "E2573", {"start": v(9.38, 150.7) * mm, "end": v(9.6, 150.85) * mm});
            skLineSegment(sketch, "E2574", {"start": v(9.6, 150.85) * mm, "end": v(9.62, 150.88) * mm});
            skLineSegment(sketch, "E2575", {"start": v(9.62, 150.88) * mm, "end": v(9.63, 150.9) * mm});
            skLineSegment(sketch, "E2576", {"start": v(9.63, 150.9) * mm, "end": v(9.64, 151.06) * mm});
            skLineSegment(sketch, "E2577", {"start": v(9.64, 151.06) * mm, "end": v(9.63, 151.07) * mm});
            skLineSegment(sketch, "E2578", {"start": v(9.63, 151.07) * mm, "end": v(9.62, 151.07) * mm});
            skLineSegment(sketch, "E2579", {"start": v(9.62, 151.07) * mm, "end": v(9.47, 151.07) * mm});
            skLineSegment(sketch, "E2580", {"start": v(9.47, 151.07) * mm, "end": v(9.45, 151.07) * mm});
            skLineSegment(sketch, "E2581", {"start": v(9.45, 151.07) * mm, "end": v(9.4, 151.06) * mm});
            skLineSegment(sketch, "E2582", {"start": v(9.4, 151.06) * mm, "end": v(8.73, 151.04) * mm});
            skLineSegment(sketch, "E2583", {"start": v(8.73, 151.04) * mm, "end": v(8.65, 151.05) * mm});
            skLineSegment(sketch, "E2584", {"start": v(8.65, 151.05) * mm, "end": v(8.42, 151.05) * mm});
            skLineSegment(sketch, "E2585", {"start": v(8.42, 151.05) * mm, "end": v(7.82, 151.11) * mm});
            skLineSegment(sketch, "E2586", {"start": v(7.82, 151.11) * mm, "end": v(7.74, 151.12) * mm});
            skLineSegment(sketch, "E2587", {"start": v(7.74, 151.12) * mm, "end": v(7.7, 151.12) * mm});
            skLineSegment(sketch, "E2588", {"start": v(7.7, 151.12) * mm, "end": v(7.3, 151.17) * mm});
            skLineSegment(sketch, "E2589", {"start": v(7.3, 151.17) * mm, "end": v(7.27, 151.18) * mm});
            skLineSegment(sketch, "E2590", {"start": v(7.27, 151.18) * mm, "end": v(7.22, 151.19) * mm});
            skLineSegment(sketch, "E2591", {"start": v(7.22, 151.19) * mm, "end": v(6.7, 151.27) * mm});
            skLineSegment(sketch, "E2592", {"start": v(6.7, 151.27) * mm, "end": v(6.64, 151.28) * mm});
            skLineSegment(sketch, "E2593", {"start": v(6.64, 151.28) * mm, "end": v(6.46, 151.32) * mm});
            skLineSegment(sketch, "E2594", {"start": v(6.46, 151.32) * mm, "end": v(5.76, 151.49) * mm});
            skLineSegment(sketch, "E2595", {"start": v(5.76, 151.49) * mm, "end": v(5, 151.7) * mm});
            skLineSegment(sketch, "E2596", {"start": v(5, 151.7) * mm, "end": v(4.8, 151.75) * mm});
            skLineSegment(sketch, "E2597", {"start": v(4.8, 151.75) * mm, "end": v(4.71, 151.75) * mm});
            skLineSegment(sketch, "E2598", {"start": v(4.71, 151.75) * mm, "end": v(4.5, 151.82) * mm});
            skLineSegment(sketch, "E2599", {"start": v(4.5, 151.82) * mm, "end": v(4.48, 151.82) * mm});
            skLineSegment(sketch, "E2600", {"start": v(4.48, 151.82) * mm, "end": v(4.36, 151.86) * mm});
            skLineSegment(sketch, "E2601", {"start": v(4.36, 151.86) * mm, "end": v(4.1, 151.95) * mm});
            skLineSegment(sketch, "E2602", {"start": v(4.1, 151.95) * mm, "end": v(3.79, 152.04) * mm});
            skLineSegment(sketch, "E2603", {"start": v(3.79, 152.04) * mm, "end": v(3.62, 152.08) * mm});
            skLineSegment(sketch, "E2604", {"start": v(3.62, 152.08) * mm, "end": v(3.58, 152.1) * mm});
            skLineSegment(sketch, "E2605", {"start": v(3.58, 152.1) * mm, "end": v(3.47, 152.12) * mm});
            skLineSegment(sketch, "E2606", {"start": v(3.47, 152.12) * mm, "end": v(2.47, 152.27) * mm});
            skLineSegment(sketch, "E2607", {"start": v(2.47, 152.27) * mm, "end": v(2.36, 152.27) * mm});
            skLineSegment(sketch, "E2608", {"start": v(2.36, 152.27) * mm, "end": v(2.28, 152.27) * mm});
            skLineSegment(sketch, "E2609", {"start": v(2.28, 152.27) * mm, "end": v(1.6, 152.24) * mm});
            skLineSegment(sketch, "E2610", {"start": v(1.6, 152.24) * mm, "end": v(1.55, 152.24) * mm});
            skLineSegment(sketch, "E2611", {"start": v(1.55, 152.24) * mm, "end": v(1.36, 152.24) * mm});
            skLineSegment(sketch, "E2612", {"start": v(1.36, 152.24) * mm, "end": v(0.5, 152.16) * mm});
            skLineSegment(sketch, "E2613", {"start": v(0.5, 152.16) * mm, "end": v(-0.46, 152.15) * mm});
            skLineSegment(sketch, "E2614", {"start": v(-0.46, 152.15) * mm, "end": v(-0.69, 152.17) * mm});
            skLineSegment(sketch, "E2615", {"start": v(-0.69, 152.17) * mm, "end": v(-0.88, 152.2) * mm});
            skLineSegment(sketch, "E2616", {"start": v(-0.88, 152.2) * mm, "end": v(-1.44, 152.32) * mm});
            skLineSegment(sketch, "E2617", {"start": v(-1.44, 152.32) * mm, "end": v(-1.83, 152.49) * mm});
            skLineSegment(sketch, "E2618", {"start": v(-1.83, 152.49) * mm, "end": v(-1.86, 152.64) * mm});
            skLineSegment(sketch, "E2619", {"start": v(-1.86, 152.64) * mm, "end": v(-1.6, 152.71) * mm});
            skLineSegment(sketch, "E2620", {"start": v(-1.6, 152.71) * mm, "end": v(-1.5, 152.71) * mm});
            skLineSegment(sketch, "E2621", {"start": v(-1.5, 152.71) * mm, "end": v(-1.42, 152.72) * mm});
            skLineSegment(sketch, "E2622", {"start": v(-1.42, 152.72) * mm, "end": v(-0.9, 152.85) * mm});
            skLineSegment(sketch, "E2623", {"start": v(-0.9, 152.85) * mm, "end": v(-0.34, 152.96) * mm});
            skLineSegment(sketch, "E2624", {"start": v(-0.34, 152.96) * mm, "end": v(-0.15, 152.96) * mm});
            skLineSegment(sketch, "E2625", {"start": v(-0.15, 152.96) * mm, "end": v(0.02, 152.96) * mm});
            skLineSegment(sketch, "E2626", {"start": v(0.02, 152.96) * mm, "end": v(1.82, 152.87) * mm});
            skLineSegment(sketch, "E2627", {"start": v(1.82, 152.87) * mm, "end": v(2, 152.85) * mm});
            skLineSegment(sketch, "E2628", {"start": v(2, 152.85) * mm, "end": v(2.07, 152.84) * mm});
            skLineSegment(sketch, "E2629", {"start": v(2.07, 152.84) * mm, "end": v(2.8, 152.75) * mm});
            skLineSegment(sketch, "E2630", {"start": v(2.8, 152.75) * mm, "end": v(2.86, 152.73) * mm});
            skLineSegment(sketch, "E2631", {"start": v(2.86, 152.73) * mm, "end": v(2.92, 152.72) * mm});
            skLineSegment(sketch, "E2632", {"start": v(2.92, 152.72) * mm, "end": v(3.47, 152.55) * mm});
            skLineSegment(sketch, "E2633", {"start": v(3.47, 152.55) * mm, "end": v(3.52, 152.53) * mm});
            skLineSegment(sketch, "E2634", {"start": v(3.52, 152.53) * mm, "end": v(3.59, 152.5) * mm});
            skLineSegment(sketch, "E2635", {"start": v(3.59, 152.5) * mm, "end": v(4.03, 152.34) * mm});
            skLineSegment(sketch, "E2636", {"start": v(4.03, 152.34) * mm, "end": v(4.08, 152.33) * mm});
            skLineSegment(sketch, "E2637", {"start": v(4.08, 152.33) * mm, "end": v(4.12, 152.31) * mm});
            skLineSegment(sketch, "E2638", {"start": v(4.12, 152.31) * mm, "end": v(4.36, 152.23) * mm});
            skLineSegment(sketch, "E2639", {"start": v(4.36, 152.23) * mm, "end": v(4.4, 152.22) * mm});
            skLineSegment(sketch, "E2640", {"start": v(4.4, 152.22) * mm, "end": v(4.41, 152.22) * mm});
            skLineSegment(sketch, "E2641", {"start": v(4.41, 152.22) * mm, "end": v(4.57, 152.16) * mm});
            skLineSegment(sketch, "E2642", {"start": v(4.57, 152.16) * mm, "end": v(4.59, 152.15) * mm});
            skLineSegment(sketch, "E2643", {"start": v(4.59, 152.15) * mm, "end": v(4.64, 152.36) * mm});
            skLineSegment(sketch, "E2644", {"start": v(4.64, 152.36) * mm, "end": v(4.98, 153.78) * mm});
            skLineSegment(sketch, "E2645", {"start": v(4.98, 153.78) * mm, "end": v(5.38, 155.36) * mm});
            skLineSegment(sketch, "E2646", {"start": v(5.38, 155.36) * mm, "end": v(5.45, 155.65) * mm});
            skLineSegment(sketch, "E2647", {"start": v(5.45, 155.65) * mm, "end": v(5.52, 155.9) * mm});
            skLineSegment(sketch, "E2648", {"start": v(5.52, 155.9) * mm, "end": v(5.66, 156.65) * mm});
            skLineSegment(sketch, "E2649", {"start": v(5.66, 156.65) * mm, "end": v(5.87, 157.93) * mm});
            skLineSegment(sketch, "E2650", {"start": v(5.87, 157.93) * mm, "end": v(6.05, 159.26) * mm});
            skLineSegment(sketch, "E2651", {"start": v(6.05, 159.26) * mm, "end": v(6.15, 160.14) * mm});
            skLineSegment(sketch, "E2652", {"start": v(6.15, 160.14) * mm, "end": v(6.19, 160.43) * mm});
            skLineSegment(sketch, "E2653", {"start": v(6.19, 160.43) * mm, "end": v(6.26, 160.41) * mm});
            skLineSegment(sketch, "E2654", {"start": v(6.26, 160.41) * mm, "end": v(6.65, 160.3) * mm});
            skLineSegment(sketch, "E2655", {"start": v(6.65, 160.3) * mm, "end": v(7.62, 160.05) * mm});
            skLineSegment(sketch, "E2656", {"start": v(7.62, 160.05) * mm, "end": v(9.15, 159.73) * mm});
            skLineSegment(sketch, "E2657", {"start": v(9.15, 159.73) * mm, "end": v(10.76, 159.45) * mm});
            skLineSegment(sketch, "E2658", {"start": v(10.76, 159.45) * mm, "end": v(11.3, 159.37) * mm});
            skLineSegment(sketch, "E2659", {"start": v(11.3, 159.37) * mm, "end": v(11.84, 159.29) * mm});
            skLineSegment(sketch, "E2660", {"start": v(11.84, 159.29) * mm, "end": v(13.48, 159.14) * mm});
            skLineSegment(sketch, "E2661", {"start": v(13.48, 159.14) * mm, "end": v(15.36, 159.08) * mm});
            skLineSegment(sketch, "E2662", {"start": v(15.36, 159.08) * mm, "end": v(16.77, 159.14) * mm});
            skLineSegment(sketch, "E2663", {"start": v(16.77, 159.14) * mm, "end": v(17.4, 159.22) * mm});
            skLineSegment(sketch, "E2664", {"start": v(17.4, 159.22) * mm, "end": v(17.52, 159.27) * mm});
            skLineSegment(sketch, "E2665", {"start": v(17.52, 159.27) * mm, "end": v(17.62, 159.3) * mm});
            skLineSegment(sketch, "E2666", {"start": v(17.62, 159.3) * mm, "end": v(17.94, 159.44) * mm});
            skLineSegment(sketch, "E2667", {"start": v(17.94, 159.44) * mm, "end": v(18.45, 159.73) * mm});
            skLineSegment(sketch, "E2668", {"start": v(18.45, 159.73) * mm, "end": v(18.88, 160.08) * mm});
            skLineSegment(sketch, "E2669", {"start": v(18.88, 160.08) * mm, "end": v(19.08, 160.36) * mm});
            skLineSegment(sketch, "E2670", {"start": v(19.08, 160.36) * mm, "end": v(19.1, 160.46) * mm});
            skLineSegment(sketch, "E2671", {"start": v(19.1, 160.46) * mm, "end": v(19.12, 160.66) * mm});
            skLineSegment(sketch, "E2672", {"start": v(19.12, 160.66) * mm, "end": v(18.94, 161.3) * mm});
            skLineSegment(sketch, "E2673", {"start": v(18.94, 161.3) * mm, "end": v(18.39, 162.42) * mm});
            skLineSegment(sketch, "E2674", {"start": v(18.39, 162.42) * mm, "end": v(17.6, 163.63) * mm});
            skLineSegment(sketch, "E2675", {"start": v(17.6, 163.63) * mm, "end": v(16.95, 164.48) * mm});
            skLineSegment(sketch, "E2676", {"start": v(16.95, 164.48) * mm, "end": v(16.72, 164.75) * mm});
            skLineSegment(sketch, "E2677", {"start": v(16.72, 164.75) * mm, "end": v(16.56, 164.94) * mm});
            skLineSegment(sketch, "E2678", {"start": v(16.56, 164.94) * mm, "end": v(15.92, 165.87) * mm});
            skLineSegment(sketch, "E2679", {"start": v(15.92, 165.87) * mm, "end": v(15.52, 166.65) * mm});
            skLineSegment(sketch, "E2680", {"start": v(15.52, 166.65) * mm, "end": v(15.48, 166.76) * mm});
            skLineSegment(sketch, "E2681", {"start": v(15.48, 166.76) * mm, "end": v(15.47, 166.78) * mm});
            skLineSegment(sketch, "E2682", {"start": v(15.47, 166.78) * mm, "end": v(15.44, 166.95) * mm});
            skLineSegment(sketch, "E2683", {"start": v(15.44, 166.95) * mm, "end": v(15.43, 166.96) * mm});
            skLineSegment(sketch, "E2684", {"start": v(15.43, 166.96) * mm, "end": v(15.43, 167.08) * mm});
            skLineSegment(sketch, "E2685", {"start": v(15.43, 167.08) * mm, "end": v(15.35, 167.53) * mm});
            skLineSegment(sketch, "E2686", {"start": v(15.35, 167.53) * mm, "end": v(15, 167.79) * mm});
            skLineSegment(sketch, "E2687", {"start": v(15, 167.79) * mm, "end": v(14.87, 167.8) * mm});
            skLineSegment(sketch, "E2688", {"start": v(14.87, 167.8) * mm, "end": v(14.84, 167.8) * mm});
            skLineSegment(sketch, "E2689", {"start": v(14.84, 167.8) * mm, "end": v(14.61, 167.76) * mm});
            skLineSegment(sketch, "E2690", {"start": v(14.61, 167.76) * mm, "end": v(14.6, 167.75) * mm});
            skLineSegment(sketch, "E2691", {"start": v(14.6, 167.75) * mm, "end": v(14.54, 167.75) * mm});
            skLineSegment(sketch, "E2692", {"start": v(14.54, 167.75) * mm, "end": v(14.4, 167.87) * mm});
            skLineSegment(sketch, "E2693", {"start": v(14.4, 167.87) * mm, "end": v(14.39, 167.9) * mm});
            skLineSegment(sketch, "E2694", {"start": v(14.39, 167.9) * mm, "end": v(14.38, 167.92) * mm});
            skLineSegment(sketch, "E2695", {"start": v(14.38, 167.92) * mm, "end": v(14.35, 167.98) * mm});
            skLineSegment(sketch, "E2696", {"start": v(14.35, 167.98) * mm, "end": v(14.35, 168) * mm});
            skLineSegment(sketch, "E2697", {"start": v(14.35, 168) * mm, "end": v(14.35, 168.03) * mm});
            skLineSegment(sketch, "E2698", {"start": v(14.35, 168.03) * mm, "end": v(14.35, 168.03) * mm});
            skLineSegment(sketch, "E2699", {"start": v(14.35, 168.03) * mm, "end": v(14.34, 168.05) * mm});
            skLineSegment(sketch, "E2700", {"start": v(14.34, 168.05) * mm, "end": v(14.33, 168.09) * mm});
            skLineSegment(sketch, "E2701", {"start": v(14.33, 168.09) * mm, "end": v(14.16, 168.25) * mm});
            skLineSegment(sketch, "E2702", {"start": v(14.16, 168.25) * mm, "end": v(14.14, 168.25) * mm});
            skLineSegment(sketch, "E2703", {"start": v(14.14, 168.25) * mm, "end": v(14.13, 168.26) * mm});
            skLineSegment(sketch, "E2704", {"start": v(14.13, 168.26) * mm, "end": v(14, 168.3) * mm});
            skLineSegment(sketch, "E2705", {"start": v(14, 168.3) * mm, "end": v(13.99, 168.3) * mm});
            skLineSegment(sketch, "E2706", {"start": v(13.99, 168.3) * mm, "end": v(13.96, 168.31) * mm});
            skLineSegment(sketch, "E2707", {"start": v(13.96, 168.31) * mm, "end": v(13.76, 168.57) * mm});
            skLineSegment(sketch, "E2708", {"start": v(13.76, 168.57) * mm, "end": v(13.74, 168.62) * mm});
            skLineSegment(sketch, "E2709", {"start": v(13.74, 168.62) * mm, "end": v(13.73, 168.67) * mm});
            skLineSegment(sketch, "E2710", {"start": v(13.73, 168.67) * mm, "end": v(13.63, 168.95) * mm});
            skLineSegment(sketch, "E2711", {"start": v(13.63, 168.95) * mm, "end": v(13.62, 168.98) * mm});
            skLineSegment(sketch, "E2712", {"start": v(13.62, 168.98) * mm, "end": v(13.62, 169.01) * mm});
            skLineSegment(sketch, "E2713", {"start": v(13.62, 169.01) * mm, "end": v(13.61, 169.03) * mm});
            skLineSegment(sketch, "E2714", {"start": v(13.61, 169.03) * mm, "end": v(13.61, 169.03) * mm});
            skLineSegment(sketch, "E2715", {"start": v(13.61, 169.03) * mm, "end": v(13.6, 169.08) * mm});
            skLineSegment(sketch, "E2716", {"start": v(13.6, 169.08) * mm, "end": v(13.51, 169.25) * mm});
            skLineSegment(sketch, "E2717", {"start": v(13.51, 169.25) * mm, "end": v(13.36, 169.43) * mm});
            skLineSegment(sketch, "E2718", {"start": v(13.36, 169.43) * mm, "end": v(13.31, 169.48) * mm});
            skLineSegment(sketch, "E2719", {"start": v(13.31, 169.48) * mm, "end": v(13.29, 169.49) * mm});
            skLineSegment(sketch, "E2720", {"start": v(13.29, 169.49) * mm, "end": v(13.29, 169.49) * mm});
            skLineSegment(sketch, "E2721", {"start": v(13.29, 169.49) * mm, "end": v(13.26, 169.53) * mm});
            skLineSegment(sketch, "E2722", {"start": v(13.26, 169.53) * mm, "end": v(12.99, 170.08) * mm});
            skLineSegment(sketch, "E2723", {"start": v(12.99, 170.08) * mm, "end": v(12.96, 170.15) * mm});
            skLineSegment(sketch, "E2724", {"start": v(12.96, 170.15) * mm, "end": v(12.89, 170.32) * mm});
            skLineSegment(sketch, "E2725", {"start": v(12.89, 170.32) * mm, "end": v(12.66, 170.99) * mm});
            skLineSegment(sketch, "E2726", {"start": v(12.66, 170.99) * mm, "end": v(12.54, 171.45) * mm});
            skLineSegment(sketch, "E2727", {"start": v(12.54, 171.45) * mm, "end": v(12.52, 171.51) * mm});
            skLineSegment(sketch, "E2728", {"start": v(12.52, 171.51) * mm, "end": v(12.5, 171.56) * mm});
            skLineSegment(sketch, "E2729", {"start": v(12.5, 171.56) * mm, "end": v(12.19, 171.83) * mm});
            skLineSegment(sketch, "E2730", {"start": v(12.19, 171.83) * mm, "end": v(12.16, 171.84) * mm});
            skLineSegment(sketch, "E2731", {"start": v(12.16, 171.84) * mm, "end": v(12.15, 171.85) * mm});
            skLineSegment(sketch, "E2732", {"start": v(12.15, 171.85) * mm, "end": v(11.99, 171.86) * mm});
            skLineSegment(sketch, "E2733", {"start": v(11.99, 171.86) * mm, "end": v(11.94, 171.86) * mm});
            skLineSegment(sketch, "E2734", {"start": v(11.94, 171.86) * mm, "end": v(11.87, 171.87) * mm});
            skLineSegment(sketch, "E2735", {"start": v(11.87, 171.87) * mm, "end": v(11.6, 171.93) * mm});
            skLineSegment(sketch, "E2736", {"start": v(11.6, 171.93) * mm, "end": v(11.56, 171.99) * mm});
            skLineSegment(sketch, "E2737", {"start": v(11.56, 171.99) * mm, "end": v(11.58, 172) * mm});
            skLineSegment(sketch, "E2738", {"start": v(11.58, 172) * mm, "end": v(11.98, 172) * mm});
            skLineSegment(sketch, "E2739", {"start": v(11.98, 172) * mm, "end": v(12.03, 172) * mm});
            skLineSegment(sketch, "E2740", {"start": v(12.03, 172) * mm, "end": v(12.02, 172.03) * mm});
            skLineSegment(sketch, "E2741", {"start": v(12.02, 172.03) * mm, "end": v(11.9, 172.33) * mm});
            skLineSegment(sketch, "E2742", {"start": v(11.9, 172.33) * mm, "end": v(11.88, 172.36) * mm});
            skLineSegment(sketch, "E2743", {"start": v(11.88, 172.36) * mm, "end": v(11.85, 172.43) * mm});
            skLineSegment(sketch, "E2744", {"start": v(11.85, 172.43) * mm, "end": v(11.66, 172.63) * mm});
            skLineSegment(sketch, "E2745", {"start": v(11.66, 172.63) * mm, "end": v(11.45, 172.7) * mm});
            skLineSegment(sketch, "E2746", {"start": v(11.45, 172.7) * mm, "end": v(11.41, 172.7) * mm});
            skLineSegment(sketch, "E2747", {"start": v(11.41, 172.7) * mm, "end": v(11.36, 172.71) * mm});
            skLineSegment(sketch, "E2748", {"start": v(11.36, 172.71) * mm, "end": v(11.16, 172.73) * mm});
            skLineSegment(sketch, "E2749", {"start": v(11.16, 172.73) * mm, "end": v(10.78, 172.73) * mm});
            skLineSegment(sketch, "E2750", {"start": v(10.78, 172.73) * mm, "end": v(10.4, 172.68) * mm});
            skLineSegment(sketch, "E2751", {"start": v(10.4, 172.68) * mm, "end": v(10.21, 172.62) * mm});
            skLineSegment(sketch, "E2752", {"start": v(10.21, 172.62) * mm, "end": v(10.19, 172.58) * mm});
            skLineSegment(sketch, "E2753", {"start": v(10.19, 172.58) * mm, "end": v(10.17, 172.55) * mm});
            skLineSegment(sketch, "E2754", {"start": v(10.17, 172.55) * mm, "end": v(10.17, 172.53) * mm});
            skLineSegment(sketch, "E2755", {"start": v(10.17, 172.53) * mm, "end": v(10.18, 172.54) * mm});
            skLineSegment(sketch, "E2756", {"start": v(10.18, 172.54) * mm, "end": v(10.31, 172.58) * mm});
            skLineSegment(sketch, "E2757", {"start": v(10.31, 172.58) * mm, "end": v(10.35, 172.58) * mm});
            skLineSegment(sketch, "E2758", {"start": v(10.35, 172.58) * mm, "end": v(10.4, 172.58) * mm});
            skLineSegment(sketch, "E2759", {"start": v(10.4, 172.58) * mm, "end": v(10.56, 172.5) * mm});
            skLineSegment(sketch, "E2760", {"start": v(10.56, 172.5) * mm, "end": v(10.65, 172.3) * mm});
            skLineSegment(sketch, "E2761", {"start": v(10.65, 172.3) * mm, "end": v(10.66, 172.24) * mm});
            skLineSegment(sketch, "E2762", {"start": v(10.66, 172.24) * mm, "end": v(10.67, 172.19) * mm});
            skLineSegment(sketch, "E2763", {"start": v(10.67, 172.19) * mm, "end": v(10.67, 171.97) * mm});
            skLineSegment(sketch, "E2764", {"start": v(10.67, 171.97) * mm, "end": v(10.63, 171.86) * mm});
            skLineSegment(sketch, "E2765", {"start": v(10.63, 171.86) * mm, "end": v(10.78, 171.87) * mm});
            skLineSegment(sketch, "E2766", {"start": v(10.78, 171.87) * mm, "end": v(10.96, 171.76) * mm});
            skLineSegment(sketch, "E2767", {"start": v(10.96, 171.76) * mm, "end": v(10.98, 171.71) * mm});
            skLineSegment(sketch, "E2768", {"start": v(10.98, 171.71) * mm, "end": v(10.99, 171.66) * mm});
            skLineSegment(sketch, "E2769", {"start": v(10.99, 171.66) * mm, "end": v(10.98, 171.4) * mm});
            skLineSegment(sketch, "E2770", {"start": v(10.98, 171.4) * mm, "end": v(10.95, 171.23) * mm});
            skLineSegment(sketch, "E2771", {"start": v(10.95, 171.23) * mm, "end": v(11.03, 171.27) * mm});
            skLineSegment(sketch, "E2772", {"start": v(11.03, 171.27) * mm, "end": v(11.2, 171.22) * mm});
            skLineSegment(sketch, "E2773", {"start": v(11.2, 171.22) * mm, "end": v(11.23, 171.18) * mm});
            skLineSegment(sketch, "E2774", {"start": v(11.23, 171.18) * mm, "end": v(11.24, 171.17) * mm});
            skLineSegment(sketch, "E2775", {"start": v(11.24, 171.17) * mm, "end": v(11.3, 171.08) * mm});
            skLineSegment(sketch, "E2776", {"start": v(11.3, 171.08) * mm, "end": v(11.3, 171.07) * mm});
            skLineSegment(sketch, "E2777", {"start": v(11.3, 171.07) * mm, "end": v(11.3, 171.05) * mm});
            skLineSegment(sketch, "E2778", {"start": v(11.3, 171.05) * mm, "end": v(11.28, 170.8) * mm});
            skLineSegment(sketch, "E2779", {"start": v(11.28, 170.8) * mm, "end": v(11.27, 170.76) * mm});
            skLineSegment(sketch, "E2780", {"start": v(11.27, 170.76) * mm, "end": v(11.26, 170.75) * mm});
            skLineSegment(sketch, "E2781", {"start": v(11.26, 170.75) * mm, "end": v(11.22, 170.6) * mm});
            skLineSegment(sketch, "E2782", {"start": v(11.22, 170.6) * mm, "end": v(11.22, 170.58) * mm});
            skLineSegment(sketch, "E2783", {"start": v(11.22, 170.58) * mm, "end": v(11.21, 170.57) * mm});
            skLineSegment(sketch, "E2784", {"start": v(11.21, 170.57) * mm, "end": v(11.1, 170.47) * mm});
            skLineSegment(sketch, "E2785", {"start": v(11.1, 170.47) * mm, "end": v(11.1, 170.46) * mm});
            skLineSegment(sketch, "E2786", {"start": v(11.1, 170.46) * mm, "end": v(11.1, 170.45) * mm});
            skLineSegment(sketch, "E2787", {"start": v(11.1, 170.45) * mm, "end": v(11.08, 170.3) * mm});
            skLineSegment(sketch, "E2788", {"start": v(11.08, 170.3) * mm, "end": v(11.08, 170.27) * mm});
            skLineSegment(sketch, "E2789", {"start": v(11.08, 170.27) * mm, "end": v(11.07, 170.25) * mm});
            skLineSegment(sketch, "E2790", {"start": v(11.07, 170.25) * mm, "end": v(10.94, 169.94) * mm});
            skLineSegment(sketch, "E2791", {"start": v(10.94, 169.94) * mm, "end": v(10.92, 169.91) * mm});
            skLineSegment(sketch, "E2792", {"start": v(10.92, 169.91) * mm, "end": v(10.9, 169.9) * mm});
            skLineSegment(sketch, "E2793", {"start": v(10.9, 169.9) * mm, "end": v(10.8, 169.84) * mm});
            skLineSegment(sketch, "E2794", {"start": v(10.8, 169.84) * mm, "end": v(10.76, 169.84) * mm});
            skLineSegment(sketch, "E2795", {"start": v(10.76, 169.84) * mm, "end": v(10.72, 169.84) * mm});
            skLineSegment(sketch, "E2796", {"start": v(10.72, 169.84) * mm, "end": v(10.62, 169.91) * mm});
            skLineSegment(sketch, "E2797", {"start": v(10.62, 169.91) * mm, "end": v(10.58, 169.98) * mm});
            skLineSegment(sketch, "E2798", {"start": v(10.58, 169.98) * mm, "end": v(10.45, 169.81) * mm});
            skLineSegment(sketch, "E2799", {"start": v(10.45, 169.81) * mm, "end": v(10.21, 169.62) * mm});
            skLineSegment(sketch, "E2800", {"start": v(10.21, 169.62) * mm, "end": v(10.17, 169.61) * mm});
            skLineSegment(sketch, "E2801", {"start": v(10.17, 169.61) * mm, "end": v(10.13, 169.6) * mm});
            skLineSegment(sketch, "E2802", {"start": v(10.13, 169.6) * mm, "end": v(9.99, 169.68) * mm});
            skLineSegment(sketch, "E2803", {"start": v(9.99, 169.68) * mm, "end": v(9.92, 169.82) * mm});
            skLineSegment(sketch, "E2804", {"start": v(9.92, 169.82) * mm, "end": v(9.9, 169.84) * mm});
            skLineSegment(sketch, "E2805", {"start": v(9.9, 169.84) * mm, "end": v(9.9, 169.87) * mm});
            skLineSegment(sketch, "E2806", {"start": v(9.9, 169.87) * mm, "end": v(9.84, 170.33) * mm});
            skLineSegment(sketch, "E2807", {"start": v(9.84, 170.33) * mm, "end": v(9.74, 170.93) * mm});
            skLineSegment(sketch, "E2808", {"start": v(9.74, 170.93) * mm, "end": v(9.72, 171.02) * mm});
            skLineSegment(sketch, "E2809", {"start": v(9.72, 171.02) * mm, "end": v(9.72, 171.04) * mm});
            skLineSegment(sketch, "E2810", {"start": v(9.72, 171.04) * mm, "end": v(9.72, 171.29) * mm});
            skLineSegment(sketch, "E2811", {"start": v(9.72, 171.29) * mm, "end": v(9.74, 171.36) * mm});
            skLineSegment(sketch, "E2812", {"start": v(9.74, 171.36) * mm, "end": v(9.74, 171.37) * mm});
            skLineSegment(sketch, "E2813", {"start": v(9.74, 171.37) * mm, "end": v(9.75, 171.39) * mm});
            skLineSegment(sketch, "E2814", {"start": v(9.75, 171.39) * mm, "end": v(9.79, 171.57) * mm});
            skLineSegment(sketch, "E2815", {"start": v(9.79, 171.57) * mm, "end": v(9.8, 171.59) * mm});
            skLineSegment(sketch, "E2816", {"start": v(9.8, 171.59) * mm, "end": v(9.8, 171.64) * mm});
            skLineSegment(sketch, "E2817", {"start": v(9.8, 171.64) * mm, "end": v(9.85, 171.88) * mm});
            skLineSegment(sketch, "E2818", {"start": v(9.85, 171.88) * mm, "end": v(9.84, 172.02) * mm});
            skLineSegment(sketch, "E2819", {"start": v(9.84, 172.02) * mm, "end": v(9.84, 172.02) * mm});
            skLineSegment(sketch, "E2820", {"start": v(9.84, 172.02) * mm, "end": v(9.83, 172) * mm});
            skLineSegment(sketch, "E2821", {"start": v(9.83, 172) * mm, "end": v(9.7, 171.73) * mm});
            skLineSegment(sketch, "E2822", {"start": v(9.7, 171.73) * mm, "end": v(9.54, 171.3) * mm});
            skLineSegment(sketch, "E2823", {"start": v(9.54, 171.3) * mm, "end": v(9.54, 171.2) * mm});
            skLineSegment(sketch, "E2824", {"start": v(9.54, 171.2) * mm, "end": v(9.54, 171.12) * mm});
            skLineSegment(sketch, "E2825", {"start": v(9.54, 171.12) * mm, "end": v(9.54, 170.86) * mm});
            skLineSegment(sketch, "E2826", {"start": v(9.54, 170.86) * mm, "end": v(9.52, 170.57) * mm});
            skLineSegment(sketch, "E2827", {"start": v(9.52, 170.57) * mm, "end": v(9.52, 170.56) * mm});
            skLineSegment(sketch, "E2828", {"start": v(9.52, 170.56) * mm, "end": v(9.47, 170.58) * mm});
            skLineSegment(sketch, "E2829", {"start": v(9.47, 170.58) * mm, "end": v(9.47, 170.58) * mm});
            skLineSegment(sketch, "E2830", {"start": v(9.47, 170.58) * mm, "end": v(9.45, 170.61) * mm});
            skLineSegment(sketch, "E2831", {"start": v(9.45, 170.61) * mm, "end": v(9.26, 170.88) * mm});
            skLineSegment(sketch, "E2832", {"start": v(9.26, 170.88) * mm, "end": v(9.24, 170.9) * mm});
            skLineSegment(sketch, "E2833", {"start": v(9.24, 170.9) * mm, "end": v(9.2, 170.95) * mm});
            skLineSegment(sketch, "E2834", {"start": v(9.2, 170.95) * mm, "end": v(8.86, 171.16) * mm});
            skLineSegment(sketch, "E2835", {"start": v(8.86, 171.16) * mm, "end": v(8.5, 171.17) * mm});
            skLineSegment(sketch, "E2836", {"start": v(8.5, 171.17) * mm, "end": v(8.43, 171.12) * mm});
            skLineSegment(sketch, "E2837", {"start": v(8.43, 171.12) * mm, "end": v(8.4, 171.1) * mm});
            skLineSegment(sketch, "E2838", {"start": v(8.4, 171.1) * mm, "end": v(8.43, 170.9) * mm});
            skLineSegment(sketch, "E2839", {"start": v(8.43, 170.9) * mm, "end": v(8.64, 170.63) * mm});
            skLineSegment(sketch, "E2840", {"start": v(8.64, 170.63) * mm, "end": v(8.68, 170.56) * mm});
            skLineSegment(sketch, "E2841", {"start": v(8.68, 170.56) * mm, "end": v(8.71, 170.5) * mm});
            skLineSegment(sketch, "E2842", {"start": v(8.71, 170.5) * mm, "end": v(9.05, 169.75) * mm});
            skLineSegment(sketch, "E2843", {"start": v(9.05, 169.75) * mm, "end": v(9.08, 169.67) * mm});
            skLineSegment(sketch, "E2844", {"start": v(9.08, 169.67) * mm, "end": v(9.12, 169.59) * mm});
            skLineSegment(sketch, "E2845", {"start": v(9.12, 169.59) * mm, "end": v(9.26, 169.3) * mm});
            skLineSegment(sketch, "E2846", {"start": v(9.26, 169.3) * mm, "end": v(9.43, 169.06) * mm});
            skLineSegment(sketch, "E2847", {"start": v(9.43, 169.06) * mm, "end": v(9.5, 169) * mm});
            skLineSegment(sketch, "E2848", {"start": v(9.5, 169) * mm, "end": v(9.55, 168.95) * mm});
            skLineSegment(sketch, "E2849", {"start": v(9.55, 168.95) * mm, "end": v(10.03, 168.61) * mm});
            skLineSegment(sketch, "E2850", {"start": v(10.03, 168.61) * mm, "end": v(10.57, 168.3) * mm});
            skLineSegment(sketch, "E2851", {"start": v(10.57, 168.3) * mm, "end": v(10.66, 168.25) * mm});
            skLineSegment(sketch, "E2852", {"start": v(10.66, 168.25) * mm, "end": v(10.75, 168.21) * mm});
            skLineSegment(sketch, "E2853", {"start": v(10.75, 168.21) * mm, "end": v(11.23, 167.95) * mm});
            skLineSegment(sketch, "E2854", {"start": v(11.23, 167.95) * mm, "end": v(11.65, 167.66) * mm});
            skLineSegment(sketch, "E2855", {"start": v(11.65, 167.66) * mm, "end": v(11.7, 167.61) * mm});
            skLineSegment(sketch, "E2856", {"start": v(11.7, 167.61) * mm, "end": v(11.72, 167.6) * mm});
            skLineSegment(sketch, "E2857", {"start": v(11.72, 167.6) * mm, "end": v(11.86, 167.45) * mm});
            skLineSegment(sketch, "E2858", {"start": v(11.86, 167.45) * mm, "end": v(11.88, 167.42) * mm});
            skLineSegment(sketch, "E2859", {"start": v(11.88, 167.42) * mm, "end": v(11.9, 167.4) * mm});
            skLineSegment(sketch, "E2860", {"start": v(11.9, 167.4) * mm, "end": v(12.02, 167.22) * mm});
            skLineSegment(sketch, "E2861", {"start": v(12.02, 167.22) * mm, "end": v(12.03, 167.2) * mm});
            skLineSegment(sketch, "E2862", {"start": v(12.03, 167.2) * mm, "end": v(12.03, 167.2) * mm});
            skLineSegment(sketch, "E2863", {"start": v(12.03, 167.2) * mm, "end": v(12.17, 167.13) * mm});
            skLineSegment(sketch, "E2864", {"start": v(12.17, 167.13) * mm, "end": v(12.18, 167.12) * mm});
            skLineSegment(sketch, "E2865", {"start": v(12.18, 167.12) * mm, "end": v(12.19, 167.12) * mm});
            skLineSegment(sketch, "E2866", {"start": v(12.19, 167.12) * mm, "end": v(12.25, 167.1) * mm});
            skLineSegment(sketch, "E2867", {"start": v(12.25, 167.1) * mm, "end": v(12.27, 167.1) * mm});
            skLineSegment(sketch, "E2868", {"start": v(12.27, 167.1) * mm, "end": v(12.41, 167.1) * mm});
            skLineSegment(sketch, "E2869", {"start": v(12.41, 167.1) * mm, "end": v(12.65, 167.1) * mm});
            skLineSegment(sketch, "E2870", {"start": v(12.65, 167.1) * mm, "end": v(12.73, 167.1) * mm});
            skLineSegment(sketch, "E2871", {"start": v(12.73, 167.1) * mm, "end": v(12.78, 167.1) * mm});
            skLineSegment(sketch, "E2872", {"start": v(12.78, 167.1) * mm, "end": v(12.93, 167.09) * mm});
            skLineSegment(sketch, "E2873", {"start": v(12.93, 167.09) * mm, "end": v(12.94, 167.08) * mm});
            skLineSegment(sketch, "E2874", {"start": v(12.94, 167.08) * mm, "end": v(12.97, 167.07) * mm});
            skLineSegment(sketch, "E2875", {"start": v(12.97, 167.07) * mm, "end": v(13.03, 166.95) * mm});
            skLineSegment(sketch, "E2876", {"start": v(13.03, 166.95) * mm, "end": v(13, 166.83) * mm});
            skLineSegment(sketch, "E2877", {"start": v(13, 166.83) * mm, "end": v(12.98, 166.82) * mm});
            skLineSegment(sketch, "E2878", {"start": v(12.98, 166.82) * mm, "end": v(12.97, 166.8) * mm});
            skLineSegment(sketch, "E2879", {"start": v(12.97, 166.8) * mm, "end": v(12.79, 166.64) * mm});
            skLineSegment(sketch, "E2880", {"start": v(12.79, 166.64) * mm, "end": v(12.76, 166.63) * mm});
            skLineSegment(sketch, "E2881", {"start": v(12.76, 166.63) * mm, "end": v(12.74, 166.62) * mm});
            skLineSegment(sketch, "E2882", {"start": v(12.74, 166.62) * mm, "end": v(12.6, 166.55) * mm});
            skLineSegment(sketch, "E2883", {"start": v(12.6, 166.55) * mm, "end": v(12.6, 166.55) * mm});
            skLineSegment(sketch, "E2884", {"start": v(12.6, 166.55) * mm, "end": v(12.57, 166.54) * mm});
            skLineSegment(sketch, "E2885", {"start": v(12.57, 166.54) * mm, "end": v(12.38, 166.49) * mm});
            skLineSegment(sketch, "E2886", {"start": v(12.38, 166.49) * mm, "end": v(12.36, 166.48) * mm});
            skLineSegment(sketch, "E2887", {"start": v(12.36, 166.48) * mm, "end": v(12.02, 166.48) * mm});
            skLineSegment(sketch, "E2888", {"start": v(12.02, 166.48) * mm, "end": v(11.94, 166.5) * mm});
            skLineSegment(sketch, "E2889", {"start": v(11.94, 166.5) * mm, "end": v(11.91, 166.5) * mm});
            skLineSegment(sketch, "E2890", {"start": v(11.91, 166.5) * mm, "end": v(11.72, 166.55) * mm});
            skLineSegment(sketch, "E2891", {"start": v(11.72, 166.55) * mm, "end": v(11.7, 166.55) * mm});
            skLineSegment(sketch, "E2892", {"start": v(11.7, 166.55) * mm, "end": v(11.68, 166.56) * mm});
            skLineSegment(sketch, "E2893", {"start": v(11.68, 166.56) * mm, "end": v(11.68, 166.57) * mm});
            skLineSegment(sketch, "E2894", {"start": v(11.68, 166.57) * mm, "end": v(11.67, 166.57) * mm});
            skLineSegment(sketch, "E2895", {"start": v(11.67, 166.57) * mm, "end": v(11.62, 166.59) * mm});
            skLineSegment(sketch, "E2896", {"start": v(11.62, 166.59) * mm, "end": v(11.6, 166.59) * mm});
            skLineSegment(sketch, "E2897", {"start": v(11.6, 166.59) * mm, "end": v(11.58, 166.6) * mm});
            skLineSegment(sketch, "E2898", {"start": v(11.58, 166.6) * mm, "end": v(11.53, 166.64) * mm});
            skLineSegment(sketch, "E2899", {"start": v(11.53, 166.64) * mm, "end": v(11.33, 166.81) * mm});
            skLineSegment(sketch, "E2900", {"start": v(11.33, 166.81) * mm, "end": v(11.21, 166.94) * mm});
            skLineSegment(sketch, "E2901", {"start": v(11.21, 166.94) * mm, "end": v(11.21, 166.95) * mm});
            skLineSegment(sketch, "E2902", {"start": v(11.21, 166.95) * mm, "end": v(11.19, 167) * mm});
            skLineSegment(sketch, "E2903", {"start": v(11.19, 167) * mm, "end": v(11.17, 167.01) * mm});
            skLineSegment(sketch, "E2904", {"start": v(11.17, 167.01) * mm, "end": v(11.01, 167.06) * mm});
            skLineSegment(sketch, "E2905", {"start": v(11.01, 167.06) * mm, "end": v(11, 167.05) * mm});
            skLineSegment(sketch, "E2906", {"start": v(11, 167.05) * mm, "end": v(10.96, 167.04) * mm});
            skLineSegment(sketch, "E2907", {"start": v(10.96, 167.04) * mm, "end": v(10.79, 166.94) * mm});
            skLineSegment(sketch, "E2908", {"start": v(10.79, 166.94) * mm, "end": v(10.7, 166.81) * mm});
            skLineSegment(sketch, "E2909", {"start": v(10.7, 166.81) * mm, "end": v(10.71, 166.79) * mm});
            skLineSegment(sketch, "E2910", {"start": v(10.71, 166.79) * mm, "end": v(10.74, 166.73) * mm});
            skLineSegment(sketch, "E2911", {"start": v(10.74, 166.73) * mm, "end": v(10.74, 166.7) * mm});
            skLineSegment(sketch, "E2912", {"start": v(10.74, 166.7) * mm, "end": v(10.77, 166.66) * mm});
            skLineSegment(sketch, "E2913", {"start": v(10.77, 166.66) * mm, "end": v(10.86, 166.3) * mm});
            skLineSegment(sketch, "E2914", {"start": v(10.86, 166.3) * mm, "end": v(10.85, 165.84) * mm});
            skLineSegment(sketch, "E2915", {"start": v(10.85, 165.84) * mm, "end": v(10.85, 165.76) * mm});
            skLineSegment(sketch, "E2916", {"start": v(10.85, 165.76) * mm, "end": v(10.84, 165.69) * mm});
            skLineSegment(sketch, "E2917", {"start": v(10.84, 165.69) * mm, "end": v(10.86, 165.47) * mm});
            skLineSegment(sketch, "E2918", {"start": v(10.86, 165.47) * mm, "end": v(10.92, 165.23) * mm});
            skLineSegment(sketch, "E2919", {"start": v(10.92, 165.23) * mm, "end": v(11.05, 165.15) * mm});
            skLineSegment(sketch, "E2920", {"start": v(11.05, 165.15) * mm, "end": v(11.21, 165.29) * mm});
            skLineSegment(sketch, "E2921", {"start": v(11.21, 165.29) * mm, "end": v(11.25, 165.35) * mm});
            skLineSegment(sketch, "E2922", {"start": v(11.25, 165.35) * mm, "end": v(11.27, 165.39) * mm});
            skLineSegment(sketch, "E2923", {"start": v(11.27, 165.39) * mm, "end": v(11.47, 165.42) * mm});
            skLineSegment(sketch, "E2924", {"start": v(11.47, 165.42) * mm, "end": v(11.74, 165.22) * mm});
            skLineSegment(sketch, "E2925", {"start": v(11.74, 165.22) * mm, "end": v(11.91, 164.92) * mm});
            skLineSegment(sketch, "E2926", {"start": v(11.91, 164.92) * mm, "end": v(11.88, 164.7) * mm});
            skLineSegment(sketch, "E2927", {"start": v(11.88, 164.7) * mm, "end": v(11.84, 164.68) * mm});
            skLineSegment(sketch, "E2928", {"start": v(11.84, 164.68) * mm, "end": v(11.79, 164.65) * mm});
            skLineSegment(sketch, "E2929", {"start": v(11.79, 164.65) * mm, "end": v(11.6, 164.6) * mm});
            skLineSegment(sketch, "E2930", {"start": v(11.6, 164.6) * mm, "end": v(11.38, 164.56) * mm});
            skLineSegment(sketch, "E2931", {"start": v(11.38, 164.56) * mm, "end": v(11.26, 164.51) * mm});
            skLineSegment(sketch, "E2932", {"start": v(11.26, 164.51) * mm, "end": v(11.28, 164.38) * mm});
            skLineSegment(sketch, "E2933", {"start": v(11.28, 164.38) * mm, "end": v(11.3, 164.34) * mm});
            skLineSegment(sketch, "E2934", {"start": v(11.3, 164.34) * mm, "end": v(11.35, 164.25) * mm});
            skLineSegment(sketch, "E2935", {"start": v(11.35, 164.25) * mm, "end": v(11.72, 164.05) * mm});
            skLineSegment(sketch, "E2936", {"start": v(11.72, 164.05) * mm, "end": v(12.22, 163.83) * mm});
            skLineSegment(sketch, "E2937", {"start": v(12.22, 163.83) * mm, "end": v(12.34, 163.73) * mm});
            skLineSegment(sketch, "E2938", {"start": v(12.34, 163.73) * mm, "end": v(12.35, 163.71) * mm});
            skLineSegment(sketch, "E2939", {"start": v(12.35, 163.71) * mm, "end": v(12.36, 163.7) * mm});
            skLineSegment(sketch, "E2940", {"start": v(12.36, 163.7) * mm, "end": v(12.46, 163.67) * mm});
            skLineSegment(sketch, "E2941", {"start": v(12.46, 163.67) * mm, "end": v(12.47, 163.67) * mm});
            skLineSegment(sketch, "E2942", {"start": v(12.47, 163.67) * mm, "end": v(12.64, 163.65) * mm});
            skLineSegment(sketch, "E2943", {"start": v(12.64, 163.65) * mm, "end": v(12.66, 163.64) * mm});
            skLineSegment(sketch, "E2944", {"start": v(12.66, 163.64) * mm, "end": v(12.72, 163.63) * mm});
            skLineSegment(sketch, "E2945", {"start": v(12.72, 163.63) * mm, "end": v(12.73, 163.63) * mm});
            skLineSegment(sketch, "E2946", {"start": v(12.73, 163.63) * mm, "end": v(12.8, 163.63) * mm});
            skLineSegment(sketch, "E2947", {"start": v(12.8, 163.63) * mm, "end": v(12.98, 163.64) * mm});
            skLineSegment(sketch, "E2948", {"start": v(12.98, 163.64) * mm, "end": v(13, 163.64) * mm});
            skLineSegment(sketch, "E2949", {"start": v(13, 163.64) * mm, "end": v(13.07, 163.65) * mm});
            skLineSegment(sketch, "E2950", {"start": v(13.07, 163.65) * mm, "end": v(13.5, 163.62) * mm});
            skLineSegment(sketch, "E2951", {"start": v(13.5, 163.62) * mm, "end": v(13.52, 163.6) * mm});
            skLineSegment(sketch, "E2952", {"start": v(13.52, 163.6) * mm, "end": v(13.52, 163.6) * mm});
            skLineSegment(sketch, "E2953", {"start": v(13.52, 163.6) * mm, "end": v(13.48, 163.43) * mm});
            skLineSegment(sketch, "E2954", {"start": v(13.48, 163.43) * mm, "end": v(13.45, 163.4) * mm});
            skLineSegment(sketch, "E2955", {"start": v(13.45, 163.4) * mm, "end": v(13.4, 163.38) * mm});
            skLineSegment(sketch, "E2956", {"start": v(13.4, 163.38) * mm, "end": v(13, 163.2) * mm});
            skLineSegment(sketch, "E2957", {"start": v(13, 163.2) * mm, "end": v(12.97, 163.2) * mm});
            skLineSegment(sketch, "E2958", {"start": v(12.97, 163.2) * mm, "end": v(13.01, 163.12) * mm});
            skLineSegment(sketch, "E2959", {"start": v(13.01, 163.12) * mm, "end": v(13.34, 162.5) * mm});
            skLineSegment(sketch, "E2960", {"start": v(13.34, 162.5) * mm, "end": v(13.36, 162.44) * mm});
            skLineSegment(sketch, "E2961", {"start": v(13.36, 162.44) * mm, "end": v(13.38, 162.41) * mm});
            skLineSegment(sketch, "E2962", {"start": v(13.38, 162.41) * mm, "end": v(13.54, 162.15) * mm});
            skLineSegment(sketch, "E2963", {"start": v(13.54, 162.15) * mm, "end": v(13.56, 162.12) * mm});
            skLineSegment(sketch, "E2964", {"start": v(13.56, 162.12) * mm, "end": v(13.6, 162.04) * mm});
            skLineSegment(sketch, "E2965", {"start": v(13.6, 162.04) * mm, "end": v(13.8, 161.83) * mm});
            skLineSegment(sketch, "E2966", {"start": v(13.8, 161.83) * mm, "end": v(14.13, 161.53) * mm});
            skLineSegment(sketch, "E2967", {"start": v(14.13, 161.53) * mm, "end": v(14.62, 161.16) * mm});
            skLineSegment(sketch, "E2968", {"start": v(14.62, 161.16) * mm, "end": v(15.15, 160.78) * mm});
            skLineSegment(sketch, "E2969", {"start": v(15.15, 160.78) * mm, "end": v(15.32, 160.66) * mm});
            skLineSegment(sketch, "E2970", {"start": v(15.32, 160.66) * mm, "end": v(15.24, 160.63) * mm});
            skLineSegment(sketch, "E2971", {"start": v(15.24, 160.63) * mm, "end": v(14.69, 160.85) * mm});
            skLineSegment(sketch, "E2972", {"start": v(14.69, 160.85) * mm, "end": v(13.95, 161.25) * mm});
            skLineSegment(sketch, "E2973", {"start": v(13.95, 161.25) * mm, "end": v(13.45, 161.6) * mm});
            skLineSegment(sketch, "E2974", {"start": v(13.45, 161.6) * mm, "end": v(13.31, 161.74) * mm});
            skLineSegment(sketch, "E2975", {"start": v(13.31, 161.74) * mm, "end": v(13.3, 161.75) * mm});
            skLineSegment(sketch, "E2976", {"start": v(13.3, 161.75) * mm, "end": v(13.21, 161.85) * mm});
            skLineSegment(sketch, "E2977", {"start": v(13.21, 161.85) * mm, "end": v(13.2, 161.86) * mm});
            skLineSegment(sketch, "E2978", {"start": v(13.2, 161.86) * mm, "end": v(13.17, 161.9) * mm});
            skLineSegment(sketch, "E2979", {"start": v(13.17, 161.9) * mm, "end": v(12.9, 162.37) * mm});
            skLineSegment(sketch, "E2980", {"start": v(12.9, 162.37) * mm, "end": v(12.89, 162.42) * mm});
            skLineSegment(sketch, "E2981", {"start": v(12.89, 162.42) * mm, "end": v(12.88, 162.45) * mm});
            skLineSegment(sketch, "E2982", {"start": v(12.88, 162.45) * mm, "end": v(12.82, 162.65) * mm});
            skLineSegment(sketch, "E2983", {"start": v(12.82, 162.65) * mm, "end": v(12.81, 162.66) * mm});
            skLineSegment(sketch, "E2984", {"start": v(12.81, 162.66) * mm, "end": v(12.8, 162.7) * mm});
            skLineSegment(sketch, "E2985", {"start": v(12.8, 162.7) * mm, "end": v(12.63, 162.9) * mm});
            skLineSegment(sketch, "E2986", {"start": v(12.63, 162.9) * mm, "end": v(12.6, 162.92) * mm});
            skLineSegment(sketch, "E2987", {"start": v(12.6, 162.92) * mm, "end": v(12.53, 162.95) * mm});
            skLineSegment(sketch, "E2988", {"start": v(12.53, 162.95) * mm, "end": v(12.27, 162.92) * mm});
            skLineSegment(sketch, "E2989", {"start": v(12.27, 162.92) * mm, "end": v(12.1, 162.56) * mm});
            skLineSegment(sketch, "E2990", {"start": v(12.1, 162.56) * mm, "end": v(12.09, 162.44) * mm});
            skLineSegment(sketch, "E2991", {"start": v(12.09, 162.44) * mm, "end": v(12.08, 162.4) * mm});
            skLineSegment(sketch, "E2992", {"start": v(12.08, 162.4) * mm, "end": v(12.07, 162.08) * mm});
            skLineSegment(sketch, "E2993", {"start": v(12.07, 162.08) * mm, "end": v(12.07, 161.97) * mm});
            skLineSegment(sketch, "E2994", {"start": v(12.07, 161.97) * mm, "end": v(12.07, 161.8) * mm});
            skLineSegment(sketch, "E2995", {"start": v(12.07, 161.8) * mm, "end": v(12.07, 161.77) * mm});
            skLineSegment(sketch, "E2996", {"start": v(12.07, 161.77) * mm, "end": v(12, 161.71) * mm});
            skLineSegment(sketch, "E2997", {"start": v(12, 161.71) * mm, "end": v(11.87, 161.8) * mm});
            skLineSegment(sketch, "E2998", {"start": v(11.87, 161.8) * mm, "end": v(11.84, 161.84) * mm});
            skLineSegment(sketch, "E2999", {"start": v(11.84, 161.84) * mm, "end": v(11.8, 161.9) * mm});
            skLineSegment(sketch, "E3000", {"start": v(11.8, 161.9) * mm, "end": v(11.52, 162.53) * mm});
            skLineSegment(sketch, "E3001", {"start": v(11.52, 162.53) * mm, "end": v(11.51, 162.61) * mm});
            skLineSegment(sketch, "E3002", {"start": v(11.51, 162.61) * mm, "end": v(11.51, 162.73) * mm});
            skLineSegment(sketch, "E3003", {"start": v(11.51, 162.73) * mm, "end": v(11.51, 162.83) * mm});
            skLineSegment(sketch, "E3004", {"start": v(11.51, 162.83) * mm, "end": v(11.62, 163.22) * mm});
            skLineSegment(sketch, "E3005", {"start": v(11.62, 163.22) * mm, "end": v(11.78, 163.48) * mm});
            skLineSegment(sketch, "E3006", {"start": v(11.78, 163.48) * mm, "end": v(11.82, 163.52) * mm});
            skLineSegment(sketch, "E3007", {"start": v(11.82, 163.52) * mm, "end": v(11.73, 163.57) * mm});
            skLineSegment(sketch, "E3008", {"start": v(11.73, 163.57) * mm, "end": v(11.45, 163.76) * mm});
            skLineSegment(sketch, "E3009", {"start": v(11.45, 163.76) * mm, "end": v(11.16, 164.06) * mm});
            skLineSegment(sketch, "E3010", {"start": v(11.16, 164.06) * mm, "end": v(11.08, 164.16) * mm});
            skLineSegment(sketch, "E3011", {"start": v(11.08, 164.16) * mm, "end": v(10.96, 164.3) * mm});
            skLineSegment(sketch, "E3012", {"start": v(10.96, 164.3) * mm, "end": v(10.28, 164.74) * mm});
            skLineSegment(sketch, "E3013", {"start": v(10.28, 164.74) * mm, "end": v(9.56, 164.9) * mm});
            skLineSegment(sketch, "E3014", {"start": v(9.56, 164.9) * mm, "end": v(9.43, 164.9) * mm});
            skLineSegment(sketch, "E3015", {"start": v(9.43, 164.9) * mm, "end": v(9.27, 164.88) * mm});
            skLineSegment(sketch, "E3016", {"start": v(9.27, 164.88) * mm, "end": v(8.78, 164.99) * mm});
            skLineSegment(sketch, "E3017", {"start": v(8.78, 164.99) * mm, "end": v(8.29, 165.28) * mm});
            skLineSegment(sketch, "E3018", {"start": v(8.29, 165.28) * mm, "end": v(7.9, 165.68) * mm});
            skLineSegment(sketch, "E3019", {"start": v(7.9, 165.68) * mm, "end": v(7.69, 165.98) * mm});
            skLineSegment(sketch, "E3020", {"start": v(7.69, 165.98) * mm, "end": v(7.62, 166.08) * mm});
            skLineSegment(sketch, "E3021", {"start": v(7.62, 166.08) * mm, "end": v(7.58, 166.13) * mm});
            skLineSegment(sketch, "E3022", {"start": v(7.58, 166.13) * mm, "end": v(7.38, 166.27) * mm});
            skLineSegment(sketch, "E3023", {"start": v(7.38, 166.27) * mm, "end": v(6.93, 166.48) * mm});
            skLineSegment(sketch, "E3024", {"start": v(6.93, 166.48) * mm, "end": v(6.36, 166.64) * mm});
            skLineSegment(sketch, "E3025", {"start": v(6.36, 166.64) * mm, "end": v(5.89, 166.7) * mm});
            skLineSegment(sketch, "E3026", {"start": v(5.89, 166.7) * mm, "end": v(5.73, 166.68) * mm});
            skLineSegment(sketch, "E3027", {"start": v(5.73, 166.68) * mm, "end": v(5.57, 166.68) * mm});
            skLineSegment(sketch, "E3028", {"start": v(5.57, 166.68) * mm, "end": v(4.97, 166.65) * mm});
            skLineSegment(sketch, "E3029", {"start": v(4.97, 166.65) * mm, "end": v(4.62, 166.6) * mm});
            skLineSegment(sketch, "E3030", {"start": v(4.62, 166.6) * mm, "end": v(4.59, 166.59) * mm});
            skLineSegment(sketch, "E3031", {"start": v(4.59, 166.59) * mm, "end": v(4.5, 166.6) * mm});
            skLineSegment(sketch, "E3032", {"start": v(4.5, 166.6) * mm, "end": v(4.48, 166.6) * mm});
            skLineSegment(sketch, "E3033", {"start": v(4.48, 166.6) * mm, "end": v(4.47, 166.58) * mm});
            skLineSegment(sketch, "E3034", {"start": v(4.47, 166.58) * mm, "end": v(4.47, 166.46) * mm});
            skLineSegment(sketch, "E3035", {"start": v(4.47, 166.46) * mm, "end": v(4.53, 166.22) * mm});
            skLineSegment(sketch, "E3036", {"start": v(4.53, 166.22) * mm, "end": v(4.67, 165.92) * mm});
            skLineSegment(sketch, "E3037", {"start": v(4.67, 165.92) * mm, "end": v(4.73, 165.82) * mm});
            skLineSegment(sketch, "E3038", {"start": v(4.73, 165.82) * mm, "end": v(4.75, 165.76) * mm});
            skLineSegment(sketch, "E3039", {"start": v(4.75, 165.76) * mm, "end": v(4.9, 165.59) * mm});
            skLineSegment(sketch, "E3040", {"start": v(4.9, 165.59) * mm, "end": v(5.15, 165.36) * mm});
            skLineSegment(sketch, "E3041", {"start": v(5.15, 165.36) * mm, "end": v(5.35, 165.05) * mm});
            skLineSegment(sketch, "E3042", {"start": v(5.35, 165.05) * mm, "end": v(5.42, 164.7) * mm});
            skLineSegment(sketch, "E3043", {"start": v(5.42, 164.7) * mm, "end": v(5.4, 164.58) * mm});
            skLineSegment(sketch, "E3044", {"start": v(5.4, 164.58) * mm, "end": v(5.4, 164.4) * mm});
            skLineSegment(sketch, "E3045", {"start": v(5.4, 164.4) * mm, "end": v(5.26, 163.56) * mm});
            skLineSegment(sketch, "E3046", {"start": v(5.26, 163.56) * mm, "end": v(5.36, 162.8) * mm});
            skLineSegment(sketch, "E3047", {"start": v(5.36, 162.8) * mm, "end": v(5.47, 162.65) * mm});
            skLineSegment(sketch, "E3048", {"start": v(5.47, 162.65) * mm, "end": v(5.48, 162.64) * mm});
            skLineSegment(sketch, "E3049", {"start": v(5.48, 162.64) * mm, "end": v(5.54, 162.55) * mm});
            skLineSegment(sketch, "E3050", {"start": v(5.54, 162.55) * mm, "end": v(5.54, 162.54) * mm});
            skLineSegment(sketch, "E3051", {"start": v(5.54, 162.54) * mm, "end": v(5.59, 162.46) * mm});
            skLineSegment(sketch, "E3052", {"start": v(5.59, 162.46) * mm, "end": v(5.85, 161.8) * mm});
            skLineSegment(sketch, "E3053", {"start": v(5.85, 161.8) * mm, "end": v(5.98, 161) * mm});
            skLineSegment(sketch, "E3054", {"start": v(5.98, 161) * mm, "end": v(5.95, 160.85) * mm});
            skLineSegment(sketch, "E3055", {"start": v(5.95, 160.85) * mm, "end": v(5.88, 160.47) * mm});
            skLineSegment(sketch, "E3056", {"start": v(5.88, 160.47) * mm, "end": v(5.66, 159.34) * mm});
            skLineSegment(sketch, "E3057", {"start": v(5.66, 159.34) * mm, "end": v(5.28, 157.68) * mm});
            skLineSegment(sketch, "E3058", {"start": v(5.28, 157.68) * mm, "end": v(4.82, 156.12) * mm});
            skLineSegment(sketch, "E3059", {"start": v(4.82, 156.12) * mm, "end": v(4.47, 155.2) * mm});
            skLineSegment(sketch, "E3060", {"start": v(4.47, 155.2) * mm, "end": v(4.3, 154.92) * mm});
            skLineSegment(sketch, "E3061", {"start": v(4.3, 154.92) * mm, "end": v(4.27, 154.86) * mm});
            skLineSegment(sketch, "E3062", {"start": v(4.27, 154.86) * mm, "end": v(4.12, 154.72) * mm});
            skLineSegment(sketch, "E3063", {"start": v(4.12, 154.72) * mm, "end": v(4.08, 154.78) * mm});
            skLineSegment(sketch, "E3064", {"start": v(4.08, 154.78) * mm, "end": v(4, 155.44) * mm});
            skLineSegment(sketch, "E3065", {"start": v(4, 155.44) * mm, "end": v(3.72, 157.2) * mm});
            skLineSegment(sketch, "E3066", {"start": v(3.72, 157.2) * mm, "end": v(3.08, 159.72) * mm});
            skLineSegment(sketch, "E3067", {"start": v(3.08, 159.72) * mm, "end": v(2.3, 161.95) * mm});
            skLineSegment(sketch, "E3068", {"start": v(2.3, 161.95) * mm, "end": v(1.97, 162.66) * mm});
            skLineSegment(sketch, "E3069", {"start": v(1.97, 162.66) * mm, "end": v(1.72, 163.2) * mm});
            skLineSegment(sketch, "E3070", {"start": v(1.72, 163.2) * mm, "end": v(0.28, 165.84) * mm});
            skLineSegment(sketch, "E3071", {"start": v(0.28, 165.84) * mm, "end": v(-1.4, 168.26) * mm});
            skLineSegment(sketch, "E3072", {"start": v(-1.4, 168.26) * mm, "end": v(-1.78, 168.7) * mm});
            skLineSegment(sketch, "E3073", {"start": v(-1.78, 168.7) * mm, "end": v(-2.02, 168.98) * mm});
            skLineSegment(sketch, "E3074", {"start": v(-2.02, 168.98) * mm, "end": v(-2.76, 169.85) * mm});
            skLineSegment(sketch, "E3075", {"start": v(-2.76, 169.85) * mm, "end": v(-3.5, 170.7) * mm});
            skLineSegment(sketch, "E3076", {"start": v(-3.5, 170.7) * mm, "end": v(-3.97, 171.18) * mm});
            skLineSegment(sketch, "E3077", {"start": v(-3.97, 171.18) * mm, "end": v(-4.17, 171.29) * mm});
            skLineSegment(sketch, "E3078", {"start": v(-4.17, 171.29) * mm, "end": v(-4.18, 171.28) * mm});
            skLineSegment(sketch, "E3079", {"start": v(-4.18, 171.28) * mm, "end": v(-4.21, 171.25) * mm});
            skLineSegment(sketch, "E3080", {"start": v(-4.21, 171.25) * mm, "end": v(-4.2, 171) * mm});
            skLineSegment(sketch, "E3081", {"start": v(-4.2, 171) * mm, "end": v(-4.23, 170.45) * mm});
            skLineSegment(sketch, "E3082", {"start": v(-4.23, 170.45) * mm, "end": v(-4.27, 170.27) * mm});
            skLineSegment(sketch, "E3083", {"start": v(-4.27, 170.27) * mm, "end": v(-4.31, 170.1) * mm});
            skLineSegment(sketch, "E3084", {"start": v(-4.31, 170.1) * mm, "end": v(-4.72, 169.54) * mm});
            skLineSegment(sketch, "E3085", {"start": v(-4.72, 169.54) * mm, "end": v(-5.1, 169.27) * mm});
            skLineSegment(sketch, "E3086", {"start": v(-5.1, 169.27) * mm, "end": v(-5.13, 169.24) * mm});
            skLineSegment(sketch, "E3087", {"start": v(-5.13, 169.24) * mm, "end": v(-4.9, 169.12) * mm});
            skLineSegment(sketch, "E3088", {"start": v(-4.9, 169.12) * mm, "end": v(-4.3, 168.98) * mm});
            skLineSegment(sketch, "E3089", {"start": v(-4.3, 168.98) * mm, "end": v(-4.16, 168.93) * mm});
            skLineSegment(sketch, "E3090", {"start": v(-4.16, 168.93) * mm, "end": v(-4.07, 168.9) * mm});
            skLineSegment(sketch, "E3091", {"start": v(-4.07, 168.9) * mm, "end": v(-3.8, 168.75) * mm});
            skLineSegment(sketch, "E3092", {"start": v(-3.8, 168.75) * mm, "end": v(-3.57, 168.6) * mm});
            skLineSegment(sketch, "E3093", {"start": v(-3.57, 168.6) * mm, "end": v(-3.55, 168.49) * mm});
            skLineSegment(sketch, "E3094", {"start": v(-3.55, 168.49) * mm, "end": v(-3.7, 168.48) * mm});
            skLineSegment(sketch, "E3095", {"start": v(-3.7, 168.48) * mm, "end": v(-3.76, 168.49) * mm});
            skLineSegment(sketch, "E3096", {"start": v(-3.76, 168.49) * mm, "end": v(-3.9, 168.5) * mm});
            skLineSegment(sketch, "E3097", {"start": v(-3.9, 168.5) * mm, "end": v(-4.36, 168.55) * mm});
            skLineSegment(sketch, "E3098", {"start": v(-4.36, 168.55) * mm, "end": v(-5, 168.58) * mm});
            skLineSegment(sketch, "E3099", {"start": v(-5, 168.58) * mm, "end": v(-5.5, 168.57) * mm});
            skLineSegment(sketch, "E3100", {"start": v(-5.5, 168.57) * mm, "end": v(-5.66, 168.5) * mm});
            skLineSegment(sketch, "E3101", {"start": v(-5.66, 168.5) * mm, "end": v(-5.64, 168.48) * mm});
            skLineSegment(sketch, "E3102", {"start": v(-5.64, 168.48) * mm, "end": v(-5.45, 168.4) * mm});
            skLineSegment(sketch, "E3103", {"start": v(-5.45, 168.4) * mm, "end": v(-5.02, 168.22) * mm});
            skLineSegment(sketch, "E3104", {"start": v(-5.02, 168.22) * mm, "end": v(-4.48, 167.98) * mm});
            skLineSegment(sketch, "E3105", {"start": v(-4.48, 167.98) * mm, "end": v(-4.06, 167.74) * mm});
            skLineSegment(sketch, "E3106", {"start": v(-4.06, 167.74) * mm, "end": v(-3.92, 167.65) * mm});
            skLineSegment(sketch, "E3107", {"start": v(-3.92, 167.65) * mm, "end": v(-3.84, 167.6) * mm});
            skLineSegment(sketch, "E3108", {"start": v(-3.84, 167.6) * mm, "end": v(-3.59, 167.4) * mm});
            skLineSegment(sketch, "E3109", {"start": v(-3.59, 167.4) * mm, "end": v(-3.34, 167.13) * mm});
            skLineSegment(sketch, "E3110", {"start": v(-3.34, 167.13) * mm, "end": v(-3.29, 166.96) * mm});
            skLineSegment(sketch, "E3111", {"start": v(-3.29, 166.96) * mm, "end": v(-3.47, 166.93) * mm});
            skLineSegment(sketch, "E3112", {"start": v(-3.47, 166.93) * mm, "end": v(-3.52, 166.94) * mm});
            skLineSegment(sketch, "E3113", {"start": v(-3.52, 166.94) * mm, "end": v(-3.78, 167) * mm});
            skLineSegment(sketch, "E3114", {"start": v(-3.78, 167) * mm, "end": v(-6.44, 167.5) * mm});
            skLineSegment(sketch, "E3115", {"start": v(-6.44, 167.5) * mm, "end": v(-6.72, 167.54) * mm});
            skLineSegment(sketch, "E3116", {"start": v(-6.72, 167.54) * mm, "end": v(-6.95, 167.56) * mm});
            skLineSegment(sketch, "E3117", {"start": v(-6.95, 167.56) * mm, "end": v(-7.66, 167.52) * mm});
            skLineSegment(sketch, "E3118", {"start": v(-7.66, 167.52) * mm, "end": v(-8.44, 167.35) * mm});
            skLineSegment(sketch, "E3119", {"start": v(-8.44, 167.35) * mm, "end": v(-8.93, 167.13) * mm});
            skLineSegment(sketch, "E3120", {"start": v(-8.93, 167.13) * mm, "end": v(-8.98, 166.98) * mm});
            skLineSegment(sketch, "E3121", {"start": v(-8.98, 166.98) * mm, "end": v(-8.98, 166.98) * mm});
            skLineSegment(sketch, "E3122", {"start": v(-8.98, 166.98) * mm, "end": v(-8.94, 166.96) * mm});
            skLineSegment(sketch, "E3123", {"start": v(-8.94, 166.96) * mm, "end": v(-8.76, 166.9) * mm});
            skLineSegment(sketch, "E3124", {"start": v(-8.76, 166.9) * mm, "end": v(-8.36, 166.76) * mm});
            skLineSegment(sketch, "E3125", {"start": v(-8.36, 166.76) * mm, "end": v(-7.84, 166.45) * mm});
            skLineSegment(sketch, "E3126", {"start": v(-7.84, 166.45) * mm, "end": v(-7.36, 166.04) * mm});
            skLineSegment(sketch, "E3127", {"start": v(-7.36, 166.04) * mm, "end": v(-7.22, 165.9) * mm});
            skLineSegment(sketch, "E3128", {"start": v(-7.22, 165.9) * mm, "end": v(-7.25, 165.87) * mm});
            skLineSegment(sketch, "E3129", {"start": v(-7.25, 165.87) * mm, "end": v(-7.53, 165.9) * mm});
            skLineSegment(sketch, "E3130", {"start": v(-7.53, 165.9) * mm, "end": v(-8.07, 166.12) * mm});
            skLineSegment(sketch, "E3131", {"start": v(-8.07, 166.12) * mm, "end": v(-8.23, 166.2) * mm});
            skLineSegment(sketch, "E3132", {"start": v(-8.23, 166.2) * mm, "end": v(-8.37, 166.28) * mm});
            skLineSegment(sketch, "E3133", {"start": v(-8.37, 166.28) * mm, "end": v(-8.8, 166.46) * mm});
            skLineSegment(sketch, "E3134", {"start": v(-8.8, 166.46) * mm, "end": v(-9.14, 166.52) * mm});
            skLineSegment(sketch, "E3135", {"start": v(-9.14, 166.52) * mm, "end": v(-9.27, 166.47) * mm});
            skLineSegment(sketch, "E3136", {"start": v(-9.27, 166.47) * mm, "end": v(-9.25, 166.39) * mm});
            skLineSegment(sketch, "E3137", {"start": v(-9.25, 166.39) * mm, "end": v(-9.23, 166.37) * mm});
            skLineSegment(sketch, "E3138", {"start": v(-9.23, 166.37) * mm, "end": v(-9.18, 166.35) * mm});
            skLineSegment(sketch, "E3139", {"start": v(-9.18, 166.35) * mm, "end": v(-8.77, 166.13) * mm});
            skLineSegment(sketch, "E3140", {"start": v(-8.77, 166.13) * mm, "end": v(-8.32, 165.85) * mm});
            skLineSegment(sketch, "E3141", {"start": v(-8.32, 165.85) * mm, "end": v(-8.25, 165.8) * mm});
            skLineSegment(sketch, "E3142", {"start": v(-8.25, 165.8) * mm, "end": v(-8.11, 165.67) * mm});
            skLineSegment(sketch, "E3143", {"start": v(-8.11, 165.67) * mm, "end": v(-7.72, 165.27) * mm});
            skLineSegment(sketch, "E3144", {"start": v(-7.72, 165.27) * mm, "end": v(-7.36, 164.8) * mm});
            skLineSegment(sketch, "E3145", {"start": v(-7.36, 164.8) * mm, "end": v(-7.16, 164.47) * mm});
            skLineSegment(sketch, "E3146", {"start": v(-7.16, 164.47) * mm, "end": v(-7.1, 164.35) * mm});
            skLineSegment(sketch, "E3147", {"start": v(-7.1, 164.35) * mm, "end": v(-7.07, 164.3) * mm});
            skLineSegment(sketch, "E3148", {"start": v(-7.07, 164.3) * mm, "end": v(-6.84, 163.84) * mm});
            skLineSegment(sketch, "E3149", {"start": v(-6.84, 163.84) * mm, "end": v(-6.6, 163.26) * mm});
            skLineSegment(sketch, "E3150", {"start": v(-6.6, 163.26) * mm, "end": v(-6.57, 163.16) * mm});
            skLineSegment(sketch, "E3151", {"start": v(-6.57, 163.16) * mm, "end": v(-6.53, 163.04) * mm});
            skLineSegment(sketch, "E3152", {"start": v(-6.53, 163.04) * mm, "end": v(-6.44, 162.7) * mm});
            skLineSegment(sketch, "E3153", {"start": v(-6.44, 162.7) * mm, "end": v(-6.32, 162.2) * mm});
            skLineSegment(sketch, "E3154", {"start": v(-6.32, 162.2) * mm, "end": v(-6.25, 161.85) * mm});
            skLineSegment(sketch, "E3155", {"start": v(-6.25, 161.85) * mm, "end": v(-6.27, 161.76) * mm});
            skLineSegment(sketch, "E3156", {"start": v(-6.27, 161.76) * mm, "end": v(-6.32, 161.8) * mm});
            skLineSegment(sketch, "E3157", {"start": v(-6.32, 161.8) * mm, "end": v(-6.43, 161.96) * mm});
            skLineSegment(sketch, "E3158", {"start": v(-6.43, 161.96) * mm, "end": v(-6.67, 162.33) * mm});
            skLineSegment(sketch, "E3159", {"start": v(-6.67, 162.33) * mm, "end": v(-6.98, 162.82) * mm});
            skLineSegment(sketch, "E3160", {"start": v(-6.98, 162.82) * mm, "end": v(-7.33, 163.36) * mm});
            skLineSegment(sketch, "E3161", {"start": v(-7.33, 163.36) * mm, "end": v(-7.68, 163.89) * mm});
            skLineSegment(sketch, "E3162", {"start": v(-7.68, 163.89) * mm, "end": v(-8.03, 164.34) * mm});
            skLineSegment(sketch, "E3163", {"start": v(-8.03, 164.34) * mm, "end": v(-8.33, 164.65) * mm});
            skLineSegment(sketch, "E3164", {"start": v(-8.33, 164.65) * mm, "end": v(-8.51, 164.76) * mm});
            skLineSegment(sketch, "E3165", {"start": v(-8.51, 164.76) * mm, "end": v(-8.57, 164.75) * mm});
            skLineSegment(sketch, "E3166", {"start": v(-8.57, 164.75) * mm, "end": v(-8.6, 164.75) * mm});
            skLineSegment(sketch, "E3167", {"start": v(-8.6, 164.75) * mm, "end": v(-8.68, 164.57) * mm});
            skLineSegment(sketch, "E3168", {"start": v(-8.68, 164.57) * mm, "end": v(-8.67, 164.18) * mm});
            skLineSegment(sketch, "E3169", {"start": v(-8.67, 164.18) * mm, "end": v(-8.56, 163.73) * mm});
            skLineSegment(sketch, "E3170", {"start": v(-8.56, 163.73) * mm, "end": v(-8.46, 163.44) * mm});
            skLineSegment(sketch, "E3171", {"start": v(-8.46, 163.44) * mm, "end": v(-8.4, 163.35) * mm});
            skLineSegment(sketch, "E3172", {"start": v(-8.4, 163.35) * mm, "end": v(-8.34, 163.23) * mm});
            skLineSegment(sketch, "E3173", {"start": v(-8.34, 163.23) * mm, "end": v(-8.06, 162.9) * mm});
            skLineSegment(sketch, "E3174", {"start": v(-8.06, 162.9) * mm, "end": v(-7.52, 162.33) * mm});
            skLineSegment(sketch, "E3175", {"start": v(-7.52, 162.33) * mm, "end": v(-6.96, 161.76) * mm});
            skLineSegment(sketch, "E3176", {"start": v(-6.96, 161.76) * mm, "end": v(-6.64, 161.44) * mm});
            skLineSegment(sketch, "E3177", {"start": v(-6.64, 161.44) * mm, "end": v(-6.54, 161.32) * mm});
            skLineSegment(sketch, "E3178", {"start": v(-6.54, 161.32) * mm, "end": v(-6.24, 160.96) * mm});
            skLineSegment(sketch, "E3179", {"start": v(-6.24, 160.96) * mm, "end": v(-5.07, 159.1) * mm});
            skLineSegment(sketch, "E3180", {"start": v(-5.07, 159.1) * mm, "end": v(-4.09, 157.2) * mm});
            skLineSegment(sketch, "E3181", {"start": v(-4.09, 157.2) * mm, "end": v(-3.87, 156.84) * mm});
            skLineSegment(sketch, "E3182", {"start": v(-3.87, 156.84) * mm, "end": v(-3.84, 156.78) * mm});
            skLineSegment(sketch, "E3183", {"start": v(-3.84, 156.78) * mm, "end": v(-3.62, 156.2) * mm});
            skLineSegment(sketch, "E3184", {"start": v(-3.62, 156.2) * mm, "end": v(-3.6, 156.15) * mm});
            skLineSegment(sketch, "E3185", {"start": v(-3.6, 156.15) * mm, "end": v(-3.6, 156.12) * mm});
            skLineSegment(sketch, "E3186", {"start": v(-3.6, 156.12) * mm, "end": v(-3.48, 155.8) * mm});
            skLineSegment(sketch, "E3187", {"start": v(-3.48, 155.8) * mm, "end": v(-3.46, 155.78) * mm});
            skLineSegment(sketch, "E3188", {"start": v(-3.46, 155.78) * mm, "end": v(-3.45, 155.75) * mm});
            skLineSegment(sketch, "E3189", {"start": v(-3.45, 155.75) * mm, "end": v(-3.24, 155.5) * mm});
            skLineSegment(sketch, "E3190", {"start": v(-3.24, 155.5) * mm, "end": v(-3.2, 155.48) * mm});
            skLineSegment(sketch, "E3191", {"start": v(-3.2, 155.48) * mm, "end": v(-3.2, 155.48) * mm});
            skLineSegment(sketch, "E3192", {"start": v(-3.2, 155.48) * mm, "end": v(-3.13, 155.42) * mm});
            skLineSegment(sketch, "E3193", {"start": v(-3.13, 155.42) * mm, "end": v(-3.12, 155.42) * mm});
            skLineSegment(sketch, "E3194", {"start": v(-3.12, 155.42) * mm, "end": v(-3.1, 155.41) * mm});
            skLineSegment(sketch, "E3195", {"start": v(-3.1, 155.41) * mm, "end": v(-3, 155.37) * mm});
            skLineSegment(sketch, "E3196", {"start": v(-3, 155.37) * mm, "end": v(-2.99, 155.37) * mm});
            skLineSegment(sketch, "E3197", {"start": v(-2.99, 155.37) * mm, "end": v(-2.95, 155.35) * mm});
            skLineSegment(sketch, "E3198", {"start": v(-2.95, 155.35) * mm, "end": v(-2.61, 155.17) * mm});
            skLineSegment(sketch, "E3199", {"start": v(-2.61, 155.17) * mm, "end": v(-2.58, 155.13) * mm});
            skLineSegment(sketch, "E3200", {"start": v(-2.58, 155.13) * mm, "end": v(-2.56, 155.12) * mm});
            skLineSegment(sketch, "E3201", {"start": v(-2.56, 155.12) * mm, "end": v(-2.45, 154.99) * mm});
            skLineSegment(sketch, "E3202", {"start": v(-2.45, 154.99) * mm, "end": v(-2.36, 154.88) * mm});
            skLineSegment(sketch, "E3203", {"start": v(-2.36, 154.88) * mm, "end": v(-2.36, 154.87) * mm});
            skLineSegment(sketch, "E3204", {"start": v(-2.36, 154.87) * mm, "end": v(-2.3, 154.82) * mm});
            skLineSegment(sketch, "E3205", {"start": v(-2.3, 154.82) * mm, "end": v(-2.3, 154.8) * mm});
            skLineSegment(sketch, "E3206", {"start": v(-2.3, 154.8) * mm, "end": v(-2.2, 154.72) * mm});
            skLineSegment(sketch, "E3207", {"start": v(-2.2, 154.72) * mm, "end": v(-1.77, 154.44) * mm});
            skLineSegment(sketch, "E3208", {"start": v(-1.77, 154.44) * mm, "end": v(-1.25, 154.28) * mm});
            skLineSegment(sketch, "E3209", {"start": v(-1.25, 154.28) * mm, "end": v(-1.1, 154.24) * mm});
            skLineSegment(sketch, "E3210", {"start": v(-1.1, 154.24) * mm, "end": v(-1.06, 154.23) * mm});
            skLineSegment(sketch, "E3211", {"start": v(-1.06, 154.23) * mm, "end": v(-0.5, 154.05) * mm});
            skLineSegment(sketch, "E3212", {"start": v(-0.5, 154.05) * mm, "end": v(-0.46, 154.03) * mm});
            skLineSegment(sketch, "E3213", {"start": v(-0.46, 154.03) * mm, "end": v(-0.35, 153.99) * mm});
            skLineSegment(sketch, "E3214", {"start": v(-0.35, 153.99) * mm, "end": v(-0.03, 153.7) * mm});
            skLineSegment(sketch, "E3215", {"start": v(-0.03, 153.7) * mm, "end": v(-0.04, 153.46) * mm});
            skLineSegment(sketch, "E3216", {"start": v(-0.04, 153.46) * mm, "end": v(-0.06, 153.46) * mm});
            skLineSegment(sketch, "E3217", {"start": v(-0.06, 153.46) * mm, "end": v(-0.07, 153.45) * mm});
            skLineSegment(sketch, "E3218", {"start": v(-0.07, 153.45) * mm, "end": v(-0.24, 153.45) * mm});
            skLineSegment(sketch, "E3219", {"start": v(-0.24, 153.45) * mm, "end": v(-0.27, 153.46) * mm});
            skLineSegment(sketch, "E3220", {"start": v(-0.27, 153.46) * mm, "end": v(-0.39, 153.48) * mm});
            skLineSegment(sketch, "E3221", {"start": v(-0.39, 153.48) * mm, "end": v(-1.1, 153.57) * mm});
            skLineSegment(sketch, "E3222", {"start": v(-1.1, 153.57) * mm, "end": v(-2.08, 153.58) * mm});
            skLineSegment(sketch, "E3223", {"start": v(-2.08, 153.58) * mm, "end": v(-2.32, 153.56) * mm});
            skLineSegment(sketch, "E3224", {"start": v(-2.32, 153.56) * mm, "end": v(-2.4, 153.56) * mm});
            skLineSegment(sketch, "E3225", {"start": v(-2.4, 153.56) * mm, "end": v(-3.4, 153.43) * mm});
            skLineSegment(sketch, "E3226", {"start": v(-3.4, 153.43) * mm, "end": v(-3.5, 153.42) * mm});
            skLineSegment(sketch, "E3227", {"start": v(-3.5, 153.42) * mm, "end": v(-3.57, 153.4) * mm});
            skLineSegment(sketch, "E3228", {"start": v(-3.57, 153.4) * mm, "end": v(-4.11, 153.29) * mm});
            skLineSegment(sketch, "E3229", {"start": v(-4.11, 153.29) * mm, "end": v(-4.16, 153.28) * mm});
            skLineSegment(sketch, "E3230", {"start": v(-4.16, 153.28) * mm, "end": v(-4.23, 153.27) * mm});
            skLineSegment(sketch, "E3231", {"start": v(-4.23, 153.27) * mm, "end": v(-4.77, 153.23) * mm});
            skLineSegment(sketch, "E3232", {"start": v(-4.77, 153.23) * mm, "end": v(-4.82, 153.23) * mm});
            skLineSegment(sketch, "E3233", {"start": v(-4.82, 153.23) * mm, "end": v(-4.83, 153.24) * mm});
            skLineSegment(sketch, "E3234", {"start": v(-4.83, 153.24) * mm, "end": v(-5, 153.25) * mm});
            skLineSegment(sketch, "E3235", {"start": v(-5, 153.25) * mm, "end": v(-5.68, 153.47) * mm});
            skLineSegment(sketch, "E3236", {"start": v(-5.68, 153.47) * mm, "end": v(-6.28, 153.86) * mm});
            skLineSegment(sketch, "E3237", {"start": v(-6.28, 153.86) * mm, "end": v(-6.4, 153.97) * mm});
            skLineSegment(sketch, "E3238", {"start": v(-6.4, 153.97) * mm, "end": v(-6.42, 153.99) * mm});
            skLineSegment(sketch, "E3239", {"start": v(-6.42, 153.99) * mm, "end": v(-6.6, 154.15) * mm});
            skLineSegment(sketch, "E3240", {"start": v(-6.6, 154.15) * mm, "end": v(-6.62, 154.17) * mm});
            skLineSegment(sketch, "E3241", {"start": v(-6.62, 154.17) * mm, "end": v(-6.68, 154.22) * mm});
            skLineSegment(sketch, "E3242", {"start": v(-6.68, 154.22) * mm, "end": v(-6.83, 154.42) * mm});
            skLineSegment(sketch, "E3243", {"start": v(-6.83, 154.42) * mm, "end": v(-6.6, 154.41) * mm});
            skLineSegment(sketch, "E3244", {"start": v(-6.6, 154.41) * mm, "end": v(-6.09, 154.25) * mm});
            skLineSegment(sketch, "E3245", {"start": v(-6.09, 154.25) * mm, "end": v(-5.6, 154.1) * mm});
            skLineSegment(sketch, "E3246", {"start": v(-5.6, 154.1) * mm, "end": v(-5.43, 154.05) * mm});
            skLineSegment(sketch, "E3247", {"start": v(-5.43, 154.05) * mm, "end": v(-5.38, 154.04) * mm});
            skLineSegment(sketch, "E3248", {"start": v(-5.38, 154.04) * mm, "end": v(-4.87, 153.96) * mm});
            skLineSegment(sketch, "E3249", {"start": v(-4.87, 153.96) * mm, "end": v(-4.7, 153.96) * mm});
            skLineSegment(sketch, "E3250", {"start": v(-4.7, 153.96) * mm, "end": v(-4.06, 153.96) * mm});
            skLineSegment(sketch, "E3251", {"start": v(-4.06, 153.96) * mm, "end": v(-4.02, 153.97) * mm});
            skLineSegment(sketch, "E3252", {"start": v(-4.02, 153.97) * mm, "end": v(-3.78, 153.97) * mm});
            skLineSegment(sketch, "E3253", {"start": v(-3.78, 153.97) * mm, "end": v(-3.14, 154.05) * mm});
            skLineSegment(sketch, "E3254", {"start": v(-3.14, 154.05) * mm, "end": v(-3.06, 154.05) * mm});
            skLineSegment(sketch, "E3255", {"start": v(-3.06, 154.05) * mm, "end": v(-2.85, 154.05) * mm});
            skLineSegment(sketch, "E3256", {"start": v(-2.85, 154.05) * mm, "end": v(-2.8, 154.06) * mm});
            skLineSegment(sketch, "E3257", {"start": v(-2.8, 154.06) * mm, "end": v(-2.55, 154.07) * mm});
            skLineSegment(sketch, "E3258", {"start": v(-2.55, 154.07) * mm, "end": v(-2.47, 154.07) * mm});
            skLineSegment(sketch, "E3259", {"start": v(-2.47, 154.07) * mm, "end": v(-2.42, 154.07) * mm});
            skLineSegment(sketch, "E3260", {"start": v(-2.42, 154.07) * mm, "end": v(-2.25, 154.1) * mm});
            skLineSegment(sketch, "E3261", {"start": v(-2.25, 154.1) * mm, "end": v(-2.25, 154.17) * mm});
            skLineSegment(sketch, "E3262", {"start": v(-2.25, 154.17) * mm, "end": v(-2.26, 154.19) * mm});
            skLineSegment(sketch, "E3263", {"start": v(-2.26, 154.19) * mm, "end": v(-2.27, 154.2) * mm});
            skLineSegment(sketch, "E3264", {"start": v(-2.27, 154.2) * mm, "end": v(-2.55, 154.37) * mm});
            skLineSegment(sketch, "E3265", {"start": v(-2.55, 154.37) * mm, "end": v(-2.58, 154.38) * mm});
            skLineSegment(sketch, "E3266", {"start": v(-2.58, 154.38) * mm, "end": v(-2.6, 154.4) * mm});
            skLineSegment(sketch, "E3267", {"start": v(-2.6, 154.4) * mm, "end": v(-2.84, 154.52) * mm});
            skLineSegment(sketch, "E3268", {"start": v(-2.84, 154.52) * mm, "end": v(-2.86, 154.53) * mm});
            skLineSegment(sketch, "E3269", {"start": v(-2.86, 154.53) * mm, "end": v(-2.9, 154.54) * mm});
            skLineSegment(sketch, "E3270", {"start": v(-2.9, 154.54) * mm, "end": v(-3.2, 154.66) * mm});
            skLineSegment(sketch, "E3271", {"start": v(-3.2, 154.66) * mm, "end": v(-3.24, 154.67) * mm});
            skLineSegment(sketch, "E3272", {"start": v(-3.24, 154.67) * mm, "end": v(-3.3, 154.7) * mm});
            skLineSegment(sketch, "E3273", {"start": v(-3.3, 154.7) * mm, "end": v(-3.95, 154.86) * mm});
            skLineSegment(sketch, "E3274", {"start": v(-3.95, 154.86) * mm, "end": v(-4.03, 154.88) * mm});
            skLineSegment(sketch, "E3275", {"start": v(-4.03, 154.88) * mm, "end": v(-4.09, 154.88) * mm});
            skLineSegment(sketch, "E3276", {"start": v(-4.09, 154.88) * mm, "end": v(-4.23, 154.92) * mm});
            skLineSegment(sketch, "E3277", {"start": v(-4.23, 154.92) * mm, "end": v(-4.27, 154.92) * mm});
            skLineSegment(sketch, "E3278", {"start": v(-4.27, 154.92) * mm, "end": v(-4.46, 154.96) * mm});
            skLineSegment(sketch, "E3279", {"start": v(-4.46, 154.96) * mm, "end": v(-5.3, 155.23) * mm});
            skLineSegment(sketch, "E3280", {"start": v(-5.3, 155.23) * mm, "end": v(-6.03, 155.77) * mm});
            skLineSegment(sketch, "E3281", {"start": v(-6.03, 155.77) * mm, "end": v(-6.16, 155.95) * mm});
            skLineSegment(sketch, "E3282", {"start": v(-6.16, 155.95) * mm, "end": v(-6.18, 155.97) * mm});
            skLineSegment(sketch, "E3283", {"start": v(-6.18, 155.97) * mm, "end": v(-6.19, 156.08) * mm});
            skLineSegment(sketch, "E3284", {"start": v(-6.19, 156.08) * mm, "end": v(-5.95, 156.06) * mm});
            skLineSegment(sketch, "E3285", {"start": v(-5.95, 156.06) * mm, "end": v(-5.56, 155.96) * mm});
            skLineSegment(sketch, "E3286", {"start": v(-5.56, 155.96) * mm, "end": v(-5.24, 155.88) * mm});
            skLineSegment(sketch, "E3287", {"start": v(-5.24, 155.88) * mm, "end": v(-5.13, 155.87) * mm});
            skLineSegment(sketch, "E3288", {"start": v(-5.13, 155.87) * mm, "end": v(-5.12, 155.87) * mm});
            skLineSegment(sketch, "E3289", {"start": v(-5.12, 155.87) * mm, "end": v(-5.04, 155.86) * mm});
            skLineSegment(sketch, "E3290", {"start": v(-5.04, 155.86) * mm, "end": v(-5, 155.86) * mm});
            skLineSegment(sketch, "E3291", {"start": v(-5, 155.86) * mm, "end": v(-4.92, 155.86) * mm});
            skLineSegment(sketch, "E3292", {"start": v(-4.92, 155.86) * mm, "end": v(-4.66, 155.92) * mm});
            skLineSegment(sketch, "E3293", {"start": v(-4.66, 155.92) * mm, "end": v(-4.66, 156.13) * mm});
            skLineSegment(sketch, "E3294", {"start": v(-4.66, 156.13) * mm, "end": v(-4.7, 156.17) * mm});
            skLineSegment(sketch, "E3295", {"start": v(-4.7, 156.17) * mm, "end": v(-4.88, 156.45) * mm});
            skLineSegment(sketch, "E3296", {"start": v(-4.88, 156.45) * mm, "end": v(-5.56, 157.22) * mm});
            skLineSegment(sketch, "E3297", {"start": v(-5.56, 157.22) * mm, "end": v(-6.58, 158.16) * mm});
            skLineSegment(sketch, "E3298", {"start": v(-6.58, 158.16) * mm, "end": v(-7.81, 159.25) * mm});
            skLineSegment(sketch, "E3299", {"start": v(-7.81, 159.25) * mm, "end": v(-8.96, 160.36) * mm});
            skLineSegment(sketch, "E3300", {"start": v(-8.96, 160.36) * mm, "end": v(-9.32, 160.75) * mm});
            skLineSegment(sketch, "E3301", {"start": v(-9.32, 160.75) * mm, "end": v(-9.46, 160.9) * mm});
            skLineSegment(sketch, "E3302", {"start": v(-9.46, 160.9) * mm, "end": v(-10.23, 161.76) * mm});
            skLineSegment(sketch, "E3303", {"start": v(-10.23, 161.76) * mm, "end": v(-10.84, 162.64) * mm});
            skLineSegment(sketch, "E3304", {"start": v(-10.84, 162.64) * mm, "end": v(-10.9, 162.8) * mm});
            skLineSegment(sketch, "E3305", {"start": v(-10.9, 162.8) * mm, "end": v(-10.92, 162.87) * mm});
            skLineSegment(sketch, "E3306", {"start": v(-10.92, 162.87) * mm, "end": v(-11.09, 163.52) * mm});
            skLineSegment(sketch, "E3307", {"start": v(-11.09, 163.52) * mm, "end": v(-11.1, 163.59) * mm});
            skLineSegment(sketch, "E3308", {"start": v(-11.1, 163.59) * mm, "end": v(-11.12, 163.7) * mm});
            skLineSegment(sketch, "E3309", {"start": v(-11.12, 163.7) * mm, "end": v(-11.17, 164.27) * mm});
            skLineSegment(sketch, "E3310", {"start": v(-11.17, 164.27) * mm, "end": v(-11.15, 164.77) * mm});
            skLineSegment(sketch, "E3311", {"start": v(-11.15, 164.77) * mm, "end": v(-11.14, 164.85) * mm});
            skLineSegment(sketch, "E3312", {"start": v(-11.14, 164.85) * mm, "end": v(-11.1, 165.04) * mm});
            skLineSegment(sketch, "E3313", {"start": v(-11.1, 165.04) * mm, "end": v(-10.92, 165.6) * mm});
            skLineSegment(sketch, "E3314", {"start": v(-10.92, 165.6) * mm, "end": v(-10.67, 166.15) * mm});
            skLineSegment(sketch, "E3315", {"start": v(-10.67, 166.15) * mm, "end": v(-10.5, 166.48) * mm});
            skLineSegment(sketch, "E3316", {"start": v(-10.5, 166.48) * mm, "end": v(-10.53, 166.59) * mm});
            skLineSegment(sketch, "E3317", {"start": v(-10.53, 166.59) * mm, "end": v(-10.54, 166.59) * mm});
            skLineSegment(sketch, "E3318", {"start": v(-10.54, 166.59) * mm, "end": v(-10.72, 166.56) * mm});
            skLineSegment(sketch, "E3319", {"start": v(-10.72, 166.56) * mm, "end": v(-10.75, 166.55) * mm});
            skLineSegment(sketch, "E3320", {"start": v(-10.75, 166.55) * mm, "end": v(-10.79, 166.53) * mm});
            skLineSegment(sketch, "E3321", {"start": v(-10.79, 166.53) * mm, "end": v(-11.05, 166.33) * mm});
            skLineSegment(sketch, "E3322", {"start": v(-11.05, 166.33) * mm, "end": v(-11.38, 166.01) * mm});
            skLineSegment(sketch, "E3323", {"start": v(-11.38, 166.01) * mm, "end": v(-11.45, 165.93) * mm});
            skLineSegment(sketch, "E3324", {"start": v(-11.45, 165.93) * mm, "end": v(-11.47, 165.9) * mm});
            skLineSegment(sketch, "E3325", {"start": v(-11.47, 165.9) * mm, "end": v(-11.66, 165.66) * mm});
            skLineSegment(sketch, "E3326", {"start": v(-11.66, 165.66) * mm, "end": v(-11.69, 165.62) * mm});
            skLineSegment(sketch, "E3327", {"start": v(-11.69, 165.62) * mm, "end": v(-11.72, 165.58) * mm});
            skLineSegment(sketch, "E3328", {"start": v(-11.72, 165.58) * mm, "end": v(-11.95, 165) * mm});
            skLineSegment(sketch, "E3329", {"start": v(-11.95, 165) * mm, "end": v(-11.96, 164.9) * mm});
            skLineSegment(sketch, "E3330", {"start": v(-11.96, 164.9) * mm, "end": v(-11.98, 164.8) * mm});
            skLineSegment(sketch, "E3331", {"start": v(-11.98, 164.8) * mm, "end": v(-12.02, 163.73) * mm});
            skLineSegment(sketch, "E3332", {"start": v(-12.02, 163.73) * mm, "end": v(-12, 163.63) * mm});
            skLineSegment(sketch, "E3333", {"start": v(-12, 163.63) * mm, "end": v(-12, 163.35) * mm});
            skLineSegment(sketch, "E3334", {"start": v(-12, 163.35) * mm, "end": v(-11.92, 162.63) * mm});
            skLineSegment(sketch, "E3335", {"start": v(-11.92, 162.63) * mm, "end": v(-11.9, 162.53) * mm});
            skLineSegment(sketch, "E3336", {"start": v(-11.9, 162.53) * mm, "end": v(-11.83, 162.17) * mm});
            skLineSegment(sketch, "E3337", {"start": v(-11.83, 162.17) * mm, "end": v(-11.6, 161.1) * mm});
            skLineSegment(sketch, "E3338", {"start": v(-11.6, 161.1) * mm, "end": v(-11.29, 159.98) * mm});
            skLineSegment(sketch, "E3339", {"start": v(-11.29, 159.98) * mm, "end": v(-10.86, 158.88) * mm});
            skLineSegment(sketch, "E3340", {"start": v(-10.86, 158.88) * mm, "end": v(-10.4, 157.84) * mm});
            skLineSegment(sketch, "E3341", {"start": v(-10.4, 157.84) * mm, "end": v(-10.23, 157.5) * mm});
            skLineSegment(sketch, "E3342", {"start": v(-10.23, 157.5) * mm, "end": v(-10.04, 157.1) * mm});
            skLineSegment(sketch, "E3343", {"start": v(-10.04, 157.1) * mm, "end": v(-9.4, 155.93) * mm});
            skLineSegment(sketch, "E3344", {"start": v(-9.4, 155.93) * mm, "end": v(-8.42, 154.34) * mm});
            skLineSegment(sketch, "E3345", {"start": v(-8.42, 154.34) * mm, "end": v(-7.47, 152.96) * mm});
            skLineSegment(sketch, "E3346", {"start": v(-7.47, 152.96) * mm, "end": v(-6.91, 152.25) * mm});
            skLineSegment(sketch, "E3347", {"start": v(-6.91, 152.25) * mm, "end": v(-6.71, 152.04) * mm});
            skLineSegment(sketch, "E3348", {"start": v(-6.71, 152.04) * mm, "end": v(-6.69, 152.01) * mm});
            skLineSegment(sketch, "E3349", {"start": v(-6.69, 152.01) * mm, "end": v(-6.45, 151.77) * mm});
            skLineSegment(sketch, "E3350", {"start": v(-6.45, 151.77) * mm, "end": v(-6.43, 151.75) * mm});
            skLineSegment(sketch, "E3351", {"start": v(-6.43, 151.75) * mm, "end": v(-6.4, 151.73) * mm});
            skLineSegment(sketch, "E3352", {"start": v(-6.4, 151.73) * mm, "end": v(-6.23, 151.57) * mm});
            skLineSegment(sketch, "E3353", {"start": v(-6.23, 151.57) * mm, "end": v(-6.2, 151.56) * mm});
            skLineSegment(sketch, "E3354", {"start": v(-6.2, 151.56) * mm, "end": v(-6.15, 151.51) * mm});
            skLineSegment(sketch, "E3355", {"start": v(-6.15, 151.51) * mm, "end": v(-5.3, 151.05) * mm});
            skLineSegment(sketch, "E3356", {"start": v(-5.3, 151.05) * mm, "end": v(-5.2, 151) * mm});
            skLineSegment(sketch, "E3357", {"start": v(-5.2, 151) * mm, "end": v(-5.1, 150.96) * mm});
            skLineSegment(sketch, "E3358", {"start": v(-5.1, 150.96) * mm, "end": v(-3.86, 150.47) * mm});
            skLineSegment(sketch, "E3359", {"start": v(-3.86, 150.47) * mm, "end": v(-3.71, 150.41) * mm});
            skLineSegment(sketch, "E3360", {"start": v(-3.71, 150.41) * mm, "end": v(-3.6, 150.37) * mm});
            skLineSegment(sketch, "E3361", {"start": v(-3.6, 150.37) * mm, "end": v(-3.25, 150.25) * mm});
            skLineSegment(sketch, "E3362", {"start": v(-3.25, 150.25) * mm, "end": v(-2.68, 150.04) * mm});
            skLineSegment(sketch, "E3363", {"start": v(-2.68, 150.04) * mm, "end": v(-2.08, 149.82) * mm});
            skLineSegment(sketch, "E3364", {"start": v(-2.08, 149.82) * mm, "end": v(-1.47, 149.59) * mm});
            skLineSegment(sketch, "E3365", {"start": v(-1.47, 149.59) * mm, "end": v(-0.93, 149.38) * mm});
            skLineSegment(sketch, "E3366", {"start": v(-0.93, 149.38) * mm, "end": v(-0.5, 149.2) * mm});
            skLineSegment(sketch, "E3367", {"start": v(-0.5, 149.2) * mm, "end": v(-0.22, 149.09) * mm});
            skLineSegment(sketch, "E3368", {"start": v(-0.22, 149.09) * mm, "end": v(-0.15, 149.04) * mm});
            skLineSegment(sketch, "E3369", {"start": v(-0.15, 149.04) * mm, "end": v(-0.33, 149.04) * mm});
            skLineSegment(sketch, "E3370", {"start": v(-0.33, 149.04) * mm, "end": v(-0.85, 149.13) * mm});
            skLineSegment(sketch, "E3371", {"start": v(-0.85, 149.13) * mm, "end": v(-1.99, 149.35) * mm});
            skLineSegment(sketch, "E3372", {"start": v(-1.99, 149.35) * mm, "end": v(-3.16, 149.59) * mm});
            skLineSegment(sketch, "E3373", {"start": v(-3.16, 149.59) * mm, "end": v(-3.8, 149.72) * mm});
            skLineSegment(sketch, "E3374", {"start": v(-3.8, 149.72) * mm, "end": v(-3.98, 149.76) * mm});
            skLineSegment(sketch, "E3375", {"start": v(-3.98, 149.76) * mm, "end": v(-4.22, 149.81) * mm});
            skLineSegment(sketch, "E3376", {"start": v(-4.22, 149.81) * mm, "end": v(-5.34, 150.14) * mm});
            skLineSegment(sketch, "E3377", {"start": v(-5.34, 150.14) * mm, "end": v(-6.13, 150.47) * mm});
            skLineSegment(sketch, "E3378", {"start": v(-6.13, 150.47) * mm, "end": v(-6.2, 150.52) * mm});
            skLineSegment(sketch, "E3379", {"start": v(-6.2, 150.52) * mm, "end": v(-6.26, 150.55) * mm});
            skLineSegment(sketch, "E3380", {"start": v(-6.26, 150.55) * mm, "end": v(-6.64, 150.86) * mm});
            skLineSegment(sketch, "E3381", {"start": v(-6.64, 150.86) * mm, "end": v(-6.67, 150.9) * mm});
            skLineSegment(sketch, "E3382", {"start": v(-6.67, 150.9) * mm, "end": v(-6.73, 150.95) * mm});
            skLineSegment(sketch, "E3383", {"start": v(-6.73, 150.95) * mm, "end": v(-6.73, 150.95) * mm});
            skLineSegment(sketch, "E3384", {"start": v(-6.73, 150.95) * mm, "end": v(-6.77, 150.97) * mm});
            skLineSegment(sketch, "E3385", {"start": v(-6.77, 150.97) * mm, "end": v(-6.78, 151) * mm});
            skLineSegment(sketch, "E3386", {"start": v(-6.78, 151) * mm, "end": v(-6.92, 151.15) * mm});
            skLineSegment(sketch, "E3387", {"start": v(-6.92, 151.15) * mm, "end": v(-6.93, 151.16) * mm});
            skLineSegment(sketch, "E3388", {"start": v(-6.93, 151.16) * mm, "end": v(-6.97, 151.22) * mm});
            skLineSegment(sketch, "E3389", {"start": v(-6.97, 151.22) * mm, "end": v(-6.98, 151.23) * mm});
            skLineSegment(sketch, "E3390", {"start": v(-6.98, 151.23) * mm, "end": v(-7, 151.25) * mm});
            skLineSegment(sketch, "E3391", {"start": v(-7, 151.25) * mm, "end": v(-7, 151.25) * mm});
            skLineSegment(sketch, "E3392", {"start": v(-7, 151.25) * mm, "end": v(-7.04, 151.18) * mm});
            skLineSegment(sketch, "E3393", {"start": v(-7.04, 151.18) * mm, "end": v(-7.04, 151.16) * mm});
            skLineSegment(sketch, "E3394", {"start": v(-7.04, 151.16) * mm, "end": v(-7.04, 151.14) * mm});
            skLineSegment(sketch, "E3395", {"start": v(-7.04, 151.14) * mm, "end": v(-7.06, 151) * mm});
            skLineSegment(sketch, "E3396", {"start": v(-7.06, 151) * mm, "end": v(-7.15, 150.6) * mm});
            skLineSegment(sketch, "E3397", {"start": v(-7.15, 150.6) * mm, "end": v(-7.17, 150.48) * mm});
            skLineSegment(sketch, "E3398", {"start": v(-7.17, 150.48) * mm, "end": v(-7.18, 150.44) * mm});
            skLineSegment(sketch, "E3399", {"start": v(-7.18, 150.44) * mm, "end": v(-7.26, 150.05) * mm});
            skLineSegment(sketch, "E3400", {"start": v(-7.26, 150.05) * mm, "end": v(-7.26, 150.01) * mm});
            skLineSegment(sketch, "E3401", {"start": v(-7.26, 150.01) * mm, "end": v(-7.34, 149.76) * mm});
            skLineSegment(sketch, "E3402", {"start": v(-7.34, 149.76) * mm, "end": v(-7.9, 148.44) * mm});
            skLineSegment(sketch, "E3403", {"start": v(-7.9, 148.44) * mm, "end": v(-8.83, 147.03) * mm});
            skLineSegment(sketch, "E3404", {"start": v(-8.83, 147.03) * mm, "end": v(-9.09, 146.72) * mm});
            skLineSegment(sketch, "E3405", {"start": v(-9.09, 146.72) * mm, "end": v(-9.07, 146.83) * mm});
            skLineSegment(sketch, "E3406", {"start": v(-9.07, 146.83) * mm, "end": v(-9.2, 147.19) * mm});
            skLineSegment(sketch, "E3407", {"start": v(-9.2, 147.19) * mm, "end": v(-9.64, 147.15) * mm});
            skLineSegment(sketch, "E3408", {"start": v(-9.64, 147.15) * mm, "end": v(-9.74, 147.08) * mm});
            skLineSegment(sketch, "E3409", {"start": v(-9.74, 147.08) * mm, "end": v(-10.04, 146.88) * mm});
            skLineSegment(sketch, "E3410", {"start": v(-10.04, 146.88) * mm, "end": v(-10.94, 146.31) * mm});
            skLineSegment(sketch, "E3411", {"start": v(-10.94, 146.31) * mm, "end": v(-11.99, 145.8) * mm});
            skLineSegment(sketch, "E3412", {"start": v(-11.99, 145.8) * mm, "end": v(-12.98, 145.52) * mm});
            skLineSegment(sketch, "E3413", {"start": v(-12.98, 145.52) * mm, "end": v(-13.75, 145.45) * mm});
            skLineSegment(sketch, "E3414", {"start": v(-13.75, 145.45) * mm, "end": v(-14.01, 145.47) * mm});
            skLineSegment(sketch, "E3415", {"start": v(-14.01, 145.47) * mm, "end": v(-14.2, 145.48) * mm});
            skLineSegment(sketch, "E3416", {"start": v(-14.2, 145.48) * mm, "end": v(-14.74, 145.6) * mm});
            skLineSegment(sketch, "E3417", {"start": v(-14.74, 145.6) * mm, "end": v(-15.28, 145.8) * mm});
            skLineSegment(sketch, "E3418", {"start": v(-15.28, 145.8) * mm, "end": v(-15.63, 145.96) * mm});
            skLineSegment(sketch, "E3419", {"start": v(-15.63, 145.96) * mm, "end": v(-15.77, 145.97) * mm});
            skLineSegment(sketch, "E3420", {"start": v(-15.77, 145.97) * mm, "end": v(-15.78, 145.95) * mm});
            skLineSegment(sketch, "E3421", {"start": v(-15.78, 145.95) * mm, "end": v(-15.79, 145.94) * mm});
            skLineSegment(sketch, "E3422", {"start": v(-15.79, 145.94) * mm, "end": v(-15.8, 145.7) * mm});
            skLineSegment(sketch, "E3423", {"start": v(-15.8, 145.7) * mm, "end": v(-15.8, 145.68) * mm});
            skLineSegment(sketch, "E3424", {"start": v(-15.8, 145.68) * mm, "end": v(-15.8, 145.59) * mm});
            skLineSegment(sketch, "E3425", {"start": v(-15.8, 145.59) * mm, "end": v(-15.44, 144.97) * mm});
            skLineSegment(sketch, "E3426", {"start": v(-15.44, 144.97) * mm, "end": v(-14.77, 144.4) * mm});
            skLineSegment(sketch, "E3427", {"start": v(-14.77, 144.4) * mm, "end": v(-14.6, 144.32) * mm});
            skLineSegment(sketch, "E3428", {"start": v(-14.6, 144.32) * mm, "end": v(-14.47, 144.27) * mm});
            skLineSegment(sketch, "E3429", {"start": v(-14.47, 144.27) * mm, "end": v(-13.79, 144.07) * mm});
            skLineSegment(sketch, "E3430", {"start": v(-13.79, 144.07) * mm, "end": v(-13.03, 144) * mm});
            skLineSegment(sketch, "E3431", {"start": v(-13.03, 144) * mm, "end": v(-12.86, 144) * mm});
            skLineSegment(sketch, "E3432", {"start": v(-12.86, 144) * mm, "end": v(-13, 143.96) * mm});
            skLineSegment(sketch, "E3433", {"start": v(-13, 143.96) * mm, "end": v(-13.43, 143.85) * mm});
            skLineSegment(sketch, "E3434", {"start": v(-13.43, 143.85) * mm, "end": v(-13.93, 143.75) * mm});
            skLineSegment(sketch, "E3435", {"start": v(-13.93, 143.75) * mm, "end": v(-14.4, 143.66) * mm});
            skLineSegment(sketch, "E3436", {"start": v(-14.4, 143.66) * mm, "end": v(-14.9, 143.55) * mm});
            skLineSegment(sketch, "E3437", {"start": v(-14.9, 143.55) * mm, "end": v(-15.46, 143.4) * mm});
            skLineSegment(sketch, "E3438", {"start": v(-15.46, 143.4) * mm, "end": v(-16.15, 143.17) * mm});
            skLineSegment(sketch, "E3439", {"start": v(-16.15, 143.17) * mm, "end": v(-17, 142.83) * mm});
            skLineSegment(sketch, "E3440", {"start": v(-17, 142.83) * mm, "end": v(-17.8, 142.47) * mm});
            skLineSegment(sketch, "E3441", {"start": v(-17.8, 142.47) * mm, "end": v(-18.06, 142.35) * mm});
            skLineSegment(sketch, "E3442", {"start": v(-18.06, 142.35) * mm, "end": v(-18.19, 142.29) * mm});
            skLineSegment(sketch, "E3443", {"start": v(-18.19, 142.29) * mm, "end": v(-18.96, 141.87) * mm});
            skLineSegment(sketch, "E3444", {"start": v(-18.96, 141.87) * mm, "end": v(-19.7, 141.42) * mm});
            skLineSegment(sketch, "E3445", {"start": v(-19.7, 141.42) * mm, "end": v(-19.81, 141.34) * mm});
            skLineSegment(sketch, "E3446", {"start": v(-19.81, 141.34) * mm, "end": v(-20.16, 141.1) * mm});
            skLineSegment(sketch, "E3447", {"start": v(-20.16, 141.1) * mm, "end": v(-21.7, 139.61) * mm});
            skLineSegment(sketch, "E3448", {"start": v(-21.7, 139.61) * mm, "end": v(-22.9, 137.88) * mm});
            skLineSegment(sketch, "E3449", {"start": v(-22.9, 137.88) * mm, "end": v(-23.08, 137.5) * mm});
            skLineSegment(sketch, "E3450", {"start": v(-23.08, 137.5) * mm, "end": v(-23.25, 137.16) * mm});
            skLineSegment(sketch, "E3451", {"start": v(-23.25, 137.16) * mm, "end": v(-23.88, 135.57) * mm});
            skLineSegment(sketch, "E3452", {"start": v(-23.88, 135.57) * mm, "end": v(-24.24, 134.2) * mm});
            skLineSegment(sketch, "E3453", {"start": v(-24.24, 134.2) * mm, "end": v(-24.28, 133.97) * mm});
            skLineSegment(sketch, "E3454", {"start": v(-24.28, 133.97) * mm, "end": v(-24.3, 133.83) * mm});
            skLineSegment(sketch, "E3455", {"start": v(-24.3, 133.83) * mm, "end": v(-24.34, 133.4) * mm});
            skLineSegment(sketch, "E3456", {"start": v(-24.34, 133.4) * mm, "end": v(-24.38, 132.84) * mm});
            skLineSegment(sketch, "E3457", {"start": v(-24.38, 132.84) * mm, "end": v(-24.39, 132.4) * mm});
            skLineSegment(sketch, "E3458", {"start": v(-24.39, 132.4) * mm, "end": v(-24.39, 132.26) * mm});
            skLineSegment(sketch, "E3459", {"start": v(-24.39, 132.26) * mm, "end": v(-24.39, 132.21) * mm});
            skLineSegment(sketch, "E3460", {"start": v(1.21, 157.77) * mm, "end": v(1.16, 157.75) * mm});
            skLineSegment(sketch, "E3461", {"start": v(1.16, 157.75) * mm, "end": v(0.89, 157.82) * mm});
            skLineSegment(sketch, "E3462", {"start": v(0.89, 157.82) * mm, "end": v(0.7, 158.07) * mm});
            skLineSegment(sketch, "E3463", {"start": v(0.7, 158.07) * mm, "end": v(0.68, 158.14) * mm});
            skLineSegment(sketch, "E3464", {"start": v(0.68, 158.14) * mm, "end": v(0.66, 158.2) * mm});
            skLineSegment(sketch, "E3465", {"start": v(0.66, 158.2) * mm, "end": v(0.7, 158.51) * mm});
            skLineSegment(sketch, "E3466", {"start": v(0.7, 158.51) * mm, "end": v(0.9, 158.71) * mm});
            skLineSegment(sketch, "E3467", {"start": v(0.9, 158.71) * mm, "end": v(0.96, 158.72) * mm});
            skLineSegment(sketch, "E3468", {"start": v(0.96, 158.72) * mm, "end": v(1.02, 158.74) * mm});
            skLineSegment(sketch, "E3469", {"start": v(1.02, 158.74) * mm, "end": v(1.3, 158.67) * mm});
            skLineSegment(sketch, "E3470", {"start": v(1.3, 158.67) * mm, "end": v(1.5, 158.43) * mm});
            skLineSegment(sketch, "E3471", {"start": v(1.5, 158.43) * mm, "end": v(1.5, 158.37) * mm});
            skLineSegment(sketch, "E3472", {"start": v(1.5, 158.37) * mm, "end": v(1.53, 158.3) * mm});
            skLineSegment(sketch, "E3473", {"start": v(1.53, 158.3) * mm, "end": v(1.47, 157.98) * mm});
            skLineSegment(sketch, "E3474", {"start": v(1.47, 157.98) * mm, "end": v(1.27, 157.78) * mm});
            skLineSegment(sketch, "E3475", {"start": v(1.27, 157.78) * mm, "end": v(1.21, 157.77) * mm});
            skLineSegment(sketch, "E3476", {"start": v(2.4, 155.42) * mm, "end": v(2.42, 155.36) * mm});
            skLineSegment(sketch, "E3477", {"start": v(2.42, 155.36) * mm, "end": v(2.38, 155.06) * mm});
            skLineSegment(sketch, "E3478", {"start": v(2.38, 155.06) * mm, "end": v(2.19, 154.86) * mm});
            skLineSegment(sketch, "E3479", {"start": v(2.19, 154.86) * mm, "end": v(2.13, 154.84) * mm});
            skLineSegment(sketch, "E3480", {"start": v(2.13, 154.84) * mm, "end": v(2.08, 154.83) * mm});
            skLineSegment(sketch, "E3481", {"start": v(2.08, 154.83) * mm, "end": v(1.8, 154.91) * mm});
            skLineSegment(sketch, "E3482", {"start": v(1.8, 154.91) * mm, "end": v(1.6, 155.14) * mm});
            skLineSegment(sketch, "E3483", {"start": v(1.6, 155.14) * mm, "end": v(1.58, 155.2) * mm});
            skLineSegment(sketch, "E3484", {"start": v(1.58, 155.2) * mm, "end": v(1.56, 155.28) * mm});
            skLineSegment(sketch, "E3485", {"start": v(1.56, 155.28) * mm, "end": v(1.6, 155.6) * mm});
            skLineSegment(sketch, "E3486", {"start": v(1.6, 155.6) * mm, "end": v(1.8, 155.8) * mm});
            skLineSegment(sketch, "E3487", {"start": v(1.8, 155.8) * mm, "end": v(1.86, 155.81) * mm});
            skLineSegment(sketch, "E3488", {"start": v(1.86, 155.81) * mm, "end": v(1.92, 155.83) * mm});
            skLineSegment(sketch, "E3489", {"start": v(1.92, 155.83) * mm, "end": v(2.2, 155.75) * mm});
            skLineSegment(sketch, "E3490", {"start": v(2.2, 155.75) * mm, "end": v(2.38, 155.5) * mm});
            skLineSegment(sketch, "E3491", {"start": v(2.38, 155.5) * mm, "end": v(2.4, 155.42) * mm});
            skLineSegment(sketch, "E3492", {"start": v(-3.62, 164.65) * mm, "end": v(-3.6, 164.68) * mm});
            skLineSegment(sketch, "E3493", {"start": v(-3.6, 164.68) * mm, "end": v(-3.35, 164.84) * mm});
            skLineSegment(sketch, "E3494", {"start": v(-3.35, 164.84) * mm, "end": v(-2.82, 165.11) * mm});
            skLineSegment(sketch, "E3495", {"start": v(-2.82, 165.11) * mm, "end": v(-2.29, 165.34) * mm});
            skLineSegment(sketch, "E3496", {"start": v(-2.29, 165.34) * mm, "end": v(-2.04, 165.4) * mm});
            skLineSegment(sketch, "E3497", {"start": v(-2.04, 165.4) * mm, "end": v(-2.04, 165.39) * mm});
            skLineSegment(sketch, "E3498", {"start": v(-2.04, 165.39) * mm, "end": v(-2.02, 165.33) * mm});
            skLineSegment(sketch, "E3499", {"start": v(-2.02, 165.33) * mm, "end": v(-2.1, 165.12) * mm});
            skLineSegment(sketch, "E3500", {"start": v(-2.1, 165.12) * mm, "end": v(-2.34, 164.87) * mm});
            skLineSegment(sketch, "E3501", {"start": v(-2.34, 164.87) * mm, "end": v(-2.59, 164.64) * mm});
            skLineSegment(sketch, "E3502", {"start": v(-2.59, 164.64) * mm, "end": v(-2.66, 164.48) * mm});
            skLineSegment(sketch, "E3503", {"start": v(-2.66, 164.48) * mm, "end": v(-2.64, 164.45) * mm});
            skLineSegment(sketch, "E3504", {"start": v(-2.64, 164.45) * mm, "end": v(-2.63, 164.42) * mm});
            skLineSegment(sketch, "E3505", {"start": v(-2.63, 164.42) * mm, "end": v(-2.4, 164.23) * mm});
            skLineSegment(sketch, "E3506", {"start": v(-2.4, 164.23) * mm, "end": v(-1.86, 163.78) * mm});
            skLineSegment(sketch, "E3507", {"start": v(-1.86, 163.78) * mm, "end": v(-1.12, 163.13) * mm});
            skLineSegment(sketch, "E3508", {"start": v(-1.12, 163.13) * mm, "end": v(-0.48, 162.52) * mm});
            skLineSegment(sketch, "E3509", {"start": v(-0.48, 162.52) * mm, "end": v(-0.27, 162.3) * mm});
            skLineSegment(sketch, "E3510", {"start": v(-0.27, 162.3) * mm, "end": v(-0.11, 162.14) * mm});
            skLineSegment(sketch, "E3511", {"start": v(-0.11, 162.14) * mm, "end": v(0.35, 161.62) * mm});
            skLineSegment(sketch, "E3512", {"start": v(0.35, 161.62) * mm, "end": v(0.78, 161.08) * mm});
            skLineSegment(sketch, "E3513", {"start": v(0.78, 161.08) * mm, "end": v(1.05, 160.68) * mm});
            skLineSegment(sketch, "E3514", {"start": v(1.05, 160.68) * mm, "end": v(1.17, 160.48) * mm});
            skLineSegment(sketch, "E3515", {"start": v(1.17, 160.48) * mm, "end": v(1.21, 160.4) * mm});
            skLineSegment(sketch, "E3516", {"start": v(1.21, 160.4) * mm, "end": v(1.24, 160.35) * mm});
            skLineSegment(sketch, "E3517", {"start": v(1.24, 160.35) * mm, "end": v(1.36, 160.02) * mm});
            skLineSegment(sketch, "E3518", {"start": v(1.36, 160.02) * mm, "end": v(1.43, 159.8) * mm});
            skLineSegment(sketch, "E3519", {"start": v(1.43, 159.8) * mm, "end": v(1.37, 159.87) * mm});
            skLineSegment(sketch, "E3520", {"start": v(1.37, 159.87) * mm, "end": v(1.2, 160.1) * mm});
            skLineSegment(sketch, "E3521", {"start": v(1.2, 160.1) * mm, "end": v(1.02, 160.38) * mm});
            skLineSegment(sketch, "E3522", {"start": v(1.02, 160.38) * mm, "end": v(0.75, 160.73) * mm});
            skLineSegment(sketch, "E3523", {"start": v(0.75, 160.73) * mm, "end": v(0.38, 161.15) * mm});
            skLineSegment(sketch, "E3524", {"start": v(0.38, 161.15) * mm, "end": v(0.26, 161.28) * mm});
            skLineSegment(sketch, "E3525", {"start": v(0.26, 161.28) * mm, "end": v(-0.06, 161.61) * mm});
            skLineSegment(sketch, "E3526", {"start": v(-0.06, 161.61) * mm, "end": v(-1.07, 162.53) * mm});
            skLineSegment(sketch, "E3527", {"start": v(-1.07, 162.53) * mm, "end": v(-2.33, 163.57) * mm});
            skLineSegment(sketch, "E3528", {"start": v(-2.33, 163.57) * mm, "end": v(-3.28, 164.3) * mm});
            skLineSegment(sketch, "E3529", {"start": v(-3.28, 164.3) * mm, "end": v(-3.64, 164.6) * mm});
            skLineSegment(sketch, "E3530", {"start": v(-3.64, 164.6) * mm, "end": v(-3.62, 164.65) * mm});
            skLineSegment(sketch, "E3531", {"start": v(10.35, 171.2) * mm, "end": v(10.36, 171.26) * mm});
            skLineSegment(sketch, "E3532", {"start": v(10.36, 171.26) * mm, "end": v(10.42, 171.47) * mm});
            skLineSegment(sketch, "E3533", {"start": v(10.42, 171.47) * mm, "end": v(10.42, 171.59) * mm});
            skLineSegment(sketch, "E3534", {"start": v(10.42, 171.59) * mm, "end": v(10.38, 171.58) * mm});
            skLineSegment(sketch, "E3535", {"start": v(10.38, 171.58) * mm, "end": v(10.3, 171.47) * mm});
            skLineSegment(sketch, "E3536", {"start": v(10.3, 171.47) * mm, "end": v(10.29, 171.43) * mm});
            skLineSegment(sketch, "E3537", {"start": v(10.29, 171.43) * mm, "end": v(10.27, 171.4) * mm});
            skLineSegment(sketch, "E3538", {"start": v(10.27, 171.4) * mm, "end": v(10.22, 171.15) * mm});
            skLineSegment(sketch, "E3539", {"start": v(10.22, 171.15) * mm, "end": v(10.21, 171) * mm});
            skLineSegment(sketch, "E3540", {"start": v(10.21, 171) * mm, "end": v(10.21, 170.95) * mm});
            skLineSegment(sketch, "E3541", {"start": v(10.21, 170.95) * mm, "end": v(10.27, 170.98) * mm});
            skLineSegment(sketch, "E3542", {"start": v(10.27, 170.98) * mm, "end": v(10.34, 171.16) * mm});
            skLineSegment(sketch, "E3543", {"start": v(10.34, 171.16) * mm, "end": v(10.35, 171.2) * mm});
            skLineSegment(sketch, "E3544", {"start": v(-3.57, 178.02) * mm, "end": v(-3.49, 177.94) * mm});
            skLineSegment(sketch, "E3545", {"start": v(-3.49, 177.94) * mm, "end": v(-2.96, 177.67) * mm});
            skLineSegment(sketch, "E3546", {"start": v(-2.96, 177.67) * mm, "end": v(-2.45, 177.53) * mm});
            skLineSegment(sketch, "E3547", {"start": v(-2.45, 177.53) * mm, "end": v(-2.38, 177.52) * mm});
            skLineSegment(sketch, "E3548", {"start": v(-2.38, 177.52) * mm, "end": v(-2.31, 177.52) * mm});
            skLineSegment(sketch, "E3549", {"start": v(-2.31, 177.52) * mm, "end": v(-2.16, 177.51) * mm});
            skLineSegment(sketch, "E3550", {"start": v(-2.16, 177.51) * mm, "end": v(-2.11, 177.5) * mm});
            skLineSegment(sketch, "E3551", {"start": v(-2.11, 177.5) * mm, "end": v(-2.08, 177.5) * mm});
            skLineSegment(sketch, "E3552", {"start": v(-2.08, 177.5) * mm, "end": v(-1.81, 177.5) * mm});
            skLineSegment(sketch, "E3553", {"start": v(-1.81, 177.5) * mm, "end": v(-1.55, 177.44) * mm});
            skLineSegment(sketch, "E3554", {"start": v(-1.55, 177.44) * mm, "end": v(-1.52, 177.42) * mm});
            skLineSegment(sketch, "E3555", {"start": v(-1.52, 177.42) * mm, "end": v(-1.5, 177.38) * mm});
            skLineSegment(sketch, "E3556", {"start": v(-1.5, 177.38) * mm, "end": v(-1.63, 177.14) * mm});
            skLineSegment(sketch, "E3557", {"start": v(-1.63, 177.14) * mm, "end": v(-2.16, 177.03) * mm});
            skLineSegment(sketch, "E3558", {"start": v(-2.16, 177.03) * mm, "end": v(-2.32, 177.05) * mm});
            skLineSegment(sketch, "E3559", {"start": v(-2.32, 177.05) * mm, "end": v(-2.43, 177.07) * mm});
            skLineSegment(sketch, "E3560", {"start": v(-2.43, 177.07) * mm, "end": v(-2.94, 176.92) * mm});
            skLineSegment(sketch, "E3561", {"start": v(-2.94, 176.92) * mm, "end": v(-3.24, 176.41) * mm});
            skLineSegment(sketch, "E3562", {"start": v(-3.24, 176.41) * mm, "end": v(-3.25, 176.25) * mm});
            skLineSegment(sketch, "E3563", {"start": v(-3.25, 176.25) * mm, "end": v(-3.27, 176.04) * mm});
            skLineSegment(sketch, "E3564", {"start": v(-3.27, 176.04) * mm, "end": v(-3.13, 175.19) * mm});
            skLineSegment(sketch, "E3565", {"start": v(-3.13, 175.19) * mm, "end": v(-3, 174.54) * mm});
            skLineSegment(sketch, "E3566", {"start": v(-3, 174.54) * mm, "end": v(-3, 174.44) * mm});
            skLineSegment(sketch, "E3567", {"start": v(-3, 174.44) * mm, "end": v(-3.01, 174.36) * mm});
            skLineSegment(sketch, "E3568", {"start": v(-3.01, 174.36) * mm, "end": v(-3.16, 174.16) * mm});
            skLineSegment(sketch, "E3569", {"start": v(-3.16, 174.16) * mm, "end": v(-3.35, 174.1) * mm});
            skLineSegment(sketch, "E3570", {"start": v(-3.35, 174.1) * mm, "end": v(-3.38, 174.1) * mm});
            skLineSegment(sketch, "E3571", {"start": v(-3.38, 174.1) * mm, "end": v(-3.4, 174.1) * mm});
            skLineSegment(sketch, "E3572", {"start": v(-3.4, 174.1) * mm, "end": v(-3.6, 174.06) * mm});
            skLineSegment(sketch, "E3573", {"start": v(-3.6, 174.06) * mm, "end": v(-3.6, 174.05) * mm});
            skLineSegment(sketch, "E3574", {"start": v(-3.6, 174.05) * mm, "end": v(-3.63, 174.04) * mm});
            skLineSegment(sketch, "E3575", {"start": v(-3.63, 174.04) * mm, "end": v(-3.6, 173.81) * mm});
            skLineSegment(sketch, "E3576", {"start": v(-3.6, 173.81) * mm, "end": v(-3.37, 173.6) * mm});
            skLineSegment(sketch, "E3577", {"start": v(-3.37, 173.6) * mm, "end": v(-3.3, 173.57) * mm});
            skLineSegment(sketch, "E3578", {"start": v(-3.3, 173.57) * mm, "end": v(-3.27, 173.57) * mm});
            skLineSegment(sketch, "E3579", {"start": v(-3.27, 173.57) * mm, "end": v(-2.98, 173.54) * mm});
            skLineSegment(sketch, "E3580", {"start": v(-2.98, 173.54) * mm, "end": v(-2.95, 173.55) * mm});
            skLineSegment(sketch, "E3581", {"start": v(-2.95, 173.55) * mm, "end": v(-2.88, 173.55) * mm});
            skLineSegment(sketch, "E3582", {"start": v(-2.88, 173.55) * mm, "end": v(-2.67, 173.6) * mm});
            skLineSegment(sketch, "E3583", {"start": v(-2.67, 173.6) * mm, "end": v(-2.42, 173.66) * mm});
            skLineSegment(sketch, "E3584", {"start": v(-2.42, 173.66) * mm, "end": v(-2.34, 173.66) * mm});
            skLineSegment(sketch, "E3585", {"start": v(-2.34, 173.66) * mm, "end": v(-2.23, 173.66) * mm});
            skLineSegment(sketch, "E3586", {"start": v(-2.23, 173.66) * mm, "end": v(-1.94, 173.57) * mm});
            skLineSegment(sketch, "E3587", {"start": v(-1.94, 173.57) * mm, "end": v(-1.9, 173.55) * mm});
            skLineSegment(sketch, "E3588", {"start": v(-1.9, 173.55) * mm, "end": v(-1.83, 173.52) * mm});
            skLineSegment(sketch, "E3589", {"start": v(-1.83, 173.52) * mm, "end": v(-1.26, 173.14) * mm});
            skLineSegment(sketch, "E3590", {"start": v(-1.26, 173.14) * mm, "end": v(-1.22, 173.11) * mm});
            skLineSegment(sketch, "E3591", {"start": v(-1.22, 173.11) * mm, "end": v(-1.2, 173.06) * mm});
            skLineSegment(sketch, "E3592", {"start": v(-1.2, 173.06) * mm, "end": v(-1.07, 172.79) * mm});
            skLineSegment(sketch, "E3593", {"start": v(-1.07, 172.79) * mm, "end": v(-0.92, 172.59) * mm});
            skLineSegment(sketch, "E3594", {"start": v(-0.92, 172.59) * mm, "end": v(-0.9, 172.58) * mm});
            skLineSegment(sketch, "E3595", {"start": v(-0.9, 172.58) * mm, "end": v(-0.85, 172.57) * mm});
            skLineSegment(sketch, "E3596", {"start": v(-0.85, 172.57) * mm, "end": v(-0.63, 172.75) * mm});
            skLineSegment(sketch, "E3597", {"start": v(-0.63, 172.75) * mm, "end": v(-0.53, 172.99) * mm});
            skLineSegment(sketch, "E3598", {"start": v(-0.53, 172.99) * mm, "end": v(-0.55, 173) * mm});
            skLineSegment(sketch, "E3599", {"start": v(-0.55, 173) * mm, "end": v(-0.72, 173.02) * mm});
            skLineSegment(sketch, "E3600", {"start": v(-0.72, 173.02) * mm, "end": v(-0.99, 173.11) * mm});
            skLineSegment(sketch, "E3601", {"start": v(-0.99, 173.11) * mm, "end": v(-1.03, 173.15) * mm});
            skLineSegment(sketch, "E3602", {"start": v(-1.03, 173.15) * mm, "end": v(-1.04, 173.21) * mm});
            skLineSegment(sketch, "E3603", {"start": v(-1.04, 173.21) * mm, "end": v(-1.17, 173.81) * mm});
            skLineSegment(sketch, "E3604", {"start": v(-1.17, 173.81) * mm, "end": v(-1.19, 173.85) * mm});
            skLineSegment(sketch, "E3605", {"start": v(-1.19, 173.85) * mm, "end": v(-1.21, 173.92) * mm});
            skLineSegment(sketch, "E3606", {"start": v(-1.21, 173.92) * mm, "end": v(-1.43, 174.63) * mm});
            skLineSegment(sketch, "E3607", {"start": v(-1.43, 174.63) * mm, "end": v(-1.44, 174.7) * mm});
            skLineSegment(sketch, "E3608", {"start": v(-1.44, 174.7) * mm, "end": v(-1.44, 174.78) * mm});
            skLineSegment(sketch, "E3609", {"start": v(-1.44, 174.78) * mm, "end": v(-1.4, 175) * mm});
            skLineSegment(sketch, "E3610", {"start": v(-1.4, 175) * mm, "end": v(-1.22, 175.32) * mm});
            skLineSegment(sketch, "E3611", {"start": v(-1.22, 175.32) * mm, "end": v(-0.93, 175.55) * mm});
            skLineSegment(sketch, "E3612", {"start": v(-0.93, 175.55) * mm, "end": v(-0.63, 175.61) * mm});
            skLineSegment(sketch, "E3613", {"start": v(-0.63, 175.61) * mm, "end": v(-0.53, 175.6) * mm});
            skLineSegment(sketch, "E3614", {"start": v(-0.53, 175.6) * mm, "end": v(-0.47, 175.58) * mm});
            skLineSegment(sketch, "E3615", {"start": v(-0.47, 175.58) * mm, "end": v(-0.25, 175.34) * mm});
            skLineSegment(sketch, "E3616", {"start": v(-0.25, 175.34) * mm, "end": v(-0.14, 174.98) * mm});
            skLineSegment(sketch, "E3617", {"start": v(-0.14, 174.98) * mm, "end": v(-0.13, 174.9) * mm});
            skLineSegment(sketch, "E3618", {"start": v(-0.13, 174.9) * mm, "end": v(-0.14, 174.92) * mm});
            skLineSegment(sketch, "E3619", {"start": v(-0.14, 174.92) * mm, "end": v(-0.3, 175.05) * mm});
            skLineSegment(sketch, "E3620", {"start": v(-0.3, 175.05) * mm, "end": v(-0.32, 175.06) * mm});
            skLineSegment(sketch, "E3621", {"start": v(-0.32, 175.06) * mm, "end": v(-0.33, 175.06) * mm});
            skLineSegment(sketch, "E3622", {"start": v(-0.33, 175.06) * mm, "end": v(-0.56, 175.01) * mm});
            skLineSegment(sketch, "E3623", {"start": v(-0.56, 175.01) * mm, "end": v(-0.58, 174.99) * mm});
            skLineSegment(sketch, "E3624", {"start": v(-0.58, 174.99) * mm, "end": v(-0.59, 174.97) * mm});
            skLineSegment(sketch, "E3625", {"start": v(-0.59, 174.97) * mm, "end": v(-0.54, 174.88) * mm});
            skLineSegment(sketch, "E3626", {"start": v(-0.54, 174.88) * mm, "end": v(-0.43, 174.82) * mm});
            skLineSegment(sketch, "E3627", {"start": v(-0.43, 174.82) * mm, "end": v(-0.42, 174.8) * mm});
            skLineSegment(sketch, "E3628", {"start": v(-0.42, 174.8) * mm, "end": v(-0.4, 174.78) * mm});
            skLineSegment(sketch, "E3629", {"start": v(-0.4, 174.78) * mm, "end": v(-0.2, 174.5) * mm});
            skLineSegment(sketch, "E3630", {"start": v(-0.2, 174.5) * mm, "end": v(-0.18, 174.45) * mm});
            skLineSegment(sketch, "E3631", {"start": v(-0.18, 174.45) * mm, "end": v(-0.16, 174.42) * mm});
            skLineSegment(sketch, "E3632", {"start": v(-0.16, 174.42) * mm, "end": v(-0.04, 174.1) * mm});
            skLineSegment(sketch, "E3633", {"start": v(-0.04, 174.1) * mm, "end": v(-0.03, 174.07) * mm});
            skLineSegment(sketch, "E3634", {"start": v(-0.03, 174.07) * mm, "end": v(-0.03, 174.04) * mm});
            skLineSegment(sketch, "E3635", {"start": v(-0.03, 174.04) * mm, "end": v(0, 173.83) * mm});
            skLineSegment(sketch, "E3636", {"start": v(0, 173.83) * mm, "end": v(0, 173.8) * mm});
            skLineSegment(sketch, "E3637", {"start": v(0, 173.8) * mm, "end": v(0.02, 173.73) * mm});
            skLineSegment(sketch, "E3638", {"start": v(0.02, 173.73) * mm, "end": v(0.06, 173.5) * mm});
            skLineSegment(sketch, "E3639", {"start": v(0.06, 173.5) * mm, "end": v(0.12, 173.4) * mm});
            skLineSegment(sketch, "E3640", {"start": v(0.12, 173.4) * mm, "end": v(0.14, 173.39) * mm});
            skLineSegment(sketch, "E3641", {"start": v(0.14, 173.39) * mm, "end": v(0.15, 173.38) * mm});
            skLineSegment(sketch, "E3642", {"start": v(0.15, 173.38) * mm, "end": v(0.27, 173.3) * mm});
            skLineSegment(sketch, "E3643", {"start": v(0.27, 173.3) * mm, "end": v(0.5, 173.13) * mm});
            skLineSegment(sketch, "E3644", {"start": v(0.5, 173.13) * mm, "end": v(0.76, 172.98) * mm});
            skLineSegment(sketch, "E3645", {"start": v(0.76, 172.98) * mm, "end": v(0.91, 172.91) * mm});
            skLineSegment(sketch, "E3646", {"start": v(0.91, 172.91) * mm, "end": v(0.96, 172.92) * mm});
            skLineSegment(sketch, "E3647", {"start": v(0.96, 172.92) * mm, "end": v(1.01, 172.92) * mm});
            skLineSegment(sketch, "E3648", {"start": v(1.01, 172.92) * mm, "end": v(1.16, 173) * mm});
            skLineSegment(sketch, "E3649", {"start": v(1.16, 173) * mm, "end": v(1.15, 173.02) * mm});
            skLineSegment(sketch, "E3650", {"start": v(1.15, 173.02) * mm, "end": v(1, 173.34) * mm});
            skLineSegment(sketch, "E3651", {"start": v(1, 173.34) * mm, "end": v(0.93, 174.08) * mm});
            skLineSegment(sketch, "E3652", {"start": v(0.93, 174.08) * mm, "end": v(0.96, 174.3) * mm});
            skLineSegment(sketch, "E3653", {"start": v(0.96, 174.3) * mm, "end": v(0.98, 174.34) * mm});
            skLineSegment(sketch, "E3654", {"start": v(0.98, 174.34) * mm, "end": v(1.13, 174.84) * mm});
            skLineSegment(sketch, "E3655", {"start": v(1.13, 174.84) * mm, "end": v(1.15, 174.9) * mm});
            skLineSegment(sketch, "E3656", {"start": v(1.15, 174.9) * mm, "end": v(1.16, 174.92) * mm});
            skLineSegment(sketch, "E3657", {"start": v(1.16, 174.92) * mm, "end": v(1.48, 175) * mm});
            skLineSegment(sketch, "E3658", {"start": v(1.48, 175) * mm, "end": v(1.52, 175) * mm});
            skLineSegment(sketch, "E3659", {"start": v(1.52, 175) * mm, "end": v(1.66, 174.98) * mm});
            skLineSegment(sketch, "E3660", {"start": v(1.66, 174.98) * mm, "end": v(1.9, 174.9) * mm});
            skLineSegment(sketch, "E3661", {"start": v(1.9, 174.9) * mm, "end": v(1.95, 174.86) * mm});
            skLineSegment(sketch, "E3662", {"start": v(1.95, 174.86) * mm, "end": v(1.97, 174.85) * mm});
            skLineSegment(sketch, "E3663", {"start": v(1.97, 174.85) * mm, "end": v(2.15, 174.75) * mm});
            skLineSegment(sketch, "E3664", {"start": v(2.15, 174.75) * mm, "end": v(2.17, 174.74) * mm});
            skLineSegment(sketch, "E3665", {"start": v(2.17, 174.74) * mm, "end": v(2.2, 174.72) * mm});
            skLineSegment(sketch, "E3666", {"start": v(2.2, 174.72) * mm, "end": v(2.35, 174.55) * mm});
            skLineSegment(sketch, "E3667", {"start": v(2.35, 174.55) * mm, "end": v(2.35, 174.54) * mm});
            skLineSegment(sketch, "E3668", {"start": v(2.35, 174.54) * mm, "end": v(2.35, 174.53) * mm});
            skLineSegment(sketch, "E3669", {"start": v(2.35, 174.53) * mm, "end": v(2.3, 174.46) * mm});
            skLineSegment(sketch, "E3670", {"start": v(2.3, 174.46) * mm, "end": v(2.3, 174.45) * mm});
            skLineSegment(sketch, "E3671", {"start": v(2.3, 174.45) * mm, "end": v(2.3, 174.42) * mm});
            skLineSegment(sketch, "E3672", {"start": v(2.3, 174.42) * mm, "end": v(2.28, 174.34) * mm});
            skLineSegment(sketch, "E3673", {"start": v(2.28, 174.34) * mm, "end": v(2.28, 174.33) * mm});
            skLineSegment(sketch, "E3674", {"start": v(2.28, 174.33) * mm, "end": v(2.47, 174.18) * mm});
            skLineSegment(sketch, "E3675", {"start": v(2.47, 174.18) * mm, "end": v(2.5, 174.16) * mm});
            skLineSegment(sketch, "E3676", {"start": v(2.5, 174.16) * mm, "end": v(2.54, 174.1) * mm});
            skLineSegment(sketch, "E3677", {"start": v(2.54, 174.1) * mm, "end": v(2.55, 174.1) * mm});
            skLineSegment(sketch, "E3678", {"start": v(2.55, 174.1) * mm, "end": v(2.55, 174.1) * mm});
            skLineSegment(sketch, "E3679", {"start": v(2.55, 174.1) * mm, "end": v(2.6, 173.98) * mm});
            skLineSegment(sketch, "E3680", {"start": v(2.6, 173.98) * mm, "end": v(2.6, 173.97) * mm});
            skLineSegment(sketch, "E3681", {"start": v(2.6, 173.97) * mm, "end": v(2.6, 173.95) * mm});
            skLineSegment(sketch, "E3682", {"start": v(2.6, 173.95) * mm, "end": v(2.75, 173.79) * mm});
            skLineSegment(sketch, "E3683", {"start": v(2.75, 173.79) * mm, "end": v(2.8, 173.76) * mm});
            skLineSegment(sketch, "E3684", {"start": v(2.8, 173.76) * mm, "end": v(2.83, 173.75) * mm});
            skLineSegment(sketch, "E3685", {"start": v(2.83, 173.75) * mm, "end": v(3.13, 173.68) * mm});
            skLineSegment(sketch, "E3686", {"start": v(3.13, 173.68) * mm, "end": v(3.6, 173.64) * mm});
            skLineSegment(sketch, "E3687", {"start": v(3.6, 173.64) * mm, "end": v(3.76, 173.64) * mm});
            skLineSegment(sketch, "E3688", {"start": v(3.76, 173.64) * mm, "end": v(3.89, 173.64) * mm});
            skLineSegment(sketch, "E3689", {"start": v(3.89, 173.64) * mm, "end": v(3.96, 173.64) * mm});
            skLineSegment(sketch, "E3690", {"start": v(3.96, 173.64) * mm, "end": v(4.2, 173.61) * mm});
            skLineSegment(sketch, "E3691", {"start": v(4.2, 173.61) * mm, "end": v(4.44, 173.53) * mm});
            skLineSegment(sketch, "E3692", {"start": v(4.44, 173.53) * mm, "end": v(4.46, 173.5) * mm});
            skLineSegment(sketch, "E3693", {"start": v(4.46, 173.5) * mm, "end": v(4.49, 173.48) * mm});
            skLineSegment(sketch, "E3694", {"start": v(4.49, 173.48) * mm, "end": v(4.53, 173.17) * mm});
            skLineSegment(sketch, "E3695", {"start": v(4.53, 173.17) * mm, "end": v(4.5, 172.64) * mm});
            skLineSegment(sketch, "E3696", {"start": v(4.5, 172.64) * mm, "end": v(4.5, 172.5) * mm});
            skLineSegment(sketch, "E3697", {"start": v(4.5, 172.5) * mm, "end": v(4.5, 172.36) * mm});
            skLineSegment(sketch, "E3698", {"start": v(4.5, 172.36) * mm, "end": v(4.48, 171.96) * mm});
            skLineSegment(sketch, "E3699", {"start": v(4.48, 171.96) * mm, "end": v(4.44, 171.76) * mm});
            skLineSegment(sketch, "E3700", {"start": v(4.44, 171.76) * mm, "end": v(4.43, 171.73) * mm});
            skLineSegment(sketch, "E3701", {"start": v(4.43, 171.73) * mm, "end": v(4.43, 171.7) * mm});
            skLineSegment(sketch, "E3702", {"start": v(4.43, 171.7) * mm, "end": v(4.22, 171.51) * mm});
            skLineSegment(sketch, "E3703", {"start": v(4.22, 171.51) * mm, "end": v(4.15, 171.51) * mm});
            skLineSegment(sketch, "E3704", {"start": v(4.15, 171.51) * mm, "end": v(4.1, 171.52) * mm});
            skLineSegment(sketch, "E3705", {"start": v(4.1, 171.52) * mm, "end": v(3.84, 171.53) * mm});
            skLineSegment(sketch, "E3706", {"start": v(3.84, 171.53) * mm, "end": v(3.82, 171.52) * mm});
            skLineSegment(sketch, "E3707", {"start": v(3.82, 171.52) * mm, "end": v(3.8, 171.52) * mm});
            skLineSegment(sketch, "E3708", {"start": v(3.8, 171.52) * mm, "end": v(3.69, 171.4) * mm});
            skLineSegment(sketch, "E3709", {"start": v(3.69, 171.4) * mm, "end": v(3.61, 171.18) * mm});
            skLineSegment(sketch, "E3710", {"start": v(3.61, 171.18) * mm, "end": v(3.6, 171.14) * mm});
            skLineSegment(sketch, "E3711", {"start": v(3.6, 171.14) * mm, "end": v(3.6, 171.12) * mm});
            skLineSegment(sketch, "E3712", {"start": v(3.6, 171.12) * mm, "end": v(3.5, 170.9) * mm});
            skLineSegment(sketch, "E3713", {"start": v(3.5, 170.9) * mm, "end": v(3.48, 170.89) * mm});
            skLineSegment(sketch, "E3714", {"start": v(3.48, 170.89) * mm, "end": v(3.46, 170.88) * mm});
            skLineSegment(sketch, "E3715", {"start": v(3.46, 170.88) * mm, "end": v(3.34, 170.8) * mm});
            skLineSegment(sketch, "E3716", {"start": v(3.34, 170.8) * mm, "end": v(3.33, 170.78) * mm});
            skLineSegment(sketch, "E3717", {"start": v(3.33, 170.78) * mm, "end": v(3.31, 170.76) * mm});
            skLineSegment(sketch, "E3718", {"start": v(3.31, 170.76) * mm, "end": v(3.2, 170.48) * mm});
            skLineSegment(sketch, "E3719", {"start": v(3.2, 170.48) * mm, "end": v(3.2, 170.44) * mm});
            skLineSegment(sketch, "E3720", {"start": v(3.2, 170.44) * mm, "end": v(3.2, 170.4) * mm});
            skLineSegment(sketch, "E3721", {"start": v(3.2, 170.4) * mm, "end": v(3.12, 170.21) * mm});
            skLineSegment(sketch, "E3722", {"start": v(3.12, 170.21) * mm, "end": v(3, 170.07) * mm});
            skLineSegment(sketch, "E3723", {"start": v(3, 170.07) * mm, "end": v(3, 170.05) * mm});
            skLineSegment(sketch, "E3724", {"start": v(3, 170.05) * mm, "end": v(2.96, 170) * mm});
            skLineSegment(sketch, "E3725", {"start": v(2.96, 170) * mm, "end": v(2.85, 169.59) * mm});
            skLineSegment(sketch, "E3726", {"start": v(2.85, 169.59) * mm, "end": v(2.85, 169.45) * mm});
            skLineSegment(sketch, "E3727", {"start": v(2.85, 169.45) * mm, "end": v(2.85, 169.32) * mm});
            skLineSegment(sketch, "E3728", {"start": v(2.85, 169.32) * mm, "end": v(2.64, 168.97) * mm});
            skLineSegment(sketch, "E3729", {"start": v(2.64, 168.97) * mm, "end": v(2.6, 168.94) * mm});
            skLineSegment(sketch, "E3730", {"start": v(2.6, 168.94) * mm, "end": v(2.54, 168.9) * mm});
            skLineSegment(sketch, "E3731", {"start": v(2.54, 168.9) * mm, "end": v(2.15, 168.83) * mm});
            skLineSegment(sketch, "E3732", {"start": v(2.15, 168.83) * mm, "end": v(1.69, 168.95) * mm});
            skLineSegment(sketch, "E3733", {"start": v(1.69, 168.95) * mm, "end": v(1.6, 169) * mm});
            skLineSegment(sketch, "E3734", {"start": v(1.6, 169) * mm, "end": v(1.56, 169.02) * mm});
            skLineSegment(sketch, "E3735", {"start": v(1.56, 169.02) * mm, "end": v(1.18, 169.28) * mm});
            skLineSegment(sketch, "E3736", {"start": v(1.18, 169.28) * mm, "end": v(1.14, 169.3) * mm});
            skLineSegment(sketch, "E3737", {"start": v(1.14, 169.3) * mm, "end": v(1.13, 169.3) * mm});
            skLineSegment(sketch, "E3738", {"start": v(1.13, 169.3) * mm, "end": v(1.06, 169.33) * mm});
            skLineSegment(sketch, "E3739", {"start": v(1.06, 169.33) * mm, "end": v(1.05, 169.32) * mm});
            skLineSegment(sketch, "E3740", {"start": v(1.05, 169.32) * mm, "end": v(1.1, 169.23) * mm});
            skLineSegment(sketch, "E3741", {"start": v(1.1, 169.23) * mm, "end": v(1.26, 169.03) * mm});
            skLineSegment(sketch, "E3742", {"start": v(1.26, 169.03) * mm, "end": v(1.3, 168.98) * mm});
            skLineSegment(sketch, "E3743", {"start": v(1.3, 168.98) * mm, "end": v(1.33, 168.95) * mm});
            skLineSegment(sketch, "E3744", {"start": v(1.33, 168.95) * mm, "end": v(1.58, 168.73) * mm});
            skLineSegment(sketch, "E3745", {"start": v(1.58, 168.73) * mm, "end": v(1.6, 168.71) * mm});
            skLineSegment(sketch, "E3746", {"start": v(1.6, 168.71) * mm, "end": v(1.75, 168.62) * mm});
            skLineSegment(sketch, "E3747", {"start": v(1.75, 168.62) * mm, "end": v(2.25, 168.4) * mm});
            skLineSegment(sketch, "E3748", {"start": v(2.25, 168.4) * mm, "end": v(2.8, 168.3) * mm});
            skLineSegment(sketch, "E3749", {"start": v(2.8, 168.3) * mm, "end": v(3.2, 168.42) * mm});
            skLineSegment(sketch, "E3750", {"start": v(3.2, 168.42) * mm, "end": v(3.4, 168.65) * mm});
            skLineSegment(sketch, "E3751", {"start": v(3.4, 168.65) * mm, "end": v(3.42, 168.74) * mm});
            skLineSegment(sketch, "E3752", {"start": v(3.42, 168.74) * mm, "end": v(3.45, 168.83) * mm});
            skLineSegment(sketch, "E3753", {"start": v(3.45, 168.83) * mm, "end": v(3.78, 169.33) * mm});
            skLineSegment(sketch, "E3754", {"start": v(3.78, 169.33) * mm, "end": v(4.33, 170.01) * mm});
            skLineSegment(sketch, "E3755", {"start": v(4.33, 170.01) * mm, "end": v(4.46, 170.2) * mm});
            skLineSegment(sketch, "E3756", {"start": v(4.46, 170.2) * mm, "end": v(4.58, 170.38) * mm});
            skLineSegment(sketch, "E3757", {"start": v(4.58, 170.38) * mm, "end": v(5.13, 171.02) * mm});
            skLineSegment(sketch, "E3758", {"start": v(5.13, 171.02) * mm, "end": v(5.6, 171.7) * mm});
            skLineSegment(sketch, "E3759", {"start": v(5.6, 171.7) * mm, "end": v(5.68, 171.93) * mm});
            skLineSegment(sketch, "E3760", {"start": v(5.68, 171.93) * mm, "end": v(5.73, 172.03) * mm});
            skLineSegment(sketch, "E3761", {"start": v(5.73, 172.03) * mm, "end": v(5.86, 172.7) * mm});
            skLineSegment(sketch, "E3762", {"start": v(5.86, 172.7) * mm, "end": v(5.93, 173.41) * mm});
            skLineSegment(sketch, "E3763", {"start": v(5.93, 173.41) * mm, "end": v(5.95, 173.55) * mm});
            skLineSegment(sketch, "E3764", {"start": v(5.95, 173.55) * mm, "end": v(5.86, 173.58) * mm});
            skLineSegment(sketch, "E3765", {"start": v(5.86, 173.58) * mm, "end": v(5.34, 173.8) * mm});
            skLineSegment(sketch, "E3766", {"start": v(5.34, 173.8) * mm, "end": v(4.8, 174.15) * mm});
            skLineSegment(sketch, "E3767", {"start": v(4.8, 174.15) * mm, "end": v(4.69, 174.24) * mm});
            skLineSegment(sketch, "E3768", {"start": v(4.69, 174.24) * mm, "end": v(4.63, 174.28) * mm});
            skLineSegment(sketch, "E3769", {"start": v(4.63, 174.28) * mm, "end": v(4.1, 174.8) * mm});
            skLineSegment(sketch, "E3770", {"start": v(4.1, 174.8) * mm, "end": v(4.06, 174.86) * mm});
            skLineSegment(sketch, "E3771", {"start": v(4.06, 174.86) * mm, "end": v(3.96, 174.97) * mm});
            skLineSegment(sketch, "E3772", {"start": v(3.96, 174.97) * mm, "end": v(3.71, 175.34) * mm});
            skLineSegment(sketch, "E3773", {"start": v(3.71, 175.34) * mm, "end": v(3.49, 175.72) * mm});
            skLineSegment(sketch, "E3774", {"start": v(3.49, 175.72) * mm, "end": v(3.23, 176.1) * mm});
            skLineSegment(sketch, "E3775", {"start": v(3.23, 176.1) * mm, "end": v(2.93, 176.47) * mm});
            skLineSegment(sketch, "E3776", {"start": v(2.93, 176.47) * mm, "end": v(2.83, 176.58) * mm});
            skLineSegment(sketch, "E3777", {"start": v(2.83, 176.58) * mm, "end": v(2.82, 176.59) * mm});
            skLineSegment(sketch, "E3778", {"start": v(2.82, 176.59) * mm, "end": v(2.75, 176.67) * mm});
            skLineSegment(sketch, "E3779", {"start": v(2.75, 176.67) * mm, "end": v(2.74, 176.68) * mm});
            skLineSegment(sketch, "E3780", {"start": v(2.74, 176.68) * mm, "end": v(2.72, 176.7) * mm});
            skLineSegment(sketch, "E3781", {"start": v(2.72, 176.7) * mm, "end": v(2.56, 176.84) * mm});
            skLineSegment(sketch, "E3782", {"start": v(2.56, 176.84) * mm, "end": v(2.55, 176.85) * mm});
            skLineSegment(sketch, "E3783", {"start": v(2.55, 176.85) * mm, "end": v(2.53, 176.88) * mm});
            skLineSegment(sketch, "E3784", {"start": v(2.53, 176.88) * mm, "end": v(2.47, 176.93) * mm});
            skLineSegment(sketch, "E3785", {"start": v(2.47, 176.93) * mm, "end": v(2.25, 177.08) * mm});
            skLineSegment(sketch, "E3786", {"start": v(2.25, 177.08) * mm, "end": v(2.09, 177.17) * mm});
            skLineSegment(sketch, "E3787", {"start": v(2.09, 177.17) * mm, "end": v(2.06, 177.19) * mm});
            skLineSegment(sketch, "E3788", {"start": v(2.06, 177.19) * mm, "end": v(2.05, 177.2) * mm});
            skLineSegment(sketch, "E3789", {"start": v(2.05, 177.2) * mm, "end": v(2, 177.24) * mm});
            skLineSegment(sketch, "E3790", {"start": v(2, 177.24) * mm, "end": v(2.2, 177.23) * mm});
            skLineSegment(sketch, "E3791", {"start": v(2.2, 177.23) * mm, "end": v(2.26, 177.2) * mm});
            skLineSegment(sketch, "E3792", {"start": v(2.26, 177.2) * mm, "end": v(2.33, 177.18) * mm});
            skLineSegment(sketch, "E3793", {"start": v(2.33, 177.18) * mm, "end": v(2.74, 176.95) * mm});
            skLineSegment(sketch, "E3794", {"start": v(2.74, 176.95) * mm, "end": v(3.3, 176.56) * mm});
            skLineSegment(sketch, "E3795", {"start": v(3.3, 176.56) * mm, "end": v(3.42, 176.45) * mm});
            skLineSegment(sketch, "E3796", {"start": v(3.42, 176.45) * mm, "end": v(3.5, 176.38) * mm});
            skLineSegment(sketch, "E3797", {"start": v(3.5, 176.38) * mm, "end": v(4.15, 175.7) * mm});
            skLineSegment(sketch, "E3798", {"start": v(4.15, 175.7) * mm, "end": v(4.2, 175.64) * mm});
            skLineSegment(sketch, "E3799", {"start": v(4.2, 175.64) * mm, "end": v(4.3, 175.52) * mm});
            skLineSegment(sketch, "E3800", {"start": v(4.3, 175.52) * mm, "end": v(5.1, 174.44) * mm});
            skLineSegment(sketch, "E3801", {"start": v(5.1, 174.44) * mm, "end": v(5.2, 174.34) * mm});
            skLineSegment(sketch, "E3802", {"start": v(5.2, 174.34) * mm, "end": v(5.22, 174.31) * mm});
            skLineSegment(sketch, "E3803", {"start": v(5.22, 174.31) * mm, "end": v(5.48, 174.08) * mm});
            skLineSegment(sketch, "E3804", {"start": v(5.48, 174.08) * mm, "end": v(5.52, 174.05) * mm});
            skLineSegment(sketch, "E3805", {"start": v(5.52, 174.05) * mm, "end": v(5.54, 174.04) * mm});
            skLineSegment(sketch, "E3806", {"start": v(5.54, 174.04) * mm, "end": v(5.79, 173.87) * mm});
            skLineSegment(sketch, "E3807", {"start": v(5.79, 173.87) * mm, "end": v(5.8, 173.85) * mm});
            skLineSegment(sketch, "E3808", {"start": v(5.8, 173.85) * mm, "end": v(5.85, 173.83) * mm});
            skLineSegment(sketch, "E3809", {"start": v(5.85, 173.83) * mm, "end": v(6.17, 173.67) * mm});
            skLineSegment(sketch, "E3810", {"start": v(6.17, 173.67) * mm, "end": v(6.19, 173.66) * mm});
            skLineSegment(sketch, "E3811", {"start": v(6.19, 173.66) * mm, "end": v(6.37, 173.59) * mm});
            skLineSegment(sketch, "E3812", {"start": v(6.37, 173.59) * mm, "end": v(6.93, 173.42) * mm});
            skLineSegment(sketch, "E3813", {"start": v(6.93, 173.42) * mm, "end": v(7.6, 173.32) * mm});
            skLineSegment(sketch, "E3814", {"start": v(7.6, 173.32) * mm, "end": v(8.16, 173.31) * mm});
            skLineSegment(sketch, "E3815", {"start": v(8.16, 173.31) * mm, "end": v(8.46, 173.35) * mm});
            skLineSegment(sketch, "E3816", {"start": v(8.46, 173.35) * mm, "end": v(8.56, 173.38) * mm});
            skLineSegment(sketch, "E3817", {"start": v(8.56, 173.38) * mm, "end": v(8.7, 173.42) * mm});
            skLineSegment(sketch, "E3818", {"start": v(8.7, 173.42) * mm, "end": v(9.1, 173.61) * mm});
            skLineSegment(sketch, "E3819", {"start": v(9.1, 173.61) * mm, "end": v(9.25, 173.81) * mm});
            skLineSegment(sketch, "E3820", {"start": v(9.25, 173.81) * mm, "end": v(9.24, 173.85) * mm});
            skLineSegment(sketch, "E3821", {"start": v(9.24, 173.85) * mm, "end": v(9.25, 173.84) * mm});
            skLineSegment(sketch, "E3822", {"start": v(9.25, 173.84) * mm, "end": v(9.38, 173.73) * mm});
            skLineSegment(sketch, "E3823", {"start": v(9.38, 173.73) * mm, "end": v(9.4, 173.71) * mm});
            skLineSegment(sketch, "E3824", {"start": v(9.4, 173.71) * mm, "end": v(9.42, 173.7) * mm});
            skLineSegment(sketch, "E3825", {"start": v(9.42, 173.7) * mm, "end": v(9.61, 173.5) * mm});
            skLineSegment(sketch, "E3826", {"start": v(9.61, 173.5) * mm, "end": v(9.63, 173.49) * mm});
            skLineSegment(sketch, "E3827", {"start": v(9.63, 173.49) * mm, "end": v(9.65, 173.49) * mm});
            skLineSegment(sketch, "E3828", {"start": v(9.65, 173.49) * mm, "end": v(9.72, 173.45) * mm});
            skLineSegment(sketch, "E3829", {"start": v(9.72, 173.45) * mm, "end": v(9.72, 173.45) * mm});
            skLineSegment(sketch, "E3830", {"start": v(9.72, 173.45) * mm, "end": v(9.76, 173.43) * mm});
            skLineSegment(sketch, "E3831", {"start": v(9.76, 173.43) * mm, "end": v(10, 173.4) * mm});
            skLineSegment(sketch, "E3832", {"start": v(10, 173.4) * mm, "end": v(10.01, 173.39) * mm});
            skLineSegment(sketch, "E3833", {"start": v(10.01, 173.39) * mm, "end": v(10.02, 173.38) * mm});
            skLineSegment(sketch, "E3834", {"start": v(10.02, 173.38) * mm, "end": v(9.97, 173.21) * mm});
            skLineSegment(sketch, "E3835", {"start": v(9.97, 173.21) * mm, "end": v(9.95, 173.2) * mm});
            skLineSegment(sketch, "E3836", {"start": v(9.95, 173.2) * mm, "end": v(10, 173.08) * mm});
            skLineSegment(sketch, "E3837", {"start": v(10, 173.08) * mm, "end": v(10.01, 173.06) * mm});
            skLineSegment(sketch, "E3838", {"start": v(10.01, 173.06) * mm, "end": v(10.03, 173.03) * mm});
            skLineSegment(sketch, "E3839", {"start": v(10.03, 173.03) * mm, "end": v(10.25, 172.95) * mm});
            skLineSegment(sketch, "E3840", {"start": v(10.25, 172.95) * mm, "end": v(10.45, 172.92) * mm});
            skLineSegment(sketch, "E3841", {"start": v(10.45, 172.92) * mm, "end": v(10.67, 172.91) * mm});
            skLineSegment(sketch, "E3842", {"start": v(10.67, 172.91) * mm, "end": v(10.88, 172.96) * mm});
            skLineSegment(sketch, "E3843", {"start": v(10.88, 172.96) * mm, "end": v(10.88, 172.98) * mm});
            skLineSegment(sketch, "E3844", {"start": v(10.88, 172.98) * mm, "end": v(10.86, 173.07) * mm});
            skLineSegment(sketch, "E3845", {"start": v(10.86, 173.07) * mm, "end": v(10.76, 173.28) * mm});
            skLineSegment(sketch, "E3846", {"start": v(10.76, 173.28) * mm, "end": v(10.6, 173.55) * mm});
            skLineSegment(sketch, "E3847", {"start": v(10.6, 173.55) * mm, "end": v(10.53, 173.64) * mm});
            skLineSegment(sketch, "E3848", {"start": v(10.53, 173.64) * mm, "end": v(10.51, 173.68) * mm});
            skLineSegment(sketch, "E3849", {"start": v(10.51, 173.68) * mm, "end": v(10.34, 173.83) * mm});
            skLineSegment(sketch, "E3850", {"start": v(10.34, 173.83) * mm, "end": v(9.96, 174.12) * mm});
            skLineSegment(sketch, "E3851", {"start": v(9.96, 174.12) * mm, "end": v(9.56, 174.41) * mm});
            skLineSegment(sketch, "E3852", {"start": v(9.56, 174.41) * mm, "end": v(9.35, 174.57) * mm});
            skLineSegment(sketch, "E3853", {"start": v(9.35, 174.57) * mm, "end": v(9.3, 174.6) * mm});
            skLineSegment(sketch, "E3854", {"start": v(9.3, 174.6) * mm, "end": v(9.26, 174.64) * mm});
            skLineSegment(sketch, "E3855", {"start": v(9.26, 174.64) * mm, "end": v(9.06, 174.63) * mm});
            skLineSegment(sketch, "E3856", {"start": v(9.06, 174.63) * mm, "end": v(8.97, 174.45) * mm});
            skLineSegment(sketch, "E3857", {"start": v(8.97, 174.45) * mm, "end": v(8.98, 174.4) * mm});
            skLineSegment(sketch, "E3858", {"start": v(8.98, 174.4) * mm, "end": v(8.98, 174.31) * mm});
            skLineSegment(sketch, "E3859", {"start": v(8.98, 174.31) * mm, "end": v(9.08, 174.09) * mm});
            skLineSegment(sketch, "E3860", {"start": v(9.08, 174.09) * mm, "end": v(9.1, 174.06) * mm});
            skLineSegment(sketch, "E3861", {"start": v(9.1, 174.06) * mm, "end": v(9.05, 174.1) * mm});
            skLineSegment(sketch, "E3862", {"start": v(9.05, 174.1) * mm, "end": v(8.74, 174.26) * mm});
            skLineSegment(sketch, "E3863", {"start": v(8.74, 174.26) * mm, "end": v(8.33, 174.38) * mm});
            skLineSegment(sketch, "E3864", {"start": v(8.33, 174.38) * mm, "end": v(8.25, 174.4) * mm});
            skLineSegment(sketch, "E3865", {"start": v(8.25, 174.4) * mm, "end": v(8.12, 174.42) * mm});
            skLineSegment(sketch, "E3866", {"start": v(8.12, 174.42) * mm, "end": v(7.75, 174.51) * mm});
            skLineSegment(sketch, "E3867", {"start": v(7.75, 174.51) * mm, "end": v(7.43, 174.64) * mm});
            skLineSegment(sketch, "E3868", {"start": v(7.43, 174.64) * mm, "end": v(7.19, 174.8) * mm});
            skLineSegment(sketch, "E3869", {"start": v(7.19, 174.8) * mm, "end": v(6.99, 174.96) * mm});
            skLineSegment(sketch, "E3870", {"start": v(6.99, 174.96) * mm, "end": v(6.92, 175.02) * mm});
            skLineSegment(sketch, "E3871", {"start": v(6.92, 175.02) * mm, "end": v(6.9, 175.03) * mm});
            skLineSegment(sketch, "E3872", {"start": v(6.9, 175.03) * mm, "end": v(6.85, 175.12) * mm});
            skLineSegment(sketch, "E3873", {"start": v(6.85, 175.12) * mm, "end": v(7, 175.37) * mm});
            skLineSegment(sketch, "E3874", {"start": v(7, 175.37) * mm, "end": v(7.36, 175.95) * mm});
            skLineSegment(sketch, "E3875", {"start": v(7.36, 175.95) * mm, "end": v(7.86, 176.66) * mm});
            skLineSegment(sketch, "E3876", {"start": v(7.86, 176.66) * mm, "end": v(8.23, 177.13) * mm});
            skLineSegment(sketch, "E3877", {"start": v(8.23, 177.13) * mm, "end": v(8.37, 177.27) * mm});
            skLineSegment(sketch, "E3878", {"start": v(8.37, 177.27) * mm, "end": v(8.53, 177.43) * mm});
            skLineSegment(sketch, "E3879", {"start": v(8.53, 177.43) * mm, "end": v(9.26, 178.1) * mm});
            skLineSegment(sketch, "E3880", {"start": v(9.26, 178.1) * mm, "end": v(9.74, 178.65) * mm});
            skLineSegment(sketch, "E3881", {"start": v(9.74, 178.65) * mm, "end": v(9.76, 178.75) * mm});
            skLineSegment(sketch, "E3882", {"start": v(9.76, 178.75) * mm, "end": v(9.8, 178.85) * mm});
            skLineSegment(sketch, "E3883", {"start": v(9.8, 178.85) * mm, "end": v(9.69, 179.37) * mm});
            skLineSegment(sketch, "E3884", {"start": v(9.69, 179.37) * mm, "end": v(9.2, 180.43) * mm});
            skLineSegment(sketch, "E3885", {"start": v(9.2, 180.43) * mm, "end": v(8.2, 181.69) * mm});
            skLineSegment(sketch, "E3886", {"start": v(8.2, 181.69) * mm, "end": v(7.05, 182.63) * mm});
            skLineSegment(sketch, "E3887", {"start": v(7.05, 182.63) * mm, "end": v(6.62, 182.86) * mm});
            skLineSegment(sketch, "E3888", {"start": v(6.62, 182.86) * mm, "end": v(6.2, 183.1) * mm});
            skLineSegment(sketch, "E3889", {"start": v(6.2, 183.1) * mm, "end": v(4.86, 183.67) * mm});
            skLineSegment(sketch, "E3890", {"start": v(4.86, 183.67) * mm, "end": v(3.39, 184.07) * mm});
            skLineSegment(sketch, "E3891", {"start": v(3.39, 184.07) * mm, "end": v(2.27, 184.17) * mm});
            skLineSegment(sketch, "E3892", {"start": v(2.27, 184.17) * mm, "end": v(1.71, 184.14) * mm});
            skLineSegment(sketch, "E3893", {"start": v(1.71, 184.14) * mm, "end": v(1.55, 184.1) * mm});
            skLineSegment(sketch, "E3894", {"start": v(1.55, 184.1) * mm, "end": v(1.38, 184.05) * mm});
            skLineSegment(sketch, "E3895", {"start": v(1.38, 184.05) * mm, "end": v(0.91, 183.73) * mm});
            skLineSegment(sketch, "E3896", {"start": v(0.91, 183.73) * mm, "end": v(0.76, 183.3) * mm});
            skLineSegment(sketch, "E3897", {"start": v(0.76, 183.3) * mm, "end": v(0.76, 183.2) * mm});
            skLineSegment(sketch, "E3898", {"start": v(0.76, 183.2) * mm, "end": v(0.75, 183.1) * mm});
            skLineSegment(sketch, "E3899", {"start": v(0.75, 183.1) * mm, "end": v(0.69, 182.35) * mm});
            skLineSegment(sketch, "E3900", {"start": v(0.69, 182.35) * mm, "end": v(0.56, 181.45) * mm});
            skLineSegment(sketch, "E3901", {"start": v(0.56, 181.45) * mm, "end": v(0.52, 181.28) * mm});
            skLineSegment(sketch, "E3902", {"start": v(0.52, 181.28) * mm, "end": v(0.48, 181.1) * mm});
            skLineSegment(sketch, "E3903", {"start": v(0.48, 181.1) * mm, "end": v(0.34, 180.52) * mm});
            skLineSegment(sketch, "E3904", {"start": v(0.34, 180.52) * mm, "end": v(0.28, 180.23) * mm});
            skLineSegment(sketch, "E3905", {"start": v(0.28, 180.23) * mm, "end": v(0.28, 180.13) * mm});
            skLineSegment(sketch, "E3906", {"start": v(0.28, 180.13) * mm, "end": v(0.28, 180.1) * mm});
            skLineSegment(sketch, "E3907", {"start": v(0.28, 180.1) * mm, "end": v(0.47, 179.76) * mm});
            skLineSegment(sketch, "E3908", {"start": v(0.47, 179.76) * mm, "end": v(0.5, 179.72) * mm});
            skLineSegment(sketch, "E3909", {"start": v(0.5, 179.72) * mm, "end": v(0.54, 179.68) * mm});
            skLineSegment(sketch, "E3910", {"start": v(0.54, 179.68) * mm, "end": v(1.02, 179.27) * mm});
            skLineSegment(sketch, "E3911", {"start": v(1.02, 179.27) * mm, "end": v(1.07, 179.22) * mm});
            skLineSegment(sketch, "E3912", {"start": v(1.07, 179.22) * mm, "end": v(1.16, 179.15) * mm});
            skLineSegment(sketch, "E3913", {"start": v(1.16, 179.15) * mm, "end": v(1.66, 178.73) * mm});
            skLineSegment(sketch, "E3914", {"start": v(1.66, 178.73) * mm, "end": v(2.1, 178.27) * mm});
            skLineSegment(sketch, "E3915", {"start": v(2.1, 178.27) * mm, "end": v(2.16, 178.17) * mm});
            skLineSegment(sketch, "E3916", {"start": v(2.16, 178.17) * mm, "end": v(2.19, 178.13) * mm});
            skLineSegment(sketch, "E3917", {"start": v(2.19, 178.13) * mm, "end": v(2.25, 177.98) * mm});
            skLineSegment(sketch, "E3918", {"start": v(2.25, 177.98) * mm, "end": v(2.17, 177.94) * mm});
            skLineSegment(sketch, "E3919", {"start": v(2.17, 177.94) * mm, "end": v(1.99, 178) * mm});
            skLineSegment(sketch, "E3920", {"start": v(1.99, 178) * mm, "end": v(1.84, 178.09) * mm});
            skLineSegment(sketch, "E3921", {"start": v(1.84, 178.09) * mm, "end": v(1.8, 178.12) * mm});
            skLineSegment(sketch, "E3922", {"start": v(1.8, 178.12) * mm, "end": v(1.73, 178.16) * mm});
            skLineSegment(sketch, "E3923", {"start": v(1.73, 178.16) * mm, "end": v(1.07, 178.57) * mm});
            skLineSegment(sketch, "E3924", {"start": v(1.07, 178.57) * mm, "end": v(0.18, 179.03) * mm});
            skLineSegment(sketch, "E3925", {"start": v(0.18, 179.03) * mm, "end": v(0, 179.1) * mm});
            skLineSegment(sketch, "E3926", {"start": v(0, 179.1) * mm, "end": v(-0.06, 179.12) * mm});
            skLineSegment(sketch, "E3927", {"start": v(-0.06, 179.12) * mm, "end": v(-0.7, 179.34) * mm});
            skLineSegment(sketch, "E3928", {"start": v(-0.7, 179.34) * mm, "end": v(-0.76, 179.36) * mm});
            skLineSegment(sketch, "E3929", {"start": v(-0.76, 179.36) * mm, "end": v(-0.99, 179.44) * mm});
            skLineSegment(sketch, "E3930", {"start": v(-0.99, 179.44) * mm, "end": v(-1.7, 179.6) * mm});
            skLineSegment(sketch, "E3931", {"start": v(-1.7, 179.6) * mm, "end": v(-2.48, 179.63) * mm});
            skLineSegment(sketch, "E3932", {"start": v(-2.48, 179.63) * mm, "end": v(-3.12, 179.48) * mm});
            skLineSegment(sketch, "E3933", {"start": v(-3.12, 179.48) * mm, "end": v(-3.54, 179.27) * mm});
            skLineSegment(sketch, "E3934", {"start": v(-3.54, 179.27) * mm, "end": v(-3.66, 179.18) * mm});
            skLineSegment(sketch, "E3935", {"start": v(-3.66, 179.18) * mm, "end": v(-3.77, 179.09) * mm});
            skLineSegment(sketch, "E3936", {"start": v(-3.77, 179.09) * mm, "end": v(-3.9, 178.57) * mm});
            skLineSegment(sketch, "E3937", {"start": v(-3.9, 178.57) * mm, "end": v(-3.65, 178.1) * mm});
            skLineSegment(sketch, "E3938", {"start": v(-3.65, 178.1) * mm, "end": v(-3.57, 178.02) * mm});
            skSolve(sketch);
        }
        {
            var Q0;
            Q0=makeQuery(id+"F0.imprint","IMPRINT",FACE,{"disambiguationData":[TD([[makeQuery(id+"F0.imprint","IMPRINT",EDGE,{"derivedFrom":sQuery(id+"F0.wireOp",EDGE,"E0")}),-1.0]])]});
            extrude(context, id + "F2", {"entities" : qUnion([Q0]), "oppositeDirection" : true, "depth" : 2 * mm, "offsetDistance" : 25 * mm});
        }
        {
            var Q0;
            Q0=makeQuery(id+"F1.imprint","IMPRINT",FACE,{"disambiguationData":[TD([[makeQuery(id+"F1.imprint","IMPRINT",EDGE,{"derivedFrom":sQuery(id+"F1.wireOp",EDGE,"E480")}),1.0]])]});
            var Q1;
            Q1=makeQuery(id+"F1.imprint","IMPRINT",FACE,{"disambiguationData":[TD([[makeQuery(id+"F1.imprint","IMPRINT",EDGE,{"derivedFrom":sQuery(id+"F1.wireOp",EDGE,"E585")}),1.0]])]});
            var Q2;
            Q2=makeQuery(id+"F1.imprint","IMPRINT",FACE,{"disambiguationData":[TD([[makeQuery(id+"F1.imprint","IMPRINT",EDGE,{"derivedFrom":sQuery(id+"F1.wireOp",EDGE,"E691")}),1.0]])]});
            var Q3;
            Q3=makeQuery(id+"F1.imprint","IMPRINT",FACE,{"disambiguationData":[TD([[makeQuery(id+"F1.imprint","IMPRINT",EDGE,{"derivedFrom":sQuery(id+"F1.wireOp",EDGE,"E296")}),1.0]])]});
            var Q4;
            Q4=makeQuery(id+"F1.imprint","IMPRINT",FACE,{"disambiguationData":[TD([[makeQuery(id+"F1.imprint","IMPRINT",EDGE,{"derivedFrom":sQuery(id+"F1.wireOp",EDGE,"E178")}),1.0]])]});
            var Q5;
            Q5=makeQuery(id+"F1.imprint","IMPRINT",FACE,{"disambiguationData":[TD([[makeQuery(id+"F1.imprint","IMPRINT",EDGE,{"derivedFrom":sQuery(id+"F1.wireOp",EDGE,"E233")}),1.0]])]});
            var Q6;
            Q6=makeQuery(id+"F1.imprint","IMPRINT",FACE,{"disambiguationData":[TD([[makeQuery(id+"F1.imprint","IMPRINT",EDGE,{"derivedFrom":sQuery(id+"F1.wireOp",EDGE,"E249")}),1.0]])]});
            var Q7;
            Q7=makeQuery(id+"F1.imprint","IMPRINT",FACE,{"disambiguationData":[TD([[makeQuery(id+"F1.imprint","IMPRINT",EDGE,{"derivedFrom":sQuery(id+"F1.wireOp",EDGE,"E350")}),1.0]])]});
            var Q8;
            Q8=makeQuery(id+"F1.imprint","IMPRINT",FACE,{"disambiguationData":[TD([[makeQuery(id+"F1.imprint","IMPRINT",EDGE,{"derivedFrom":sQuery(id+"F1.wireOp",EDGE,"E725")}),1.0]])]});
            var Q9;
            Q9=makeQuery(id+"F1.imprint","IMPRINT",FACE,{"disambiguationData":[TD([[makeQuery(id+"F1.imprint","IMPRINT",EDGE,{"derivedFrom":sQuery(id+"F1.wireOp",EDGE,"E937")}),1.0]])]});
            var Q10;
            Q10=makeQuery(id+"F1.imprint","IMPRINT",FACE,{"disambiguationData":[TD([[makeQuery(id+"F1.imprint","IMPRINT",EDGE,{"derivedFrom":sQuery(id+"F1.wireOp",EDGE,"E953")}),1.0]])]});
            var Q11;
            Q11=makeQuery(id+"F1.imprint","IMPRINT",FACE,{"disambiguationData":[TD([[makeQuery(id+"F1.imprint","IMPRINT",EDGE,{"derivedFrom":sQuery(id+"F1.wireOp",EDGE,"E897")}),1.0]])]});
            var Q12;
            Q12=makeQuery(id+"F1.imprint","IMPRINT",FACE,{"disambiguationData":[TD([[makeQuery(id+"F1.imprint","IMPRINT",EDGE,{"derivedFrom":sQuery(id+"F1.wireOp",EDGE,"E746")}),1.0]])]});
            var Q13;
            Q13=makeQuery(id+"F1.imprint","IMPRINT",FACE,{"disambiguationData":[TD([[makeQuery(id+"F1.imprint","IMPRINT",EDGE,{"derivedFrom":sQuery(id+"F1.wireOp",EDGE,"E793")}),1.0]])]});
            var Q14;
            Q14=makeQuery(id+"F1.imprint","IMPRINT",FACE,{"disambiguationData":[TD([[makeQuery(id+"F1.imprint","IMPRINT",EDGE,{"derivedFrom":sQuery(id+"F1.wireOp",EDGE,"E998")}),-1.0]])]});
            var Q15;
            Q15=makeQuery(id+"F1.imprint","IMPRINT",FACE,{"disambiguationData":[TD([[makeQuery(id+"F1.imprint","IMPRINT",EDGE,{"derivedFrom":sQuery(id+"F1.wireOp",EDGE,"E8")}),1.0]])]});
            var Q16;
            Q16=makeQuery(id+"F1.imprint","IMPRINT",FACE,{"disambiguationData":[TD([[makeQuery(id+"F1.imprint","IMPRINT",EDGE,{"derivedFrom":sQuery(id+"F1.wireOp",EDGE,"E20")}),1.0]])]});
            var Q17;
            Q17=makeQuery(id+"F1.imprint","IMPRINT",FACE,{"disambiguationData":[TD([[makeQuery(id+"F1.imprint","IMPRINT",EDGE,{"derivedFrom":sQuery(id+"F1.wireOp",EDGE,"E32")}),1.0]])]});
            var Q18;
            Q18=makeQuery(id+"F1.imprint","IMPRINT",FACE,{"disambiguationData":[TD([[makeQuery(id+"F1.imprint","IMPRINT",EDGE,{"derivedFrom":sQuery(id+"F1.wireOp",EDGE,"E76")}),1.0]])]});
            var Q19;
            Q19=makeQuery(id+"F1.imprint","IMPRINT",FACE,{"disambiguationData":[TD([[makeQuery(id+"F1.imprint","IMPRINT",EDGE,{"derivedFrom":sQuery(id+"F1.wireOp",EDGE,"E44")}),1.0]])]});
            var Q20;
            Q20=makeQuery(id+"F1.imprint","IMPRINT",FACE,{"disambiguationData":[TD([[makeQuery(id+"F1.imprint","IMPRINT",EDGE,{"derivedFrom":sQuery(id+"F1.wireOp",EDGE,"E89")}),1.0]])]});
            var Q21;
            Q21=makeQuery(id+"F1.imprint","IMPRINT",FACE,{"disambiguationData":[TD([[makeQuery(id+"F1.imprint","IMPRINT",EDGE,{"derivedFrom":sQuery(id+"F1.wireOp",EDGE,"E106")}),1.0]])]});
            var Q22;
            Q22=makeQuery(id+"F1.imprint","IMPRINT",FACE,{"disambiguationData":[TD([[makeQuery(id+"F1.imprint","IMPRINT",EDGE,{"derivedFrom":sQuery(id+"F1.wireOp",EDGE,"E100")}),1.0]])]});
            var Q23;
            Q23=makeQuery(id+"F1.imprint","IMPRINT",FACE,{"disambiguationData":[TD([[makeQuery(id+"F1.imprint","IMPRINT",EDGE,{"derivedFrom":sQuery(id+"F1.wireOp",EDGE,"E118")}),1.0]])]});
            var Q24;
            Q24=makeQuery(id+"F1.imprint","IMPRINT",FACE,{"disambiguationData":[TD([[makeQuery(id+"F1.imprint","IMPRINT",EDGE,{"derivedFrom":sQuery(id+"F1.wireOp",EDGE,"E122")}),1.0]])]});
            var Q25;
            Q25=makeQuery(id+"F1.imprint","IMPRINT",FACE,{"disambiguationData":[TD([[makeQuery(id+"F1.imprint","IMPRINT",EDGE,{"derivedFrom":sQuery(id+"F1.wireOp",EDGE,"E132")}),1.0]])]});
            var Q26;
            Q26=makeQuery(id+"F1.imprint","IMPRINT",FACE,{"disambiguationData":[TD([[makeQuery(id+"F1.imprint","IMPRINT",EDGE,{"derivedFrom":sQuery(id+"F1.wireOp",EDGE,"E2088")}),1.0]])]});
            var Q27;
            Q27=makeQuery(id+"F1.imprint","IMPRINT",FACE,{"disambiguationData":[TD([[makeQuery(id+"F1.imprint","IMPRINT",EDGE,{"derivedFrom":sQuery(id+"F1.wireOp",EDGE,"E1118")}),-1.0]])]});
            var Q28;
            Q28=makeQuery(id+"F1.imprint","IMPRINT",FACE,{"disambiguationData":[TD([[makeQuery(id+"F1.imprint","IMPRINT",EDGE,{"derivedFrom":sQuery(id+"F1.wireOp",EDGE,"E1126")}),-1.0]])]});
            var Q29;
            Q29=makeQuery(id+"F1.imprint","IMPRINT",FACE,{"disambiguationData":[TD([[makeQuery(id+"F1.imprint","IMPRINT",EDGE,{"derivedFrom":sQuery(id+"F1.wireOp",EDGE,"E1408")}),1.0]])]});
            var Q30;
            Q30=makeQuery(id+"F1.imprint","IMPRINT",FACE,{"disambiguationData":[TD([[makeQuery(id+"F1.imprint","IMPRINT",EDGE,{"derivedFrom":sQuery(id+"F1.wireOp",EDGE,"E1808")}),1.0]])]});
            var Q31;
            Q31=makeQuery(id+"F1.imprint","IMPRINT",FACE,{"disambiguationData":[TD([[makeQuery(id+"F1.imprint","IMPRINT",EDGE,{"derivedFrom":sQuery(id+"F1.wireOp",EDGE,"E1891")}),1.0]])]});
            var Q32;
            Q32=makeQuery(id+"F1.imprint","IMPRINT",FACE,{"disambiguationData":[TD([[makeQuery(id+"F1.imprint","IMPRINT",EDGE,{"derivedFrom":sQuery(id+"F1.wireOp",EDGE,"E1214")}),1.0]])]});
            var Q33;
            Q33=makeQuery(id+"F1.imprint","IMPRINT",FACE,{"disambiguationData":[TD([[makeQuery(id+"F1.imprint","IMPRINT",EDGE,{"derivedFrom":sQuery(id+"F1.wireOp",EDGE,"E2363")}),1.0]])]});
            var Q34;
            Q34=makeQuery(id+"F1.imprint","IMPRINT",FACE,{"disambiguationData":[TD([[makeQuery(id+"F1.imprint","IMPRINT",EDGE,{"derivedFrom":sQuery(id+"F1.wireOp",EDGE,"E1153")}),1.0]])]});
            var Q35;
            Q35=makeQuery(id+"F1.imprint","IMPRINT",FACE,{"disambiguationData":[TD([[makeQuery(id+"F1.imprint","IMPRINT",EDGE,{"derivedFrom":sQuery(id+"F1.wireOp",EDGE,"E1351")}),1.0]])]});
            var Q36;
            Q36=makeQuery(id+"F1.imprint","IMPRINT",FACE,{"disambiguationData":[TD([[makeQuery(id+"F1.imprint","IMPRINT",EDGE,{"derivedFrom":sQuery(id+"F1.wireOp",EDGE,"E1684")}),1.0]])]});
            var Q37;
            Q37=makeQuery(id+"F1.imprint","IMPRINT",FACE,{"disambiguationData":[TD([[makeQuery(id+"F1.imprint","IMPRINT",EDGE,{"derivedFrom":sQuery(id+"F1.wireOp",EDGE,"E1138")}),1.0]])]});
            var Q38;
            Q38=makeQuery(id+"F1.imprint","IMPRINT",FACE,{"disambiguationData":[TD([[makeQuery(id+"F1.imprint","IMPRINT",EDGE,{"derivedFrom":sQuery(id+"F1.wireOp",EDGE,"E1202")}),1.0]])]});
            var Q39;
            Q39=makeQuery(id+"F1.imprint","IMPRINT",FACE,{"disambiguationData":[TD([[makeQuery(id+"F1.imprint","IMPRINT",EDGE,{"derivedFrom":sQuery(id+"F1.wireOp",EDGE,"E1188")}),1.0]])]});
            var Q40;
            Q40=makeQuery(id+"F1.imprint","IMPRINT",FACE,{"disambiguationData":[TD([[makeQuery(id+"F1.imprint","IMPRINT",EDGE,{"derivedFrom":sQuery(id+"F1.wireOp",EDGE,"E3544")}),1.0]])]});
            var Q41;
            Q41=makeQuery(id+"F1.imprint","IMPRINT",FACE,{"disambiguationData":[TD([[makeQuery(id+"F1.imprint","IMPRINT",EDGE,{"derivedFrom":sQuery(id+"F1.wireOp",EDGE,"E1778")}),1.0]])]});
            var Q42;
            Q42=makeQuery(id+"F1.imprint","IMPRINT",FACE,{"disambiguationData":[TD([[makeQuery(id+"F1.imprint","IMPRINT",EDGE,{"derivedFrom":sQuery(id+"F1.wireOp",EDGE,"E1792")}),1.0]])]});
            var Q43;
            Q43=makeQuery(id+"F1.imprint","IMPRINT",FACE,{"disambiguationData":[TD([[makeQuery(id+"F1.imprint","IMPRINT",EDGE,{"derivedFrom":sQuery(id+"F1.wireOp",EDGE,"E1706")}),1.0]])]});
            extrude(context, id + "F3", {"entities" : qUnion([Q0, Q1, Q2, Q3, Q4, Q5, Q6, Q7, Q8, Q9, Q10, Q11, Q12, Q13, Q14, Q15, Q16, Q17, Q18, Q19, Q20, Q21, Q22, Q23, Q24, Q25, Q26, Q27, Q28, Q29, Q30, Q31, Q32, Q33, Q34, Q35, Q36, Q37, Q38, Q39, Q40, Q41, Q42, Q43]), "operationType" : NewBodyOperationType.REMOVE, "endBound" : BoundingType.THROUGH_ALL, "oppositeDirection" : true, "depth" : 25 * mm, "offsetDistance" : 25 * mm});
        }
        {
            var Q0;
            Q0=makeQuery(id+"F3.boolean.opBoolean","SPLIT",BODY,{"disambiguationData":[OD(0.0)],"derivedFrom":makeQuery(id+"F2.opExtrude","SWEPT_BODY",BODY,{"disambiguationData":[OSD([sQuery(id+"F0.wireOp",EDGE,"E0"),sQuery(id+"F0.wireOp",EDGE,"E1"),sQuery(id+"F0.wireOp",EDGE,"E2"),sQuery(id+"F0.wireOp",EDGE,"E3"),sQuery(id+"F0.wireOp",EDGE,"E4"),sQuery(id+"F0.wireOp",EDGE,"E5"),sQuery(id+"F0.wireOp",EDGE,"E6"),sQuery(id+"F0.wireOp",EDGE,"E7")])]})});
            var Q1;
            Q1=makeQuery(id+"F3.boolean.opBoolean","SPLIT",BODY,{"disambiguationData":[OD(2.0)],"derivedFrom":makeQuery(id+"F2.opExtrude","SWEPT_BODY",BODY,{"disambiguationData":[OSD([sQuery(id+"F0.wireOp",EDGE,"E0"),sQuery(id+"F0.wireOp",EDGE,"E1"),sQuery(id+"F0.wireOp",EDGE,"E2"),sQuery(id+"F0.wireOp",EDGE,"E3"),sQuery(id+"F0.wireOp",EDGE,"E4"),sQuery(id+"F0.wireOp",EDGE,"E5"),sQuery(id+"F0.wireOp",EDGE,"E6"),sQuery(id+"F0.wireOp",EDGE,"E7")])]})});
            var Q2;
            Q2=makeQuery(id+"F3.boolean.opBoolean","SPLIT",BODY,{"disambiguationData":[OD(3.0)],"derivedFrom":makeQuery(id+"F2.opExtrude","SWEPT_BODY",BODY,{"disambiguationData":[OSD([sQuery(id+"F0.wireOp",EDGE,"E0"),sQuery(id+"F0.wireOp",EDGE,"E1"),sQuery(id+"F0.wireOp",EDGE,"E2"),sQuery(id+"F0.wireOp",EDGE,"E3"),sQuery(id+"F0.wireOp",EDGE,"E4"),sQuery(id+"F0.wireOp",EDGE,"E5"),sQuery(id+"F0.wireOp",EDGE,"E6"),sQuery(id+"F0.wireOp",EDGE,"E7")])]})});
            var Q3;
            Q3=makeQuery(id+"F3.boolean.opBoolean","SPLIT",BODY,{"disambiguationData":[OD(4.0)],"derivedFrom":makeQuery(id+"F2.opExtrude","SWEPT_BODY",BODY,{"disambiguationData":[OSD([sQuery(id+"F0.wireOp",EDGE,"E0"),sQuery(id+"F0.wireOp",EDGE,"E1"),sQuery(id+"F0.wireOp",EDGE,"E2"),sQuery(id+"F0.wireOp",EDGE,"E3"),sQuery(id+"F0.wireOp",EDGE,"E4"),sQuery(id+"F0.wireOp",EDGE,"E5"),sQuery(id+"F0.wireOp",EDGE,"E6"),sQuery(id+"F0.wireOp",EDGE,"E7")])]})});
            var Q4;
            Q4=makeQuery(id+"F3.boolean.opBoolean","SPLIT",BODY,{"disambiguationData":[OD(5.0)],"derivedFrom":makeQuery(id+"F2.opExtrude","SWEPT_BODY",BODY,{"disambiguationData":[OSD([sQuery(id+"F0.wireOp",EDGE,"E0"),sQuery(id+"F0.wireOp",EDGE,"E1"),sQuery(id+"F0.wireOp",EDGE,"E2"),sQuery(id+"F0.wireOp",EDGE,"E3"),sQuery(id+"F0.wireOp",EDGE,"E4"),sQuery(id+"F0.wireOp",EDGE,"E5"),sQuery(id+"F0.wireOp",EDGE,"E6"),sQuery(id+"F0.wireOp",EDGE,"E7")])]})});
            var Q5;
            Q5=makeQuery(id+"F3.boolean.opBoolean","SPLIT",BODY,{"disambiguationData":[OD(9.0)],"derivedFrom":makeQuery(id+"F2.opExtrude","SWEPT_BODY",BODY,{"disambiguationData":[OSD([sQuery(id+"F0.wireOp",EDGE,"E0"),sQuery(id+"F0.wireOp",EDGE,"E1"),sQuery(id+"F0.wireOp",EDGE,"E2"),sQuery(id+"F0.wireOp",EDGE,"E3"),sQuery(id+"F0.wireOp",EDGE,"E4"),sQuery(id+"F0.wireOp",EDGE,"E5"),sQuery(id+"F0.wireOp",EDGE,"E6"),sQuery(id+"F0.wireOp",EDGE,"E7")])]})});
            var Q6;
            Q6=makeQuery(id+"F3.boolean.opBoolean","SPLIT",BODY,{"disambiguationData":[OD(14.0)],"derivedFrom":makeQuery(id+"F2.opExtrude","SWEPT_BODY",BODY,{"disambiguationData":[OSD([sQuery(id+"F0.wireOp",EDGE,"E0"),sQuery(id+"F0.wireOp",EDGE,"E1"),sQuery(id+"F0.wireOp",EDGE,"E2"),sQuery(id+"F0.wireOp",EDGE,"E3"),sQuery(id+"F0.wireOp",EDGE,"E4"),sQuery(id+"F0.wireOp",EDGE,"E5"),sQuery(id+"F0.wireOp",EDGE,"E6"),sQuery(id+"F0.wireOp",EDGE,"E7")])]})});
            var Q7;
            Q7=makeQuery(id+"F3.boolean.opBoolean","SPLIT",BODY,{"disambiguationData":[OD(1.0)],"derivedFrom":makeQuery(id+"F2.opExtrude","SWEPT_BODY",BODY,{"disambiguationData":[OSD([sQuery(id+"F0.wireOp",EDGE,"E0"),sQuery(id+"F0.wireOp",EDGE,"E1"),sQuery(id+"F0.wireOp",EDGE,"E2"),sQuery(id+"F0.wireOp",EDGE,"E3"),sQuery(id+"F0.wireOp",EDGE,"E4"),sQuery(id+"F0.wireOp",EDGE,"E5"),sQuery(id+"F0.wireOp",EDGE,"E6"),sQuery(id+"F0.wireOp",EDGE,"E7")])]})});
            var Q8;
            Q8=makeQuery(id+"F3.boolean.opBoolean","SPLIT",BODY,{"disambiguationData":[OD(6.0)],"derivedFrom":makeQuery(id+"F2.opExtrude","SWEPT_BODY",BODY,{"disambiguationData":[OSD([sQuery(id+"F0.wireOp",EDGE,"E0"),sQuery(id+"F0.wireOp",EDGE,"E1"),sQuery(id+"F0.wireOp",EDGE,"E2"),sQuery(id+"F0.wireOp",EDGE,"E3"),sQuery(id+"F0.wireOp",EDGE,"E4"),sQuery(id+"F0.wireOp",EDGE,"E5"),sQuery(id+"F0.wireOp",EDGE,"E6"),sQuery(id+"F0.wireOp",EDGE,"E7")])]})});
            var Q9;
            Q9=makeQuery(id+"F3.boolean.opBoolean","SPLIT",BODY,{"disambiguationData":[OD(7.0)],"derivedFrom":makeQuery(id+"F2.opExtrude","SWEPT_BODY",BODY,{"disambiguationData":[OSD([sQuery(id+"F0.wireOp",EDGE,"E0"),sQuery(id+"F0.wireOp",EDGE,"E1"),sQuery(id+"F0.wireOp",EDGE,"E2"),sQuery(id+"F0.wireOp",EDGE,"E3"),sQuery(id+"F0.wireOp",EDGE,"E4"),sQuery(id+"F0.wireOp",EDGE,"E5"),sQuery(id+"F0.wireOp",EDGE,"E6"),sQuery(id+"F0.wireOp",EDGE,"E7")])]})});
            var Q10;
            Q10=makeQuery(id+"F3.boolean.opBoolean","SPLIT",BODY,{"disambiguationData":[OD(8.0)],"derivedFrom":makeQuery(id+"F2.opExtrude","SWEPT_BODY",BODY,{"disambiguationData":[OSD([sQuery(id+"F0.wireOp",EDGE,"E0"),sQuery(id+"F0.wireOp",EDGE,"E1"),sQuery(id+"F0.wireOp",EDGE,"E2"),sQuery(id+"F0.wireOp",EDGE,"E3"),sQuery(id+"F0.wireOp",EDGE,"E4"),sQuery(id+"F0.wireOp",EDGE,"E5"),sQuery(id+"F0.wireOp",EDGE,"E6"),sQuery(id+"F0.wireOp",EDGE,"E7")])]})});
            var Q11;
            Q11=makeQuery(id+"F3.boolean.opBoolean","SPLIT",BODY,{"disambiguationData":[OD(10.0)],"derivedFrom":makeQuery(id+"F2.opExtrude","SWEPT_BODY",BODY,{"disambiguationData":[OSD([sQuery(id+"F0.wireOp",EDGE,"E0"),sQuery(id+"F0.wireOp",EDGE,"E1"),sQuery(id+"F0.wireOp",EDGE,"E2"),sQuery(id+"F0.wireOp",EDGE,"E3"),sQuery(id+"F0.wireOp",EDGE,"E4"),sQuery(id+"F0.wireOp",EDGE,"E5"),sQuery(id+"F0.wireOp",EDGE,"E6"),sQuery(id+"F0.wireOp",EDGE,"E7")])]})});
            var Q12;
            Q12=makeQuery(id+"F3.boolean.opBoolean","SPLIT",BODY,{"disambiguationData":[OD(11.0)],"derivedFrom":makeQuery(id+"F2.opExtrude","SWEPT_BODY",BODY,{"disambiguationData":[OSD([sQuery(id+"F0.wireOp",EDGE,"E0"),sQuery(id+"F0.wireOp",EDGE,"E1"),sQuery(id+"F0.wireOp",EDGE,"E2"),sQuery(id+"F0.wireOp",EDGE,"E3"),sQuery(id+"F0.wireOp",EDGE,"E4"),sQuery(id+"F0.wireOp",EDGE,"E5"),sQuery(id+"F0.wireOp",EDGE,"E6"),sQuery(id+"F0.wireOp",EDGE,"E7")])]})});
            var Q13;
            Q13=makeQuery(id+"F3.boolean.opBoolean","SPLIT",BODY,{"disambiguationData":[OD(12.0)],"derivedFrom":makeQuery(id+"F2.opExtrude","SWEPT_BODY",BODY,{"disambiguationData":[OSD([sQuery(id+"F0.wireOp",EDGE,"E0"),sQuery(id+"F0.wireOp",EDGE,"E1"),sQuery(id+"F0.wireOp",EDGE,"E2"),sQuery(id+"F0.wireOp",EDGE,"E3"),sQuery(id+"F0.wireOp",EDGE,"E4"),sQuery(id+"F0.wireOp",EDGE,"E5"),sQuery(id+"F0.wireOp",EDGE,"E6"),sQuery(id+"F0.wireOp",EDGE,"E7")])]})});
            var Q14;
            Q14=makeQuery(id+"F3.boolean.opBoolean","SPLIT",BODY,{"disambiguationData":[OD(13.0)],"derivedFrom":makeQuery(id+"F2.opExtrude","SWEPT_BODY",BODY,{"disambiguationData":[OSD([sQuery(id+"F0.wireOp",EDGE,"E0"),sQuery(id+"F0.wireOp",EDGE,"E1"),sQuery(id+"F0.wireOp",EDGE,"E2"),sQuery(id+"F0.wireOp",EDGE,"E3"),sQuery(id+"F0.wireOp",EDGE,"E4"),sQuery(id+"F0.wireOp",EDGE,"E5"),sQuery(id+"F0.wireOp",EDGE,"E6"),sQuery(id+"F0.wireOp",EDGE,"E7")])]})});
            var Q15;
            Q15=makeQuery(id+"F2.opExtrude","CAP_EDGE",EDGE,{"disambiguationData":[OSD([sQuery(id+"F0.wireOp",EDGE,"E3")])],"isStart":true});
            transform(context, id + "F4", {"entities" : qUnion([Q0, Q1, Q2, Q3, Q4, Q5, Q6, Q7, Q8, Q9, Q10, Q11, Q12, Q13, Q14]), "transformType" : TransformType.ROTATION, "transformAxis" : qUnion([Q15]), "angle" : 180 * degree, "makeCopy" : false});
        }
    });
